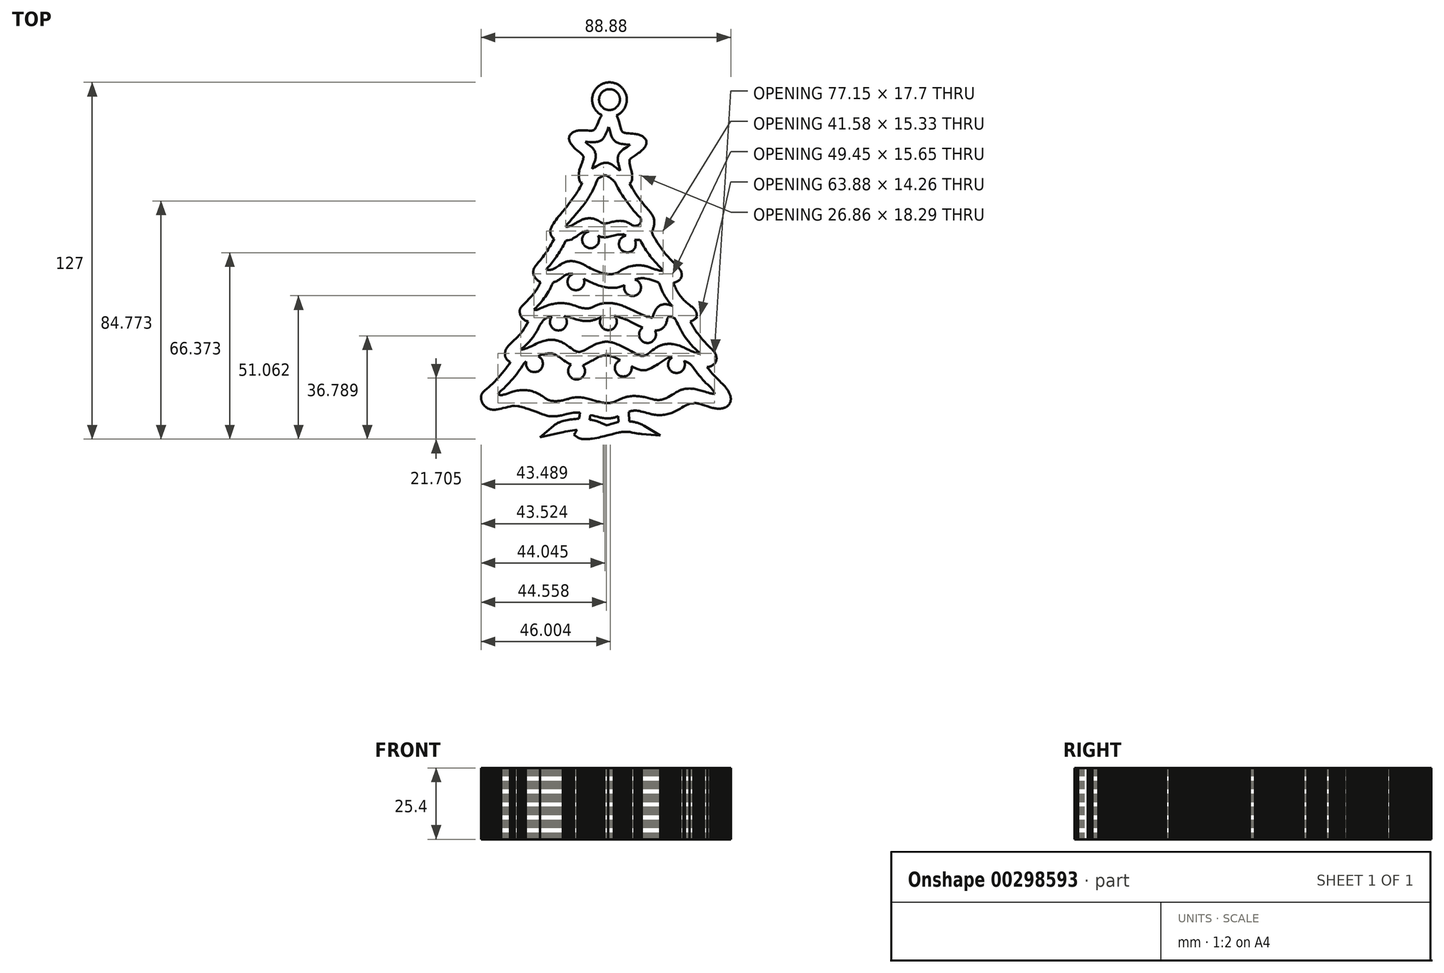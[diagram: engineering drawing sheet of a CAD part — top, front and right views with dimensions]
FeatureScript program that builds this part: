
annotation { "Feature Type Name" : "Feature", "Feature Type Description" : "" }
export const myFeature = defineFeature(function(context is Context, id is Id, definition is map)
    precondition{}
    {
        {
            var Q0;
            Q0=qCreatedBy(makeId("Top.planeOp"),FACE);
            var sketch = newSketch(context, id + "F0", { "sketchPlane" : qUnion([Q0])});
            skLineSegment(sketch, "E0", {"start": v(-10.31, -60.2) * mm, "end": v(-10.71, -60.23) * mm});
            skLineSegment(sketch, "E1", {"start": v(-10.71, -60.23) * mm, "end": v(-11.12, -60.26) * mm});
            skLineSegment(sketch, "E2", {"start": v(-11.12, -60.26) * mm, "end": v(-11.93, -60.35) * mm});
            skLineSegment(sketch, "E3", {"start": v(-11.93, -60.35) * mm, "end": v(-12.75, -60.48) * mm});
            skLineSegment(sketch, "E4", {"start": v(-12.75, -60.48) * mm, "end": v(-13.6, -60.62) * mm});
            skLineSegment(sketch, "E5", {"start": v(-13.6, -60.62) * mm, "end": v(-14.47, -60.8) * mm});
            skLineSegment(sketch, "E6", {"start": v(-14.47, -60.8) * mm, "end": v(-15.37, -60.98) * mm});
            skLineSegment(sketch, "E7", {"start": v(-15.37, -60.98) * mm, "end": v(-17.3, -61.4) * mm});
            skLineSegment(sketch, "E8", {"start": v(-17.3, -61.4) * mm, "end": v(-23.47, -62.8) * mm});
            skLineSegment(sketch, "E9", {"start": v(-23.47, -62.8) * mm, "end": v(-18.63, -58.71) * mm});
            skLineSegment(sketch, "E10", {"start": v(-18.63, -58.71) * mm, "end": v(-18.42, -58.54) * mm});
            skLineSegment(sketch, "E11", {"start": v(-18.42, -58.54) * mm, "end": v(-18.2, -58.38) * mm});
            skLineSegment(sketch, "E12", {"start": v(-18.2, -58.38) * mm, "end": v(-17.97, -58.22) * mm});
            skLineSegment(sketch, "E13", {"start": v(-17.97, -58.22) * mm, "end": v(-17.73, -58.07) * mm});
            skLineSegment(sketch, "E14", {"start": v(-17.73, -58.07) * mm, "end": v(-17.49, -57.93) * mm});
            skLineSegment(sketch, "E15", {"start": v(-17.49, -57.93) * mm, "end": v(-17.24, -57.8) * mm});
            skLineSegment(sketch, "E16", {"start": v(-17.24, -57.8) * mm, "end": v(-16.98, -57.67) * mm});
            skLineSegment(sketch, "E17", {"start": v(-16.98, -57.67) * mm, "end": v(-16.72, -57.55) * mm});
            skLineSegment(sketch, "E18", {"start": v(-16.72, -57.55) * mm, "end": v(-16.45, -57.44) * mm});
            skLineSegment(sketch, "E19", {"start": v(-16.45, -57.44) * mm, "end": v(-16.18, -57.33) * mm});
            skLineSegment(sketch, "E20", {"start": v(-16.18, -57.33) * mm, "end": v(-15.61, -57.14) * mm});
            skLineSegment(sketch, "E21", {"start": v(-15.61, -57.14) * mm, "end": v(-15.03, -56.96) * mm});
            skLineSegment(sketch, "E22", {"start": v(-15.03, -56.96) * mm, "end": v(-14.44, -56.82) * mm});
            skLineSegment(sketch, "E23", {"start": v(-14.44, -56.82) * mm, "end": v(-13.84, -56.69) * mm});
            skLineSegment(sketch, "E24", {"start": v(-13.84, -56.69) * mm, "end": v(-13.23, -56.58) * mm});
            skLineSegment(sketch, "E25", {"start": v(-13.23, -56.58) * mm, "end": v(-12.62, -56.49) * mm});
            skLineSegment(sketch, "E26", {"start": v(-12.62, -56.49) * mm, "end": v(-12, -56.41) * mm});
            skLineSegment(sketch, "E27", {"start": v(-12, -56.41) * mm, "end": v(-11.4, -56.35) * mm});
            skLineSegment(sketch, "E28", {"start": v(-11.4, -56.35) * mm, "end": v(-10.8, -56.3) * mm});
            skLineSegment(sketch, "E29", {"start": v(-10.8, -56.3) * mm, "end": v(-10.2, -56.27) * mm});
            skLineSegment(sketch, "E30", {"start": v(-10.2, -56.27) * mm, "end": v(-9.62, -56.25) * mm});
            skLineSegment(sketch, "E31", {"start": v(-9.62, -56.25) * mm, "end": v(-9.36, -55.07) * mm});
            skLineSegment(sketch, "E32", {"start": v(-9.36, -55.07) * mm, "end": v(-9.2, -54.1) * mm});
            skLineSegment(sketch, "E33", {"start": v(-9.2, -54.1) * mm, "end": v(-9.5, -54.06) * mm});
            skLineSegment(sketch, "E34", {"start": v(-9.5, -54.06) * mm, "end": v(-9.81, -54.04) * mm});
            skLineSegment(sketch, "E35", {"start": v(-9.81, -54.04) * mm, "end": v(-10.11, -54.02) * mm});
            skLineSegment(sketch, "E36", {"start": v(-10.11, -54.02) * mm, "end": v(-10.41, -54.02) * mm});
            skLineSegment(sketch, "E37", {"start": v(-10.41, -54.02) * mm, "end": v(-10.7, -54.02) * mm});
            skLineSegment(sketch, "E38", {"start": v(-10.7, -54.02) * mm, "end": v(-11, -54.03) * mm});
            skLineSegment(sketch, "E39", {"start": v(-11, -54.03) * mm, "end": v(-11.29, -54.06) * mm});
            skLineSegment(sketch, "E40", {"start": v(-11.29, -54.06) * mm, "end": v(-11.58, -54.09) * mm});
            skLineSegment(sketch, "E41", {"start": v(-11.58, -54.09) * mm, "end": v(-12.17, -54.17) * mm});
            skLineSegment(sketch, "E42", {"start": v(-12.17, -54.17) * mm, "end": v(-12.78, -54.29) * mm});
            skLineSegment(sketch, "E43", {"start": v(-12.78, -54.29) * mm, "end": v(-13.41, -54.44) * mm});
            skLineSegment(sketch, "E44", {"start": v(-13.41, -54.44) * mm, "end": v(-14.09, -54.6) * mm});
            skLineSegment(sketch, "E45", {"start": v(-14.09, -54.6) * mm, "end": v(-14.96, -54.83) * mm});
            skLineSegment(sketch, "E46", {"start": v(-14.96, -54.83) * mm, "end": v(-15.79, -55.03) * mm});
            skLineSegment(sketch, "E47", {"start": v(-15.79, -55.03) * mm, "end": v(-16.2, -55.1) * mm});
            skLineSegment(sketch, "E48", {"start": v(-16.2, -55.1) * mm, "end": v(-16.6, -55.18) * mm});
            skLineSegment(sketch, "E49", {"start": v(-16.6, -55.18) * mm, "end": v(-17, -55.25) * mm});
            skLineSegment(sketch, "E50", {"start": v(-17, -55.25) * mm, "end": v(-17.39, -55.3) * mm});
            skLineSegment(sketch, "E51", {"start": v(-17.39, -55.3) * mm, "end": v(-17.79, -55.34) * mm});
            skLineSegment(sketch, "E52", {"start": v(-17.79, -55.34) * mm, "end": v(-18.19, -55.37) * mm});
            skLineSegment(sketch, "E53", {"start": v(-18.19, -55.37) * mm, "end": v(-18.6, -55.38) * mm});
            skLineSegment(sketch, "E54", {"start": v(-18.6, -55.38) * mm, "end": v(-19.01, -55.38) * mm});
            skLineSegment(sketch, "E55", {"start": v(-19.01, -55.38) * mm, "end": v(-19.43, -55.37) * mm});
            skLineSegment(sketch, "E56", {"start": v(-19.43, -55.37) * mm, "end": v(-19.87, -55.34) * mm});
            skLineSegment(sketch, "E57", {"start": v(-19.87, -55.34) * mm, "end": v(-20.32, -55.3) * mm});
            skLineSegment(sketch, "E58", {"start": v(-20.32, -55.3) * mm, "end": v(-20.78, -55.24) * mm});
            skLineSegment(sketch, "E59", {"start": v(-20.78, -55.24) * mm, "end": v(-20.99, -55.2) * mm});
            skLineSegment(sketch, "E60", {"start": v(-20.99, -55.2) * mm, "end": v(-21.2, -55.13) * mm});
            skLineSegment(sketch, "E61", {"start": v(-21.2, -55.13) * mm, "end": v(-21.62, -54.98) * mm});
            skLineSegment(sketch, "E62", {"start": v(-21.62, -54.98) * mm, "end": v(-22.85, -54.52) * mm});
            skLineSegment(sketch, "E63", {"start": v(-22.85, -54.52) * mm, "end": v(-24.67, -53.85) * mm});
            skLineSegment(sketch, "E64", {"start": v(-24.67, -53.85) * mm, "end": v(-26.49, -53.2) * mm});
            skLineSegment(sketch, "E65", {"start": v(-26.49, -53.2) * mm, "end": v(-27.5, -52.83) * mm});
            skLineSegment(sketch, "E66", {"start": v(-27.5, -52.83) * mm, "end": v(-28.55, -52.48) * mm});
            skLineSegment(sketch, "E67", {"start": v(-28.55, -52.48) * mm, "end": v(-29.08, -52.3) * mm});
            skLineSegment(sketch, "E68", {"start": v(-29.08, -52.3) * mm, "end": v(-29.6, -52.14) * mm});
            skLineSegment(sketch, "E69", {"start": v(-29.6, -52.14) * mm, "end": v(-30.13, -52) * mm});
            skLineSegment(sketch, "E70", {"start": v(-30.13, -52) * mm, "end": v(-30.65, -51.85) * mm});
            skLineSegment(sketch, "E71", {"start": v(-30.65, -51.85) * mm, "end": v(-30.73, -51.83) * mm});
            skLineSegment(sketch, "E72", {"start": v(-30.73, -51.83) * mm, "end": v(-30.97, -51.78) * mm});
            skLineSegment(sketch, "E73", {"start": v(-30.97, -51.78) * mm, "end": v(-31.23, -51.73) * mm});
            skLineSegment(sketch, "E74", {"start": v(-31.23, -51.73) * mm, "end": v(-31.35, -51.76) * mm});
            skLineSegment(sketch, "E75", {"start": v(-31.35, -51.76) * mm, "end": v(-32.54, -51.6) * mm});
            skLineSegment(sketch, "E76", {"start": v(-32.54, -51.6) * mm, "end": v(-32.92, -51.64) * mm});
            skLineSegment(sketch, "E77", {"start": v(-32.92, -51.64) * mm, "end": v(-33.3, -51.7) * mm});
            skLineSegment(sketch, "E78", {"start": v(-33.3, -51.7) * mm, "end": v(-33.71, -51.78) * mm});
            skLineSegment(sketch, "E79", {"start": v(-33.71, -51.78) * mm, "end": v(-34.12, -51.86) * mm});
            skLineSegment(sketch, "E80", {"start": v(-34.12, -51.86) * mm, "end": v(-34.92, -52.05) * mm});
            skLineSegment(sketch, "E81", {"start": v(-34.92, -52.05) * mm, "end": v(-35.67, -52.22) * mm});
            skLineSegment(sketch, "E82", {"start": v(-35.67, -52.22) * mm, "end": v(-36.7, -52.47) * mm});
            skLineSegment(sketch, "E83", {"start": v(-36.7, -52.47) * mm, "end": v(-37.34, -52.62) * mm});
            skLineSegment(sketch, "E84", {"start": v(-37.34, -52.62) * mm, "end": v(-38.02, -52.77) * mm});
            skLineSegment(sketch, "E85", {"start": v(-38.02, -52.77) * mm, "end": v(-38.7, -52.9) * mm});
            skLineSegment(sketch, "E86", {"start": v(-38.7, -52.9) * mm, "end": v(-39.02, -52.95) * mm});
            skLineSegment(sketch, "E87", {"start": v(-39.02, -52.95) * mm, "end": v(-39.33, -53) * mm});
            skLineSegment(sketch, "E88", {"start": v(-39.33, -53) * mm, "end": v(-39.62, -53.03) * mm});
            skLineSegment(sketch, "E89", {"start": v(-39.62, -53.03) * mm, "end": v(-39.89, -53.04) * mm});
            skLineSegment(sketch, "E90", {"start": v(-39.89, -53.04) * mm, "end": v(-40.12, -53.04) * mm});
            skLineSegment(sketch, "E91", {"start": v(-40.12, -53.04) * mm, "end": v(-40.32, -53.02) * mm});
            skLineSegment(sketch, "E92", {"start": v(-40.32, -53.02) * mm, "end": v(-40.7, -52.95) * mm});
            skLineSegment(sketch, "E93", {"start": v(-40.7, -52.95) * mm, "end": v(-41.06, -52.86) * mm});
            skLineSegment(sketch, "E94", {"start": v(-41.06, -52.86) * mm, "end": v(-41.42, -52.75) * mm});
            skLineSegment(sketch, "E95", {"start": v(-41.42, -52.75) * mm, "end": v(-41.76, -52.63) * mm});
            skLineSegment(sketch, "E96", {"start": v(-41.76, -52.63) * mm, "end": v(-42.08, -52.48) * mm});
            skLineSegment(sketch, "E97", {"start": v(-42.08, -52.48) * mm, "end": v(-42.4, -52.31) * mm});
            skLineSegment(sketch, "E98", {"start": v(-42.4, -52.31) * mm, "end": v(-42.69, -52.13) * mm});
            skLineSegment(sketch, "E99", {"start": v(-42.69, -52.13) * mm, "end": v(-42.96, -51.92) * mm});
            skLineSegment(sketch, "E100", {"start": v(-42.96, -51.92) * mm, "end": v(-43.22, -51.7) * mm});
            skLineSegment(sketch, "E101", {"start": v(-43.22, -51.7) * mm, "end": v(-43.34, -51.57) * mm});
            skLineSegment(sketch, "E102", {"start": v(-43.34, -51.57) * mm, "end": v(-43.45, -51.44) * mm});
            skLineSegment(sketch, "E103", {"start": v(-43.45, -51.44) * mm, "end": v(-43.56, -51.31) * mm});
            skLineSegment(sketch, "E104", {"start": v(-43.56, -51.31) * mm, "end": v(-43.67, -51.17) * mm});
            skLineSegment(sketch, "E105", {"start": v(-43.67, -51.17) * mm, "end": v(-43.77, -51.03) * mm});
            skLineSegment(sketch, "E106", {"start": v(-43.77, -51.03) * mm, "end": v(-43.86, -50.88) * mm});
            skLineSegment(sketch, "E107", {"start": v(-43.86, -50.88) * mm, "end": v(-43.94, -50.72) * mm});
            skLineSegment(sketch, "E108", {"start": v(-43.94, -50.72) * mm, "end": v(-44.02, -50.56) * mm});
            skLineSegment(sketch, "E109", {"start": v(-44.02, -50.56) * mm, "end": v(-44.1, -50.4) * mm});
            skLineSegment(sketch, "E110", {"start": v(-44.1, -50.4) * mm, "end": v(-44.16, -50.22) * mm});
            skLineSegment(sketch, "E111", {"start": v(-44.16, -50.22) * mm, "end": v(-44.22, -50.04) * mm});
            skLineSegment(sketch, "E112", {"start": v(-44.22, -50.04) * mm, "end": v(-44.28, -49.86) * mm});
            skLineSegment(sketch, "E113", {"start": v(-44.28, -49.86) * mm, "end": v(-44.32, -49.67) * mm});
            skLineSegment(sketch, "E114", {"start": v(-44.32, -49.67) * mm, "end": v(-44.36, -49.47) * mm});
            skLineSegment(sketch, "E115", {"start": v(-44.36, -49.47) * mm, "end": v(-44.4, -49.25) * mm});
            skLineSegment(sketch, "E116", {"start": v(-44.4, -49.25) * mm, "end": v(-44.42, -49.04) * mm});
            skLineSegment(sketch, "E117", {"start": v(-44.42, -49.04) * mm, "end": v(-44.44, -48.84) * mm});
            skLineSegment(sketch, "E118", {"start": v(-44.44, -48.84) * mm, "end": v(-44.44, -48.65) * mm});
            skLineSegment(sketch, "E119", {"start": v(-44.44, -48.65) * mm, "end": v(-44.44, -48.47) * mm});
            skLineSegment(sketch, "E120", {"start": v(-44.44, -48.47) * mm, "end": v(-44.43, -48.3) * mm});
            skLineSegment(sketch, "E121", {"start": v(-44.43, -48.3) * mm, "end": v(-44.4, -48.13) * mm});
            skLineSegment(sketch, "E122", {"start": v(-44.4, -48.13) * mm, "end": v(-44.38, -47.98) * mm});
            skLineSegment(sketch, "E123", {"start": v(-44.38, -47.98) * mm, "end": v(-44.34, -47.83) * mm});
            skLineSegment(sketch, "E124", {"start": v(-44.34, -47.83) * mm, "end": v(-44.3, -47.69) * mm});
            skLineSegment(sketch, "E125", {"start": v(-44.3, -47.69) * mm, "end": v(-44.25, -47.55) * mm});
            skLineSegment(sketch, "E126", {"start": v(-44.25, -47.55) * mm, "end": v(-44.19, -47.42) * mm});
            skLineSegment(sketch, "E127", {"start": v(-44.19, -47.42) * mm, "end": v(-44.12, -47.3) * mm});
            skLineSegment(sketch, "E128", {"start": v(-44.12, -47.3) * mm, "end": v(-44.05, -47.18) * mm});
            skLineSegment(sketch, "E129", {"start": v(-44.05, -47.18) * mm, "end": v(-43.89, -46.95) * mm});
            skLineSegment(sketch, "E130", {"start": v(-43.89, -46.95) * mm, "end": v(-43.7, -46.73) * mm});
            skLineSegment(sketch, "E131", {"start": v(-43.7, -46.73) * mm, "end": v(-43.5, -46.52) * mm});
            skLineSegment(sketch, "E132", {"start": v(-43.5, -46.52) * mm, "end": v(-43.27, -46.31) * mm});
            skLineSegment(sketch, "E133", {"start": v(-43.27, -46.31) * mm, "end": v(-43.03, -46.1) * mm});
            skLineSegment(sketch, "E134", {"start": v(-43.03, -46.1) * mm, "end": v(-42.5, -45.67) * mm});
            skLineSegment(sketch, "E135", {"start": v(-42.5, -45.67) * mm, "end": v(-42.23, -45.43) * mm});
            skLineSegment(sketch, "E136", {"start": v(-42.23, -45.43) * mm, "end": v(-41.94, -45.18) * mm});
            skLineSegment(sketch, "E137", {"start": v(-41.94, -45.18) * mm, "end": v(-41.17, -44.45) * mm});
            skLineSegment(sketch, "E138", {"start": v(-41.17, -44.45) * mm, "end": v(-40.4, -43.7) * mm});
            skLineSegment(sketch, "E139", {"start": v(-40.4, -43.7) * mm, "end": v(-39.64, -42.96) * mm});
            skLineSegment(sketch, "E140", {"start": v(-39.64, -42.96) * mm, "end": v(-38.9, -42.2) * mm});
            skLineSegment(sketch, "E141", {"start": v(-38.9, -42.2) * mm, "end": v(-38.22, -41.47) * mm});
            skLineSegment(sketch, "E142", {"start": v(-38.22, -41.47) * mm, "end": v(-37.56, -40.73) * mm});
            skLineSegment(sketch, "E143", {"start": v(-37.56, -40.73) * mm, "end": v(-36.92, -39.98) * mm});
            skLineSegment(sketch, "E144", {"start": v(-36.92, -39.98) * mm, "end": v(-36.3, -39.22) * mm});
            skLineSegment(sketch, "E145", {"start": v(-36.3, -39.22) * mm, "end": v(-35.7, -38.45) * mm});
            skLineSegment(sketch, "E146", {"start": v(-35.7, -38.45) * mm, "end": v(-35.1, -37.67) * mm});
            skLineSegment(sketch, "E147", {"start": v(-35.1, -37.67) * mm, "end": v(-34.53, -36.88) * mm});
            skLineSegment(sketch, "E148", {"start": v(-34.53, -36.88) * mm, "end": v(-33.96, -36.07) * mm});
            skLineSegment(sketch, "E149", {"start": v(-33.96, -36.07) * mm, "end": v(-34.16, -35.98) * mm});
            skLineSegment(sketch, "E150", {"start": v(-34.16, -35.98) * mm, "end": v(-34.34, -35.9) * mm});
            skLineSegment(sketch, "E151", {"start": v(-34.34, -35.9) * mm, "end": v(-34.52, -35.8) * mm});
            skLineSegment(sketch, "E152", {"start": v(-34.52, -35.8) * mm, "end": v(-34.68, -35.68) * mm});
            skLineSegment(sketch, "E153", {"start": v(-34.68, -35.68) * mm, "end": v(-34.84, -35.57) * mm});
            skLineSegment(sketch, "E154", {"start": v(-34.84, -35.57) * mm, "end": v(-34.98, -35.45) * mm});
            skLineSegment(sketch, "E155", {"start": v(-34.98, -35.45) * mm, "end": v(-35.12, -35.32) * mm});
            skLineSegment(sketch, "E156", {"start": v(-35.12, -35.32) * mm, "end": v(-35.24, -35.2) * mm});
            skLineSegment(sketch, "E157", {"start": v(-35.24, -35.2) * mm, "end": v(-35.35, -35.05) * mm});
            skLineSegment(sketch, "E158", {"start": v(-35.35, -35.05) * mm, "end": v(-35.46, -34.91) * mm});
            skLineSegment(sketch, "E159", {"start": v(-35.46, -34.91) * mm, "end": v(-35.55, -34.76) * mm});
            skLineSegment(sketch, "E160", {"start": v(-35.55, -34.76) * mm, "end": v(-35.64, -34.61) * mm});
            skLineSegment(sketch, "E161", {"start": v(-35.64, -34.61) * mm, "end": v(-35.71, -34.46) * mm});
            skLineSegment(sketch, "E162", {"start": v(-35.71, -34.46) * mm, "end": v(-35.78, -34.3) * mm});
            skLineSegment(sketch, "E163", {"start": v(-35.78, -34.3) * mm, "end": v(-35.83, -34.13) * mm});
            skLineSegment(sketch, "E164", {"start": v(-35.83, -34.13) * mm, "end": v(-35.88, -33.96) * mm});
            skLineSegment(sketch, "E165", {"start": v(-35.88, -33.96) * mm, "end": v(-35.91, -33.8) * mm});
            skLineSegment(sketch, "E166", {"start": v(-35.91, -33.8) * mm, "end": v(-35.94, -33.62) * mm});
            skLineSegment(sketch, "E167", {"start": v(-35.94, -33.62) * mm, "end": v(-35.95, -33.44) * mm});
            skLineSegment(sketch, "E168", {"start": v(-35.95, -33.44) * mm, "end": v(-35.96, -33.26) * mm});
            skLineSegment(sketch, "E169", {"start": v(-35.96, -33.26) * mm, "end": v(-35.96, -33.08) * mm});
            skLineSegment(sketch, "E170", {"start": v(-35.96, -33.08) * mm, "end": v(-35.94, -32.9) * mm});
            skLineSegment(sketch, "E171", {"start": v(-35.94, -32.9) * mm, "end": v(-35.92, -32.7) * mm});
            skLineSegment(sketch, "E172", {"start": v(-35.92, -32.7) * mm, "end": v(-35.89, -32.52) * mm});
            skLineSegment(sketch, "E173", {"start": v(-35.89, -32.52) * mm, "end": v(-35.85, -32.33) * mm});
            skLineSegment(sketch, "E174", {"start": v(-35.85, -32.33) * mm, "end": v(-35.8, -32.14) * mm});
            skLineSegment(sketch, "E175", {"start": v(-35.8, -32.14) * mm, "end": v(-35.73, -31.95) * mm});
            skLineSegment(sketch, "E176", {"start": v(-35.73, -31.95) * mm, "end": v(-35.66, -31.76) * mm});
            skLineSegment(sketch, "E177", {"start": v(-35.66, -31.76) * mm, "end": v(-35.58, -31.57) * mm});
            skLineSegment(sketch, "E178", {"start": v(-35.58, -31.57) * mm, "end": v(-35.5, -31.38) * mm});
            skLineSegment(sketch, "E179", {"start": v(-35.5, -31.38) * mm, "end": v(-35.4, -31.19) * mm});
            skLineSegment(sketch, "E180", {"start": v(-35.4, -31.19) * mm, "end": v(-35.28, -31) * mm});
            skLineSegment(sketch, "E181", {"start": v(-35.28, -31) * mm, "end": v(-35.19, -30.85) * mm});
            skLineSegment(sketch, "E182", {"start": v(-35.19, -30.85) * mm, "end": v(-35.07, -30.69) * mm});
            skLineSegment(sketch, "E183", {"start": v(-35.07, -30.69) * mm, "end": v(-34.8, -30.36) * mm});
            skLineSegment(sketch, "E184", {"start": v(-34.8, -30.36) * mm, "end": v(-34.5, -30.02) * mm});
            skLineSegment(sketch, "E185", {"start": v(-34.5, -30.02) * mm, "end": v(-34.17, -29.68) * mm});
            skLineSegment(sketch, "E186", {"start": v(-34.17, -29.68) * mm, "end": v(-33.49, -29.02) * mm});
            skLineSegment(sketch, "E187", {"start": v(-33.49, -29.02) * mm, "end": v(-32.9, -28.46) * mm});
            skLineSegment(sketch, "E188", {"start": v(-32.9, -28.46) * mm, "end": v(-31.9, -27.52) * mm});
            skLineSegment(sketch, "E189", {"start": v(-31.9, -27.52) * mm, "end": v(-31.4, -27.04) * mm});
            skLineSegment(sketch, "E190", {"start": v(-31.4, -27.04) * mm, "end": v(-30.9, -26.56) * mm});
            skLineSegment(sketch, "E191", {"start": v(-30.9, -26.56) * mm, "end": v(-30.61, -26.24) * mm});
            skLineSegment(sketch, "E192", {"start": v(-30.61, -26.24) * mm, "end": v(-30.32, -25.87) * mm});
            skLineSegment(sketch, "E193", {"start": v(-30.32, -25.87) * mm, "end": v(-30.02, -25.48) * mm});
            skLineSegment(sketch, "E194", {"start": v(-30.02, -25.48) * mm, "end": v(-29.73, -25.07) * mm});
            skLineSegment(sketch, "E195", {"start": v(-29.73, -25.07) * mm, "end": v(-29.19, -24.23) * mm});
            skLineSegment(sketch, "E196", {"start": v(-29.19, -24.23) * mm, "end": v(-28.7, -23.46) * mm});
            skLineSegment(sketch, "E197", {"start": v(-28.7, -23.46) * mm, "end": v(-28.16, -22.56) * mm});
            skLineSegment(sketch, "E198", {"start": v(-28.16, -22.56) * mm, "end": v(-27.61, -21.63) * mm});
            skLineSegment(sketch, "E199", {"start": v(-27.61, -21.63) * mm, "end": v(-27.88, -21.55) * mm});
            skLineSegment(sketch, "E200", {"start": v(-27.88, -21.55) * mm, "end": v(-28.14, -21.46) * mm});
            skLineSegment(sketch, "E201", {"start": v(-28.14, -21.46) * mm, "end": v(-28.4, -21.36) * mm});
            skLineSegment(sketch, "E202", {"start": v(-28.4, -21.36) * mm, "end": v(-28.64, -21.25) * mm});
            skLineSegment(sketch, "E203", {"start": v(-28.64, -21.25) * mm, "end": v(-28.89, -21.12) * mm});
            skLineSegment(sketch, "E204", {"start": v(-28.89, -21.12) * mm, "end": v(-29.13, -20.97) * mm});
            skLineSegment(sketch, "E205", {"start": v(-29.13, -20.97) * mm, "end": v(-29.36, -20.8) * mm});
            skLineSegment(sketch, "E206", {"start": v(-29.36, -20.8) * mm, "end": v(-29.58, -20.62) * mm});
            skLineSegment(sketch, "E207", {"start": v(-29.58, -20.62) * mm, "end": v(-29.74, -20.47) * mm});
            skLineSegment(sketch, "E208", {"start": v(-29.74, -20.47) * mm, "end": v(-29.88, -20.31) * mm});
            skLineSegment(sketch, "E209", {"start": v(-29.88, -20.31) * mm, "end": v(-30, -20.15) * mm});
            skLineSegment(sketch, "E210", {"start": v(-30, -20.15) * mm, "end": v(-30.12, -19.98) * mm});
            skLineSegment(sketch, "E211", {"start": v(-30.12, -19.98) * mm, "end": v(-30.23, -19.8) * mm});
            skLineSegment(sketch, "E212", {"start": v(-30.23, -19.8) * mm, "end": v(-30.32, -19.63) * mm});
            skLineSegment(sketch, "E213", {"start": v(-30.32, -19.63) * mm, "end": v(-30.4, -19.45) * mm});
            skLineSegment(sketch, "E214", {"start": v(-30.4, -19.45) * mm, "end": v(-30.47, -19.26) * mm});
            skLineSegment(sketch, "E215", {"start": v(-30.47, -19.26) * mm, "end": v(-30.53, -19.07) * mm});
            skLineSegment(sketch, "E216", {"start": v(-30.53, -19.07) * mm, "end": v(-30.58, -18.87) * mm});
            skLineSegment(sketch, "E217", {"start": v(-30.58, -18.87) * mm, "end": v(-30.62, -18.67) * mm});
            skLineSegment(sketch, "E218", {"start": v(-30.62, -18.67) * mm, "end": v(-30.65, -18.47) * mm});
            skLineSegment(sketch, "E219", {"start": v(-30.65, -18.47) * mm, "end": v(-30.67, -18.27) * mm});
            skLineSegment(sketch, "E220", {"start": v(-30.67, -18.27) * mm, "end": v(-30.68, -18.06) * mm});
            skLineSegment(sketch, "E221", {"start": v(-30.68, -18.06) * mm, "end": v(-30.68, -17.85) * mm});
            skLineSegment(sketch, "E222", {"start": v(-30.68, -17.85) * mm, "end": v(-30.68, -17.64) * mm});
            skLineSegment(sketch, "E223", {"start": v(-30.68, -17.64) * mm, "end": v(-30.67, -17.49) * mm});
            skLineSegment(sketch, "E224", {"start": v(-30.67, -17.49) * mm, "end": v(-30.63, -17.34) * mm});
            skLineSegment(sketch, "E225", {"start": v(-30.63, -17.34) * mm, "end": v(-30.6, -17.2) * mm});
            skLineSegment(sketch, "E226", {"start": v(-30.6, -17.2) * mm, "end": v(-30.54, -17.07) * mm});
            skLineSegment(sketch, "E227", {"start": v(-30.54, -17.07) * mm, "end": v(-30.48, -16.94) * mm});
            skLineSegment(sketch, "E228", {"start": v(-30.48, -16.94) * mm, "end": v(-30.4, -16.81) * mm});
            skLineSegment(sketch, "E229", {"start": v(-30.4, -16.81) * mm, "end": v(-30.23, -16.56) * mm});
            skLineSegment(sketch, "E230", {"start": v(-30.23, -16.56) * mm, "end": v(-30.03, -16.31) * mm});
            skLineSegment(sketch, "E231", {"start": v(-30.03, -16.31) * mm, "end": v(-29.82, -16.08) * mm});
            skLineSegment(sketch, "E232", {"start": v(-29.82, -16.08) * mm, "end": v(-29.6, -15.85) * mm});
            skLineSegment(sketch, "E233", {"start": v(-29.6, -15.85) * mm, "end": v(-29.18, -15.44) * mm});
            skLineSegment(sketch, "E234", {"start": v(-29.18, -15.44) * mm, "end": v(-28.62, -14.88) * mm});
            skLineSegment(sketch, "E235", {"start": v(-28.62, -14.88) * mm, "end": v(-28.07, -14.3) * mm});
            skLineSegment(sketch, "E236", {"start": v(-28.07, -14.3) * mm, "end": v(-27.52, -13.73) * mm});
            skLineSegment(sketch, "E237", {"start": v(-27.52, -13.73) * mm, "end": v(-26.98, -13.15) * mm});
            skLineSegment(sketch, "E238", {"start": v(-26.98, -13.15) * mm, "end": v(-26.44, -12.52) * mm});
            skLineSegment(sketch, "E239", {"start": v(-26.44, -12.52) * mm, "end": v(-25.9, -11.88) * mm});
            skLineSegment(sketch, "E240", {"start": v(-25.9, -11.88) * mm, "end": v(-25.4, -11.21) * mm});
            skLineSegment(sketch, "E241", {"start": v(-25.4, -11.21) * mm, "end": v(-25.14, -10.87) * mm});
            skLineSegment(sketch, "E242", {"start": v(-25.14, -10.87) * mm, "end": v(-24.9, -10.53) * mm});
            skLineSegment(sketch, "E243", {"start": v(-24.9, -10.53) * mm, "end": v(-24.66, -10.18) * mm});
            skLineSegment(sketch, "E244", {"start": v(-24.66, -10.18) * mm, "end": v(-24.43, -9.83) * mm});
            skLineSegment(sketch, "E245", {"start": v(-24.43, -9.83) * mm, "end": v(-24.21, -9.47) * mm});
            skLineSegment(sketch, "E246", {"start": v(-24.21, -9.47) * mm, "end": v(-24, -9.1) * mm});
            skLineSegment(sketch, "E247", {"start": v(-24, -9.1) * mm, "end": v(-23.8, -8.74) * mm});
            skLineSegment(sketch, "E248", {"start": v(-23.8, -8.74) * mm, "end": v(-23.6, -8.37) * mm});
            skLineSegment(sketch, "E249", {"start": v(-23.6, -8.37) * mm, "end": v(-23.4, -8) * mm});
            skLineSegment(sketch, "E250", {"start": v(-23.4, -8) * mm, "end": v(-23.23, -7.62) * mm});
            skLineSegment(sketch, "E251", {"start": v(-23.23, -7.62) * mm, "end": v(-23.44, -7.53) * mm});
            skLineSegment(sketch, "E252", {"start": v(-23.44, -7.53) * mm, "end": v(-23.64, -7.43) * mm});
            skLineSegment(sketch, "E253", {"start": v(-23.64, -7.43) * mm, "end": v(-23.83, -7.32) * mm});
            skLineSegment(sketch, "E254", {"start": v(-23.83, -7.32) * mm, "end": v(-24.02, -7.2) * mm});
            skLineSegment(sketch, "E255", {"start": v(-24.02, -7.2) * mm, "end": v(-24.2, -7.07) * mm});
            skLineSegment(sketch, "E256", {"start": v(-24.2, -7.07) * mm, "end": v(-24.37, -6.93) * mm});
            skLineSegment(sketch, "E257", {"start": v(-24.37, -6.93) * mm, "end": v(-24.55, -6.77) * mm});
            skLineSegment(sketch, "E258", {"start": v(-24.55, -6.77) * mm, "end": v(-24.72, -6.6) * mm});
            skLineSegment(sketch, "E259", {"start": v(-24.72, -6.6) * mm, "end": v(-24.97, -6.33) * mm});
            skLineSegment(sketch, "E260", {"start": v(-24.97, -6.33) * mm, "end": v(-25.2, -6.04) * mm});
            skLineSegment(sketch, "E261", {"start": v(-25.2, -6.04) * mm, "end": v(-25.3, -5.89) * mm});
            skLineSegment(sketch, "E262", {"start": v(-25.3, -5.89) * mm, "end": v(-25.4, -5.73) * mm});
            skLineSegment(sketch, "E263", {"start": v(-25.4, -5.73) * mm, "end": v(-25.5, -5.57) * mm});
            skLineSegment(sketch, "E264", {"start": v(-25.5, -5.57) * mm, "end": v(-25.58, -5.41) * mm});
            skLineSegment(sketch, "E265", {"start": v(-25.58, -5.41) * mm, "end": v(-25.65, -5.25) * mm});
            skLineSegment(sketch, "E266", {"start": v(-25.65, -5.25) * mm, "end": v(-25.72, -5.08) * mm});
            skLineSegment(sketch, "E267", {"start": v(-25.72, -5.08) * mm, "end": v(-25.77, -4.9) * mm});
            skLineSegment(sketch, "E268", {"start": v(-25.77, -4.9) * mm, "end": v(-25.81, -4.73) * mm});
            skLineSegment(sketch, "E269", {"start": v(-25.81, -4.73) * mm, "end": v(-25.85, -4.54) * mm});
            skLineSegment(sketch, "E270", {"start": v(-25.85, -4.54) * mm, "end": v(-25.87, -4.36) * mm});
            skLineSegment(sketch, "E271", {"start": v(-25.87, -4.36) * mm, "end": v(-25.88, -4.17) * mm});
            skLineSegment(sketch, "E272", {"start": v(-25.88, -4.17) * mm, "end": v(-25.88, -3.98) * mm});
            skLineSegment(sketch, "E273", {"start": v(-25.88, -3.98) * mm, "end": v(-25.87, -3.77) * mm});
            skLineSegment(sketch, "E274", {"start": v(-25.87, -3.77) * mm, "end": v(-25.84, -3.57) * mm});
            skLineSegment(sketch, "E275", {"start": v(-25.84, -3.57) * mm, "end": v(-25.8, -3.37) * mm});
            skLineSegment(sketch, "E276", {"start": v(-25.8, -3.37) * mm, "end": v(-25.75, -3.18) * mm});
            skLineSegment(sketch, "E277", {"start": v(-25.75, -3.18) * mm, "end": v(-25.69, -2.99) * mm});
            skLineSegment(sketch, "E278", {"start": v(-25.69, -2.99) * mm, "end": v(-25.61, -2.8) * mm});
            skLineSegment(sketch, "E279", {"start": v(-25.61, -2.8) * mm, "end": v(-25.53, -2.62) * mm});
            skLineSegment(sketch, "E280", {"start": v(-25.53, -2.62) * mm, "end": v(-25.44, -2.44) * mm});
            skLineSegment(sketch, "E281", {"start": v(-25.44, -2.44) * mm, "end": v(-25.23, -2.1) * mm});
            skLineSegment(sketch, "E282", {"start": v(-25.23, -2.1) * mm, "end": v(-25, -1.76) * mm});
            skLineSegment(sketch, "E283", {"start": v(-25, -1.76) * mm, "end": v(-24.76, -1.44) * mm});
            skLineSegment(sketch, "E284", {"start": v(-24.76, -1.44) * mm, "end": v(-24.5, -1.12) * mm});
            skLineSegment(sketch, "E285", {"start": v(-24.5, -1.12) * mm, "end": v(-23.98, -0.5) * mm});
            skLineSegment(sketch, "E286", {"start": v(-23.98, -0.5) * mm, "end": v(-23.45, 0.1) * mm});
            skLineSegment(sketch, "E287", {"start": v(-23.45, 0.1) * mm, "end": v(-22.93, 0.72) * mm});
            skLineSegment(sketch, "E288", {"start": v(-22.93, 0.72) * mm, "end": v(-22.68, 1.03) * mm});
            skLineSegment(sketch, "E289", {"start": v(-22.68, 1.03) * mm, "end": v(-22.44, 1.36) * mm});
            skLineSegment(sketch, "E290", {"start": v(-22.44, 1.36) * mm, "end": v(-22.05, 1.9) * mm});
            skLineSegment(sketch, "E291", {"start": v(-22.05, 1.9) * mm, "end": v(-21.67, 2.43) * mm});
            skLineSegment(sketch, "E292", {"start": v(-21.67, 2.43) * mm, "end": v(-21.3, 2.97) * mm});
            skLineSegment(sketch, "E293", {"start": v(-21.3, 2.97) * mm, "end": v(-20.94, 3.5) * mm});
            skLineSegment(sketch, "E294", {"start": v(-20.94, 3.5) * mm, "end": v(-20.58, 4.06) * mm});
            skLineSegment(sketch, "E295", {"start": v(-20.58, 4.06) * mm, "end": v(-20.24, 4.61) * mm});
            skLineSegment(sketch, "E296", {"start": v(-20.24, 4.61) * mm, "end": v(-19.9, 5.17) * mm});
            skLineSegment(sketch, "E297", {"start": v(-19.9, 5.17) * mm, "end": v(-19.57, 5.75) * mm});
            skLineSegment(sketch, "E298", {"start": v(-19.57, 5.75) * mm, "end": v(-18.99, 6.8) * mm});
            skLineSegment(sketch, "E299", {"start": v(-18.99, 6.8) * mm, "end": v(-18.4, 7.83) * mm});
            skLineSegment(sketch, "E300", {"start": v(-18.4, 7.83) * mm, "end": v(-18.61, 7.98) * mm});
            skLineSegment(sketch, "E301", {"start": v(-18.61, 7.98) * mm, "end": v(-18.83, 8.15) * mm});
            skLineSegment(sketch, "E302", {"start": v(-18.83, 8.15) * mm, "end": v(-18.96, 8.28) * mm});
            skLineSegment(sketch, "E303", {"start": v(-18.96, 8.28) * mm, "end": v(-19.1, 8.41) * mm});
            skLineSegment(sketch, "E304", {"start": v(-19.1, 8.41) * mm, "end": v(-19.2, 8.55) * mm});
            skLineSegment(sketch, "E305", {"start": v(-19.2, 8.55) * mm, "end": v(-19.3, 8.7) * mm});
            skLineSegment(sketch, "E306", {"start": v(-19.3, 8.7) * mm, "end": v(-19.4, 8.85) * mm});
            skLineSegment(sketch, "E307", {"start": v(-19.4, 8.85) * mm, "end": v(-19.48, 9) * mm});
            skLineSegment(sketch, "E308", {"start": v(-19.48, 9) * mm, "end": v(-19.55, 9.16) * mm});
            skLineSegment(sketch, "E309", {"start": v(-19.55, 9.16) * mm, "end": v(-19.61, 9.32) * mm});
            skLineSegment(sketch, "E310", {"start": v(-19.61, 9.32) * mm, "end": v(-19.66, 9.5) * mm});
            skLineSegment(sketch, "E311", {"start": v(-19.66, 9.5) * mm, "end": v(-19.7, 9.66) * mm});
            skLineSegment(sketch, "E312", {"start": v(-19.7, 9.66) * mm, "end": v(-19.73, 9.83) * mm});
            skLineSegment(sketch, "E313", {"start": v(-19.73, 9.83) * mm, "end": v(-19.76, 10.01) * mm});
            skLineSegment(sketch, "E314", {"start": v(-19.76, 10.01) * mm, "end": v(-19.77, 10.19) * mm});
            skLineSegment(sketch, "E315", {"start": v(-19.77, 10.19) * mm, "end": v(-19.78, 10.37) * mm});
            skLineSegment(sketch, "E316", {"start": v(-19.78, 10.37) * mm, "end": v(-19.76, 10.74) * mm});
            skLineSegment(sketch, "E317", {"start": v(-19.76, 10.74) * mm, "end": v(-19.74, 10.95) * mm});
            skLineSegment(sketch, "E318", {"start": v(-19.74, 10.95) * mm, "end": v(-19.69, 11.17) * mm});
            skLineSegment(sketch, "E319", {"start": v(-19.69, 11.17) * mm, "end": v(-19.62, 11.4) * mm});
            skLineSegment(sketch, "E320", {"start": v(-19.62, 11.4) * mm, "end": v(-19.53, 11.65) * mm});
            skLineSegment(sketch, "E321", {"start": v(-19.53, 11.65) * mm, "end": v(-19.42, 11.9) * mm});
            skLineSegment(sketch, "E322", {"start": v(-19.42, 11.9) * mm, "end": v(-19.3, 12.17) * mm});
            skLineSegment(sketch, "E323", {"start": v(-19.3, 12.17) * mm, "end": v(-19.15, 12.45) * mm});
            skLineSegment(sketch, "E324", {"start": v(-19.15, 12.45) * mm, "end": v(-19, 12.73) * mm});
            skLineSegment(sketch, "E325", {"start": v(-19, 12.73) * mm, "end": v(-18.64, 13.3) * mm});
            skLineSegment(sketch, "E326", {"start": v(-18.64, 13.3) * mm, "end": v(-18.25, 13.9) * mm});
            skLineSegment(sketch, "E327", {"start": v(-18.25, 13.9) * mm, "end": v(-17.81, 14.52) * mm});
            skLineSegment(sketch, "E328", {"start": v(-17.81, 14.52) * mm, "end": v(-17.35, 15.13) * mm});
            skLineSegment(sketch, "E329", {"start": v(-17.35, 15.13) * mm, "end": v(-16.88, 15.74) * mm});
            skLineSegment(sketch, "E330", {"start": v(-16.88, 15.74) * mm, "end": v(-16.4, 16.34) * mm});
            skLineSegment(sketch, "E331", {"start": v(-16.4, 16.34) * mm, "end": v(-15.47, 17.47) * mm});
            skLineSegment(sketch, "E332", {"start": v(-15.47, 17.47) * mm, "end": v(-14.63, 18.47) * mm});
            skLineSegment(sketch, "E333", {"start": v(-14.63, 18.47) * mm, "end": v(-13.97, 19.27) * mm});
            skLineSegment(sketch, "E334", {"start": v(-13.97, 19.27) * mm, "end": v(-13.16, 20.3) * mm});
            skLineSegment(sketch, "E335", {"start": v(-13.16, 20.3) * mm, "end": v(-12.38, 21.32) * mm});
            skLineSegment(sketch, "E336", {"start": v(-12.38, 21.32) * mm, "end": v(-11.62, 22.34) * mm});
            skLineSegment(sketch, "E337", {"start": v(-11.62, 22.34) * mm, "end": v(-11.25, 22.85) * mm});
            skLineSegment(sketch, "E338", {"start": v(-11.25, 22.85) * mm, "end": v(-10.9, 23.37) * mm});
            skLineSegment(sketch, "E339", {"start": v(-10.9, 23.37) * mm, "end": v(-10.55, 23.89) * mm});
            skLineSegment(sketch, "E340", {"start": v(-10.55, 23.89) * mm, "end": v(-10.21, 24.41) * mm});
            skLineSegment(sketch, "E341", {"start": v(-10.21, 24.41) * mm, "end": v(-9.89, 24.94) * mm});
            skLineSegment(sketch, "E342", {"start": v(-9.89, 24.94) * mm, "end": v(-9.57, 25.48) * mm});
            skLineSegment(sketch, "E343", {"start": v(-9.57, 25.48) * mm, "end": v(-9.26, 26.03) * mm});
            skLineSegment(sketch, "E344", {"start": v(-9.26, 26.03) * mm, "end": v(-8.97, 26.59) * mm});
            skLineSegment(sketch, "E345", {"start": v(-8.97, 26.59) * mm, "end": v(-8.7, 27.16) * mm});
            skLineSegment(sketch, "E346", {"start": v(-8.7, 27.16) * mm, "end": v(-8.42, 27.74) * mm});
            skLineSegment(sketch, "E347", {"start": v(-8.42, 27.74) * mm, "end": v(-9.16, 27.8) * mm});
            skLineSegment(sketch, "E348", {"start": v(-9.16, 27.8) * mm, "end": v(-9.46, 28.81) * mm});
            skLineSegment(sketch, "E349", {"start": v(-9.46, 28.81) * mm, "end": v(-9.53, 29.08) * mm});
            skLineSegment(sketch, "E350", {"start": v(-9.53, 29.08) * mm, "end": v(-9.6, 29.36) * mm});
            skLineSegment(sketch, "E351", {"start": v(-9.6, 29.36) * mm, "end": v(-9.64, 29.63) * mm});
            skLineSegment(sketch, "E352", {"start": v(-9.64, 29.63) * mm, "end": v(-9.67, 29.9) * mm});
            skLineSegment(sketch, "E353", {"start": v(-9.67, 29.9) * mm, "end": v(-9.68, 30.14) * mm});
            skLineSegment(sketch, "E354", {"start": v(-9.68, 30.14) * mm, "end": v(-9.69, 30.38) * mm});
            skLineSegment(sketch, "E355", {"start": v(-9.69, 30.38) * mm, "end": v(-9.68, 30.62) * mm});
            skLineSegment(sketch, "E356", {"start": v(-9.68, 30.62) * mm, "end": v(-9.67, 30.85) * mm});
            skLineSegment(sketch, "E357", {"start": v(-9.67, 30.85) * mm, "end": v(-9.62, 31.32) * mm});
            skLineSegment(sketch, "E358", {"start": v(-9.62, 31.32) * mm, "end": v(-9.54, 31.78) * mm});
            skLineSegment(sketch, "E359", {"start": v(-9.54, 31.78) * mm, "end": v(-9.44, 32.24) * mm});
            skLineSegment(sketch, "E360", {"start": v(-9.44, 32.24) * mm, "end": v(-9.31, 32.7) * mm});
            skLineSegment(sketch, "E361", {"start": v(-9.31, 32.7) * mm, "end": v(-9.17, 33.15) * mm});
            skLineSegment(sketch, "E362", {"start": v(-9.17, 33.15) * mm, "end": v(-9.02, 33.6) * mm});
            skLineSegment(sketch, "E363", {"start": v(-9.02, 33.6) * mm, "end": v(-8.72, 34.37) * mm});
            skLineSegment(sketch, "E364", {"start": v(-8.72, 34.37) * mm, "end": v(-8.52, 34.9) * mm});
            skLineSegment(sketch, "E365", {"start": v(-8.52, 34.9) * mm, "end": v(-8.33, 35.46) * mm});
            skLineSegment(sketch, "E366", {"start": v(-8.33, 35.46) * mm, "end": v(-8.24, 35.74) * mm});
            skLineSegment(sketch, "E367", {"start": v(-8.24, 35.74) * mm, "end": v(-8.16, 36.02) * mm});
            skLineSegment(sketch, "E368", {"start": v(-8.16, 36.02) * mm, "end": v(-8.1, 36.3) * mm});
            skLineSegment(sketch, "E369", {"start": v(-8.1, 36.3) * mm, "end": v(-8.05, 36.54) * mm});
            skLineSegment(sketch, "E370", {"start": v(-8.05, 36.54) * mm, "end": v(-8.03, 36.78) * mm});
            skLineSegment(sketch, "E371", {"start": v(-8.03, 36.78) * mm, "end": v(-8.03, 36.99) * mm});
            skLineSegment(sketch, "E372", {"start": v(-8.03, 36.99) * mm, "end": v(-8.04, 37.08) * mm});
            skLineSegment(sketch, "E373", {"start": v(-8.04, 37.08) * mm, "end": v(-8.05, 37.17) * mm});
            skLineSegment(sketch, "E374", {"start": v(-8.05, 37.17) * mm, "end": v(-8.08, 37.24) * mm});
            skLineSegment(sketch, "E375", {"start": v(-8.08, 37.24) * mm, "end": v(-8.1, 37.31) * mm});
            skLineSegment(sketch, "E376", {"start": v(-8.1, 37.31) * mm, "end": v(-8.17, 37.4) * mm});
            skLineSegment(sketch, "E377", {"start": v(-8.17, 37.4) * mm, "end": v(-8.26, 37.52) * mm});
            skLineSegment(sketch, "E378", {"start": v(-8.26, 37.52) * mm, "end": v(-8.5, 37.78) * mm});
            skLineSegment(sketch, "E379", {"start": v(-8.5, 37.78) * mm, "end": v(-8.8, 38.06) * mm});
            skLineSegment(sketch, "E380", {"start": v(-8.8, 38.06) * mm, "end": v(-9.13, 38.36) * mm});
            skLineSegment(sketch, "E381", {"start": v(-9.13, 38.36) * mm, "end": v(-9.8, 38.93) * mm});
            skLineSegment(sketch, "E382", {"start": v(-9.8, 38.93) * mm, "end": v(-10.29, 39.35) * mm});
            skLineSegment(sketch, "E383", {"start": v(-10.29, 39.35) * mm, "end": v(-10.83, 39.83) * mm});
            skLineSegment(sketch, "E384", {"start": v(-10.83, 39.83) * mm, "end": v(-11.11, 40.1) * mm});
            skLineSegment(sketch, "E385", {"start": v(-11.11, 40.1) * mm, "end": v(-11.4, 40.37) * mm});
            skLineSegment(sketch, "E386", {"start": v(-11.4, 40.37) * mm, "end": v(-11.68, 40.65) * mm});
            skLineSegment(sketch, "E387", {"start": v(-11.68, 40.65) * mm, "end": v(-11.95, 40.95) * mm});
            skLineSegment(sketch, "E388", {"start": v(-11.95, 40.95) * mm, "end": v(-12.2, 41.27) * mm});
            skLineSegment(sketch, "E389", {"start": v(-12.2, 41.27) * mm, "end": v(-12.44, 41.59) * mm});
            skLineSegment(sketch, "E390", {"start": v(-12.44, 41.59) * mm, "end": v(-12.65, 41.92) * mm});
            skLineSegment(sketch, "E391", {"start": v(-12.65, 41.92) * mm, "end": v(-12.74, 42.09) * mm});
            skLineSegment(sketch, "E392", {"start": v(-12.74, 42.09) * mm, "end": v(-12.83, 42.26) * mm});
            skLineSegment(sketch, "E393", {"start": v(-12.83, 42.26) * mm, "end": v(-12.9, 42.44) * mm});
            skLineSegment(sketch, "E394", {"start": v(-12.9, 42.44) * mm, "end": v(-12.97, 42.61) * mm});
            skLineSegment(sketch, "E395", {"start": v(-12.97, 42.61) * mm, "end": v(-13.03, 42.79) * mm});
            skLineSegment(sketch, "E396", {"start": v(-13.03, 42.79) * mm, "end": v(-13.07, 42.97) * mm});
            skLineSegment(sketch, "E397", {"start": v(-13.07, 42.97) * mm, "end": v(-13.1, 43.15) * mm});
            skLineSegment(sketch, "E398", {"start": v(-13.1, 43.15) * mm, "end": v(-13.13, 43.33) * mm});
            skLineSegment(sketch, "E399", {"start": v(-13.13, 43.33) * mm, "end": v(-13.14, 43.52) * mm});
            skLineSegment(sketch, "E400", {"start": v(-13.14, 43.52) * mm, "end": v(-13.13, 43.7) * mm});
            skLineSegment(sketch, "E401", {"start": v(-13.13, 43.7) * mm, "end": v(-13.1, 43.9) * mm});
            skLineSegment(sketch, "E402", {"start": v(-13.1, 43.9) * mm, "end": v(-13.07, 44.08) * mm});
            skLineSegment(sketch, "E403", {"start": v(-13.07, 44.08) * mm, "end": v(-13.02, 44.27) * mm});
            skLineSegment(sketch, "E404", {"start": v(-13.02, 44.27) * mm, "end": v(-12.96, 44.46) * mm});
            skLineSegment(sketch, "E405", {"start": v(-12.96, 44.46) * mm, "end": v(-12.86, 44.7) * mm});
            skLineSegment(sketch, "E406", {"start": v(-12.86, 44.7) * mm, "end": v(-12.7, 44.9) * mm});
            skLineSegment(sketch, "E407", {"start": v(-12.7, 44.9) * mm, "end": v(-12.57, 45.04) * mm});
            skLineSegment(sketch, "E408", {"start": v(-12.57, 45.04) * mm, "end": v(-12.45, 45.16) * mm});
            skLineSegment(sketch, "E409", {"start": v(-12.45, 45.16) * mm, "end": v(-12.2, 45.4) * mm});
            skLineSegment(sketch, "E410", {"start": v(-12.2, 45.4) * mm, "end": v(-11.92, 45.6) * mm});
            skLineSegment(sketch, "E411", {"start": v(-11.92, 45.6) * mm, "end": v(-11.64, 45.77) * mm});
            skLineSegment(sketch, "E412", {"start": v(-11.64, 45.77) * mm, "end": v(-11.35, 45.92) * mm});
            skLineSegment(sketch, "E413", {"start": v(-11.35, 45.92) * mm, "end": v(-11.05, 46.05) * mm});
            skLineSegment(sketch, "E414", {"start": v(-11.05, 46.05) * mm, "end": v(-10.74, 46.15) * mm});
            skLineSegment(sketch, "E415", {"start": v(-10.74, 46.15) * mm, "end": v(-10.42, 46.24) * mm});
            skLineSegment(sketch, "E416", {"start": v(-10.42, 46.24) * mm, "end": v(-10.1, 46.3) * mm});
            skLineSegment(sketch, "E417", {"start": v(-10.1, 46.3) * mm, "end": v(-9.78, 46.36) * mm});
            skLineSegment(sketch, "E418", {"start": v(-9.78, 46.36) * mm, "end": v(-9.45, 46.4) * mm});
            skLineSegment(sketch, "E419", {"start": v(-9.45, 46.4) * mm, "end": v(-9.12, 46.42) * mm});
            skLineSegment(sketch, "E420", {"start": v(-9.12, 46.42) * mm, "end": v(-8.78, 46.43) * mm});
            skLineSegment(sketch, "E421", {"start": v(-8.78, 46.43) * mm, "end": v(-8.45, 46.44) * mm});
            skLineSegment(sketch, "E422", {"start": v(-8.45, 46.44) * mm, "end": v(-7.8, 46.42) * mm});
            skLineSegment(sketch, "E423", {"start": v(-7.8, 46.42) * mm, "end": v(-7.16, 46.39) * mm});
            skLineSegment(sketch, "E424", {"start": v(-7.16, 46.39) * mm, "end": v(-6.55, 46.34) * mm});
            skLineSegment(sketch, "E425", {"start": v(-6.55, 46.34) * mm, "end": v(-5.98, 46.3) * mm});
            skLineSegment(sketch, "E426", {"start": v(-5.98, 46.3) * mm, "end": v(-5.46, 46.3) * mm});
            skLineSegment(sketch, "E427", {"start": v(-5.46, 46.3) * mm, "end": v(-5.22, 46.3) * mm});
            skLineSegment(sketch, "E428", {"start": v(-5.22, 46.3) * mm, "end": v(-5, 46.31) * mm});
            skLineSegment(sketch, "E429", {"start": v(-5, 46.31) * mm, "end": v(-4.79, 46.34) * mm});
            skLineSegment(sketch, "E430", {"start": v(-4.79, 46.34) * mm, "end": v(-4.6, 46.38) * mm});
            skLineSegment(sketch, "E431", {"start": v(-4.6, 46.38) * mm, "end": v(-4.43, 46.43) * mm});
            skLineSegment(sketch, "E432", {"start": v(-4.43, 46.43) * mm, "end": v(-4.28, 46.5) * mm});
            skLineSegment(sketch, "E433", {"start": v(-4.28, 46.5) * mm, "end": v(-4.15, 46.6) * mm});
            skLineSegment(sketch, "E434", {"start": v(-4.15, 46.6) * mm, "end": v(-4.1, 46.65) * mm});
            skLineSegment(sketch, "E435", {"start": v(-4.1, 46.65) * mm, "end": v(-4.05, 46.7) * mm});
            skLineSegment(sketch, "E436", {"start": v(-4.05, 46.7) * mm, "end": v(-3.93, 46.86) * mm});
            skLineSegment(sketch, "E437", {"start": v(-3.93, 46.86) * mm, "end": v(-3.82, 47.04) * mm});
            skLineSegment(sketch, "E438", {"start": v(-3.82, 47.04) * mm, "end": v(-3.6, 47.42) * mm});
            skLineSegment(sketch, "E439", {"start": v(-3.6, 47.42) * mm, "end": v(-3.39, 47.83) * mm});
            skLineSegment(sketch, "E440", {"start": v(-3.39, 47.83) * mm, "end": v(-3.19, 48.26) * mm});
            skLineSegment(sketch, "E441", {"start": v(-3.19, 48.26) * mm, "end": v(-2.82, 49.14) * mm});
            skLineSegment(sketch, "E442", {"start": v(-2.82, 49.14) * mm, "end": v(-2.49, 49.93) * mm});
            skLineSegment(sketch, "E443", {"start": v(-2.49, 49.93) * mm, "end": v(-2.27, 50.43) * mm});
            skLineSegment(sketch, "E444", {"start": v(-2.27, 50.43) * mm, "end": v(-2.05, 50.92) * mm});
            skLineSegment(sketch, "E445", {"start": v(-2.05, 50.92) * mm, "end": v(-1.93, 51.16) * mm});
            skLineSegment(sketch, "E446", {"start": v(-1.93, 51.16) * mm, "end": v(-1.8, 51.4) * mm});
            skLineSegment(sketch, "E447", {"start": v(-1.8, 51.4) * mm, "end": v(-1.68, 51.63) * mm});
            skLineSegment(sketch, "E448", {"start": v(-1.68, 51.63) * mm, "end": v(-1.53, 51.86) * mm});
            skLineSegment(sketch, "E449", {"start": v(-1.53, 51.86) * mm, "end": v(-1.9, 52.06) * mm});
            skLineSegment(sketch, "E450", {"start": v(-1.9, 52.06) * mm, "end": v(-2.25, 52.28) * mm});
            skLineSegment(sketch, "E451", {"start": v(-2.25, 52.28) * mm, "end": v(-2.59, 52.53) * mm});
            skLineSegment(sketch, "E452", {"start": v(-2.59, 52.53) * mm, "end": v(-2.9, 52.8) * mm});
            skLineSegment(sketch, "E453", {"start": v(-2.9, 52.8) * mm, "end": v(-3.2, 53.1) * mm});
            skLineSegment(sketch, "E454", {"start": v(-3.2, 53.1) * mm, "end": v(-3.48, 53.4) * mm});
            skLineSegment(sketch, "E455", {"start": v(-3.48, 53.4) * mm, "end": v(-3.73, 53.74) * mm});
            skLineSegment(sketch, "E456", {"start": v(-3.73, 53.74) * mm, "end": v(-3.97, 54.08) * mm});
            skLineSegment(sketch, "E457", {"start": v(-3.97, 54.08) * mm, "end": v(-4.18, 54.45) * mm});
            skLineSegment(sketch, "E458", {"start": v(-4.18, 54.45) * mm, "end": v(-4.36, 54.82) * mm});
            skLineSegment(sketch, "E459", {"start": v(-4.36, 54.82) * mm, "end": v(-4.52, 55.21) * mm});
            skLineSegment(sketch, "E460", {"start": v(-4.52, 55.21) * mm, "end": v(-4.66, 55.62) * mm});
            skLineSegment(sketch, "E461", {"start": v(-4.66, 55.62) * mm, "end": v(-4.76, 56.04) * mm});
            skLineSegment(sketch, "E462", {"start": v(-4.76, 56.04) * mm, "end": v(-4.8, 56.25) * mm});
            skLineSegment(sketch, "E463", {"start": v(-4.8, 56.25) * mm, "end": v(-4.84, 56.46) * mm});
            skLineSegment(sketch, "E464", {"start": v(-4.84, 56.46) * mm, "end": v(-4.87, 56.68) * mm});
            skLineSegment(sketch, "E465", {"start": v(-4.87, 56.68) * mm, "end": v(-4.89, 56.9) * mm});
            skLineSegment(sketch, "E466", {"start": v(-4.89, 56.9) * mm, "end": v(-4.9, 57.12) * mm});
            skLineSegment(sketch, "E467", {"start": v(-4.9, 57.12) * mm, "end": v(-4.9, 57.35) * mm});
            skLineSegment(sketch, "E468", {"start": v(-4.9, 57.35) * mm, "end": v(-4.9, 57.66) * mm});
            skLineSegment(sketch, "E469", {"start": v(-4.9, 57.66) * mm, "end": v(-4.87, 57.98) * mm});
            skLineSegment(sketch, "E470", {"start": v(-4.87, 57.98) * mm, "end": v(-4.83, 58.28) * mm});
            skLineSegment(sketch, "E471", {"start": v(-4.83, 58.28) * mm, "end": v(-4.78, 58.59) * mm});
            skLineSegment(sketch, "E472", {"start": v(-4.78, 58.59) * mm, "end": v(-4.7, 58.88) * mm});
            skLineSegment(sketch, "E473", {"start": v(-4.7, 58.88) * mm, "end": v(-4.63, 59.18) * mm});
            skLineSegment(sketch, "E474", {"start": v(-4.63, 59.18) * mm, "end": v(-4.53, 59.46) * mm});
            skLineSegment(sketch, "E475", {"start": v(-4.53, 59.46) * mm, "end": v(-4.42, 59.74) * mm});
            skLineSegment(sketch, "E476", {"start": v(-4.42, 59.74) * mm, "end": v(-4.3, 60.01) * mm});
            skLineSegment(sketch, "E477", {"start": v(-4.3, 60.01) * mm, "end": v(-4.16, 60.28) * mm});
            skLineSegment(sketch, "E478", {"start": v(-4.16, 60.28) * mm, "end": v(-4.01, 60.54) * mm});
            skLineSegment(sketch, "E479", {"start": v(-4.01, 60.54) * mm, "end": v(-3.85, 60.79) * mm});
            skLineSegment(sketch, "E480", {"start": v(-3.85, 60.79) * mm, "end": v(-3.68, 61.03) * mm});
            skLineSegment(sketch, "E481", {"start": v(-3.68, 61.03) * mm, "end": v(-3.5, 61.26) * mm});
            skLineSegment(sketch, "E482", {"start": v(-3.5, 61.26) * mm, "end": v(-3.3, 61.48) * mm});
            skLineSegment(sketch, "E483", {"start": v(-3.3, 61.48) * mm, "end": v(-3.1, 61.7) * mm});
            skLineSegment(sketch, "E484", {"start": v(-3.1, 61.7) * mm, "end": v(-2.89, 61.9) * mm});
            skLineSegment(sketch, "E485", {"start": v(-2.89, 61.9) * mm, "end": v(-2.66, 62.1) * mm});
            skLineSegment(sketch, "E486", {"start": v(-2.66, 62.1) * mm, "end": v(-2.43, 62.28) * mm});
            skLineSegment(sketch, "E487", {"start": v(-2.43, 62.28) * mm, "end": v(-2.19, 62.45) * mm});
            skLineSegment(sketch, "E488", {"start": v(-2.19, 62.45) * mm, "end": v(-1.94, 62.6) * mm});
            skLineSegment(sketch, "E489", {"start": v(-1.94, 62.6) * mm, "end": v(-1.68, 62.76) * mm});
            skLineSegment(sketch, "E490", {"start": v(-1.68, 62.76) * mm, "end": v(-1.42, 62.9) * mm});
            skLineSegment(sketch, "E491", {"start": v(-1.42, 62.9) * mm, "end": v(-1.14, 63.02) * mm});
            skLineSegment(sketch, "E492", {"start": v(-1.14, 63.02) * mm, "end": v(-0.86, 63.13) * mm});
            skLineSegment(sketch, "E493", {"start": v(-0.86, 63.13) * mm, "end": v(-0.58, 63.22) * mm});
            skLineSegment(sketch, "E494", {"start": v(-0.58, 63.22) * mm, "end": v(-0.29, 63.3) * mm});
            skLineSegment(sketch, "E495", {"start": v(-0.29, 63.3) * mm, "end": v(0.01, 63.37) * mm});
            skLineSegment(sketch, "E496", {"start": v(0.01, 63.37) * mm, "end": v(0.31, 63.43) * mm});
            skLineSegment(sketch, "E497", {"start": v(0.31, 63.43) * mm, "end": v(0.62, 63.47) * mm});
            skLineSegment(sketch, "E498", {"start": v(0.62, 63.47) * mm, "end": v(0.93, 63.5) * mm});
            skLineSegment(sketch, "E499", {"start": v(0.93, 63.5) * mm, "end": v(1.25, 63.5) * mm});
            skLineSegment(sketch, "E500", {"start": v(1.25, 63.5) * mm, "end": v(1.57, 63.5) * mm});
            skLineSegment(sketch, "E501", {"start": v(1.57, 63.5) * mm, "end": v(1.88, 63.47) * mm});
            skLineSegment(sketch, "E502", {"start": v(1.88, 63.47) * mm, "end": v(2.19, 63.43) * mm});
            skLineSegment(sketch, "E503", {"start": v(2.19, 63.43) * mm, "end": v(2.5, 63.37) * mm});
            skLineSegment(sketch, "E504", {"start": v(2.5, 63.37) * mm, "end": v(2.79, 63.3) * mm});
            skLineSegment(sketch, "E505", {"start": v(2.79, 63.3) * mm, "end": v(3.08, 63.22) * mm});
            skLineSegment(sketch, "E506", {"start": v(3.08, 63.22) * mm, "end": v(3.37, 63.13) * mm});
            skLineSegment(sketch, "E507", {"start": v(3.37, 63.13) * mm, "end": v(3.65, 63.02) * mm});
            skLineSegment(sketch, "E508", {"start": v(3.65, 63.02) * mm, "end": v(3.92, 62.9) * mm});
            skLineSegment(sketch, "E509", {"start": v(3.92, 62.9) * mm, "end": v(4.18, 62.76) * mm});
            skLineSegment(sketch, "E510", {"start": v(4.18, 62.76) * mm, "end": v(4.44, 62.6) * mm});
            skLineSegment(sketch, "E511", {"start": v(4.44, 62.6) * mm, "end": v(4.7, 62.45) * mm});
            skLineSegment(sketch, "E512", {"start": v(4.7, 62.45) * mm, "end": v(4.93, 62.28) * mm});
            skLineSegment(sketch, "E513", {"start": v(4.93, 62.28) * mm, "end": v(5.17, 62.1) * mm});
            skLineSegment(sketch, "E514", {"start": v(5.17, 62.1) * mm, "end": v(5.39, 61.9) * mm});
            skLineSegment(sketch, "E515", {"start": v(5.39, 61.9) * mm, "end": v(5.6, 61.7) * mm});
            skLineSegment(sketch, "E516", {"start": v(5.6, 61.7) * mm, "end": v(5.8, 61.48) * mm});
            skLineSegment(sketch, "E517", {"start": v(5.8, 61.48) * mm, "end": v(6, 61.26) * mm});
            skLineSegment(sketch, "E518", {"start": v(6, 61.26) * mm, "end": v(6.18, 61.03) * mm});
            skLineSegment(sketch, "E519", {"start": v(6.18, 61.03) * mm, "end": v(6.35, 60.79) * mm});
            skLineSegment(sketch, "E520", {"start": v(6.35, 60.79) * mm, "end": v(6.51, 60.54) * mm});
            skLineSegment(sketch, "E521", {"start": v(6.51, 60.54) * mm, "end": v(6.66, 60.28) * mm});
            skLineSegment(sketch, "E522", {"start": v(6.66, 60.28) * mm, "end": v(6.8, 60.01) * mm});
            skLineSegment(sketch, "E523", {"start": v(6.8, 60.01) * mm, "end": v(6.92, 59.74) * mm});
            skLineSegment(sketch, "E524", {"start": v(6.92, 59.74) * mm, "end": v(7.03, 59.46) * mm});
            skLineSegment(sketch, "E525", {"start": v(7.03, 59.46) * mm, "end": v(7.13, 59.18) * mm});
            skLineSegment(sketch, "E526", {"start": v(7.13, 59.18) * mm, "end": v(7.21, 58.88) * mm});
            skLineSegment(sketch, "E527", {"start": v(7.21, 58.88) * mm, "end": v(7.28, 58.59) * mm});
            skLineSegment(sketch, "E528", {"start": v(7.28, 58.59) * mm, "end": v(7.33, 58.28) * mm});
            skLineSegment(sketch, "E529", {"start": v(7.33, 58.28) * mm, "end": v(7.37, 57.98) * mm});
            skLineSegment(sketch, "E530", {"start": v(7.37, 57.98) * mm, "end": v(7.4, 57.66) * mm});
            skLineSegment(sketch, "E531", {"start": v(7.4, 57.66) * mm, "end": v(7.4, 57.35) * mm});
            skLineSegment(sketch, "E532", {"start": v(7.4, 57.35) * mm, "end": v(7.4, 57.11) * mm});
            skLineSegment(sketch, "E533", {"start": v(7.4, 57.11) * mm, "end": v(7.39, 56.88) * mm});
            skLineSegment(sketch, "E534", {"start": v(7.39, 56.88) * mm, "end": v(7.37, 56.65) * mm});
            skLineSegment(sketch, "E535", {"start": v(7.37, 56.65) * mm, "end": v(7.34, 56.42) * mm});
            skLineSegment(sketch, "E536", {"start": v(7.34, 56.42) * mm, "end": v(7.3, 56.2) * mm});
            skLineSegment(sketch, "E537", {"start": v(7.3, 56.2) * mm, "end": v(7.25, 55.98) * mm});
            skLineSegment(sketch, "E538", {"start": v(7.25, 55.98) * mm, "end": v(7.2, 55.76) * mm});
            skLineSegment(sketch, "E539", {"start": v(7.2, 55.76) * mm, "end": v(7.14, 55.54) * mm});
            skLineSegment(sketch, "E540", {"start": v(7.14, 55.54) * mm, "end": v(7.07, 55.33) * mm});
            skLineSegment(sketch, "E541", {"start": v(7.07, 55.33) * mm, "end": v(6.99, 55.12) * mm});
            skLineSegment(sketch, "E542", {"start": v(6.99, 55.12) * mm, "end": v(6.9, 54.91) * mm});
            skLineSegment(sketch, "E543", {"start": v(6.9, 54.91) * mm, "end": v(6.81, 54.71) * mm});
            skLineSegment(sketch, "E544", {"start": v(6.81, 54.71) * mm, "end": v(6.72, 54.52) * mm});
            skLineSegment(sketch, "E545", {"start": v(6.72, 54.52) * mm, "end": v(6.61, 54.32) * mm});
            skLineSegment(sketch, "E546", {"start": v(6.61, 54.32) * mm, "end": v(6.5, 54.13) * mm});
            skLineSegment(sketch, "E547", {"start": v(6.5, 54.13) * mm, "end": v(6.38, 53.95) * mm});
            skLineSegment(sketch, "E548", {"start": v(6.38, 53.95) * mm, "end": v(6.26, 53.77) * mm});
            skLineSegment(sketch, "E549", {"start": v(6.26, 53.77) * mm, "end": v(6.13, 53.6) * mm});
            skLineSegment(sketch, "E550", {"start": v(6.13, 53.6) * mm, "end": v(6, 53.42) * mm});
            skLineSegment(sketch, "E551", {"start": v(6, 53.42) * mm, "end": v(5.85, 53.26) * mm});
            skLineSegment(sketch, "E552", {"start": v(5.85, 53.26) * mm, "end": v(5.7, 53.1) * mm});
            skLineSegment(sketch, "E553", {"start": v(5.7, 53.1) * mm, "end": v(5.55, 52.94) * mm});
            skLineSegment(sketch, "E554", {"start": v(5.55, 52.94) * mm, "end": v(5.39, 52.8) * mm});
            skLineSegment(sketch, "E555", {"start": v(5.39, 52.8) * mm, "end": v(5.22, 52.65) * mm});
            skLineSegment(sketch, "E556", {"start": v(5.22, 52.65) * mm, "end": v(5.05, 52.5) * mm});
            skLineSegment(sketch, "E557", {"start": v(5.05, 52.5) * mm, "end": v(4.88, 52.38) * mm});
            skLineSegment(sketch, "E558", {"start": v(4.88, 52.38) * mm, "end": v(4.7, 52.25) * mm});
            skLineSegment(sketch, "E559", {"start": v(4.7, 52.25) * mm, "end": v(4.52, 52.13) * mm});
            skLineSegment(sketch, "E560", {"start": v(4.52, 52.13) * mm, "end": v(4.33, 52.02) * mm});
            skLineSegment(sketch, "E561", {"start": v(4.33, 52.02) * mm, "end": v(4.14, 51.9) * mm});
            skLineSegment(sketch, "E562", {"start": v(4.14, 51.9) * mm, "end": v(3.94, 51.8) * mm});
            skLineSegment(sketch, "E563", {"start": v(3.94, 51.8) * mm, "end": v(3.74, 51.72) * mm});
            skLineSegment(sketch, "E564", {"start": v(3.74, 51.72) * mm, "end": v(3.92, 51.4) * mm});
            skLineSegment(sketch, "E565", {"start": v(3.92, 51.4) * mm, "end": v(4.07, 51.08) * mm});
            skLineSegment(sketch, "E566", {"start": v(4.07, 51.08) * mm, "end": v(4.21, 50.76) * mm});
            skLineSegment(sketch, "E567", {"start": v(4.21, 50.76) * mm, "end": v(4.34, 50.42) * mm});
            skLineSegment(sketch, "E568", {"start": v(4.34, 50.42) * mm, "end": v(4.58, 49.69) * mm});
            skLineSegment(sketch, "E569", {"start": v(4.58, 49.69) * mm, "end": v(4.82, 48.86) * mm});
            skLineSegment(sketch, "E570", {"start": v(4.82, 48.86) * mm, "end": v(5, 48.19) * mm});
            skLineSegment(sketch, "E571", {"start": v(5, 48.19) * mm, "end": v(5.12, 47.75) * mm});
            skLineSegment(sketch, "E572", {"start": v(5.12, 47.75) * mm, "end": v(5.24, 47.3) * mm});
            skLineSegment(sketch, "E573", {"start": v(5.24, 47.3) * mm, "end": v(5.39, 46.85) * mm});
            skLineSegment(sketch, "E574", {"start": v(5.39, 46.85) * mm, "end": v(5.54, 46.45) * mm});
            skLineSegment(sketch, "E575", {"start": v(5.54, 46.45) * mm, "end": v(5.62, 46.27) * mm});
            skLineSegment(sketch, "E576", {"start": v(5.62, 46.27) * mm, "end": v(5.7, 46.11) * mm});
            skLineSegment(sketch, "E577", {"start": v(5.7, 46.11) * mm, "end": v(5.78, 45.98) * mm});
            skLineSegment(sketch, "E578", {"start": v(5.78, 45.98) * mm, "end": v(5.86, 45.89) * mm});
            skLineSegment(sketch, "E579", {"start": v(5.86, 45.89) * mm, "end": v(5.97, 45.8) * mm});
            skLineSegment(sketch, "E580", {"start": v(5.97, 45.8) * mm, "end": v(6.1, 45.73) * mm});
            skLineSegment(sketch, "E581", {"start": v(6.1, 45.73) * mm, "end": v(6.25, 45.66) * mm});
            skLineSegment(sketch, "E582", {"start": v(6.25, 45.66) * mm, "end": v(6.43, 45.6) * mm});
            skLineSegment(sketch, "E583", {"start": v(6.43, 45.6) * mm, "end": v(6.63, 45.55) * mm});
            skLineSegment(sketch, "E584", {"start": v(6.63, 45.55) * mm, "end": v(6.84, 45.5) * mm});
            skLineSegment(sketch, "E585", {"start": v(6.84, 45.5) * mm, "end": v(7.28, 45.43) * mm});
            skLineSegment(sketch, "E586", {"start": v(7.28, 45.43) * mm, "end": v(7.73, 45.38) * mm});
            skLineSegment(sketch, "E587", {"start": v(7.73, 45.38) * mm, "end": v(8.16, 45.34) * mm});
            skLineSegment(sketch, "E588", {"start": v(8.16, 45.34) * mm, "end": v(8.82, 45.29) * mm});
            skLineSegment(sketch, "E589", {"start": v(8.82, 45.29) * mm, "end": v(9.52, 45.23) * mm});
            skLineSegment(sketch, "E590", {"start": v(9.52, 45.23) * mm, "end": v(10.24, 45.16) * mm});
            skLineSegment(sketch, "E591", {"start": v(10.24, 45.16) * mm, "end": v(10.6, 45.1) * mm});
            skLineSegment(sketch, "E592", {"start": v(10.6, 45.1) * mm, "end": v(10.96, 45.05) * mm});
            skLineSegment(sketch, "E593", {"start": v(10.96, 45.05) * mm, "end": v(11.31, 44.98) * mm});
            skLineSegment(sketch, "E594", {"start": v(11.31, 44.98) * mm, "end": v(11.66, 44.89) * mm});
            skLineSegment(sketch, "E595", {"start": v(11.66, 44.89) * mm, "end": v(12, 44.78) * mm});
            skLineSegment(sketch, "E596", {"start": v(12, 44.78) * mm, "end": v(12.34, 44.65) * mm});
            skLineSegment(sketch, "E597", {"start": v(12.34, 44.65) * mm, "end": v(12.66, 44.5) * mm});
            skLineSegment(sketch, "E598", {"start": v(12.66, 44.5) * mm, "end": v(12.97, 44.34) * mm});
            skLineSegment(sketch, "E599", {"start": v(12.97, 44.34) * mm, "end": v(13.12, 44.24) * mm});
            skLineSegment(sketch, "E600", {"start": v(13.12, 44.24) * mm, "end": v(13.26, 44.14) * mm});
            skLineSegment(sketch, "E601", {"start": v(13.26, 44.14) * mm, "end": v(13.4, 44.03) * mm});
            skLineSegment(sketch, "E602", {"start": v(13.4, 44.03) * mm, "end": v(13.54, 43.92) * mm});
            skLineSegment(sketch, "E603", {"start": v(13.54, 43.92) * mm, "end": v(13.67, 43.8) * mm});
            skLineSegment(sketch, "E604", {"start": v(13.67, 43.8) * mm, "end": v(13.8, 43.66) * mm});
            skLineSegment(sketch, "E605", {"start": v(13.8, 43.66) * mm, "end": v(13.92, 43.53) * mm});
            skLineSegment(sketch, "E606", {"start": v(13.92, 43.53) * mm, "end": v(14.03, 43.38) * mm});
            skLineSegment(sketch, "E607", {"start": v(14.03, 43.38) * mm, "end": v(14.17, 43.19) * mm});
            skLineSegment(sketch, "E608", {"start": v(14.17, 43.19) * mm, "end": v(14.25, 42.96) * mm});
            skLineSegment(sketch, "E609", {"start": v(14.25, 42.96) * mm, "end": v(14.32, 42.75) * mm});
            skLineSegment(sketch, "E610", {"start": v(14.32, 42.75) * mm, "end": v(14.36, 42.55) * mm});
            skLineSegment(sketch, "E611", {"start": v(14.36, 42.55) * mm, "end": v(14.39, 42.35) * mm});
            skLineSegment(sketch, "E612", {"start": v(14.39, 42.35) * mm, "end": v(14.4, 42.15) * mm});
            skLineSegment(sketch, "E613", {"start": v(14.4, 42.15) * mm, "end": v(14.4, 41.95) * mm});
            skLineSegment(sketch, "E614", {"start": v(14.4, 41.95) * mm, "end": v(14.37, 41.76) * mm});
            skLineSegment(sketch, "E615", {"start": v(14.37, 41.76) * mm, "end": v(14.34, 41.57) * mm});
            skLineSegment(sketch, "E616", {"start": v(14.34, 41.57) * mm, "end": v(14.29, 41.38) * mm});
            skLineSegment(sketch, "E617", {"start": v(14.29, 41.38) * mm, "end": v(14.22, 41.2) * mm});
            skLineSegment(sketch, "E618", {"start": v(14.22, 41.2) * mm, "end": v(14.15, 41.02) * mm});
            skLineSegment(sketch, "E619", {"start": v(14.15, 41.02) * mm, "end": v(14.06, 40.84) * mm});
            skLineSegment(sketch, "E620", {"start": v(14.06, 40.84) * mm, "end": v(13.96, 40.66) * mm});
            skLineSegment(sketch, "E621", {"start": v(13.96, 40.66) * mm, "end": v(13.86, 40.5) * mm});
            skLineSegment(sketch, "E622", {"start": v(13.86, 40.5) * mm, "end": v(13.74, 40.33) * mm});
            skLineSegment(sketch, "E623", {"start": v(13.74, 40.33) * mm, "end": v(13.61, 40.16) * mm});
            skLineSegment(sketch, "E624", {"start": v(13.61, 40.16) * mm, "end": v(13.48, 40) * mm});
            skLineSegment(sketch, "E625", {"start": v(13.48, 40) * mm, "end": v(13.2, 39.69) * mm});
            skLineSegment(sketch, "E626", {"start": v(13.2, 39.69) * mm, "end": v(12.89, 39.39) * mm});
            skLineSegment(sketch, "E627", {"start": v(12.89, 39.39) * mm, "end": v(12.56, 39.1) * mm});
            skLineSegment(sketch, "E628", {"start": v(12.56, 39.1) * mm, "end": v(12.23, 38.84) * mm});
            skLineSegment(sketch, "E629", {"start": v(12.23, 38.84) * mm, "end": v(11.9, 38.58) * mm});
            skLineSegment(sketch, "E630", {"start": v(11.9, 38.58) * mm, "end": v(11.57, 38.34) * mm});
            skLineSegment(sketch, "E631", {"start": v(11.57, 38.34) * mm, "end": v(10.95, 37.9) * mm});
            skLineSegment(sketch, "E632", {"start": v(10.95, 37.9) * mm, "end": v(10.4, 37.54) * mm});
            skLineSegment(sketch, "E633", {"start": v(10.4, 37.54) * mm, "end": v(9.64, 37.02) * mm});
            skLineSegment(sketch, "E634", {"start": v(9.64, 37.02) * mm, "end": v(9.26, 36.75) * mm});
            skLineSegment(sketch, "E635", {"start": v(9.26, 36.75) * mm, "end": v(8.92, 36.48) * mm});
            skLineSegment(sketch, "E636", {"start": v(8.92, 36.48) * mm, "end": v(8.64, 36.25) * mm});
            skLineSegment(sketch, "E637", {"start": v(8.64, 36.25) * mm, "end": v(8.54, 36.14) * mm});
            skLineSegment(sketch, "E638", {"start": v(8.54, 36.14) * mm, "end": v(8.46, 36.05) * mm});
            skLineSegment(sketch, "E639", {"start": v(8.46, 36.05) * mm, "end": v(8.43, 35.98) * mm});
            skLineSegment(sketch, "E640", {"start": v(8.43, 35.98) * mm, "end": v(8.41, 35.9) * mm});
            skLineSegment(sketch, "E641", {"start": v(8.41, 35.9) * mm, "end": v(8.39, 35.71) * mm});
            skLineSegment(sketch, "E642", {"start": v(8.39, 35.71) * mm, "end": v(8.38, 35.5) * mm});
            skLineSegment(sketch, "E643", {"start": v(8.38, 35.5) * mm, "end": v(8.4, 35.25) * mm});
            skLineSegment(sketch, "E644", {"start": v(8.4, 35.25) * mm, "end": v(8.42, 34.98) * mm});
            skLineSegment(sketch, "E645", {"start": v(8.42, 34.98) * mm, "end": v(8.46, 34.7) * mm});
            skLineSegment(sketch, "E646", {"start": v(8.46, 34.7) * mm, "end": v(8.57, 34.1) * mm});
            skLineSegment(sketch, "E647", {"start": v(8.57, 34.1) * mm, "end": v(8.7, 33.5) * mm});
            skLineSegment(sketch, "E648", {"start": v(8.7, 33.5) * mm, "end": v(8.83, 32.95) * mm});
            skLineSegment(sketch, "E649", {"start": v(8.83, 32.95) * mm, "end": v(8.94, 32.48) * mm});
            skLineSegment(sketch, "E650", {"start": v(8.94, 32.48) * mm, "end": v(9.02, 32.13) * mm});
            skLineSegment(sketch, "E651", {"start": v(9.02, 32.13) * mm, "end": v(9.13, 31.57) * mm});
            skLineSegment(sketch, "E652", {"start": v(9.13, 31.57) * mm, "end": v(9.24, 30.97) * mm});
            skLineSegment(sketch, "E653", {"start": v(9.24, 30.97) * mm, "end": v(9.28, 30.66) * mm});
            skLineSegment(sketch, "E654", {"start": v(9.28, 30.66) * mm, "end": v(9.31, 30.35) * mm});
            skLineSegment(sketch, "E655", {"start": v(9.31, 30.35) * mm, "end": v(9.33, 30.04) * mm});
            skLineSegment(sketch, "E656", {"start": v(9.33, 30.04) * mm, "end": v(9.34, 29.73) * mm});
            skLineSegment(sketch, "E657", {"start": v(9.34, 29.73) * mm, "end": v(9.33, 29.43) * mm});
            skLineSegment(sketch, "E658", {"start": v(9.33, 29.43) * mm, "end": v(9.3, 29.13) * mm});
            skLineSegment(sketch, "E659", {"start": v(9.3, 29.13) * mm, "end": v(9.25, 28.83) * mm});
            skLineSegment(sketch, "E660", {"start": v(9.25, 28.83) * mm, "end": v(9.17, 28.55) * mm});
            skLineSegment(sketch, "E661", {"start": v(9.17, 28.55) * mm, "end": v(9.12, 28.41) * mm});
            skLineSegment(sketch, "E662", {"start": v(9.12, 28.41) * mm, "end": v(9.06, 28.28) * mm});
            skLineSegment(sketch, "E663", {"start": v(9.06, 28.28) * mm, "end": v(9, 28.15) * mm});
            skLineSegment(sketch, "E664", {"start": v(9, 28.15) * mm, "end": v(8.93, 28.02) * mm});
            skLineSegment(sketch, "E665", {"start": v(8.93, 28.02) * mm, "end": v(8.85, 27.9) * mm});
            skLineSegment(sketch, "E666", {"start": v(8.85, 27.9) * mm, "end": v(8.76, 27.77) * mm});
            skLineSegment(sketch, "E667", {"start": v(8.76, 27.77) * mm, "end": v(8.67, 27.66) * mm});
            skLineSegment(sketch, "E668", {"start": v(8.67, 27.66) * mm, "end": v(8.56, 27.54) * mm});
            skLineSegment(sketch, "E669", {"start": v(8.56, 27.54) * mm, "end": v(8.44, 27.43) * mm});
            skLineSegment(sketch, "E670", {"start": v(8.44, 27.43) * mm, "end": v(9.32, 25.9) * mm});
            skLineSegment(sketch, "E671", {"start": v(9.32, 25.9) * mm, "end": v(9.77, 25.14) * mm});
            skLineSegment(sketch, "E672", {"start": v(9.77, 25.14) * mm, "end": v(10.23, 24.39) * mm});
            skLineSegment(sketch, "E673", {"start": v(10.23, 24.39) * mm, "end": v(10.72, 23.64) * mm});
            skLineSegment(sketch, "E674", {"start": v(10.72, 23.64) * mm, "end": v(11.22, 22.92) * mm});
            skLineSegment(sketch, "E675", {"start": v(11.22, 22.92) * mm, "end": v(11.73, 22.21) * mm});
            skLineSegment(sketch, "E676", {"start": v(11.73, 22.21) * mm, "end": v(12.26, 21.52) * mm});
            skLineSegment(sketch, "E677", {"start": v(12.26, 21.52) * mm, "end": v(12.8, 20.84) * mm});
            skLineSegment(sketch, "E678", {"start": v(12.8, 20.84) * mm, "end": v(13.34, 20.17) * mm});
            skLineSegment(sketch, "E679", {"start": v(13.34, 20.17) * mm, "end": v(13.9, 19.5) * mm});
            skLineSegment(sketch, "E680", {"start": v(13.9, 19.5) * mm, "end": v(14.5, 18.83) * mm});
            skLineSegment(sketch, "E681", {"start": v(14.5, 18.83) * mm, "end": v(14.88, 18.38) * mm});
            skLineSegment(sketch, "E682", {"start": v(14.88, 18.38) * mm, "end": v(15.27, 17.93) * mm});
            skLineSegment(sketch, "E683", {"start": v(15.27, 17.93) * mm, "end": v(15.65, 17.46) * mm});
            skLineSegment(sketch, "E684", {"start": v(15.65, 17.46) * mm, "end": v(15.84, 17.22) * mm});
            skLineSegment(sketch, "E685", {"start": v(15.84, 17.22) * mm, "end": v(16.02, 16.97) * mm});
            skLineSegment(sketch, "E686", {"start": v(16.02, 16.97) * mm, "end": v(16.2, 16.73) * mm});
            skLineSegment(sketch, "E687", {"start": v(16.2, 16.73) * mm, "end": v(16.35, 16.47) * mm});
            skLineSegment(sketch, "E688", {"start": v(16.35, 16.47) * mm, "end": v(16.5, 16.21) * mm});
            skLineSegment(sketch, "E689", {"start": v(16.5, 16.21) * mm, "end": v(16.65, 15.95) * mm});
            skLineSegment(sketch, "E690", {"start": v(16.65, 15.95) * mm, "end": v(16.78, 15.68) * mm});
            skLineSegment(sketch, "E691", {"start": v(16.78, 15.68) * mm, "end": v(16.9, 15.4) * mm});
            skLineSegment(sketch, "E692", {"start": v(16.9, 15.4) * mm, "end": v(17, 15.13) * mm});
            skLineSegment(sketch, "E693", {"start": v(17, 15.13) * mm, "end": v(17.07, 14.84) * mm});
            skLineSegment(sketch, "E694", {"start": v(17.07, 14.84) * mm, "end": v(17.14, 14.54) * mm});
            skLineSegment(sketch, "E695", {"start": v(17.14, 14.54) * mm, "end": v(17.18, 14.24) * mm});
            skLineSegment(sketch, "E696", {"start": v(17.18, 14.24) * mm, "end": v(17.21, 13.93) * mm});
            skLineSegment(sketch, "E697", {"start": v(17.21, 13.93) * mm, "end": v(17.22, 13.63) * mm});
            skLineSegment(sketch, "E698", {"start": v(17.22, 13.63) * mm, "end": v(17.2, 13.33) * mm});
            skLineSegment(sketch, "E699", {"start": v(17.2, 13.33) * mm, "end": v(17.18, 13.03) * mm});
            skLineSegment(sketch, "E700", {"start": v(17.18, 13.03) * mm, "end": v(17.14, 12.74) * mm});
            skLineSegment(sketch, "E701", {"start": v(17.14, 12.74) * mm, "end": v(17.08, 12.44) * mm});
            skLineSegment(sketch, "E702", {"start": v(17.08, 12.44) * mm, "end": v(17.01, 12.15) * mm});
            skLineSegment(sketch, "E703", {"start": v(17.01, 12.15) * mm, "end": v(16.93, 11.86) * mm});
            skLineSegment(sketch, "E704", {"start": v(16.93, 11.86) * mm, "end": v(16.84, 11.57) * mm});
            skLineSegment(sketch, "E705", {"start": v(16.84, 11.57) * mm, "end": v(16.74, 11.28) * mm});
            skLineSegment(sketch, "E706", {"start": v(16.74, 11.28) * mm, "end": v(16.63, 11) * mm});
            skLineSegment(sketch, "E707", {"start": v(16.63, 11) * mm, "end": v(16.51, 10.72) * mm});
            skLineSegment(sketch, "E708", {"start": v(16.51, 10.72) * mm, "end": v(16.26, 10.17) * mm});
            skLineSegment(sketch, "E709", {"start": v(16.26, 10.17) * mm, "end": v(16.48, 9.7) * mm});
            skLineSegment(sketch, "E710", {"start": v(16.48, 9.7) * mm, "end": v(16.72, 9.22) * mm});
            skLineSegment(sketch, "E711", {"start": v(16.72, 9.22) * mm, "end": v(16.97, 8.74) * mm});
            skLineSegment(sketch, "E712", {"start": v(16.97, 8.74) * mm, "end": v(17.23, 8.27) * mm});
            skLineSegment(sketch, "E713", {"start": v(17.23, 8.27) * mm, "end": v(17.5, 7.8) * mm});
            skLineSegment(sketch, "E714", {"start": v(17.5, 7.8) * mm, "end": v(17.77, 7.32) * mm});
            skLineSegment(sketch, "E715", {"start": v(17.77, 7.32) * mm, "end": v(18.35, 6.38) * mm});
            skLineSegment(sketch, "E716", {"start": v(18.35, 6.38) * mm, "end": v(18.94, 5.46) * mm});
            skLineSegment(sketch, "E717", {"start": v(18.94, 5.46) * mm, "end": v(19.56, 4.56) * mm});
            skLineSegment(sketch, "E718", {"start": v(19.56, 4.56) * mm, "end": v(20.19, 3.7) * mm});
            skLineSegment(sketch, "E719", {"start": v(20.19, 3.7) * mm, "end": v(20.81, 2.88) * mm});
            skLineSegment(sketch, "E720", {"start": v(20.81, 2.88) * mm, "end": v(21.26, 2.34) * mm});
            skLineSegment(sketch, "E721", {"start": v(21.26, 2.34) * mm, "end": v(21.73, 1.8) * mm});
            skLineSegment(sketch, "E722", {"start": v(21.73, 1.8) * mm, "end": v(22.2, 1.3) * mm});
            skLineSegment(sketch, "E723", {"start": v(22.2, 1.3) * mm, "end": v(22.7, 0.8) * mm});
            skLineSegment(sketch, "E724", {"start": v(22.7, 0.8) * mm, "end": v(23.69, -0.2) * mm});
            skLineSegment(sketch, "E725", {"start": v(23.69, -0.2) * mm, "end": v(24.68, -1.19) * mm});
            skLineSegment(sketch, "E726", {"start": v(24.68, -1.19) * mm, "end": v(25.1, -1.62) * mm});
            skLineSegment(sketch, "E727", {"start": v(25.1, -1.62) * mm, "end": v(25.54, -2.09) * mm});
            skLineSegment(sketch, "E728", {"start": v(25.54, -2.09) * mm, "end": v(25.76, -2.34) * mm});
            skLineSegment(sketch, "E729", {"start": v(25.76, -2.34) * mm, "end": v(25.96, -2.6) * mm});
            skLineSegment(sketch, "E730", {"start": v(25.96, -2.6) * mm, "end": v(26.16, -2.86) * mm});
            skLineSegment(sketch, "E731", {"start": v(26.16, -2.86) * mm, "end": v(26.34, -3.13) * mm});
            skLineSegment(sketch, "E732", {"start": v(26.34, -3.13) * mm, "end": v(26.51, -3.4) * mm});
            skLineSegment(sketch, "E733", {"start": v(26.51, -3.4) * mm, "end": v(26.66, -3.7) * mm});
            skLineSegment(sketch, "E734", {"start": v(26.66, -3.7) * mm, "end": v(26.78, -3.99) * mm});
            skLineSegment(sketch, "E735", {"start": v(26.78, -3.99) * mm, "end": v(26.87, -4.28) * mm});
            skLineSegment(sketch, "E736", {"start": v(26.87, -4.28) * mm, "end": v(26.9, -4.43) * mm});
            skLineSegment(sketch, "E737", {"start": v(26.9, -4.43) * mm, "end": v(26.94, -4.59) * mm});
            skLineSegment(sketch, "E738", {"start": v(26.94, -4.59) * mm, "end": v(26.96, -4.74) * mm});
            skLineSegment(sketch, "E739", {"start": v(26.96, -4.74) * mm, "end": v(26.97, -4.9) * mm});
            skLineSegment(sketch, "E740", {"start": v(26.97, -4.9) * mm, "end": v(26.97, -5.05) * mm});
            skLineSegment(sketch, "E741", {"start": v(26.97, -5.05) * mm, "end": v(26.96, -5.2) * mm});
            skLineSegment(sketch, "E742", {"start": v(26.96, -5.2) * mm, "end": v(26.94, -5.36) * mm});
            skLineSegment(sketch, "E743", {"start": v(26.94, -5.36) * mm, "end": v(26.9, -5.52) * mm});
            skLineSegment(sketch, "E744", {"start": v(26.9, -5.52) * mm, "end": v(26.84, -5.77) * mm});
            skLineSegment(sketch, "E745", {"start": v(26.84, -5.77) * mm, "end": v(26.75, -6) * mm});
            skLineSegment(sketch, "E746", {"start": v(26.75, -6) * mm, "end": v(26.64, -6.21) * mm});
            skLineSegment(sketch, "E747", {"start": v(26.64, -6.21) * mm, "end": v(26.51, -6.41) * mm});
            skLineSegment(sketch, "E748", {"start": v(26.51, -6.41) * mm, "end": v(26.37, -6.6) * mm});
            skLineSegment(sketch, "E749", {"start": v(26.37, -6.6) * mm, "end": v(26.2, -6.77) * mm});
            skLineSegment(sketch, "E750", {"start": v(26.2, -6.77) * mm, "end": v(26.03, -6.93) * mm});
            skLineSegment(sketch, "E751", {"start": v(26.03, -6.93) * mm, "end": v(25.84, -7.08) * mm});
            skLineSegment(sketch, "E752", {"start": v(25.84, -7.08) * mm, "end": v(25.64, -7.21) * mm});
            skLineSegment(sketch, "E753", {"start": v(25.64, -7.21) * mm, "end": v(25.42, -7.34) * mm});
            skLineSegment(sketch, "E754", {"start": v(25.42, -7.34) * mm, "end": v(25.2, -7.45) * mm});
            skLineSegment(sketch, "E755", {"start": v(25.2, -7.45) * mm, "end": v(24.97, -7.56) * mm});
            skLineSegment(sketch, "E756", {"start": v(24.97, -7.56) * mm, "end": v(24.74, -7.65) * mm});
            skLineSegment(sketch, "E757", {"start": v(24.74, -7.65) * mm, "end": v(24.5, -7.74) * mm});
            skLineSegment(sketch, "E758", {"start": v(24.5, -7.74) * mm, "end": v(24.25, -7.82) * mm});
            skLineSegment(sketch, "E759", {"start": v(24.25, -7.82) * mm, "end": v(24, -7.89) * mm});
            skLineSegment(sketch, "E760", {"start": v(24, -7.89) * mm, "end": v(24.18, -8.34) * mm});
            skLineSegment(sketch, "E761", {"start": v(24.18, -8.34) * mm, "end": v(24.36, -8.79) * mm});
            skLineSegment(sketch, "E762", {"start": v(24.36, -8.79) * mm, "end": v(24.55, -9.23) * mm});
            skLineSegment(sketch, "E763", {"start": v(24.55, -9.23) * mm, "end": v(24.76, -9.67) * mm});
            skLineSegment(sketch, "E764", {"start": v(24.76, -9.67) * mm, "end": v(24.97, -10.1) * mm});
            skLineSegment(sketch, "E765", {"start": v(24.97, -10.1) * mm, "end": v(25.2, -10.53) * mm});
            skLineSegment(sketch, "E766", {"start": v(25.2, -10.53) * mm, "end": v(25.43, -10.95) * mm});
            skLineSegment(sketch, "E767", {"start": v(25.43, -10.95) * mm, "end": v(25.67, -11.36) * mm});
            skLineSegment(sketch, "E768", {"start": v(25.67, -11.36) * mm, "end": v(25.93, -11.76) * mm});
            skLineSegment(sketch, "E769", {"start": v(25.93, -11.76) * mm, "end": v(26.2, -12.16) * mm});
            skLineSegment(sketch, "E770", {"start": v(26.2, -12.16) * mm, "end": v(26.49, -12.55) * mm});
            skLineSegment(sketch, "E771", {"start": v(26.49, -12.55) * mm, "end": v(26.78, -12.93) * mm});
            skLineSegment(sketch, "E772", {"start": v(26.78, -12.93) * mm, "end": v(27.1, -13.3) * mm});
            skLineSegment(sketch, "E773", {"start": v(27.1, -13.3) * mm, "end": v(27.42, -13.66) * mm});
            skLineSegment(sketch, "E774", {"start": v(27.42, -13.66) * mm, "end": v(27.76, -14.02) * mm});
            skLineSegment(sketch, "E775", {"start": v(27.76, -14.02) * mm, "end": v(28.11, -14.36) * mm});
            skLineSegment(sketch, "E776", {"start": v(28.11, -14.36) * mm, "end": v(28.38, -14.6) * mm});
            skLineSegment(sketch, "E777", {"start": v(28.38, -14.6) * mm, "end": v(28.65, -14.83) * mm});
            skLineSegment(sketch, "E778", {"start": v(28.65, -14.83) * mm, "end": v(29.2, -15.28) * mm});
            skLineSegment(sketch, "E779", {"start": v(29.2, -15.28) * mm, "end": v(29.74, -15.72) * mm});
            skLineSegment(sketch, "E780", {"start": v(29.74, -15.72) * mm, "end": v(30.3, -16.16) * mm});
            skLineSegment(sketch, "E781", {"start": v(30.3, -16.16) * mm, "end": v(30.57, -16.38) * mm});
            skLineSegment(sketch, "E782", {"start": v(30.57, -16.38) * mm, "end": v(30.84, -16.61) * mm});
            skLineSegment(sketch, "E783", {"start": v(30.84, -16.61) * mm, "end": v(31.1, -16.85) * mm});
            skLineSegment(sketch, "E784", {"start": v(31.1, -16.85) * mm, "end": v(31.34, -17.1) * mm});
            skLineSegment(sketch, "E785", {"start": v(31.34, -17.1) * mm, "end": v(31.57, -17.37) * mm});
            skLineSegment(sketch, "E786", {"start": v(31.57, -17.37) * mm, "end": v(31.77, -17.65) * mm});
            skLineSegment(sketch, "E787", {"start": v(31.77, -17.65) * mm, "end": v(31.86, -17.8) * mm});
            skLineSegment(sketch, "E788", {"start": v(31.86, -17.8) * mm, "end": v(31.95, -17.95) * mm});
            skLineSegment(sketch, "E789", {"start": v(31.95, -17.95) * mm, "end": v(32.03, -18.1) * mm});
            skLineSegment(sketch, "E790", {"start": v(32.03, -18.1) * mm, "end": v(32.1, -18.27) * mm});
            skLineSegment(sketch, "E791", {"start": v(32.1, -18.27) * mm, "end": v(32.18, -18.47) * mm});
            skLineSegment(sketch, "E792", {"start": v(32.18, -18.47) * mm, "end": v(32.25, -18.67) * mm});
            skLineSegment(sketch, "E793", {"start": v(32.25, -18.67) * mm, "end": v(32.3, -18.88) * mm});
            skLineSegment(sketch, "E794", {"start": v(32.3, -18.88) * mm, "end": v(32.34, -19.09) * mm});
            skLineSegment(sketch, "E795", {"start": v(32.34, -19.09) * mm, "end": v(32.45, -19.8) * mm});
            skLineSegment(sketch, "E796", {"start": v(32.45, -19.8) * mm, "end": v(31.98, -20.35) * mm});
            skLineSegment(sketch, "E797", {"start": v(31.98, -20.35) * mm, "end": v(31.74, -20.6) * mm});
            skLineSegment(sketch, "E798", {"start": v(31.74, -20.6) * mm, "end": v(31.5, -20.83) * mm});
            skLineSegment(sketch, "E799", {"start": v(31.5, -20.83) * mm, "end": v(31.27, -21.03) * mm});
            skLineSegment(sketch, "E800", {"start": v(31.27, -21.03) * mm, "end": v(31.03, -21.2) * mm});
            skLineSegment(sketch, "E801", {"start": v(31.03, -21.2) * mm, "end": v(30.8, -21.36) * mm});
            skLineSegment(sketch, "E802", {"start": v(30.8, -21.36) * mm, "end": v(30.55, -21.48) * mm});
            skLineSegment(sketch, "E803", {"start": v(30.55, -21.48) * mm, "end": v(30.3, -21.58) * mm});
            skLineSegment(sketch, "E804", {"start": v(30.3, -21.58) * mm, "end": v(30.06, -21.66) * mm});
            skLineSegment(sketch, "E805", {"start": v(30.06, -21.66) * mm, "end": v(30.27, -22.1) * mm});
            skLineSegment(sketch, "E806", {"start": v(30.27, -22.1) * mm, "end": v(30.49, -22.55) * mm});
            skLineSegment(sketch, "E807", {"start": v(30.49, -22.55) * mm, "end": v(30.72, -22.99) * mm});
            skLineSegment(sketch, "E808", {"start": v(30.72, -22.99) * mm, "end": v(30.97, -23.42) * mm});
            skLineSegment(sketch, "E809", {"start": v(30.97, -23.42) * mm, "end": v(31.22, -23.84) * mm});
            skLineSegment(sketch, "E810", {"start": v(31.22, -23.84) * mm, "end": v(31.49, -24.26) * mm});
            skLineSegment(sketch, "E811", {"start": v(31.49, -24.26) * mm, "end": v(31.76, -24.68) * mm});
            skLineSegment(sketch, "E812", {"start": v(31.76, -24.68) * mm, "end": v(32.04, -25.1) * mm});
            skLineSegment(sketch, "E813", {"start": v(32.04, -25.1) * mm, "end": v(32.33, -25.5) * mm});
            skLineSegment(sketch, "E814", {"start": v(32.33, -25.5) * mm, "end": v(32.63, -25.9) * mm});
            skLineSegment(sketch, "E815", {"start": v(32.63, -25.9) * mm, "end": v(33.24, -26.68) * mm});
            skLineSegment(sketch, "E816", {"start": v(33.24, -26.68) * mm, "end": v(33.86, -27.44) * mm});
            skLineSegment(sketch, "E817", {"start": v(33.86, -27.44) * mm, "end": v(34.5, -28.17) * mm});
            skLineSegment(sketch, "E818", {"start": v(34.5, -28.17) * mm, "end": v(35.17, -28.9) * mm});
            skLineSegment(sketch, "E819", {"start": v(35.17, -28.9) * mm, "end": v(35.85, -29.62) * mm});
            skLineSegment(sketch, "E820", {"start": v(35.85, -29.62) * mm, "end": v(37.23, -31.02) * mm});
            skLineSegment(sketch, "E821", {"start": v(37.23, -31.02) * mm, "end": v(37.68, -31.46) * mm});
            skLineSegment(sketch, "E822", {"start": v(37.68, -31.46) * mm, "end": v(37.93, -31.72) * mm});
            skLineSegment(sketch, "E823", {"start": v(37.93, -31.72) * mm, "end": v(38.18, -31.98) * mm});
            skLineSegment(sketch, "E824", {"start": v(38.18, -31.98) * mm, "end": v(38.42, -32.25) * mm});
            skLineSegment(sketch, "E825", {"start": v(38.42, -32.25) * mm, "end": v(38.64, -32.53) * mm});
            skLineSegment(sketch, "E826", {"start": v(38.64, -32.53) * mm, "end": v(38.82, -32.8) * mm});
            skLineSegment(sketch, "E827", {"start": v(38.82, -32.8) * mm, "end": v(38.9, -32.92) * mm});
            skLineSegment(sketch, "E828", {"start": v(38.9, -32.92) * mm, "end": v(38.96, -33.05) * mm});
            skLineSegment(sketch, "E829", {"start": v(38.96, -33.05) * mm, "end": v(39.05, -33.26) * mm});
            skLineSegment(sketch, "E830", {"start": v(39.05, -33.26) * mm, "end": v(39.12, -33.47) * mm});
            skLineSegment(sketch, "E831", {"start": v(39.12, -33.47) * mm, "end": v(39.19, -33.68) * mm});
            skLineSegment(sketch, "E832", {"start": v(39.19, -33.68) * mm, "end": v(39.25, -33.89) * mm});
            skLineSegment(sketch, "E833", {"start": v(39.25, -33.89) * mm, "end": v(39.3, -34.1) * mm});
            skLineSegment(sketch, "E834", {"start": v(39.3, -34.1) * mm, "end": v(39.33, -34.31) * mm});
            skLineSegment(sketch, "E835", {"start": v(39.33, -34.31) * mm, "end": v(39.35, -34.53) * mm});
            skLineSegment(sketch, "E836", {"start": v(39.35, -34.53) * mm, "end": v(39.35, -34.74) * mm});
            skLineSegment(sketch, "E837", {"start": v(39.35, -34.74) * mm, "end": v(39.35, -34.95) * mm});
            skLineSegment(sketch, "E838", {"start": v(39.35, -34.95) * mm, "end": v(39.33, -35.17) * mm});
            skLineSegment(sketch, "E839", {"start": v(39.33, -35.17) * mm, "end": v(39.3, -35.38) * mm});
            skLineSegment(sketch, "E840", {"start": v(39.3, -35.38) * mm, "end": v(39.24, -35.58) * mm});
            skLineSegment(sketch, "E841", {"start": v(39.24, -35.58) * mm, "end": v(39.17, -35.79) * mm});
            skLineSegment(sketch, "E842", {"start": v(39.17, -35.79) * mm, "end": v(39.08, -36) * mm});
            skLineSegment(sketch, "E843", {"start": v(39.08, -36) * mm, "end": v(38.97, -36.19) * mm});
            skLineSegment(sketch, "E844", {"start": v(38.97, -36.19) * mm, "end": v(38.85, -36.38) * mm});
            skLineSegment(sketch, "E845", {"start": v(38.85, -36.38) * mm, "end": v(38.72, -36.55) * mm});
            skLineSegment(sketch, "E846", {"start": v(38.72, -36.55) * mm, "end": v(38.6, -36.7) * mm});
            skLineSegment(sketch, "E847", {"start": v(38.6, -36.7) * mm, "end": v(38.45, -36.84) * mm});
            skLineSegment(sketch, "E848", {"start": v(38.45, -36.84) * mm, "end": v(38.3, -36.98) * mm});
            skLineSegment(sketch, "E849", {"start": v(38.3, -36.98) * mm, "end": v(38.13, -37.1) * mm});
            skLineSegment(sketch, "E850", {"start": v(38.13, -37.1) * mm, "end": v(37.96, -37.2) * mm});
            skLineSegment(sketch, "E851", {"start": v(37.96, -37.2) * mm, "end": v(37.79, -37.3) * mm});
            skLineSegment(sketch, "E852", {"start": v(37.79, -37.3) * mm, "end": v(37.6, -37.4) * mm});
            skLineSegment(sketch, "E853", {"start": v(37.6, -37.4) * mm, "end": v(37.42, -37.49) * mm});
            skLineSegment(sketch, "E854", {"start": v(37.42, -37.49) * mm, "end": v(37.22, -37.56) * mm});
            skLineSegment(sketch, "E855", {"start": v(37.22, -37.56) * mm, "end": v(37.02, -37.63) * mm});
            skLineSegment(sketch, "E856", {"start": v(37.02, -37.63) * mm, "end": v(36.82, -37.69) * mm});
            skLineSegment(sketch, "E857", {"start": v(36.82, -37.69) * mm, "end": v(36.4, -37.78) * mm});
            skLineSegment(sketch, "E858", {"start": v(36.4, -37.78) * mm, "end": v(35.97, -37.85) * mm});
            skLineSegment(sketch, "E859", {"start": v(35.97, -37.85) * mm, "end": v(36.27, -38.23) * mm});
            skLineSegment(sketch, "E860", {"start": v(36.27, -38.23) * mm, "end": v(36.58, -38.62) * mm});
            skLineSegment(sketch, "E861", {"start": v(36.58, -38.62) * mm, "end": v(37.24, -39.4) * mm});
            skLineSegment(sketch, "E862", {"start": v(37.24, -39.4) * mm, "end": v(37.93, -40.18) * mm});
            skLineSegment(sketch, "E863", {"start": v(37.93, -40.18) * mm, "end": v(38.62, -40.93) * mm});
            skLineSegment(sketch, "E864", {"start": v(38.62, -40.93) * mm, "end": v(39.3, -41.65) * mm});
            skLineSegment(sketch, "E865", {"start": v(39.3, -41.65) * mm, "end": v(39.93, -42.3) * mm});
            skLineSegment(sketch, "E866", {"start": v(39.93, -42.3) * mm, "end": v(40.5, -42.87) * mm});
            skLineSegment(sketch, "E867", {"start": v(40.5, -42.87) * mm, "end": v(40.98, -43.34) * mm});
            skLineSegment(sketch, "E868", {"start": v(40.98, -43.34) * mm, "end": v(41.41, -43.76) * mm});
            skLineSegment(sketch, "E869", {"start": v(41.41, -43.76) * mm, "end": v(41.85, -44.21) * mm});
            skLineSegment(sketch, "E870", {"start": v(41.85, -44.21) * mm, "end": v(42.28, -44.69) * mm});
            skLineSegment(sketch, "E871", {"start": v(42.28, -44.69) * mm, "end": v(42.69, -45.18) * mm});
            skLineSegment(sketch, "E872", {"start": v(42.69, -45.18) * mm, "end": v(42.89, -45.43) * mm});
            skLineSegment(sketch, "E873", {"start": v(42.89, -45.43) * mm, "end": v(43.08, -45.7) * mm});
            skLineSegment(sketch, "E874", {"start": v(43.08, -45.7) * mm, "end": v(43.26, -45.95) * mm});
            skLineSegment(sketch, "E875", {"start": v(43.26, -45.95) * mm, "end": v(43.43, -46.22) * mm});
            skLineSegment(sketch, "E876", {"start": v(43.43, -46.22) * mm, "end": v(43.6, -46.49) * mm});
            skLineSegment(sketch, "E877", {"start": v(43.6, -46.49) * mm, "end": v(43.75, -46.76) * mm});
            skLineSegment(sketch, "E878", {"start": v(43.75, -46.76) * mm, "end": v(43.89, -47.03) * mm});
            skLineSegment(sketch, "E879", {"start": v(43.89, -47.03) * mm, "end": v(44.02, -47.3) * mm});
            skLineSegment(sketch, "E880", {"start": v(44.02, -47.3) * mm, "end": v(44.1, -47.54) * mm});
            skLineSegment(sketch, "E881", {"start": v(44.1, -47.54) * mm, "end": v(44.2, -47.77) * mm});
            skLineSegment(sketch, "E882", {"start": v(44.2, -47.77) * mm, "end": v(44.26, -48) * mm});
            skLineSegment(sketch, "E883", {"start": v(44.26, -48) * mm, "end": v(44.33, -48.24) * mm});
            skLineSegment(sketch, "E884", {"start": v(44.33, -48.24) * mm, "end": v(44.37, -48.47) * mm});
            skLineSegment(sketch, "E885", {"start": v(44.37, -48.47) * mm, "end": v(44.41, -48.71) * mm});
            skLineSegment(sketch, "E886", {"start": v(44.41, -48.71) * mm, "end": v(44.43, -48.95) * mm});
            skLineSegment(sketch, "E887", {"start": v(44.43, -48.95) * mm, "end": v(44.44, -49.19) * mm});
            skLineSegment(sketch, "E888", {"start": v(44.44, -49.19) * mm, "end": v(44.43, -49.42) * mm});
            skLineSegment(sketch, "E889", {"start": v(44.43, -49.42) * mm, "end": v(44.41, -49.66) * mm});
            skLineSegment(sketch, "E890", {"start": v(44.41, -49.66) * mm, "end": v(44.37, -49.9) * mm});
            skLineSegment(sketch, "E891", {"start": v(44.37, -49.9) * mm, "end": v(44.32, -50.12) * mm});
            skLineSegment(sketch, "E892", {"start": v(44.32, -50.12) * mm, "end": v(44.24, -50.35) * mm});
            skLineSegment(sketch, "E893", {"start": v(44.24, -50.35) * mm, "end": v(44.15, -50.58) * mm});
            skLineSegment(sketch, "E894", {"start": v(44.15, -50.58) * mm, "end": v(44.04, -50.8) * mm});
            skLineSegment(sketch, "E895", {"start": v(44.04, -50.8) * mm, "end": v(43.9, -51.01) * mm});
            skLineSegment(sketch, "E896", {"start": v(43.9, -51.01) * mm, "end": v(43.78, -51.18) * mm});
            skLineSegment(sketch, "E897", {"start": v(43.78, -51.18) * mm, "end": v(43.65, -51.34) * mm});
            skLineSegment(sketch, "E898", {"start": v(43.65, -51.34) * mm, "end": v(43.51, -51.5) * mm});
            skLineSegment(sketch, "E899", {"start": v(43.51, -51.5) * mm, "end": v(43.37, -51.63) * mm});
            skLineSegment(sketch, "E900", {"start": v(43.37, -51.63) * mm, "end": v(43.21, -51.76) * mm});
            skLineSegment(sketch, "E901", {"start": v(43.21, -51.76) * mm, "end": v(43.06, -51.88) * mm});
            skLineSegment(sketch, "E902", {"start": v(43.06, -51.88) * mm, "end": v(42.9, -51.99) * mm});
            skLineSegment(sketch, "E903", {"start": v(42.9, -51.99) * mm, "end": v(42.72, -52.09) * mm});
            skLineSegment(sketch, "E904", {"start": v(42.72, -52.09) * mm, "end": v(42.54, -52.18) * mm});
            skLineSegment(sketch, "E905", {"start": v(42.54, -52.18) * mm, "end": v(42.36, -52.26) * mm});
            skLineSegment(sketch, "E906", {"start": v(42.36, -52.26) * mm, "end": v(42.18, -52.33) * mm});
            skLineSegment(sketch, "E907", {"start": v(42.18, -52.33) * mm, "end": v(41.99, -52.4) * mm});
            skLineSegment(sketch, "E908", {"start": v(41.99, -52.4) * mm, "end": v(41.8, -52.45) * mm});
            skLineSegment(sketch, "E909", {"start": v(41.8, -52.45) * mm, "end": v(41.6, -52.5) * mm});
            skLineSegment(sketch, "E910", {"start": v(41.6, -52.5) * mm, "end": v(41.2, -52.57) * mm});
            skLineSegment(sketch, "E911", {"start": v(41.2, -52.57) * mm, "end": v(40.79, -52.62) * mm});
            skLineSegment(sketch, "E912", {"start": v(40.79, -52.62) * mm, "end": v(40.38, -52.64) * mm});
            skLineSegment(sketch, "E913", {"start": v(40.38, -52.64) * mm, "end": v(39.96, -52.64) * mm});
            skLineSegment(sketch, "E914", {"start": v(39.96, -52.64) * mm, "end": v(39.55, -52.62) * mm});
            skLineSegment(sketch, "E915", {"start": v(39.55, -52.62) * mm, "end": v(39.14, -52.58) * mm});
            skLineSegment(sketch, "E916", {"start": v(39.14, -52.58) * mm, "end": v(38.74, -52.52) * mm});
            skLineSegment(sketch, "E917", {"start": v(38.74, -52.52) * mm, "end": v(38.35, -52.45) * mm});
            skLineSegment(sketch, "E918", {"start": v(38.35, -52.45) * mm, "end": v(37.97, -52.37) * mm});
            skLineSegment(sketch, "E919", {"start": v(37.97, -52.37) * mm, "end": v(37.52, -52.25) * mm});
            skLineSegment(sketch, "E920", {"start": v(37.52, -52.25) * mm, "end": v(37.06, -52.12) * mm});
            skLineSegment(sketch, "E921", {"start": v(37.06, -52.12) * mm, "end": v(36.15, -51.82) * mm});
            skLineSegment(sketch, "E922", {"start": v(36.15, -51.82) * mm, "end": v(35.24, -51.5) * mm});
            skLineSegment(sketch, "E923", {"start": v(35.24, -51.5) * mm, "end": v(34.78, -51.35) * mm});
            skLineSegment(sketch, "E924", {"start": v(34.78, -51.35) * mm, "end": v(34.33, -51.2) * mm});
            skLineSegment(sketch, "E925", {"start": v(34.33, -51.2) * mm, "end": v(33.72, -51.03) * mm});
            skLineSegment(sketch, "E926", {"start": v(33.72, -51.03) * mm, "end": v(33.4, -50.94) * mm});
            skLineSegment(sketch, "E927", {"start": v(33.4, -50.94) * mm, "end": v(33.07, -50.86) * mm});
            skLineSegment(sketch, "E928", {"start": v(33.07, -50.86) * mm, "end": v(32.73, -50.79) * mm});
            skLineSegment(sketch, "E929", {"start": v(32.73, -50.79) * mm, "end": v(32.4, -50.73) * mm});
            skLineSegment(sketch, "E930", {"start": v(32.4, -50.73) * mm, "end": v(32.08, -50.7) * mm});
            skLineSegment(sketch, "E931", {"start": v(32.08, -50.7) * mm, "end": v(31.76, -50.67) * mm});
            skLineSegment(sketch, "E932", {"start": v(31.76, -50.67) * mm, "end": v(31.71, -50.67) * mm});
            skLineSegment(sketch, "E933", {"start": v(31.71, -50.67) * mm, "end": v(31.5, -50.68) * mm});
            skLineSegment(sketch, "E934", {"start": v(31.5, -50.68) * mm, "end": v(31.4, -50.69) * mm});
            skLineSegment(sketch, "E935", {"start": v(31.4, -50.69) * mm, "end": v(31.3, -50.71) * mm});
            skLineSegment(sketch, "E936", {"start": v(31.3, -50.71) * mm, "end": v(31.18, -50.74) * mm});
            skLineSegment(sketch, "E937", {"start": v(31.18, -50.74) * mm, "end": v(29.76, -50.9) * mm});
            skLineSegment(sketch, "E938", {"start": v(29.76, -50.9) * mm, "end": v(28.09, -51.63) * mm});
            skLineSegment(sketch, "E939", {"start": v(28.09, -51.63) * mm, "end": v(27.53, -51.95) * mm});
            skLineSegment(sketch, "E940", {"start": v(27.53, -51.95) * mm, "end": v(26.98, -52.28) * mm});
            skLineSegment(sketch, "E941", {"start": v(26.98, -52.28) * mm, "end": v(26.43, -52.62) * mm});
            skLineSegment(sketch, "E942", {"start": v(26.43, -52.62) * mm, "end": v(25.87, -52.95) * mm});
            skLineSegment(sketch, "E943", {"start": v(25.87, -52.95) * mm, "end": v(25.38, -53.22) * mm});
            skLineSegment(sketch, "E944", {"start": v(25.38, -53.22) * mm, "end": v(24.9, -53.48) * mm});
            skLineSegment(sketch, "E945", {"start": v(24.9, -53.48) * mm, "end": v(24.4, -53.72) * mm});
            skLineSegment(sketch, "E946", {"start": v(24.4, -53.72) * mm, "end": v(23.9, -53.94) * mm});
            skLineSegment(sketch, "E947", {"start": v(23.9, -53.94) * mm, "end": v(23.41, -54.13) * mm});
            skLineSegment(sketch, "E948", {"start": v(23.41, -54.13) * mm, "end": v(22.91, -54.31) * mm});
            skLineSegment(sketch, "E949", {"start": v(22.91, -54.31) * mm, "end": v(22.4, -54.47) * mm});
            skLineSegment(sketch, "E950", {"start": v(22.4, -54.47) * mm, "end": v(21.9, -54.6) * mm});
            skLineSegment(sketch, "E951", {"start": v(21.9, -54.6) * mm, "end": v(21.39, -54.72) * mm});
            skLineSegment(sketch, "E952", {"start": v(21.39, -54.72) * mm, "end": v(20.87, -54.81) * mm});
            skLineSegment(sketch, "E953", {"start": v(20.87, -54.81) * mm, "end": v(20.34, -54.88) * mm});
            skLineSegment(sketch, "E954", {"start": v(20.34, -54.88) * mm, "end": v(19.81, -54.92) * mm});
            skLineSegment(sketch, "E955", {"start": v(19.81, -54.92) * mm, "end": v(19.28, -54.94) * mm});
            skLineSegment(sketch, "E956", {"start": v(19.28, -54.94) * mm, "end": v(18.73, -54.94) * mm});
            skLineSegment(sketch, "E957", {"start": v(18.73, -54.94) * mm, "end": v(18.18, -54.9) * mm});
            skLineSegment(sketch, "E958", {"start": v(18.18, -54.9) * mm, "end": v(17.62, -54.85) * mm});
            skLineSegment(sketch, "E959", {"start": v(17.62, -54.85) * mm, "end": v(17.22, -54.8) * mm});
            skLineSegment(sketch, "E960", {"start": v(17.22, -54.8) * mm, "end": v(16.82, -54.73) * mm});
            skLineSegment(sketch, "E961", {"start": v(16.82, -54.73) * mm, "end": v(16.43, -54.65) * mm});
            skLineSegment(sketch, "E962", {"start": v(16.43, -54.65) * mm, "end": v(16.03, -54.56) * mm});
            skLineSegment(sketch, "E963", {"start": v(16.03, -54.56) * mm, "end": v(15.25, -54.37) * mm});
            skLineSegment(sketch, "E964", {"start": v(15.25, -54.37) * mm, "end": v(14.48, -54.15) * mm});
            skLineSegment(sketch, "E965", {"start": v(14.48, -54.15) * mm, "end": v(13.83, -53.97) * mm});
            skLineSegment(sketch, "E966", {"start": v(13.83, -53.97) * mm, "end": v(13.17, -53.78) * mm});
            skLineSegment(sketch, "E967", {"start": v(13.17, -53.78) * mm, "end": v(12.52, -53.62) * mm});
            skLineSegment(sketch, "E968", {"start": v(12.52, -53.62) * mm, "end": v(12.19, -53.54) * mm});
            skLineSegment(sketch, "E969", {"start": v(12.19, -53.54) * mm, "end": v(11.85, -53.47) * mm});
            skLineSegment(sketch, "E970", {"start": v(11.85, -53.47) * mm, "end": v(11.35, -53.4) * mm});
            skLineSegment(sketch, "E971", {"start": v(11.35, -53.4) * mm, "end": v(10.87, -53.35) * mm});
            skLineSegment(sketch, "E972", {"start": v(10.87, -53.35) * mm, "end": v(10.63, -53.34) * mm});
            skLineSegment(sketch, "E973", {"start": v(10.63, -53.34) * mm, "end": v(10.4, -53.33) * mm});
            skLineSegment(sketch, "E974", {"start": v(10.4, -53.33) * mm, "end": v(10.17, -53.34) * mm});
            skLineSegment(sketch, "E975", {"start": v(10.17, -53.34) * mm, "end": v(9.94, -53.35) * mm});
            skLineSegment(sketch, "E976", {"start": v(9.94, -53.35) * mm, "end": v(9.72, -53.37) * mm});
            skLineSegment(sketch, "E977", {"start": v(9.72, -53.37) * mm, "end": v(9.5, -53.4) * mm});
            skLineSegment(sketch, "E978", {"start": v(9.5, -53.4) * mm, "end": v(9.27, -53.44) * mm});
            skLineSegment(sketch, "E979", {"start": v(9.27, -53.44) * mm, "end": v(9.05, -53.48) * mm});
            skLineSegment(sketch, "E980", {"start": v(9.05, -53.48) * mm, "end": v(8.82, -53.54) * mm});
            skLineSegment(sketch, "E981", {"start": v(8.82, -53.54) * mm, "end": v(8.6, -53.6) * mm});
            skLineSegment(sketch, "E982", {"start": v(8.6, -53.6) * mm, "end": v(8.38, -53.68) * mm});
            skLineSegment(sketch, "E983", {"start": v(8.38, -53.68) * mm, "end": v(8.16, -53.76) * mm});
            skLineSegment(sketch, "E984", {"start": v(8.16, -53.76) * mm, "end": v(8.18, -54.56) * mm});
            skLineSegment(sketch, "E985", {"start": v(8.18, -54.56) * mm, "end": v(8.3, -56.51) * mm});
            skLineSegment(sketch, "E986", {"start": v(8.3, -56.51) * mm, "end": v(8.33, -57.16) * mm});
            skLineSegment(sketch, "E987", {"start": v(8.33, -57.16) * mm, "end": v(8.69, -57.19) * mm});
            skLineSegment(sketch, "E988", {"start": v(8.69, -57.19) * mm, "end": v(9.03, -57.23) * mm});
            skLineSegment(sketch, "E989", {"start": v(9.03, -57.23) * mm, "end": v(9.38, -57.28) * mm});
            skLineSegment(sketch, "E990", {"start": v(9.38, -57.28) * mm, "end": v(9.72, -57.34) * mm});
            skLineSegment(sketch, "E991", {"start": v(9.72, -57.34) * mm, "end": v(10.06, -57.4) * mm});
            skLineSegment(sketch, "E992", {"start": v(10.06, -57.4) * mm, "end": v(10.4, -57.48) * mm});
            skLineSegment(sketch, "E993", {"start": v(10.4, -57.48) * mm, "end": v(10.73, -57.56) * mm});
            skLineSegment(sketch, "E994", {"start": v(10.73, -57.56) * mm, "end": v(11.07, -57.65) * mm});
            skLineSegment(sketch, "E995", {"start": v(11.07, -57.65) * mm, "end": v(11.4, -57.76) * mm});
            skLineSegment(sketch, "E996", {"start": v(11.4, -57.76) * mm, "end": v(11.72, -57.87) * mm});
            skLineSegment(sketch, "E997", {"start": v(11.72, -57.87) * mm, "end": v(12.05, -58) * mm});
            skLineSegment(sketch, "E998", {"start": v(12.05, -58) * mm, "end": v(12.37, -58.13) * mm});
            skLineSegment(sketch, "E999", {"start": v(12.37, -58.13) * mm, "end": v(12.7, -58.28) * mm});
            skLineSegment(sketch, "E1000", {"start": v(12.7, -58.28) * mm, "end": v(13.01, -58.43) * mm});
            skLineSegment(sketch, "E1001", {"start": v(13.01, -58.43) * mm, "end": v(13.33, -58.6) * mm});
            skLineSegment(sketch, "E1002", {"start": v(13.33, -58.6) * mm, "end": v(13.65, -58.79) * mm});
            skLineSegment(sketch, "E1003", {"start": v(13.65, -58.79) * mm, "end": v(19.31, -62.2) * mm});
            skLineSegment(sketch, "E1004", {"start": v(19.31, -62.2) * mm, "end": v(12.72, -61.66) * mm});
            skLineSegment(sketch, "E1005", {"start": v(12.72, -61.66) * mm, "end": v(12.09, -61.6) * mm});
            skLineSegment(sketch, "E1006", {"start": v(12.09, -61.6) * mm, "end": v(11.46, -61.52) * mm});
            skLineSegment(sketch, "E1007", {"start": v(11.46, -61.52) * mm, "end": v(10.84, -61.43) * mm});
            skLineSegment(sketch, "E1008", {"start": v(10.84, -61.43) * mm, "end": v(10.22, -61.32) * mm});
            skLineSegment(sketch, "E1009", {"start": v(10.22, -61.32) * mm, "end": v(9.36, -61.14) * mm});
            skLineSegment(sketch, "E1010", {"start": v(9.36, -61.14) * mm, "end": v(8.93, -61.05) * mm});
            skLineSegment(sketch, "E1011", {"start": v(8.93, -61.05) * mm, "end": v(8.5, -60.98) * mm});
            skLineSegment(sketch, "E1012", {"start": v(8.5, -60.98) * mm, "end": v(8.1, -60.92) * mm});
            skLineSegment(sketch, "E1013", {"start": v(8.1, -60.92) * mm, "end": v(7.7, -60.88) * mm});
            skLineSegment(sketch, "E1014", {"start": v(7.7, -60.88) * mm, "end": v(7.29, -60.86) * mm});
            skLineSegment(sketch, "E1015", {"start": v(7.29, -60.86) * mm, "end": v(6.88, -60.86) * mm});
            skLineSegment(sketch, "E1016", {"start": v(6.88, -60.86) * mm, "end": v(6.48, -60.88) * mm});
            skLineSegment(sketch, "E1017", {"start": v(6.48, -60.88) * mm, "end": v(6.07, -60.91) * mm});
            skLineSegment(sketch, "E1018", {"start": v(6.07, -60.91) * mm, "end": v(5.67, -60.96) * mm});
            skLineSegment(sketch, "E1019", {"start": v(5.67, -60.96) * mm, "end": v(5.26, -61.01) * mm});
            skLineSegment(sketch, "E1020", {"start": v(5.26, -61.01) * mm, "end": v(4.86, -61.08) * mm});
            skLineSegment(sketch, "E1021", {"start": v(4.86, -61.08) * mm, "end": v(4.46, -61.16) * mm});
            skLineSegment(sketch, "E1022", {"start": v(4.46, -61.16) * mm, "end": v(3.66, -61.34) * mm});
            skLineSegment(sketch, "E1023", {"start": v(3.66, -61.34) * mm, "end": v(2.87, -61.54) * mm});
            skLineSegment(sketch, "E1024", {"start": v(2.87, -61.54) * mm, "end": v(2.09, -61.75) * mm});
            skLineSegment(sketch, "E1025", {"start": v(2.09, -61.75) * mm, "end": v(0.77, -62.1) * mm});
            skLineSegment(sketch, "E1026", {"start": v(0.77, -62.1) * mm, "end": v(-0.55, -62.44) * mm});
            skLineSegment(sketch, "E1027", {"start": v(-0.55, -62.44) * mm, "end": v(-1.21, -62.6) * mm});
            skLineSegment(sketch, "E1028", {"start": v(-1.21, -62.6) * mm, "end": v(-1.88, -62.75) * mm});
            skLineSegment(sketch, "E1029", {"start": v(-1.88, -62.75) * mm, "end": v(-2.54, -62.89) * mm});
            skLineSegment(sketch, "E1030", {"start": v(-2.54, -62.89) * mm, "end": v(-3.2, -63.02) * mm});
            skLineSegment(sketch, "E1031", {"start": v(-3.2, -63.02) * mm, "end": v(-3.98, -63.16) * mm});
            skLineSegment(sketch, "E1032", {"start": v(-3.98, -63.16) * mm, "end": v(-4.85, -63.3) * mm});
            skLineSegment(sketch, "E1033", {"start": v(-4.85, -63.3) * mm, "end": v(-5.32, -63.37) * mm});
            skLineSegment(sketch, "E1034", {"start": v(-5.32, -63.37) * mm, "end": v(-5.8, -63.42) * mm});
            skLineSegment(sketch, "E1035", {"start": v(-5.8, -63.42) * mm, "end": v(-6.28, -63.46) * mm});
            skLineSegment(sketch, "E1036", {"start": v(-6.28, -63.46) * mm, "end": v(-6.77, -63.5) * mm});
            skLineSegment(sketch, "E1037", {"start": v(-6.77, -63.5) * mm, "end": v(-7.25, -63.5) * mm});
            skLineSegment(sketch, "E1038", {"start": v(-7.25, -63.5) * mm, "end": v(-7.73, -63.49) * mm});
            skLineSegment(sketch, "E1039", {"start": v(-7.73, -63.49) * mm, "end": v(-8.2, -63.45) * mm});
            skLineSegment(sketch, "E1040", {"start": v(-8.2, -63.45) * mm, "end": v(-8.42, -63.43) * mm});
            skLineSegment(sketch, "E1041", {"start": v(-8.42, -63.43) * mm, "end": v(-8.64, -63.4) * mm});
            skLineSegment(sketch, "E1042", {"start": v(-8.64, -63.4) * mm, "end": v(-8.86, -63.35) * mm});
            skLineSegment(sketch, "E1043", {"start": v(-8.86, -63.35) * mm, "end": v(-9.06, -63.3) * mm});
            skLineSegment(sketch, "E1044", {"start": v(-9.06, -63.3) * mm, "end": v(-9.27, -63.24) * mm});
            skLineSegment(sketch, "E1045", {"start": v(-9.27, -63.24) * mm, "end": v(-9.46, -63.18) * mm});
            skLineSegment(sketch, "E1046", {"start": v(-9.46, -63.18) * mm, "end": v(-9.65, -63.1) * mm});
            skLineSegment(sketch, "E1047", {"start": v(-9.65, -63.1) * mm, "end": v(-9.83, -63.02) * mm});
            skLineSegment(sketch, "E1048", {"start": v(-9.83, -63.02) * mm, "end": v(-10, -62.92) * mm});
            skLineSegment(sketch, "E1049", {"start": v(-10, -62.92) * mm, "end": v(-10.16, -62.82) * mm});
            skLineSegment(sketch, "E1050", {"start": v(-10.16, -62.82) * mm, "end": v(-11.37, -61.96) * mm});
            skLineSegment(sketch, "E1051", {"start": v(-11.37, -61.96) * mm, "end": v(-10.75, -61) * mm});
            skLineSegment(sketch, "E1052", {"start": v(-10.75, -61) * mm, "end": v(-10.72, -60.88) * mm});
            skLineSegment(sketch, "E1053", {"start": v(-10.72, -60.88) * mm, "end": v(-10.68, -60.77) * mm});
            skLineSegment(sketch, "E1054", {"start": v(-10.68, -60.77) * mm, "end": v(-10.64, -60.66) * mm});
            skLineSegment(sketch, "E1055", {"start": v(-10.64, -60.66) * mm, "end": v(-10.59, -60.56) * mm});
            skLineSegment(sketch, "E1056", {"start": v(-10.59, -60.56) * mm, "end": v(-10.53, -60.46) * mm});
            skLineSegment(sketch, "E1057", {"start": v(-10.53, -60.46) * mm, "end": v(-10.46, -60.37) * mm});
            skLineSegment(sketch, "E1058", {"start": v(-10.46, -60.37) * mm, "end": v(-10.31, -60.2) * mm});
            skLineSegment(sketch, "E1059", {"start": v(1.25, 61.06) * mm, "end": v(1.44, 61.06) * mm});
            skLineSegment(sketch, "E1060", {"start": v(1.44, 61.06) * mm, "end": v(1.63, 61.04) * mm});
            skLineSegment(sketch, "E1061", {"start": v(1.63, 61.04) * mm, "end": v(1.82, 61.02) * mm});
            skLineSegment(sketch, "E1062", {"start": v(1.82, 61.02) * mm, "end": v(2, 60.99) * mm});
            skLineSegment(sketch, "E1063", {"start": v(2, 60.99) * mm, "end": v(2.18, 60.95) * mm});
            skLineSegment(sketch, "E1064", {"start": v(2.18, 60.95) * mm, "end": v(2.36, 60.9) * mm});
            skLineSegment(sketch, "E1065", {"start": v(2.36, 60.9) * mm, "end": v(2.53, 60.84) * mm});
            skLineSegment(sketch, "E1066", {"start": v(2.53, 60.84) * mm, "end": v(2.7, 60.77) * mm});
            skLineSegment(sketch, "E1067", {"start": v(2.7, 60.77) * mm, "end": v(2.86, 60.7) * mm});
            skLineSegment(sketch, "E1068", {"start": v(2.86, 60.7) * mm, "end": v(3.02, 60.61) * mm});
            skLineSegment(sketch, "E1069", {"start": v(3.02, 60.61) * mm, "end": v(3.18, 60.52) * mm});
            skLineSegment(sketch, "E1070", {"start": v(3.18, 60.52) * mm, "end": v(3.33, 60.43) * mm});
            skLineSegment(sketch, "E1071", {"start": v(3.33, 60.43) * mm, "end": v(3.47, 60.32) * mm});
            skLineSegment(sketch, "E1072", {"start": v(3.47, 60.32) * mm, "end": v(3.62, 60.21) * mm});
            skLineSegment(sketch, "E1073", {"start": v(3.62, 60.21) * mm, "end": v(3.75, 60.1) * mm});
            skLineSegment(sketch, "E1074", {"start": v(3.75, 60.1) * mm, "end": v(3.88, 59.97) * mm});
            skLineSegment(sketch, "E1075", {"start": v(3.88, 59.97) * mm, "end": v(4, 59.85) * mm});
            skLineSegment(sketch, "E1076", {"start": v(4, 59.85) * mm, "end": v(4.12, 59.71) * mm});
            skLineSegment(sketch, "E1077", {"start": v(4.12, 59.71) * mm, "end": v(4.23, 59.57) * mm});
            skLineSegment(sketch, "E1078", {"start": v(4.23, 59.57) * mm, "end": v(4.33, 59.42) * mm});
            skLineSegment(sketch, "E1079", {"start": v(4.33, 59.42) * mm, "end": v(4.43, 59.27) * mm});
            skLineSegment(sketch, "E1080", {"start": v(4.43, 59.27) * mm, "end": v(4.52, 59.12) * mm});
            skLineSegment(sketch, "E1081", {"start": v(4.52, 59.12) * mm, "end": v(4.6, 58.96) * mm});
            skLineSegment(sketch, "E1082", {"start": v(4.6, 58.96) * mm, "end": v(4.68, 58.8) * mm});
            skLineSegment(sketch, "E1083", {"start": v(4.68, 58.8) * mm, "end": v(4.74, 58.62) * mm});
            skLineSegment(sketch, "E1084", {"start": v(4.74, 58.62) * mm, "end": v(4.8, 58.45) * mm});
            skLineSegment(sketch, "E1085", {"start": v(4.8, 58.45) * mm, "end": v(4.85, 58.27) * mm});
            skLineSegment(sketch, "E1086", {"start": v(4.85, 58.27) * mm, "end": v(4.9, 58.1) * mm});
            skLineSegment(sketch, "E1087", {"start": v(4.9, 58.1) * mm, "end": v(4.93, 57.91) * mm});
            skLineSegment(sketch, "E1088", {"start": v(4.93, 57.91) * mm, "end": v(4.95, 57.73) * mm});
            skLineSegment(sketch, "E1089", {"start": v(4.95, 57.73) * mm, "end": v(4.96, 57.54) * mm});
            skLineSegment(sketch, "E1090", {"start": v(4.96, 57.54) * mm, "end": v(4.97, 57.35) * mm});
            skLineSegment(sketch, "E1091", {"start": v(4.97, 57.35) * mm, "end": v(4.96, 57.15) * mm});
            skLineSegment(sketch, "E1092", {"start": v(4.96, 57.15) * mm, "end": v(4.95, 56.97) * mm});
            skLineSegment(sketch, "E1093", {"start": v(4.95, 56.97) * mm, "end": v(4.93, 56.78) * mm});
            skLineSegment(sketch, "E1094", {"start": v(4.93, 56.78) * mm, "end": v(4.9, 56.6) * mm});
            skLineSegment(sketch, "E1095", {"start": v(4.9, 56.6) * mm, "end": v(4.85, 56.42) * mm});
            skLineSegment(sketch, "E1096", {"start": v(4.85, 56.42) * mm, "end": v(4.8, 56.24) * mm});
            skLineSegment(sketch, "E1097", {"start": v(4.8, 56.24) * mm, "end": v(4.74, 56.07) * mm});
            skLineSegment(sketch, "E1098", {"start": v(4.74, 56.07) * mm, "end": v(4.68, 55.9) * mm});
            skLineSegment(sketch, "E1099", {"start": v(4.68, 55.9) * mm, "end": v(4.6, 55.73) * mm});
            skLineSegment(sketch, "E1100", {"start": v(4.6, 55.73) * mm, "end": v(4.52, 55.57) * mm});
            skLineSegment(sketch, "E1101", {"start": v(4.52, 55.57) * mm, "end": v(4.43, 55.42) * mm});
            skLineSegment(sketch, "E1102", {"start": v(4.43, 55.42) * mm, "end": v(4.33, 55.27) * mm});
            skLineSegment(sketch, "E1103", {"start": v(4.33, 55.27) * mm, "end": v(4.23, 55.12) * mm});
            skLineSegment(sketch, "E1104", {"start": v(4.23, 55.12) * mm, "end": v(4.12, 54.98) * mm});
            skLineSegment(sketch, "E1105", {"start": v(4.12, 54.98) * mm, "end": v(4, 54.85) * mm});
            skLineSegment(sketch, "E1106", {"start": v(4, 54.85) * mm, "end": v(3.88, 54.72) * mm});
            skLineSegment(sketch, "E1107", {"start": v(3.88, 54.72) * mm, "end": v(3.75, 54.6) * mm});
            skLineSegment(sketch, "E1108", {"start": v(3.75, 54.6) * mm, "end": v(3.62, 54.48) * mm});
            skLineSegment(sketch, "E1109", {"start": v(3.62, 54.48) * mm, "end": v(3.47, 54.37) * mm});
            skLineSegment(sketch, "E1110", {"start": v(3.47, 54.37) * mm, "end": v(3.33, 54.26) * mm});
            skLineSegment(sketch, "E1111", {"start": v(3.33, 54.26) * mm, "end": v(3.18, 54.17) * mm});
            skLineSegment(sketch, "E1112", {"start": v(3.18, 54.17) * mm, "end": v(3.02, 54.08) * mm});
            skLineSegment(sketch, "E1113", {"start": v(3.02, 54.08) * mm, "end": v(2.86, 54) * mm});
            skLineSegment(sketch, "E1114", {"start": v(2.86, 54) * mm, "end": v(2.7, 53.92) * mm});
            skLineSegment(sketch, "E1115", {"start": v(2.7, 53.92) * mm, "end": v(2.53, 53.85) * mm});
            skLineSegment(sketch, "E1116", {"start": v(2.53, 53.85) * mm, "end": v(2.36, 53.8) * mm});
            skLineSegment(sketch, "E1117", {"start": v(2.36, 53.8) * mm, "end": v(2.18, 53.75) * mm});
            skLineSegment(sketch, "E1118", {"start": v(2.18, 53.75) * mm, "end": v(2, 53.7) * mm});
            skLineSegment(sketch, "E1119", {"start": v(2, 53.7) * mm, "end": v(1.82, 53.67) * mm});
            skLineSegment(sketch, "E1120", {"start": v(1.82, 53.67) * mm, "end": v(1.63, 53.65) * mm});
            skLineSegment(sketch, "E1121", {"start": v(1.63, 53.65) * mm, "end": v(1.44, 53.63) * mm});
            skLineSegment(sketch, "E1122", {"start": v(1.44, 53.63) * mm, "end": v(1.25, 53.63) * mm});
            skLineSegment(sketch, "E1123", {"start": v(1.25, 53.63) * mm, "end": v(1.06, 53.63) * mm});
            skLineSegment(sketch, "E1124", {"start": v(1.06, 53.63) * mm, "end": v(0.87, 53.65) * mm});
            skLineSegment(sketch, "E1125", {"start": v(0.87, 53.65) * mm, "end": v(0.69, 53.67) * mm});
            skLineSegment(sketch, "E1126", {"start": v(0.69, 53.67) * mm, "end": v(0.5, 53.7) * mm});
            skLineSegment(sketch, "E1127", {"start": v(0.5, 53.7) * mm, "end": v(0.32, 53.75) * mm});
            skLineSegment(sketch, "E1128", {"start": v(0.32, 53.75) * mm, "end": v(0.15, 53.8) * mm});
            skLineSegment(sketch, "E1129", {"start": v(0.15, 53.8) * mm, "end": v(-0.03, 53.85) * mm});
            skLineSegment(sketch, "E1130", {"start": v(-0.03, 53.85) * mm, "end": v(-0.2, 53.92) * mm});
            skLineSegment(sketch, "E1131", {"start": v(-0.2, 53.92) * mm, "end": v(-0.36, 54) * mm});
            skLineSegment(sketch, "E1132", {"start": v(-0.36, 54) * mm, "end": v(-0.52, 54.08) * mm});
            skLineSegment(sketch, "E1133", {"start": v(-0.52, 54.08) * mm, "end": v(-0.68, 54.17) * mm});
            skLineSegment(sketch, "E1134", {"start": v(-0.68, 54.17) * mm, "end": v(-0.83, 54.26) * mm});
            skLineSegment(sketch, "E1135", {"start": v(-0.83, 54.26) * mm, "end": v(-0.97, 54.37) * mm});
            skLineSegment(sketch, "E1136", {"start": v(-0.97, 54.37) * mm, "end": v(-1.11, 54.48) * mm});
            skLineSegment(sketch, "E1137", {"start": v(-1.11, 54.48) * mm, "end": v(-1.25, 54.6) * mm});
            skLineSegment(sketch, "E1138", {"start": v(-1.25, 54.6) * mm, "end": v(-1.38, 54.72) * mm});
            skLineSegment(sketch, "E1139", {"start": v(-1.38, 54.72) * mm, "end": v(-1.5, 54.85) * mm});
            skLineSegment(sketch, "E1140", {"start": v(-1.5, 54.85) * mm, "end": v(-1.62, 54.98) * mm});
            skLineSegment(sketch, "E1141", {"start": v(-1.62, 54.98) * mm, "end": v(-1.73, 55.12) * mm});
            skLineSegment(sketch, "E1142", {"start": v(-1.73, 55.12) * mm, "end": v(-1.83, 55.27) * mm});
            skLineSegment(sketch, "E1143", {"start": v(-1.83, 55.27) * mm, "end": v(-1.93, 55.42) * mm});
            skLineSegment(sketch, "E1144", {"start": v(-1.93, 55.42) * mm, "end": v(-2.02, 55.57) * mm});
            skLineSegment(sketch, "E1145", {"start": v(-2.02, 55.57) * mm, "end": v(-2.1, 55.73) * mm});
            skLineSegment(sketch, "E1146", {"start": v(-2.1, 55.73) * mm, "end": v(-2.17, 55.9) * mm});
            skLineSegment(sketch, "E1147", {"start": v(-2.17, 55.9) * mm, "end": v(-2.24, 56.07) * mm});
            skLineSegment(sketch, "E1148", {"start": v(-2.24, 56.07) * mm, "end": v(-2.3, 56.24) * mm});
            skLineSegment(sketch, "E1149", {"start": v(-2.3, 56.24) * mm, "end": v(-2.35, 56.42) * mm});
            skLineSegment(sketch, "E1150", {"start": v(-2.35, 56.42) * mm, "end": v(-2.4, 56.6) * mm});
            skLineSegment(sketch, "E1151", {"start": v(-2.4, 56.6) * mm, "end": v(-2.42, 56.78) * mm});
            skLineSegment(sketch, "E1152", {"start": v(-2.42, 56.78) * mm, "end": v(-2.45, 56.97) * mm});
            skLineSegment(sketch, "E1153", {"start": v(-2.45, 56.97) * mm, "end": v(-2.46, 57.15) * mm});
            skLineSegment(sketch, "E1154", {"start": v(-2.46, 57.15) * mm, "end": v(-2.47, 57.35) * mm});
            skLineSegment(sketch, "E1155", {"start": v(-2.47, 57.35) * mm, "end": v(-2.46, 57.54) * mm});
            skLineSegment(sketch, "E1156", {"start": v(-2.46, 57.54) * mm, "end": v(-2.45, 57.73) * mm});
            skLineSegment(sketch, "E1157", {"start": v(-2.45, 57.73) * mm, "end": v(-2.42, 57.91) * mm});
            skLineSegment(sketch, "E1158", {"start": v(-2.42, 57.91) * mm, "end": v(-2.4, 58.1) * mm});
            skLineSegment(sketch, "E1159", {"start": v(-2.4, 58.1) * mm, "end": v(-2.35, 58.27) * mm});
            skLineSegment(sketch, "E1160", {"start": v(-2.35, 58.27) * mm, "end": v(-2.3, 58.45) * mm});
            skLineSegment(sketch, "E1161", {"start": v(-2.3, 58.45) * mm, "end": v(-2.24, 58.62) * mm});
            skLineSegment(sketch, "E1162", {"start": v(-2.24, 58.62) * mm, "end": v(-2.17, 58.8) * mm});
            skLineSegment(sketch, "E1163", {"start": v(-2.17, 58.8) * mm, "end": v(-2.1, 58.96) * mm});
            skLineSegment(sketch, "E1164", {"start": v(-2.1, 58.96) * mm, "end": v(-2.02, 59.12) * mm});
            skLineSegment(sketch, "E1165", {"start": v(-2.02, 59.12) * mm, "end": v(-1.93, 59.27) * mm});
            skLineSegment(sketch, "E1166", {"start": v(-1.93, 59.27) * mm, "end": v(-1.83, 59.42) * mm});
            skLineSegment(sketch, "E1167", {"start": v(-1.83, 59.42) * mm, "end": v(-1.73, 59.57) * mm});
            skLineSegment(sketch, "E1168", {"start": v(-1.73, 59.57) * mm, "end": v(-1.62, 59.71) * mm});
            skLineSegment(sketch, "E1169", {"start": v(-1.62, 59.71) * mm, "end": v(-1.5, 59.85) * mm});
            skLineSegment(sketch, "E1170", {"start": v(-1.5, 59.85) * mm, "end": v(-1.38, 59.97) * mm});
            skLineSegment(sketch, "E1171", {"start": v(-1.38, 59.97) * mm, "end": v(-1.25, 60.1) * mm});
            skLineSegment(sketch, "E1172", {"start": v(-1.25, 60.1) * mm, "end": v(-1.11, 60.21) * mm});
            skLineSegment(sketch, "E1173", {"start": v(-1.11, 60.21) * mm, "end": v(-0.97, 60.32) * mm});
            skLineSegment(sketch, "E1174", {"start": v(-0.97, 60.32) * mm, "end": v(-0.83, 60.43) * mm});
            skLineSegment(sketch, "E1175", {"start": v(-0.83, 60.43) * mm, "end": v(-0.68, 60.52) * mm});
            skLineSegment(sketch, "E1176", {"start": v(-0.68, 60.52) * mm, "end": v(-0.52, 60.61) * mm});
            skLineSegment(sketch, "E1177", {"start": v(-0.52, 60.61) * mm, "end": v(-0.36, 60.7) * mm});
            skLineSegment(sketch, "E1178", {"start": v(-0.36, 60.7) * mm, "end": v(-0.2, 60.77) * mm});
            skLineSegment(sketch, "E1179", {"start": v(-0.2, 60.77) * mm, "end": v(-0.03, 60.84) * mm});
            skLineSegment(sketch, "E1180", {"start": v(-0.03, 60.84) * mm, "end": v(0.15, 60.9) * mm});
            skLineSegment(sketch, "E1181", {"start": v(0.15, 60.9) * mm, "end": v(0.32, 60.95) * mm});
            skLineSegment(sketch, "E1182", {"start": v(0.32, 60.95) * mm, "end": v(0.5, 60.99) * mm});
            skLineSegment(sketch, "E1183", {"start": v(0.5, 60.99) * mm, "end": v(0.69, 61.02) * mm});
            skLineSegment(sketch, "E1184", {"start": v(0.69, 61.02) * mm, "end": v(0.87, 61.04) * mm});
            skLineSegment(sketch, "E1185", {"start": v(0.87, 61.04) * mm, "end": v(1.06, 61.06) * mm});
            skLineSegment(sketch, "E1186", {"start": v(1.06, 61.06) * mm, "end": v(1.25, 61.06) * mm});
            skLineSegment(sketch, "E1187", {"start": v(-24.05, -34) * mm, "end": v(-23.88, -34.1) * mm});
            skLineSegment(sketch, "E1188", {"start": v(-23.88, -34.1) * mm, "end": v(-23.7, -34.2) * mm});
            skLineSegment(sketch, "E1189", {"start": v(-23.7, -34.2) * mm, "end": v(-23.55, -34.32) * mm});
            skLineSegment(sketch, "E1190", {"start": v(-23.55, -34.32) * mm, "end": v(-23.4, -34.46) * mm});
            skLineSegment(sketch, "E1191", {"start": v(-23.4, -34.46) * mm, "end": v(-23.26, -34.6) * mm});
            skLineSegment(sketch, "E1192", {"start": v(-23.26, -34.6) * mm, "end": v(-23.13, -34.75) * mm});
            skLineSegment(sketch, "E1193", {"start": v(-23.13, -34.75) * mm, "end": v(-23, -34.9) * mm});
            skLineSegment(sketch, "E1194", {"start": v(-23, -34.9) * mm, "end": v(-22.9, -35.07) * mm});
            skLineSegment(sketch, "E1195", {"start": v(-22.9, -35.07) * mm, "end": v(-22.8, -35.25) * mm});
            skLineSegment(sketch, "E1196", {"start": v(-22.8, -35.25) * mm, "end": v(-22.7, -35.43) * mm});
            skLineSegment(sketch, "E1197", {"start": v(-22.7, -35.43) * mm, "end": v(-22.63, -35.62) * mm});
            skLineSegment(sketch, "E1198", {"start": v(-22.63, -35.62) * mm, "end": v(-22.57, -35.81) * mm});
            skLineSegment(sketch, "E1199", {"start": v(-22.57, -35.81) * mm, "end": v(-22.52, -36.01) * mm});
            skLineSegment(sketch, "E1200", {"start": v(-22.52, -36.01) * mm, "end": v(-22.48, -36.22) * mm});
            skLineSegment(sketch, "E1201", {"start": v(-22.48, -36.22) * mm, "end": v(-22.46, -36.43) * mm});
            skLineSegment(sketch, "E1202", {"start": v(-22.46, -36.43) * mm, "end": v(-22.45, -36.64) * mm});
            skLineSegment(sketch, "E1203", {"start": v(-22.45, -36.64) * mm, "end": v(-22.46, -36.8) * mm});
            skLineSegment(sketch, "E1204", {"start": v(-22.46, -36.8) * mm, "end": v(-22.47, -36.95) * mm});
            skLineSegment(sketch, "E1205", {"start": v(-22.47, -36.95) * mm, "end": v(-22.52, -37.25) * mm});
            skLineSegment(sketch, "E1206", {"start": v(-22.52, -37.25) * mm, "end": v(-22.59, -37.53) * mm});
            skLineSegment(sketch, "E1207", {"start": v(-22.59, -37.53) * mm, "end": v(-22.7, -37.8) * mm});
            skLineSegment(sketch, "E1208", {"start": v(-22.7, -37.8) * mm, "end": v(-22.82, -38.07) * mm});
            skLineSegment(sketch, "E1209", {"start": v(-22.82, -38.07) * mm, "end": v(-22.97, -38.32) * mm});
            skLineSegment(sketch, "E1210", {"start": v(-22.97, -38.32) * mm, "end": v(-23.14, -38.55) * mm});
            skLineSegment(sketch, "E1211", {"start": v(-23.14, -38.55) * mm, "end": v(-23.33, -38.76) * mm});
            skLineSegment(sketch, "E1212", {"start": v(-23.33, -38.76) * mm, "end": v(-23.55, -38.96) * mm});
            skLineSegment(sketch, "E1213", {"start": v(-23.55, -38.96) * mm, "end": v(-23.78, -39.13) * mm});
            skLineSegment(sketch, "E1214", {"start": v(-23.78, -39.13) * mm, "end": v(-24.02, -39.28) * mm});
            skLineSegment(sketch, "E1215", {"start": v(-24.02, -39.28) * mm, "end": v(-24.29, -39.4) * mm});
            skLineSegment(sketch, "E1216", {"start": v(-24.29, -39.4) * mm, "end": v(-24.56, -39.5) * mm});
            skLineSegment(sketch, "E1217", {"start": v(-24.56, -39.5) * mm, "end": v(-24.85, -39.58) * mm});
            skLineSegment(sketch, "E1218", {"start": v(-24.85, -39.58) * mm, "end": v(-25, -39.6) * mm});
            skLineSegment(sketch, "E1219", {"start": v(-25, -39.6) * mm, "end": v(-25.15, -39.63) * mm});
            skLineSegment(sketch, "E1220", {"start": v(-25.15, -39.63) * mm, "end": v(-25.3, -39.64) * mm});
            skLineSegment(sketch, "E1221", {"start": v(-25.3, -39.64) * mm, "end": v(-25.45, -39.64) * mm});
            skLineSegment(sketch, "E1222", {"start": v(-25.45, -39.64) * mm, "end": v(-25.6, -39.64) * mm});
            skLineSegment(sketch, "E1223", {"start": v(-25.6, -39.64) * mm, "end": v(-25.76, -39.63) * mm});
            skLineSegment(sketch, "E1224", {"start": v(-25.76, -39.63) * mm, "end": v(-26.06, -39.58) * mm});
            skLineSegment(sketch, "E1225", {"start": v(-26.06, -39.58) * mm, "end": v(-26.35, -39.5) * mm});
            skLineSegment(sketch, "E1226", {"start": v(-26.35, -39.5) * mm, "end": v(-26.62, -39.4) * mm});
            skLineSegment(sketch, "E1227", {"start": v(-26.62, -39.4) * mm, "end": v(-26.88, -39.28) * mm});
            skLineSegment(sketch, "E1228", {"start": v(-26.88, -39.28) * mm, "end": v(-27.13, -39.13) * mm});
            skLineSegment(sketch, "E1229", {"start": v(-27.13, -39.13) * mm, "end": v(-27.36, -38.96) * mm});
            skLineSegment(sketch, "E1230", {"start": v(-27.36, -38.96) * mm, "end": v(-27.58, -38.76) * mm});
            skLineSegment(sketch, "E1231", {"start": v(-27.58, -38.76) * mm, "end": v(-27.77, -38.55) * mm});
            skLineSegment(sketch, "E1232", {"start": v(-27.77, -38.55) * mm, "end": v(-27.94, -38.32) * mm});
            skLineSegment(sketch, "E1233", {"start": v(-27.94, -38.32) * mm, "end": v(-28.1, -38.07) * mm});
            skLineSegment(sketch, "E1234", {"start": v(-28.1, -38.07) * mm, "end": v(-28.22, -37.8) * mm});
            skLineSegment(sketch, "E1235", {"start": v(-28.22, -37.8) * mm, "end": v(-28.32, -37.53) * mm});
            skLineSegment(sketch, "E1236", {"start": v(-28.32, -37.53) * mm, "end": v(-28.4, -37.25) * mm});
            skLineSegment(sketch, "E1237", {"start": v(-28.4, -37.25) * mm, "end": v(-28.42, -37.1) * mm});
            skLineSegment(sketch, "E1238", {"start": v(-28.42, -37.1) * mm, "end": v(-28.44, -36.95) * mm});
            skLineSegment(sketch, "E1239", {"start": v(-28.44, -36.95) * mm, "end": v(-28.45, -36.8) * mm});
            skLineSegment(sketch, "E1240", {"start": v(-28.45, -36.8) * mm, "end": v(-28.45, -36.64) * mm});
            skLineSegment(sketch, "E1241", {"start": v(-28.45, -36.64) * mm, "end": v(-28.45, -36.46) * mm});
            skLineSegment(sketch, "E1242", {"start": v(-28.45, -36.46) * mm, "end": v(-28.43, -36.28) * mm});
            skLineSegment(sketch, "E1243", {"start": v(-28.43, -36.28) * mm, "end": v(-28.4, -36.1) * mm});
            skLineSegment(sketch, "E1244", {"start": v(-28.4, -36.1) * mm, "end": v(-28.37, -35.93) * mm});
            skLineSegment(sketch, "E1245", {"start": v(-28.37, -35.93) * mm, "end": v(-28.73, -36.04) * mm});
            skLineSegment(sketch, "E1246", {"start": v(-28.73, -36.04) * mm, "end": v(-28.8, -36.13) * mm});
            skLineSegment(sketch, "E1247", {"start": v(-28.8, -36.13) * mm, "end": v(-28.98, -36.33) * mm});
            skLineSegment(sketch, "E1248", {"start": v(-28.98, -36.33) * mm, "end": v(-29.15, -36.54) * mm});
            skLineSegment(sketch, "E1249", {"start": v(-29.15, -36.54) * mm, "end": v(-29.44, -36.93) * mm});
            skLineSegment(sketch, "E1250", {"start": v(-29.44, -36.93) * mm, "end": v(-29.72, -37.32) * mm});
            skLineSegment(sketch, "E1251", {"start": v(-29.72, -37.32) * mm, "end": v(-30.25, -38.14) * mm});
            skLineSegment(sketch, "E1252", {"start": v(-30.25, -38.14) * mm, "end": v(-30.79, -38.96) * mm});
            skLineSegment(sketch, "E1253", {"start": v(-30.79, -38.96) * mm, "end": v(-31.06, -39.37) * mm});
            skLineSegment(sketch, "E1254", {"start": v(-31.06, -39.37) * mm, "end": v(-31.34, -39.76) * mm});
            skLineSegment(sketch, "E1255", {"start": v(-31.34, -39.76) * mm, "end": v(-31.9, -40.52) * mm});
            skLineSegment(sketch, "E1256", {"start": v(-31.9, -40.52) * mm, "end": v(-32.49, -41.26) * mm});
            skLineSegment(sketch, "E1257", {"start": v(-32.49, -41.26) * mm, "end": v(-33.1, -41.98) * mm});
            skLineSegment(sketch, "E1258", {"start": v(-33.1, -41.98) * mm, "end": v(-33.72, -42.68) * mm});
            skLineSegment(sketch, "E1259", {"start": v(-33.72, -42.68) * mm, "end": v(-34.36, -43.37) * mm});
            skLineSegment(sketch, "E1260", {"start": v(-34.36, -43.37) * mm, "end": v(-35.01, -44.05) * mm});
            skLineSegment(sketch, "E1261", {"start": v(-35.01, -44.05) * mm, "end": v(-35.68, -44.71) * mm});
            skLineSegment(sketch, "E1262", {"start": v(-35.68, -44.71) * mm, "end": v(-36.36, -45.36) * mm});
            skLineSegment(sketch, "E1263", {"start": v(-36.36, -45.36) * mm, "end": v(-36.78, -45.75) * mm});
            skLineSegment(sketch, "E1264", {"start": v(-36.78, -45.75) * mm, "end": v(-37.39, -46.3) * mm});
            skLineSegment(sketch, "E1265", {"start": v(-37.39, -46.3) * mm, "end": v(-37.7, -46.62) * mm});
            skLineSegment(sketch, "E1266", {"start": v(-37.7, -46.62) * mm, "end": v(-38, -46.92) * mm});
            skLineSegment(sketch, "E1267", {"start": v(-38, -46.92) * mm, "end": v(-38.27, -47.2) * mm});
            skLineSegment(sketch, "E1268", {"start": v(-38.27, -47.2) * mm, "end": v(-38.37, -47.32) * mm});
            skLineSegment(sketch, "E1269", {"start": v(-38.37, -47.32) * mm, "end": v(-38.46, -47.44) * mm});
            skLineSegment(sketch, "E1270", {"start": v(-38.46, -47.44) * mm, "end": v(-38.36, -47.5) * mm});
            skLineSegment(sketch, "E1271", {"start": v(-38.36, -47.5) * mm, "end": v(-38.18, -47.61) * mm});
            skLineSegment(sketch, "E1272", {"start": v(-38.18, -47.61) * mm, "end": v(-38, -47.7) * mm});
            skLineSegment(sketch, "E1273", {"start": v(-38, -47.7) * mm, "end": v(-37.8, -47.75) * mm});
            skLineSegment(sketch, "E1274", {"start": v(-37.8, -47.75) * mm, "end": v(-37.6, -47.79) * mm});
            skLineSegment(sketch, "E1275", {"start": v(-37.6, -47.79) * mm, "end": v(-37.38, -47.8) * mm});
            skLineSegment(sketch, "E1276", {"start": v(-37.38, -47.8) * mm, "end": v(-37.16, -47.8) * mm});
            skLineSegment(sketch, "E1277", {"start": v(-37.16, -47.8) * mm, "end": v(-36.94, -47.77) * mm});
            skLineSegment(sketch, "E1278", {"start": v(-36.94, -47.77) * mm, "end": v(-36.71, -47.74) * mm});
            skLineSegment(sketch, "E1279", {"start": v(-36.71, -47.74) * mm, "end": v(-36.27, -47.64) * mm});
            skLineSegment(sketch, "E1280", {"start": v(-36.27, -47.64) * mm, "end": v(-35.85, -47.52) * mm});
            skLineSegment(sketch, "E1281", {"start": v(-35.85, -47.52) * mm, "end": v(-35.18, -47.3) * mm});
            skLineSegment(sketch, "E1282", {"start": v(-35.18, -47.3) * mm, "end": v(-34.5, -47.07) * mm});
            skLineSegment(sketch, "E1283", {"start": v(-34.5, -47.07) * mm, "end": v(-33.83, -46.84) * mm});
            skLineSegment(sketch, "E1284", {"start": v(-33.83, -46.84) * mm, "end": v(-33.16, -46.62) * mm});
            skLineSegment(sketch, "E1285", {"start": v(-33.16, -46.62) * mm, "end": v(-32.64, -46.48) * mm});
            skLineSegment(sketch, "E1286", {"start": v(-32.64, -46.48) * mm, "end": v(-32.13, -46.35) * mm});
            skLineSegment(sketch, "E1287", {"start": v(-32.13, -46.35) * mm, "end": v(-31.62, -46.24) * mm});
            skLineSegment(sketch, "E1288", {"start": v(-31.62, -46.24) * mm, "end": v(-31.12, -46.15) * mm});
            skLineSegment(sketch, "E1289", {"start": v(-31.12, -46.15) * mm, "end": v(-30.63, -46.08) * mm});
            skLineSegment(sketch, "E1290", {"start": v(-30.63, -46.08) * mm, "end": v(-30.13, -46.04) * mm});
            skLineSegment(sketch, "E1291", {"start": v(-30.13, -46.04) * mm, "end": v(-29.64, -46.01) * mm});
            skLineSegment(sketch, "E1292", {"start": v(-29.64, -46.01) * mm, "end": v(-29.15, -46) * mm});
            skLineSegment(sketch, "E1293", {"start": v(-29.15, -46) * mm, "end": v(-28.66, -46.03) * mm});
            skLineSegment(sketch, "E1294", {"start": v(-28.66, -46.03) * mm, "end": v(-28.17, -46.07) * mm});
            skLineSegment(sketch, "E1295", {"start": v(-28.17, -46.07) * mm, "end": v(-27.68, -46.13) * mm});
            skLineSegment(sketch, "E1296", {"start": v(-27.68, -46.13) * mm, "end": v(-27.18, -46.22) * mm});
            skLineSegment(sketch, "E1297", {"start": v(-27.18, -46.22) * mm, "end": v(-26.69, -46.34) * mm});
            skLineSegment(sketch, "E1298", {"start": v(-26.69, -46.34) * mm, "end": v(-26.19, -46.47) * mm});
            skLineSegment(sketch, "E1299", {"start": v(-26.19, -46.47) * mm, "end": v(-25.69, -46.64) * mm});
            skLineSegment(sketch, "E1300", {"start": v(-25.69, -46.64) * mm, "end": v(-25.18, -46.83) * mm});
            skLineSegment(sketch, "E1301", {"start": v(-25.18, -46.83) * mm, "end": v(-24.62, -47.06) * mm});
            skLineSegment(sketch, "E1302", {"start": v(-24.62, -47.06) * mm, "end": v(-24.09, -47.32) * mm});
            skLineSegment(sketch, "E1303", {"start": v(-24.09, -47.32) * mm, "end": v(-23.82, -47.46) * mm});
            skLineSegment(sketch, "E1304", {"start": v(-23.82, -47.46) * mm, "end": v(-23.56, -47.6) * mm});
            skLineSegment(sketch, "E1305", {"start": v(-23.56, -47.6) * mm, "end": v(-23.3, -47.76) * mm});
            skLineSegment(sketch, "E1306", {"start": v(-23.3, -47.76) * mm, "end": v(-23.05, -47.92) * mm});
            skLineSegment(sketch, "E1307", {"start": v(-23.05, -47.92) * mm, "end": v(-22.71, -48.15) * mm});
            skLineSegment(sketch, "E1308", {"start": v(-22.71, -48.15) * mm, "end": v(-22.38, -48.39) * mm});
            skLineSegment(sketch, "E1309", {"start": v(-22.38, -48.39) * mm, "end": v(-21.72, -48.87) * mm});
            skLineSegment(sketch, "E1310", {"start": v(-21.72, -48.87) * mm, "end": v(-21.5, -49.01) * mm});
            skLineSegment(sketch, "E1311", {"start": v(-21.5, -49.01) * mm, "end": v(-21.3, -49.14) * mm});
            skLineSegment(sketch, "E1312", {"start": v(-21.3, -49.14) * mm, "end": v(-21.1, -49.26) * mm});
            skLineSegment(sketch, "E1313", {"start": v(-21.1, -49.26) * mm, "end": v(-20.88, -49.37) * mm});
            skLineSegment(sketch, "E1314", {"start": v(-20.88, -49.37) * mm, "end": v(-20.67, -49.47) * mm});
            skLineSegment(sketch, "E1315", {"start": v(-20.67, -49.47) * mm, "end": v(-20.45, -49.56) * mm});
            skLineSegment(sketch, "E1316", {"start": v(-20.45, -49.56) * mm, "end": v(-20.22, -49.64) * mm});
            skLineSegment(sketch, "E1317", {"start": v(-20.22, -49.64) * mm, "end": v(-19.97, -49.71) * mm});
            skLineSegment(sketch, "E1318", {"start": v(-19.97, -49.71) * mm, "end": v(-19.58, -49.8) * mm});
            skLineSegment(sketch, "E1319", {"start": v(-19.58, -49.8) * mm, "end": v(-19.18, -49.87) * mm});
            skLineSegment(sketch, "E1320", {"start": v(-19.18, -49.87) * mm, "end": v(-18.78, -49.92) * mm});
            skLineSegment(sketch, "E1321", {"start": v(-18.78, -49.92) * mm, "end": v(-18.37, -49.95) * mm});
            skLineSegment(sketch, "E1322", {"start": v(-18.37, -49.95) * mm, "end": v(-17.96, -49.96) * mm});
            skLineSegment(sketch, "E1323", {"start": v(-17.96, -49.96) * mm, "end": v(-17.54, -49.95) * mm});
            skLineSegment(sketch, "E1324", {"start": v(-17.54, -49.95) * mm, "end": v(-17.12, -49.93) * mm});
            skLineSegment(sketch, "E1325", {"start": v(-17.12, -49.93) * mm, "end": v(-16.7, -49.89) * mm});
            skLineSegment(sketch, "E1326", {"start": v(-16.7, -49.89) * mm, "end": v(-16.29, -49.84) * mm});
            skLineSegment(sketch, "E1327", {"start": v(-16.29, -49.84) * mm, "end": v(-15.87, -49.77) * mm});
            skLineSegment(sketch, "E1328", {"start": v(-15.87, -49.77) * mm, "end": v(-15.46, -49.7) * mm});
            skLineSegment(sketch, "E1329", {"start": v(-15.46, -49.7) * mm, "end": v(-15.05, -49.6) * mm});
            skLineSegment(sketch, "E1330", {"start": v(-15.05, -49.6) * mm, "end": v(-14.65, -49.5) * mm});
            skLineSegment(sketch, "E1331", {"start": v(-14.65, -49.5) * mm, "end": v(-14.26, -49.4) * mm});
            skLineSegment(sketch, "E1332", {"start": v(-14.26, -49.4) * mm, "end": v(-13.87, -49.29) * mm});
            skLineSegment(sketch, "E1333", {"start": v(-13.87, -49.29) * mm, "end": v(-13.5, -49.17) * mm});
            skLineSegment(sketch, "E1334", {"start": v(-13.5, -49.17) * mm, "end": v(-12.97, -49.01) * mm});
            skLineSegment(sketch, "E1335", {"start": v(-12.97, -49.01) * mm, "end": v(-12.45, -48.88) * mm});
            skLineSegment(sketch, "E1336", {"start": v(-12.45, -48.88) * mm, "end": v(-11.94, -48.78) * mm});
            skLineSegment(sketch, "E1337", {"start": v(-11.94, -48.78) * mm, "end": v(-11.44, -48.7) * mm});
            skLineSegment(sketch, "E1338", {"start": v(-11.44, -48.7) * mm, "end": v(-10.94, -48.64) * mm});
            skLineSegment(sketch, "E1339", {"start": v(-10.94, -48.64) * mm, "end": v(-10.44, -48.6) * mm});
            skLineSegment(sketch, "E1340", {"start": v(-10.44, -48.6) * mm, "end": v(-9.95, -48.6) * mm});
            skLineSegment(sketch, "E1341", {"start": v(-9.95, -48.6) * mm, "end": v(-9.46, -48.6) * mm});
            skLineSegment(sketch, "E1342", {"start": v(-9.46, -48.6) * mm, "end": v(-8.97, -48.63) * mm});
            skLineSegment(sketch, "E1343", {"start": v(-8.97, -48.63) * mm, "end": v(-8.48, -48.68) * mm});
            skLineSegment(sketch, "E1344", {"start": v(-8.48, -48.68) * mm, "end": v(-7.99, -48.75) * mm});
            skLineSegment(sketch, "E1345", {"start": v(-7.99, -48.75) * mm, "end": v(-7.49, -48.83) * mm});
            skLineSegment(sketch, "E1346", {"start": v(-7.49, -48.83) * mm, "end": v(-6.99, -48.93) * mm});
            skLineSegment(sketch, "E1347", {"start": v(-6.99, -48.93) * mm, "end": v(-6.48, -49.05) * mm});
            skLineSegment(sketch, "E1348", {"start": v(-6.48, -49.05) * mm, "end": v(-5.97, -49.18) * mm});
            skLineSegment(sketch, "E1349", {"start": v(-5.97, -49.18) * mm, "end": v(-5.45, -49.32) * mm});
            skLineSegment(sketch, "E1350", {"start": v(-5.45, -49.32) * mm, "end": v(-4.62, -49.57) * mm});
            skLineSegment(sketch, "E1351", {"start": v(-4.62, -49.57) * mm, "end": v(-3.8, -49.82) * mm});
            skLineSegment(sketch, "E1352", {"start": v(-3.8, -49.82) * mm, "end": v(-2.97, -50.06) * mm});
            skLineSegment(sketch, "E1353", {"start": v(-2.97, -50.06) * mm, "end": v(-2.56, -50.17) * mm});
            skLineSegment(sketch, "E1354", {"start": v(-2.56, -50.17) * mm, "end": v(-2.15, -50.28) * mm});
            skLineSegment(sketch, "E1355", {"start": v(-2.15, -50.28) * mm, "end": v(-1.74, -50.37) * mm});
            skLineSegment(sketch, "E1356", {"start": v(-1.74, -50.37) * mm, "end": v(-1.32, -50.46) * mm});
            skLineSegment(sketch, "E1357", {"start": v(-1.32, -50.46) * mm, "end": v(-0.9, -50.53) * mm});
            skLineSegment(sketch, "E1358", {"start": v(-0.9, -50.53) * mm, "end": v(-0.48, -50.58) * mm});
            skLineSegment(sketch, "E1359", {"start": v(-0.48, -50.58) * mm, "end": v(-0.05, -50.62) * mm});
            skLineSegment(sketch, "E1360", {"start": v(-0.05, -50.62) * mm, "end": v(0.38, -50.65) * mm});
            skLineSegment(sketch, "E1361", {"start": v(0.38, -50.65) * mm, "end": v(0.81, -50.65) * mm});
            skLineSegment(sketch, "E1362", {"start": v(0.81, -50.65) * mm, "end": v(1.25, -50.63) * mm});
            skLineSegment(sketch, "E1363", {"start": v(1.25, -50.63) * mm, "end": v(1.56, -50.6) * mm});
            skLineSegment(sketch, "E1364", {"start": v(1.56, -50.6) * mm, "end": v(1.85, -50.55) * mm});
            skLineSegment(sketch, "E1365", {"start": v(1.85, -50.55) * mm, "end": v(2.13, -50.5) * mm});
            skLineSegment(sketch, "E1366", {"start": v(2.13, -50.5) * mm, "end": v(2.41, -50.42) * mm});
            skLineSegment(sketch, "E1367", {"start": v(2.41, -50.42) * mm, "end": v(2.69, -50.33) * mm});
            skLineSegment(sketch, "E1368", {"start": v(2.69, -50.33) * mm, "end": v(2.96, -50.23) * mm});
            skLineSegment(sketch, "E1369", {"start": v(2.96, -50.23) * mm, "end": v(3.24, -50.12) * mm});
            skLineSegment(sketch, "E1370", {"start": v(3.24, -50.12) * mm, "end": v(3.52, -50) * mm});
            skLineSegment(sketch, "E1371", {"start": v(3.52, -50) * mm, "end": v(4.55, -49.51) * mm});
            skLineSegment(sketch, "E1372", {"start": v(4.55, -49.51) * mm, "end": v(5.05, -49.28) * mm});
            skLineSegment(sketch, "E1373", {"start": v(5.05, -49.28) * mm, "end": v(5.55, -49.07) * mm});
            skLineSegment(sketch, "E1374", {"start": v(5.55, -49.07) * mm, "end": v(6.05, -48.86) * mm});
            skLineSegment(sketch, "E1375", {"start": v(6.05, -48.86) * mm, "end": v(6.57, -48.68) * mm});
            skLineSegment(sketch, "E1376", {"start": v(6.57, -48.68) * mm, "end": v(6.83, -48.6) * mm});
            skLineSegment(sketch, "E1377", {"start": v(6.83, -48.6) * mm, "end": v(7.1, -48.51) * mm});
            skLineSegment(sketch, "E1378", {"start": v(7.1, -48.51) * mm, "end": v(7.4, -48.44) * mm});
            skLineSegment(sketch, "E1379", {"start": v(7.4, -48.44) * mm, "end": v(7.69, -48.37) * mm});
            skLineSegment(sketch, "E1380", {"start": v(7.69, -48.37) * mm, "end": v(8.14, -48.29) * mm});
            skLineSegment(sketch, "E1381", {"start": v(8.14, -48.29) * mm, "end": v(8.6, -48.22) * mm});
            skLineSegment(sketch, "E1382", {"start": v(8.6, -48.22) * mm, "end": v(9.06, -48.18) * mm});
            skLineSegment(sketch, "E1383", {"start": v(9.06, -48.18) * mm, "end": v(9.52, -48.15) * mm});
            skLineSegment(sketch, "E1384", {"start": v(9.52, -48.15) * mm, "end": v(9.99, -48.13) * mm});
            skLineSegment(sketch, "E1385", {"start": v(9.99, -48.13) * mm, "end": v(10.45, -48.14) * mm});
            skLineSegment(sketch, "E1386", {"start": v(10.45, -48.14) * mm, "end": v(10.91, -48.16) * mm});
            skLineSegment(sketch, "E1387", {"start": v(10.91, -48.16) * mm, "end": v(11.38, -48.19) * mm});
            skLineSegment(sketch, "E1388", {"start": v(11.38, -48.19) * mm, "end": v(11.84, -48.23) * mm});
            skLineSegment(sketch, "E1389", {"start": v(11.84, -48.23) * mm, "end": v(12.3, -48.3) * mm});
            skLineSegment(sketch, "E1390", {"start": v(12.3, -48.3) * mm, "end": v(12.76, -48.36) * mm});
            skLineSegment(sketch, "E1391", {"start": v(12.76, -48.36) * mm, "end": v(13.22, -48.44) * mm});
            skLineSegment(sketch, "E1392", {"start": v(13.22, -48.44) * mm, "end": v(13.67, -48.53) * mm});
            skLineSegment(sketch, "E1393", {"start": v(13.67, -48.53) * mm, "end": v(14.12, -48.63) * mm});
            skLineSegment(sketch, "E1394", {"start": v(14.12, -48.63) * mm, "end": v(15.02, -48.85) * mm});
            skLineSegment(sketch, "E1395", {"start": v(15.02, -48.85) * mm, "end": v(15.84, -49.07) * mm});
            skLineSegment(sketch, "E1396", {"start": v(15.84, -49.07) * mm, "end": v(16.59, -49.27) * mm});
            skLineSegment(sketch, "E1397", {"start": v(16.59, -49.27) * mm, "end": v(16.94, -49.35) * mm});
            skLineSegment(sketch, "E1398", {"start": v(16.94, -49.35) * mm, "end": v(17.29, -49.43) * mm});
            skLineSegment(sketch, "E1399", {"start": v(17.29, -49.43) * mm, "end": v(17.63, -49.5) * mm});
            skLineSegment(sketch, "E1400", {"start": v(17.63, -49.5) * mm, "end": v(17.96, -49.54) * mm});
            skLineSegment(sketch, "E1401", {"start": v(17.96, -49.54) * mm, "end": v(18.3, -49.57) * mm});
            skLineSegment(sketch, "E1402", {"start": v(18.3, -49.57) * mm, "end": v(18.64, -49.58) * mm});
            skLineSegment(sketch, "E1403", {"start": v(18.64, -49.58) * mm, "end": v(18.99, -49.56) * mm});
            skLineSegment(sketch, "E1404", {"start": v(18.99, -49.56) * mm, "end": v(19.34, -49.53) * mm});
            skLineSegment(sketch, "E1405", {"start": v(19.34, -49.53) * mm, "end": v(19.7, -49.46) * mm});
            skLineSegment(sketch, "E1406", {"start": v(19.7, -49.46) * mm, "end": v(20.1, -49.37) * mm});
            skLineSegment(sketch, "E1407", {"start": v(20.1, -49.37) * mm, "end": v(20.5, -49.25) * mm});
            skLineSegment(sketch, "E1408", {"start": v(20.5, -49.25) * mm, "end": v(20.91, -49.1) * mm});
            skLineSegment(sketch, "E1409", {"start": v(20.91, -49.1) * mm, "end": v(21.26, -48.95) * mm});
            skLineSegment(sketch, "E1410", {"start": v(21.26, -48.95) * mm, "end": v(21.6, -48.79) * mm});
            skLineSegment(sketch, "E1411", {"start": v(21.6, -48.79) * mm, "end": v(21.95, -48.62) * mm});
            skLineSegment(sketch, "E1412", {"start": v(21.95, -48.62) * mm, "end": v(22.28, -48.44) * mm});
            skLineSegment(sketch, "E1413", {"start": v(22.28, -48.44) * mm, "end": v(22.94, -48.06) * mm});
            skLineSegment(sketch, "E1414", {"start": v(22.94, -48.06) * mm, "end": v(23.58, -47.67) * mm});
            skLineSegment(sketch, "E1415", {"start": v(23.58, -47.67) * mm, "end": v(24.23, -47.27) * mm});
            skLineSegment(sketch, "E1416", {"start": v(24.23, -47.27) * mm, "end": v(24.88, -46.88) * mm});
            skLineSegment(sketch, "E1417", {"start": v(24.88, -46.88) * mm, "end": v(25.22, -46.7) * mm});
            skLineSegment(sketch, "E1418", {"start": v(25.22, -46.7) * mm, "end": v(25.55, -46.52) * mm});
            skLineSegment(sketch, "E1419", {"start": v(25.55, -46.52) * mm, "end": v(25.9, -46.35) * mm});
            skLineSegment(sketch, "E1420", {"start": v(25.9, -46.35) * mm, "end": v(26.25, -46.19) * mm});
            skLineSegment(sketch, "E1421", {"start": v(26.25, -46.19) * mm, "end": v(26.5, -46.08) * mm});
            skLineSegment(sketch, "E1422", {"start": v(26.5, -46.08) * mm, "end": v(26.75, -45.99) * mm});
            skLineSegment(sketch, "E1423", {"start": v(26.75, -45.99) * mm, "end": v(27, -45.9) * mm});
            skLineSegment(sketch, "E1424", {"start": v(27, -45.9) * mm, "end": v(27.25, -45.82) * mm});
            skLineSegment(sketch, "E1425", {"start": v(27.25, -45.82) * mm, "end": v(27.5, -45.76) * mm});
            skLineSegment(sketch, "E1426", {"start": v(27.5, -45.76) * mm, "end": v(27.75, -45.7) * mm});
            skLineSegment(sketch, "E1427", {"start": v(27.75, -45.7) * mm, "end": v(28.25, -45.6) * mm});
            skLineSegment(sketch, "E1428", {"start": v(28.25, -45.6) * mm, "end": v(28.75, -45.53) * mm});
            skLineSegment(sketch, "E1429", {"start": v(28.75, -45.53) * mm, "end": v(29.25, -45.5) * mm});
            skLineSegment(sketch, "E1430", {"start": v(29.25, -45.5) * mm, "end": v(29.74, -45.48) * mm});
            skLineSegment(sketch, "E1431", {"start": v(29.74, -45.48) * mm, "end": v(30.24, -45.5) * mm});
            skLineSegment(sketch, "E1432", {"start": v(30.24, -45.5) * mm, "end": v(30.74, -45.53) * mm});
            skLineSegment(sketch, "E1433", {"start": v(30.74, -45.53) * mm, "end": v(31.23, -45.58) * mm});
            skLineSegment(sketch, "E1434", {"start": v(31.23, -45.58) * mm, "end": v(31.73, -45.66) * mm});
            skLineSegment(sketch, "E1435", {"start": v(31.73, -45.66) * mm, "end": v(32.23, -45.76) * mm});
            skLineSegment(sketch, "E1436", {"start": v(32.23, -45.76) * mm, "end": v(32.73, -45.87) * mm});
            skLineSegment(sketch, "E1437", {"start": v(32.73, -45.87) * mm, "end": v(33.23, -46) * mm});
            skLineSegment(sketch, "E1438", {"start": v(33.23, -46) * mm, "end": v(33.73, -46.13) * mm});
            skLineSegment(sketch, "E1439", {"start": v(33.73, -46.13) * mm, "end": v(34.23, -46.28) * mm});
            skLineSegment(sketch, "E1440", {"start": v(34.23, -46.28) * mm, "end": v(35.2, -46.6) * mm});
            skLineSegment(sketch, "E1441", {"start": v(35.2, -46.6) * mm, "end": v(35.8, -46.8) * mm});
            skLineSegment(sketch, "E1442", {"start": v(35.8, -46.8) * mm, "end": v(36.46, -46.99) * mm});
            skLineSegment(sketch, "E1443", {"start": v(36.46, -46.99) * mm, "end": v(36.8, -47.07) * mm});
            skLineSegment(sketch, "E1444", {"start": v(36.8, -47.07) * mm, "end": v(37.11, -47.15) * mm});
            skLineSegment(sketch, "E1445", {"start": v(37.11, -47.15) * mm, "end": v(37.43, -47.22) * mm});
            skLineSegment(sketch, "E1446", {"start": v(37.43, -47.22) * mm, "end": v(37.73, -47.26) * mm});
            skLineSegment(sketch, "E1447", {"start": v(37.73, -47.26) * mm, "end": v(38.01, -47.3) * mm});
            skLineSegment(sketch, "E1448", {"start": v(38.01, -47.3) * mm, "end": v(38.27, -47.3) * mm});
            skLineSegment(sketch, "E1449", {"start": v(38.27, -47.3) * mm, "end": v(38.5, -47.28) * mm});
            skLineSegment(sketch, "E1450", {"start": v(38.5, -47.28) * mm, "end": v(38.6, -47.27) * mm});
            skLineSegment(sketch, "E1451", {"start": v(38.6, -47.27) * mm, "end": v(38.7, -47.24) * mm});
            skLineSegment(sketch, "E1452", {"start": v(38.7, -47.24) * mm, "end": v(38.6, -47) * mm});
            skLineSegment(sketch, "E1453", {"start": v(38.6, -47) * mm, "end": v(38.5, -46.77) * mm});
            skLineSegment(sketch, "E1454", {"start": v(38.5, -46.77) * mm, "end": v(38.36, -46.52) * mm});
            skLineSegment(sketch, "E1455", {"start": v(38.36, -46.52) * mm, "end": v(38.2, -46.27) * mm});
            skLineSegment(sketch, "E1456", {"start": v(38.2, -46.27) * mm, "end": v(38.03, -46.02) * mm});
            skLineSegment(sketch, "E1457", {"start": v(38.03, -46.02) * mm, "end": v(37.84, -45.77) * mm});
            skLineSegment(sketch, "E1458", {"start": v(37.84, -45.77) * mm, "end": v(37.64, -45.53) * mm});
            skLineSegment(sketch, "E1459", {"start": v(37.64, -45.53) * mm, "end": v(37.43, -45.29) * mm});
            skLineSegment(sketch, "E1460", {"start": v(37.43, -45.29) * mm, "end": v(37, -44.83) * mm});
            skLineSegment(sketch, "E1461", {"start": v(37, -44.83) * mm, "end": v(36.59, -44.42) * mm});
            skLineSegment(sketch, "E1462", {"start": v(36.59, -44.42) * mm, "end": v(36.2, -44.07) * mm});
            skLineSegment(sketch, "E1463", {"start": v(36.2, -44.07) * mm, "end": v(35.9, -43.79) * mm});
            skLineSegment(sketch, "E1464", {"start": v(35.9, -43.79) * mm, "end": v(35.52, -43.45) * mm});
            skLineSegment(sketch, "E1465", {"start": v(35.52, -43.45) * mm, "end": v(35.16, -43.11) * mm});
            skLineSegment(sketch, "E1466", {"start": v(35.16, -43.11) * mm, "end": v(34.83, -42.76) * mm});
            skLineSegment(sketch, "E1467", {"start": v(34.83, -42.76) * mm, "end": v(34.5, -42.38) * mm});
            skLineSegment(sketch, "E1468", {"start": v(34.5, -42.38) * mm, "end": v(34.08, -41.88) * mm});
            skLineSegment(sketch, "E1469", {"start": v(34.08, -41.88) * mm, "end": v(33.87, -41.63) * mm});
            skLineSegment(sketch, "E1470", {"start": v(33.87, -41.63) * mm, "end": v(33.66, -41.39) * mm});
            skLineSegment(sketch, "E1471", {"start": v(33.66, -41.39) * mm, "end": v(33.37, -41.06) * mm});
            skLineSegment(sketch, "E1472", {"start": v(33.37, -41.06) * mm, "end": v(33.1, -40.73) * mm});
            skLineSegment(sketch, "E1473", {"start": v(33.1, -40.73) * mm, "end": v(32.82, -40.4) * mm});
            skLineSegment(sketch, "E1474", {"start": v(32.82, -40.4) * mm, "end": v(32.55, -40.04) * mm});
            skLineSegment(sketch, "E1475", {"start": v(32.55, -40.04) * mm, "end": v(32.03, -39.34) * mm});
            skLineSegment(sketch, "E1476", {"start": v(32.03, -39.34) * mm, "end": v(31.53, -38.64) * mm});
            skLineSegment(sketch, "E1477", {"start": v(31.53, -38.64) * mm, "end": v(31.03, -37.96) * mm});
            skLineSegment(sketch, "E1478", {"start": v(31.03, -37.96) * mm, "end": v(30.8, -37.67) * mm});
            skLineSegment(sketch, "E1479", {"start": v(30.8, -37.67) * mm, "end": v(30.6, -37.43) * mm});
            skLineSegment(sketch, "E1480", {"start": v(30.6, -37.43) * mm, "end": v(30.41, -37.2) * mm});
            skLineSegment(sketch, "E1481", {"start": v(30.41, -37.2) * mm, "end": v(30.23, -37.01) * mm});
            skLineSegment(sketch, "E1482", {"start": v(30.23, -37.01) * mm, "end": v(30.04, -36.84) * mm});
            skLineSegment(sketch, "E1483", {"start": v(30.04, -36.84) * mm, "end": v(29.86, -36.7) * mm});
            skLineSegment(sketch, "E1484", {"start": v(29.86, -36.7) * mm, "end": v(29.67, -36.55) * mm});
            skLineSegment(sketch, "E1485", {"start": v(29.67, -36.55) * mm, "end": v(29.46, -36.42) * mm});
            skLineSegment(sketch, "E1486", {"start": v(29.46, -36.42) * mm, "end": v(29.25, -36.3) * mm});
            skLineSegment(sketch, "E1487", {"start": v(29.25, -36.3) * mm, "end": v(29, -36.18) * mm});
            skLineSegment(sketch, "E1488", {"start": v(29, -36.18) * mm, "end": v(28.46, -35.92) * mm});
            skLineSegment(sketch, "E1489", {"start": v(28.46, -35.92) * mm, "end": v(27.78, -35.63) * mm});
            skLineSegment(sketch, "E1490", {"start": v(27.78, -35.63) * mm, "end": v(27.85, -35.78) * mm});
            skLineSegment(sketch, "E1491", {"start": v(27.85, -35.78) * mm, "end": v(27.9, -35.94) * mm});
            skLineSegment(sketch, "E1492", {"start": v(27.9, -35.94) * mm, "end": v(27.96, -36.1) * mm});
            skLineSegment(sketch, "E1493", {"start": v(27.96, -36.1) * mm, "end": v(28, -36.26) * mm});
            skLineSegment(sketch, "E1494", {"start": v(28, -36.26) * mm, "end": v(28.04, -36.43) * mm});
            skLineSegment(sketch, "E1495", {"start": v(28.04, -36.43) * mm, "end": v(28.06, -36.6) * mm});
            skLineSegment(sketch, "E1496", {"start": v(28.06, -36.6) * mm, "end": v(28.08, -36.77) * mm});
            skLineSegment(sketch, "E1497", {"start": v(28.08, -36.77) * mm, "end": v(28.08, -36.95) * mm});
            skLineSegment(sketch, "E1498", {"start": v(28.08, -36.95) * mm, "end": v(28.08, -37.1) * mm});
            skLineSegment(sketch, "E1499", {"start": v(28.08, -37.1) * mm, "end": v(28.07, -37.26) * mm});
            skLineSegment(sketch, "E1500", {"start": v(28.07, -37.26) * mm, "end": v(28.02, -37.55) * mm});
            skLineSegment(sketch, "E1501", {"start": v(28.02, -37.55) * mm, "end": v(27.95, -37.84) * mm});
            skLineSegment(sketch, "E1502", {"start": v(27.95, -37.84) * mm, "end": v(27.85, -38.12) * mm});
            skLineSegment(sketch, "E1503", {"start": v(27.85, -38.12) * mm, "end": v(27.72, -38.38) * mm});
            skLineSegment(sketch, "E1504", {"start": v(27.72, -38.38) * mm, "end": v(27.57, -38.63) * mm});
            skLineSegment(sketch, "E1505", {"start": v(27.57, -38.63) * mm, "end": v(27.4, -38.86) * mm});
            skLineSegment(sketch, "E1506", {"start": v(27.4, -38.86) * mm, "end": v(27.2, -39.07) * mm});
            skLineSegment(sketch, "E1507", {"start": v(27.2, -39.07) * mm, "end": v(27, -39.26) * mm});
            skLineSegment(sketch, "E1508", {"start": v(27, -39.26) * mm, "end": v(26.76, -39.44) * mm});
            skLineSegment(sketch, "E1509", {"start": v(26.76, -39.44) * mm, "end": v(26.51, -39.59) * mm});
            skLineSegment(sketch, "E1510", {"start": v(26.51, -39.59) * mm, "end": v(26.25, -39.71) * mm});
            skLineSegment(sketch, "E1511", {"start": v(26.25, -39.71) * mm, "end": v(25.98, -39.81) * mm});
            skLineSegment(sketch, "E1512", {"start": v(25.98, -39.81) * mm, "end": v(25.69, -39.89) * mm});
            skLineSegment(sketch, "E1513", {"start": v(25.69, -39.89) * mm, "end": v(25.54, -39.91) * mm});
            skLineSegment(sketch, "E1514", {"start": v(25.54, -39.91) * mm, "end": v(25.4, -39.93) * mm});
            skLineSegment(sketch, "E1515", {"start": v(25.4, -39.93) * mm, "end": v(25.24, -39.95) * mm});
            skLineSegment(sketch, "E1516", {"start": v(25.24, -39.95) * mm, "end": v(25.08, -39.95) * mm});
            skLineSegment(sketch, "E1517", {"start": v(25.08, -39.95) * mm, "end": v(24.93, -39.95) * mm});
            skLineSegment(sketch, "E1518", {"start": v(24.93, -39.95) * mm, "end": v(24.78, -39.93) * mm});
            skLineSegment(sketch, "E1519", {"start": v(24.78, -39.93) * mm, "end": v(24.48, -39.89) * mm});
            skLineSegment(sketch, "E1520", {"start": v(24.48, -39.89) * mm, "end": v(24.2, -39.81) * mm});
            skLineSegment(sketch, "E1521", {"start": v(24.2, -39.81) * mm, "end": v(23.92, -39.71) * mm});
            skLineSegment(sketch, "E1522", {"start": v(23.92, -39.71) * mm, "end": v(23.65, -39.59) * mm});
            skLineSegment(sketch, "E1523", {"start": v(23.65, -39.59) * mm, "end": v(23.4, -39.44) * mm});
            skLineSegment(sketch, "E1524", {"start": v(23.4, -39.44) * mm, "end": v(23.18, -39.26) * mm});
            skLineSegment(sketch, "E1525", {"start": v(23.18, -39.26) * mm, "end": v(22.96, -39.07) * mm});
            skLineSegment(sketch, "E1526", {"start": v(22.96, -39.07) * mm, "end": v(22.77, -38.86) * mm});
            skLineSegment(sketch, "E1527", {"start": v(22.77, -38.86) * mm, "end": v(22.6, -38.63) * mm});
            skLineSegment(sketch, "E1528", {"start": v(22.6, -38.63) * mm, "end": v(22.45, -38.38) * mm});
            skLineSegment(sketch, "E1529", {"start": v(22.45, -38.38) * mm, "end": v(22.32, -38.12) * mm});
            skLineSegment(sketch, "E1530", {"start": v(22.32, -38.12) * mm, "end": v(22.22, -37.84) * mm});
            skLineSegment(sketch, "E1531", {"start": v(22.22, -37.84) * mm, "end": v(22.15, -37.55) * mm});
            skLineSegment(sketch, "E1532", {"start": v(22.15, -37.55) * mm, "end": v(22.12, -37.4) * mm});
            skLineSegment(sketch, "E1533", {"start": v(22.12, -37.4) * mm, "end": v(22.1, -37.26) * mm});
            skLineSegment(sketch, "E1534", {"start": v(22.1, -37.26) * mm, "end": v(22.09, -37.1) * mm});
            skLineSegment(sketch, "E1535", {"start": v(22.09, -37.1) * mm, "end": v(22.08, -36.95) * mm});
            skLineSegment(sketch, "E1536", {"start": v(22.08, -36.95) * mm, "end": v(22.1, -36.75) * mm});
            skLineSegment(sketch, "E1537", {"start": v(22.1, -36.75) * mm, "end": v(22.11, -36.54) * mm});
            skLineSegment(sketch, "E1538", {"start": v(22.11, -36.54) * mm, "end": v(22.14, -36.35) * mm});
            skLineSegment(sketch, "E1539", {"start": v(22.14, -36.35) * mm, "end": v(22.2, -36.16) * mm});
            skLineSegment(sketch, "E1540", {"start": v(22.2, -36.16) * mm, "end": v(22.25, -35.97) * mm});
            skLineSegment(sketch, "E1541", {"start": v(22.25, -35.97) * mm, "end": v(22.32, -35.79) * mm});
            skLineSegment(sketch, "E1542", {"start": v(22.32, -35.79) * mm, "end": v(22.4, -35.61) * mm});
            skLineSegment(sketch, "E1543", {"start": v(22.4, -35.61) * mm, "end": v(22.49, -35.44) * mm});
            skLineSegment(sketch, "E1544", {"start": v(22.49, -35.44) * mm, "end": v(22.6, -35.28) * mm});
            skLineSegment(sketch, "E1545", {"start": v(22.6, -35.28) * mm, "end": v(22.7, -35.13) * mm});
            skLineSegment(sketch, "E1546", {"start": v(22.7, -35.13) * mm, "end": v(22.82, -34.98) * mm});
            skLineSegment(sketch, "E1547", {"start": v(22.82, -34.98) * mm, "end": v(22.95, -34.84) * mm});
            skLineSegment(sketch, "E1548", {"start": v(22.95, -34.84) * mm, "end": v(23.1, -34.7) * mm});
            skLineSegment(sketch, "E1549", {"start": v(23.1, -34.7) * mm, "end": v(23.24, -34.58) * mm});
            skLineSegment(sketch, "E1550", {"start": v(23.24, -34.58) * mm, "end": v(23.4, -34.47) * mm});
            skLineSegment(sketch, "E1551", {"start": v(23.4, -34.47) * mm, "end": v(23.55, -34.37) * mm});
            skLineSegment(sketch, "E1552", {"start": v(23.55, -34.37) * mm, "end": v(23.28, -34.37) * mm});
            skLineSegment(sketch, "E1553", {"start": v(23.28, -34.37) * mm, "end": v(23, -34.39) * mm});
            skLineSegment(sketch, "E1554", {"start": v(23, -34.39) * mm, "end": v(22.7, -34.42) * mm});
            skLineSegment(sketch, "E1555", {"start": v(22.7, -34.42) * mm, "end": v(22.42, -34.47) * mm});
            skLineSegment(sketch, "E1556", {"start": v(22.42, -34.47) * mm, "end": v(22.03, -34.54) * mm});
            skLineSegment(sketch, "E1557", {"start": v(22.03, -34.54) * mm, "end": v(18.55, -36.78) * mm});
            skLineSegment(sketch, "E1558", {"start": v(18.55, -36.78) * mm, "end": v(18.53, -36.8) * mm});
            skLineSegment(sketch, "E1559", {"start": v(18.53, -36.8) * mm, "end": v(17.99, -37.13) * mm});
            skLineSegment(sketch, "E1560", {"start": v(17.99, -37.13) * mm, "end": v(17.41, -37.47) * mm});
            skLineSegment(sketch, "E1561", {"start": v(17.41, -37.47) * mm, "end": v(16.82, -37.82) * mm});
            skLineSegment(sketch, "E1562", {"start": v(16.82, -37.82) * mm, "end": v(16.2, -38.16) * mm});
            skLineSegment(sketch, "E1563", {"start": v(16.2, -38.16) * mm, "end": v(15.89, -38.32) * mm});
            skLineSegment(sketch, "E1564", {"start": v(15.89, -38.32) * mm, "end": v(15.57, -38.46) * mm});
            skLineSegment(sketch, "E1565", {"start": v(15.57, -38.46) * mm, "end": v(15.26, -38.6) * mm});
            skLineSegment(sketch, "E1566", {"start": v(15.26, -38.6) * mm, "end": v(14.94, -38.71) * mm});
            skLineSegment(sketch, "E1567", {"start": v(14.94, -38.71) * mm, "end": v(14.63, -38.81) * mm});
            skLineSegment(sketch, "E1568", {"start": v(14.63, -38.81) * mm, "end": v(14.31, -38.9) * mm});
            skLineSegment(sketch, "E1569", {"start": v(14.31, -38.9) * mm, "end": v(14, -38.95) * mm});
            skLineSegment(sketch, "E1570", {"start": v(14, -38.95) * mm, "end": v(13.69, -38.99) * mm});
            skLineSegment(sketch, "E1571", {"start": v(13.69, -38.99) * mm, "end": v(13.49, -39) * mm});
            skLineSegment(sketch, "E1572", {"start": v(13.49, -39) * mm, "end": v(13.29, -39) * mm});
            skLineSegment(sketch, "E1573", {"start": v(13.29, -39) * mm, "end": v(13.09, -39) * mm});
            skLineSegment(sketch, "E1574", {"start": v(13.09, -39) * mm, "end": v(12.9, -38.97) * mm});
            skLineSegment(sketch, "E1575", {"start": v(12.9, -38.97) * mm, "end": v(12.5, -38.91) * mm});
            skLineSegment(sketch, "E1576", {"start": v(12.5, -38.91) * mm, "end": v(12.12, -38.83) * mm});
            skLineSegment(sketch, "E1577", {"start": v(12.12, -38.83) * mm, "end": v(11.75, -38.72) * mm});
            skLineSegment(sketch, "E1578", {"start": v(11.75, -38.72) * mm, "end": v(11.37, -38.58) * mm});
            skLineSegment(sketch, "E1579", {"start": v(11.37, -38.58) * mm, "end": v(11, -38.44) * mm});
            skLineSegment(sketch, "E1580", {"start": v(11, -38.44) * mm, "end": v(10.64, -38.27) * mm});
            skLineSegment(sketch, "E1581", {"start": v(10.64, -38.27) * mm, "end": v(9.86, -37.9) * mm});
            skLineSegment(sketch, "E1582", {"start": v(9.86, -37.9) * mm, "end": v(9.08, -37.5) * mm});
            skLineSegment(sketch, "E1583", {"start": v(9.08, -37.5) * mm, "end": v(9.12, -37.66) * mm});
            skLineSegment(sketch, "E1584", {"start": v(9.12, -37.66) * mm, "end": v(9.14, -37.83) * mm});
            skLineSegment(sketch, "E1585", {"start": v(9.14, -37.83) * mm, "end": v(9.16, -38) * mm});
            skLineSegment(sketch, "E1586", {"start": v(9.16, -38) * mm, "end": v(9.16, -38.18) * mm});
            skLineSegment(sketch, "E1587", {"start": v(9.16, -38.18) * mm, "end": v(9.16, -38.33) * mm});
            skLineSegment(sketch, "E1588", {"start": v(9.16, -38.33) * mm, "end": v(9.15, -38.49) * mm});
            skLineSegment(sketch, "E1589", {"start": v(9.15, -38.49) * mm, "end": v(9.1, -38.78) * mm});
            skLineSegment(sketch, "E1590", {"start": v(9.1, -38.78) * mm, "end": v(9.03, -39.07) * mm});
            skLineSegment(sketch, "E1591", {"start": v(9.03, -39.07) * mm, "end": v(8.93, -39.35) * mm});
            skLineSegment(sketch, "E1592", {"start": v(8.93, -39.35) * mm, "end": v(8.8, -39.6) * mm});
            skLineSegment(sketch, "E1593", {"start": v(8.8, -39.6) * mm, "end": v(8.65, -39.86) * mm});
            skLineSegment(sketch, "E1594", {"start": v(8.65, -39.86) * mm, "end": v(8.48, -40.09) * mm});
            skLineSegment(sketch, "E1595", {"start": v(8.48, -40.09) * mm, "end": v(8.28, -40.3) * mm});
            skLineSegment(sketch, "E1596", {"start": v(8.28, -40.3) * mm, "end": v(8.07, -40.5) * mm});
            skLineSegment(sketch, "E1597", {"start": v(8.07, -40.5) * mm, "end": v(7.84, -40.67) * mm});
            skLineSegment(sketch, "E1598", {"start": v(7.84, -40.67) * mm, "end": v(7.6, -40.82) * mm});
            skLineSegment(sketch, "E1599", {"start": v(7.6, -40.82) * mm, "end": v(7.33, -40.94) * mm});
            skLineSegment(sketch, "E1600", {"start": v(7.33, -40.94) * mm, "end": v(7.05, -41.05) * mm});
            skLineSegment(sketch, "E1601", {"start": v(7.05, -41.05) * mm, "end": v(6.77, -41.12) * mm});
            skLineSegment(sketch, "E1602", {"start": v(6.77, -41.12) * mm, "end": v(6.62, -41.15) * mm});
            skLineSegment(sketch, "E1603", {"start": v(6.62, -41.15) * mm, "end": v(6.47, -41.16) * mm});
            skLineSegment(sketch, "E1604", {"start": v(6.47, -41.16) * mm, "end": v(6.32, -41.18) * mm});
            skLineSegment(sketch, "E1605", {"start": v(6.32, -41.18) * mm, "end": v(6.16, -41.18) * mm});
            skLineSegment(sketch, "E1606", {"start": v(6.16, -41.18) * mm, "end": v(6, -41.18) * mm});
            skLineSegment(sketch, "E1607", {"start": v(6, -41.18) * mm, "end": v(5.85, -41.16) * mm});
            skLineSegment(sketch, "E1608", {"start": v(5.85, -41.16) * mm, "end": v(5.56, -41.12) * mm});
            skLineSegment(sketch, "E1609", {"start": v(5.56, -41.12) * mm, "end": v(5.27, -41.05) * mm});
            skLineSegment(sketch, "E1610", {"start": v(5.27, -41.05) * mm, "end": v(5, -40.94) * mm});
            skLineSegment(sketch, "E1611", {"start": v(5, -40.94) * mm, "end": v(4.73, -40.82) * mm});
            skLineSegment(sketch, "E1612", {"start": v(4.73, -40.82) * mm, "end": v(4.48, -40.67) * mm});
            skLineSegment(sketch, "E1613", {"start": v(4.48, -40.67) * mm, "end": v(4.25, -40.5) * mm});
            skLineSegment(sketch, "E1614", {"start": v(4.25, -40.5) * mm, "end": v(4.04, -40.3) * mm});
            skLineSegment(sketch, "E1615", {"start": v(4.04, -40.3) * mm, "end": v(3.85, -40.09) * mm});
            skLineSegment(sketch, "E1616", {"start": v(3.85, -40.09) * mm, "end": v(3.67, -39.86) * mm});
            skLineSegment(sketch, "E1617", {"start": v(3.67, -39.86) * mm, "end": v(3.52, -39.6) * mm});
            skLineSegment(sketch, "E1618", {"start": v(3.52, -39.6) * mm, "end": v(3.4, -39.35) * mm});
            skLineSegment(sketch, "E1619", {"start": v(3.4, -39.35) * mm, "end": v(3.3, -39.07) * mm});
            skLineSegment(sketch, "E1620", {"start": v(3.3, -39.07) * mm, "end": v(3.22, -38.78) * mm});
            skLineSegment(sketch, "E1621", {"start": v(3.22, -38.78) * mm, "end": v(3.2, -38.64) * mm});
            skLineSegment(sketch, "E1622", {"start": v(3.2, -38.64) * mm, "end": v(3.18, -38.49) * mm});
            skLineSegment(sketch, "E1623", {"start": v(3.18, -38.49) * mm, "end": v(3.17, -38.33) * mm});
            skLineSegment(sketch, "E1624", {"start": v(3.17, -38.33) * mm, "end": v(3.16, -38.18) * mm});
            skLineSegment(sketch, "E1625", {"start": v(3.16, -38.18) * mm, "end": v(3.17, -37.94) * mm});
            skLineSegment(sketch, "E1626", {"start": v(3.17, -37.94) * mm, "end": v(3.2, -37.7) * mm});
            skLineSegment(sketch, "E1627", {"start": v(3.2, -37.7) * mm, "end": v(3.25, -37.47) * mm});
            skLineSegment(sketch, "E1628", {"start": v(3.25, -37.47) * mm, "end": v(3.3, -37.25) * mm});
            skLineSegment(sketch, "E1629", {"start": v(3.3, -37.25) * mm, "end": v(3.4, -37.03) * mm});
            skLineSegment(sketch, "E1630", {"start": v(3.4, -37.03) * mm, "end": v(3.49, -36.82) * mm});
            skLineSegment(sketch, "E1631", {"start": v(3.49, -36.82) * mm, "end": v(3.6, -36.62) * mm});
            skLineSegment(sketch, "E1632", {"start": v(3.6, -36.62) * mm, "end": v(3.72, -36.43) * mm});
            skLineSegment(sketch, "E1633", {"start": v(3.72, -36.43) * mm, "end": v(3.86, -36.25) * mm});
            skLineSegment(sketch, "E1634", {"start": v(3.86, -36.25) * mm, "end": v(4.02, -36.08) * mm});
            skLineSegment(sketch, "E1635", {"start": v(4.02, -36.08) * mm, "end": v(4.18, -35.93) * mm});
            skLineSegment(sketch, "E1636", {"start": v(4.18, -35.93) * mm, "end": v(4.36, -35.78) * mm});
            skLineSegment(sketch, "E1637", {"start": v(4.36, -35.78) * mm, "end": v(4.54, -35.65) * mm});
            skLineSegment(sketch, "E1638", {"start": v(4.54, -35.65) * mm, "end": v(4.74, -35.54) * mm});
            skLineSegment(sketch, "E1639", {"start": v(4.74, -35.54) * mm, "end": v(4.95, -35.44) * mm});
            skLineSegment(sketch, "E1640", {"start": v(4.95, -35.44) * mm, "end": v(5.16, -35.35) * mm});
            skLineSegment(sketch, "E1641", {"start": v(5.16, -35.35) * mm, "end": v(4.36, -34.95) * mm});
            skLineSegment(sketch, "E1642", {"start": v(4.36, -34.95) * mm, "end": v(3.95, -34.76) * mm});
            skLineSegment(sketch, "E1643", {"start": v(3.95, -34.76) * mm, "end": v(3.54, -34.58) * mm});
            skLineSegment(sketch, "E1644", {"start": v(3.54, -34.58) * mm, "end": v(3.11, -34.4) * mm});
            skLineSegment(sketch, "E1645", {"start": v(3.11, -34.4) * mm, "end": v(2.68, -34.24) * mm});
            skLineSegment(sketch, "E1646", {"start": v(2.68, -34.24) * mm, "end": v(2.25, -34.1) * mm});
            skLineSegment(sketch, "E1647", {"start": v(2.25, -34.1) * mm, "end": v(1.82, -33.97) * mm});
            skLineSegment(sketch, "E1648", {"start": v(1.82, -33.97) * mm, "end": v(1.4, -33.86) * mm});
            skLineSegment(sketch, "E1649", {"start": v(1.4, -33.86) * mm, "end": v(0.96, -33.77) * mm});
            skLineSegment(sketch, "E1650", {"start": v(0.96, -33.77) * mm, "end": v(0.54, -33.71) * mm});
            skLineSegment(sketch, "E1651", {"start": v(0.54, -33.71) * mm, "end": v(0.12, -33.68) * mm});
            skLineSegment(sketch, "E1652", {"start": v(0.12, -33.68) * mm, "end": v(-0.1, -33.67) * mm});
            skLineSegment(sketch, "E1653", {"start": v(-0.1, -33.67) * mm, "end": v(-0.3, -33.68) * mm});
            skLineSegment(sketch, "E1654", {"start": v(-0.3, -33.68) * mm, "end": v(-0.5, -33.69) * mm});
            skLineSegment(sketch, "E1655", {"start": v(-0.5, -33.69) * mm, "end": v(-0.7, -33.7) * mm});
            skLineSegment(sketch, "E1656", {"start": v(-0.7, -33.7) * mm, "end": v(-0.9, -33.74) * mm});
            skLineSegment(sketch, "E1657", {"start": v(-0.9, -33.74) * mm, "end": v(-1.1, -33.77) * mm});
            skLineSegment(sketch, "E1658", {"start": v(-1.1, -33.77) * mm, "end": v(-1.3, -33.82) * mm});
            skLineSegment(sketch, "E1659", {"start": v(-1.3, -33.82) * mm, "end": v(-1.5, -33.88) * mm});
            skLineSegment(sketch, "E1660", {"start": v(-1.5, -33.88) * mm, "end": v(-1.76, -33.96) * mm});
            skLineSegment(sketch, "E1661", {"start": v(-1.76, -33.96) * mm, "end": v(-2.1, -34.05) * mm});
            skLineSegment(sketch, "E1662", {"start": v(-2.1, -34.05) * mm, "end": v(-2.43, -34.16) * mm});
            skLineSegment(sketch, "E1663", {"start": v(-2.43, -34.16) * mm, "end": v(-2.57, -34.22) * mm});
            skLineSegment(sketch, "E1664", {"start": v(-2.57, -34.22) * mm, "end": v(-2.68, -34.27) * mm});
            skLineSegment(sketch, "E1665", {"start": v(-2.68, -34.27) * mm, "end": v(-4.38, -35.3) * mm});
            skLineSegment(sketch, "E1666", {"start": v(-4.38, -35.3) * mm, "end": v(-4.47, -35.34) * mm});
            skLineSegment(sketch, "E1667", {"start": v(-4.47, -35.34) * mm, "end": v(-4.94, -35.57) * mm});
            skLineSegment(sketch, "E1668", {"start": v(-4.94, -35.57) * mm, "end": v(-5.4, -35.81) * mm});
            skLineSegment(sketch, "E1669", {"start": v(-5.4, -35.81) * mm, "end": v(-6.34, -36.33) * mm});
            skLineSegment(sketch, "E1670", {"start": v(-6.34, -36.33) * mm, "end": v(-6.82, -36.58) * mm});
            skLineSegment(sketch, "E1671", {"start": v(-6.82, -36.58) * mm, "end": v(-7.3, -36.82) * mm});
            skLineSegment(sketch, "E1672", {"start": v(-7.3, -36.82) * mm, "end": v(-7.77, -37.03) * mm});
            skLineSegment(sketch, "E1673", {"start": v(-7.77, -37.03) * mm, "end": v(-8.01, -37.13) * mm});
            skLineSegment(sketch, "E1674", {"start": v(-8.01, -37.13) * mm, "end": v(-8.26, -37.21) * mm});
            skLineSegment(sketch, "E1675", {"start": v(-8.26, -37.21) * mm, "end": v(-8.08, -37.42) * mm});
            skLineSegment(sketch, "E1676", {"start": v(-8.08, -37.42) * mm, "end": v(-7.92, -37.65) * mm});
            skLineSegment(sketch, "E1677", {"start": v(-7.92, -37.65) * mm, "end": v(-7.78, -37.89) * mm});
            skLineSegment(sketch, "E1678", {"start": v(-7.78, -37.89) * mm, "end": v(-7.67, -38.14) * mm});
            skLineSegment(sketch, "E1679", {"start": v(-7.67, -38.14) * mm, "end": v(-7.58, -38.4) * mm});
            skLineSegment(sketch, "E1680", {"start": v(-7.58, -38.4) * mm, "end": v(-7.5, -38.68) * mm});
            skLineSegment(sketch, "E1681", {"start": v(-7.5, -38.68) * mm, "end": v(-7.47, -38.96) * mm});
            skLineSegment(sketch, "E1682", {"start": v(-7.47, -38.96) * mm, "end": v(-7.45, -39.26) * mm});
            skLineSegment(sketch, "E1683", {"start": v(-7.45, -39.26) * mm, "end": v(-7.46, -39.41) * mm});
            skLineSegment(sketch, "E1684", {"start": v(-7.46, -39.41) * mm, "end": v(-7.47, -39.56) * mm});
            skLineSegment(sketch, "E1685", {"start": v(-7.47, -39.56) * mm, "end": v(-7.52, -39.86) * mm});
            skLineSegment(sketch, "E1686", {"start": v(-7.52, -39.86) * mm, "end": v(-7.59, -40.15) * mm});
            skLineSegment(sketch, "E1687", {"start": v(-7.59, -40.15) * mm, "end": v(-7.7, -40.42) * mm});
            skLineSegment(sketch, "E1688", {"start": v(-7.7, -40.42) * mm, "end": v(-7.82, -40.69) * mm});
            skLineSegment(sketch, "E1689", {"start": v(-7.82, -40.69) * mm, "end": v(-7.97, -40.93) * mm});
            skLineSegment(sketch, "E1690", {"start": v(-7.97, -40.93) * mm, "end": v(-8.14, -41.17) * mm});
            skLineSegment(sketch, "E1691", {"start": v(-8.14, -41.17) * mm, "end": v(-8.33, -41.38) * mm});
            skLineSegment(sketch, "E1692", {"start": v(-8.33, -41.38) * mm, "end": v(-8.55, -41.57) * mm});
            skLineSegment(sketch, "E1693", {"start": v(-8.55, -41.57) * mm, "end": v(-8.78, -41.74) * mm});
            skLineSegment(sketch, "E1694", {"start": v(-8.78, -41.74) * mm, "end": v(-9.02, -41.9) * mm});
            skLineSegment(sketch, "E1695", {"start": v(-9.02, -41.9) * mm, "end": v(-9.29, -42.02) * mm});
            skLineSegment(sketch, "E1696", {"start": v(-9.29, -42.02) * mm, "end": v(-9.56, -42.12) * mm});
            skLineSegment(sketch, "E1697", {"start": v(-9.56, -42.12) * mm, "end": v(-9.85, -42.2) * mm});
            skLineSegment(sketch, "E1698", {"start": v(-9.85, -42.2) * mm, "end": v(-10, -42.22) * mm});
            skLineSegment(sketch, "E1699", {"start": v(-10, -42.22) * mm, "end": v(-10.15, -42.24) * mm});
            skLineSegment(sketch, "E1700", {"start": v(-10.15, -42.24) * mm, "end": v(-10.3, -42.25) * mm});
            skLineSegment(sketch, "E1701", {"start": v(-10.3, -42.25) * mm, "end": v(-10.45, -42.26) * mm});
            skLineSegment(sketch, "E1702", {"start": v(-10.45, -42.26) * mm, "end": v(-10.6, -42.25) * mm});
            skLineSegment(sketch, "E1703", {"start": v(-10.6, -42.25) * mm, "end": v(-10.76, -42.24) * mm});
            skLineSegment(sketch, "E1704", {"start": v(-10.76, -42.24) * mm, "end": v(-11.06, -42.2) * mm});
            skLineSegment(sketch, "E1705", {"start": v(-11.06, -42.2) * mm, "end": v(-11.35, -42.12) * mm});
            skLineSegment(sketch, "E1706", {"start": v(-11.35, -42.12) * mm, "end": v(-11.62, -42.02) * mm});
            skLineSegment(sketch, "E1707", {"start": v(-11.62, -42.02) * mm, "end": v(-11.88, -41.9) * mm});
            skLineSegment(sketch, "E1708", {"start": v(-11.88, -41.9) * mm, "end": v(-12.13, -41.74) * mm});
            skLineSegment(sketch, "E1709", {"start": v(-12.13, -41.74) * mm, "end": v(-12.36, -41.57) * mm});
            skLineSegment(sketch, "E1710", {"start": v(-12.36, -41.57) * mm, "end": v(-12.58, -41.38) * mm});
            skLineSegment(sketch, "E1711", {"start": v(-12.58, -41.38) * mm, "end": v(-12.77, -41.17) * mm});
            skLineSegment(sketch, "E1712", {"start": v(-12.77, -41.17) * mm, "end": v(-12.94, -40.93) * mm});
            skLineSegment(sketch, "E1713", {"start": v(-12.94, -40.93) * mm, "end": v(-13.1, -40.69) * mm});
            skLineSegment(sketch, "E1714", {"start": v(-13.1, -40.69) * mm, "end": v(-13.22, -40.42) * mm});
            skLineSegment(sketch, "E1715", {"start": v(-13.22, -40.42) * mm, "end": v(-13.32, -40.15) * mm});
            skLineSegment(sketch, "E1716", {"start": v(-13.32, -40.15) * mm, "end": v(-13.4, -39.86) * mm});
            skLineSegment(sketch, "E1717", {"start": v(-13.4, -39.86) * mm, "end": v(-13.42, -39.71) * mm});
            skLineSegment(sketch, "E1718", {"start": v(-13.42, -39.71) * mm, "end": v(-13.44, -39.56) * mm});
            skLineSegment(sketch, "E1719", {"start": v(-13.44, -39.56) * mm, "end": v(-13.45, -39.41) * mm});
            skLineSegment(sketch, "E1720", {"start": v(-13.45, -39.41) * mm, "end": v(-13.45, -39.26) * mm});
            skLineSegment(sketch, "E1721", {"start": v(-13.45, -39.26) * mm, "end": v(-13.45, -39.08) * mm});
            skLineSegment(sketch, "E1722", {"start": v(-13.45, -39.08) * mm, "end": v(-13.44, -38.92) * mm});
            skLineSegment(sketch, "E1723", {"start": v(-13.44, -38.92) * mm, "end": v(-13.41, -38.75) * mm});
            skLineSegment(sketch, "E1724", {"start": v(-13.41, -38.75) * mm, "end": v(-13.38, -38.58) * mm});
            skLineSegment(sketch, "E1725", {"start": v(-13.38, -38.58) * mm, "end": v(-13.34, -38.42) * mm});
            skLineSegment(sketch, "E1726", {"start": v(-13.34, -38.42) * mm, "end": v(-13.29, -38.27) * mm});
            skLineSegment(sketch, "E1727", {"start": v(-13.29, -38.27) * mm, "end": v(-13.23, -38.11) * mm});
            skLineSegment(sketch, "E1728", {"start": v(-13.23, -38.11) * mm, "end": v(-13.16, -37.97) * mm});
            skLineSegment(sketch, "E1729", {"start": v(-13.16, -37.97) * mm, "end": v(-13.09, -37.82) * mm});
            skLineSegment(sketch, "E1730", {"start": v(-13.09, -37.82) * mm, "end": v(-13, -37.68) * mm});
            skLineSegment(sketch, "E1731", {"start": v(-13, -37.68) * mm, "end": v(-12.92, -37.55) * mm});
            skLineSegment(sketch, "E1732", {"start": v(-12.92, -37.55) * mm, "end": v(-12.82, -37.42) * mm});
            skLineSegment(sketch, "E1733", {"start": v(-12.82, -37.42) * mm, "end": v(-12.72, -37.3) * mm});
            skLineSegment(sketch, "E1734", {"start": v(-12.72, -37.3) * mm, "end": v(-12.61, -37.17) * mm});
            skLineSegment(sketch, "E1735", {"start": v(-12.61, -37.17) * mm, "end": v(-12.5, -37.06) * mm});
            skLineSegment(sketch, "E1736", {"start": v(-12.5, -37.06) * mm, "end": v(-12.38, -36.95) * mm});
            skLineSegment(sketch, "E1737", {"start": v(-12.38, -36.95) * mm, "end": v(-12.7, -36.8) * mm});
            skLineSegment(sketch, "E1738", {"start": v(-12.7, -36.8) * mm, "end": v(-13.04, -36.65) * mm});
            skLineSegment(sketch, "E1739", {"start": v(-13.04, -36.65) * mm, "end": v(-13.36, -36.48) * mm});
            skLineSegment(sketch, "E1740", {"start": v(-13.36, -36.48) * mm, "end": v(-13.68, -36.3) * mm});
            skLineSegment(sketch, "E1741", {"start": v(-13.68, -36.3) * mm, "end": v(-13.99, -36.11) * mm});
            skLineSegment(sketch, "E1742", {"start": v(-13.99, -36.11) * mm, "end": v(-14.3, -35.91) * mm});
            skLineSegment(sketch, "E1743", {"start": v(-14.3, -35.91) * mm, "end": v(-14.9, -35.5) * mm});
            skLineSegment(sketch, "E1744", {"start": v(-14.9, -35.5) * mm, "end": v(-16.09, -34.66) * mm});
            skLineSegment(sketch, "E1745", {"start": v(-16.09, -34.66) * mm, "end": v(-16.6, -34.3) * mm});
            skLineSegment(sketch, "E1746", {"start": v(-16.6, -34.3) * mm, "end": v(-17.05, -33.98) * mm});
            skLineSegment(sketch, "E1747", {"start": v(-17.05, -33.98) * mm, "end": v(-17.47, -33.7) * mm});
            skLineSegment(sketch, "E1748", {"start": v(-17.47, -33.7) * mm, "end": v(-17.87, -33.47) * mm});
            skLineSegment(sketch, "E1749", {"start": v(-17.87, -33.47) * mm, "end": v(-18.07, -33.37) * mm});
            skLineSegment(sketch, "E1750", {"start": v(-18.07, -33.37) * mm, "end": v(-18.26, -33.28) * mm});
            skLineSegment(sketch, "E1751", {"start": v(-18.26, -33.28) * mm, "end": v(-18.46, -33.2) * mm});
            skLineSegment(sketch, "E1752", {"start": v(-18.46, -33.2) * mm, "end": v(-18.65, -33.13) * mm});
            skLineSegment(sketch, "E1753", {"start": v(-18.65, -33.13) * mm, "end": v(-18.85, -33.07) * mm});
            skLineSegment(sketch, "E1754", {"start": v(-18.85, -33.07) * mm, "end": v(-19.05, -33.02) * mm});
            skLineSegment(sketch, "E1755", {"start": v(-19.05, -33.02) * mm, "end": v(-19.25, -32.98) * mm});
            skLineSegment(sketch, "E1756", {"start": v(-19.25, -32.98) * mm, "end": v(-19.47, -32.96) * mm});
            skLineSegment(sketch, "E1757", {"start": v(-19.47, -32.96) * mm, "end": v(-19.69, -32.95) * mm});
            skLineSegment(sketch, "E1758", {"start": v(-19.69, -32.95) * mm, "end": v(-19.92, -32.94) * mm});
            skLineSegment(sketch, "E1759", {"start": v(-19.92, -32.94) * mm, "end": v(-20.16, -32.95) * mm});
            skLineSegment(sketch, "E1760", {"start": v(-20.16, -32.95) * mm, "end": v(-20.41, -32.97) * mm});
            skLineSegment(sketch, "E1761", {"start": v(-20.41, -32.97) * mm, "end": v(-20.68, -33) * mm});
            skLineSegment(sketch, "E1762", {"start": v(-20.68, -33) * mm, "end": v(-20.96, -33.04) * mm});
            skLineSegment(sketch, "E1763", {"start": v(-20.96, -33.04) * mm, "end": v(-21.26, -33.1) * mm});
            skLineSegment(sketch, "E1764", {"start": v(-21.26, -33.1) * mm, "end": v(-21.58, -33.16) * mm});
            skLineSegment(sketch, "E1765", {"start": v(-21.58, -33.16) * mm, "end": v(-22.27, -33.33) * mm});
            skLineSegment(sketch, "E1766", {"start": v(-22.27, -33.33) * mm, "end": v(-23.05, -33.54) * mm});
            skLineSegment(sketch, "E1767", {"start": v(-23.05, -33.54) * mm, "end": v(-24.05, -34) * mm});
            skLineSegment(sketch, "E1768", {"start": v(-2.8, 8.85) * mm, "end": v(-2.72, 8.7) * mm});
            skLineSegment(sketch, "E1769", {"start": v(-2.72, 8.7) * mm, "end": v(-2.65, 8.54) * mm});
            skLineSegment(sketch, "E1770", {"start": v(-2.65, 8.54) * mm, "end": v(-2.6, 8.37) * mm});
            skLineSegment(sketch, "E1771", {"start": v(-2.6, 8.37) * mm, "end": v(-2.55, 8.2) * mm});
            skLineSegment(sketch, "E1772", {"start": v(-2.55, 8.2) * mm, "end": v(-2.51, 8.03) * mm});
            skLineSegment(sketch, "E1773", {"start": v(-2.51, 8.03) * mm, "end": v(-2.49, 7.85) * mm});
            skLineSegment(sketch, "E1774", {"start": v(-2.49, 7.85) * mm, "end": v(-2.47, 7.67) * mm});
            skLineSegment(sketch, "E1775", {"start": v(-2.47, 7.67) * mm, "end": v(-2.46, 7.48) * mm});
            skLineSegment(sketch, "E1776", {"start": v(-2.46, 7.48) * mm, "end": v(-2.47, 7.33) * mm});
            skLineSegment(sketch, "E1777", {"start": v(-2.47, 7.33) * mm, "end": v(-2.48, 7.18) * mm});
            skLineSegment(sketch, "E1778", {"start": v(-2.48, 7.18) * mm, "end": v(-2.52, 6.88) * mm});
            skLineSegment(sketch, "E1779", {"start": v(-2.52, 6.88) * mm, "end": v(-2.6, 6.6) * mm});
            skLineSegment(sketch, "E1780", {"start": v(-2.6, 6.6) * mm, "end": v(-2.7, 6.32) * mm});
            skLineSegment(sketch, "E1781", {"start": v(-2.7, 6.32) * mm, "end": v(-2.83, 6.06) * mm});
            skLineSegment(sketch, "E1782", {"start": v(-2.83, 6.06) * mm, "end": v(-2.98, 5.8) * mm});
            skLineSegment(sketch, "E1783", {"start": v(-2.98, 5.8) * mm, "end": v(-3.15, 5.58) * mm});
            skLineSegment(sketch, "E1784", {"start": v(-3.15, 5.58) * mm, "end": v(-3.34, 5.36) * mm});
            skLineSegment(sketch, "E1785", {"start": v(-3.34, 5.36) * mm, "end": v(-3.56, 5.17) * mm});
            skLineSegment(sketch, "E1786", {"start": v(-3.56, 5.17) * mm, "end": v(-3.79, 5) * mm});
            skLineSegment(sketch, "E1787", {"start": v(-3.79, 5) * mm, "end": v(-4.03, 4.85) * mm});
            skLineSegment(sketch, "E1788", {"start": v(-4.03, 4.85) * mm, "end": v(-4.3, 4.72) * mm});
            skLineSegment(sketch, "E1789", {"start": v(-4.3, 4.72) * mm, "end": v(-4.57, 4.62) * mm});
            skLineSegment(sketch, "E1790", {"start": v(-4.57, 4.62) * mm, "end": v(-4.86, 4.55) * mm});
            skLineSegment(sketch, "E1791", {"start": v(-4.86, 4.55) * mm, "end": v(-5, 4.52) * mm});
            skLineSegment(sketch, "E1792", {"start": v(-5, 4.52) * mm, "end": v(-5.16, 4.5) * mm});
            skLineSegment(sketch, "E1793", {"start": v(-5.16, 4.5) * mm, "end": v(-5.3, 4.49) * mm});
            skLineSegment(sketch, "E1794", {"start": v(-5.3, 4.49) * mm, "end": v(-5.46, 4.49) * mm});
            skLineSegment(sketch, "E1795", {"start": v(-5.46, 4.49) * mm, "end": v(-5.62, 4.49) * mm});
            skLineSegment(sketch, "E1796", {"start": v(-5.62, 4.49) * mm, "end": v(-5.77, 4.5) * mm});
            skLineSegment(sketch, "E1797", {"start": v(-5.77, 4.5) * mm, "end": v(-6.07, 4.55) * mm});
            skLineSegment(sketch, "E1798", {"start": v(-6.07, 4.55) * mm, "end": v(-6.36, 4.62) * mm});
            skLineSegment(sketch, "E1799", {"start": v(-6.36, 4.62) * mm, "end": v(-6.63, 4.72) * mm});
            skLineSegment(sketch, "E1800", {"start": v(-6.63, 4.72) * mm, "end": v(-6.9, 4.85) * mm});
            skLineSegment(sketch, "E1801", {"start": v(-6.9, 4.85) * mm, "end": v(-7.14, 5) * mm});
            skLineSegment(sketch, "E1802", {"start": v(-7.14, 5) * mm, "end": v(-7.37, 5.17) * mm});
            skLineSegment(sketch, "E1803", {"start": v(-7.37, 5.17) * mm, "end": v(-7.58, 5.36) * mm});
            skLineSegment(sketch, "E1804", {"start": v(-7.58, 5.36) * mm, "end": v(-7.78, 5.58) * mm});
            skLineSegment(sketch, "E1805", {"start": v(-7.78, 5.58) * mm, "end": v(-7.95, 5.8) * mm});
            skLineSegment(sketch, "E1806", {"start": v(-7.95, 5.8) * mm, "end": v(-8.1, 6.06) * mm});
            skLineSegment(sketch, "E1807", {"start": v(-8.1, 6.06) * mm, "end": v(-8.23, 6.32) * mm});
            skLineSegment(sketch, "E1808", {"start": v(-8.23, 6.32) * mm, "end": v(-8.33, 6.6) * mm});
            skLineSegment(sketch, "E1809", {"start": v(-8.33, 6.6) * mm, "end": v(-8.4, 6.88) * mm});
            skLineSegment(sketch, "E1810", {"start": v(-8.4, 6.88) * mm, "end": v(-8.43, 7.03) * mm});
            skLineSegment(sketch, "E1811", {"start": v(-8.43, 7.03) * mm, "end": v(-8.45, 7.18) * mm});
            skLineSegment(sketch, "E1812", {"start": v(-8.45, 7.18) * mm, "end": v(-8.46, 7.33) * mm});
            skLineSegment(sketch, "E1813", {"start": v(-8.46, 7.33) * mm, "end": v(-8.46, 7.48) * mm});
            skLineSegment(sketch, "E1814", {"start": v(-8.46, 7.48) * mm, "end": v(-8.45, 7.76) * mm});
            skLineSegment(sketch, "E1815", {"start": v(-8.45, 7.76) * mm, "end": v(-8.42, 8.02) * mm});
            skLineSegment(sketch, "E1816", {"start": v(-8.42, 8.02) * mm, "end": v(-8.36, 8.28) * mm});
            skLineSegment(sketch, "E1817", {"start": v(-8.36, 8.28) * mm, "end": v(-8.28, 8.53) * mm});
            skLineSegment(sketch, "E1818", {"start": v(-8.28, 8.53) * mm, "end": v(-8.18, 8.77) * mm});
            skLineSegment(sketch, "E1819", {"start": v(-8.18, 8.77) * mm, "end": v(-8.06, 9) * mm});
            skLineSegment(sketch, "E1820", {"start": v(-8.06, 9) * mm, "end": v(-7.92, 9.21) * mm});
            skLineSegment(sketch, "E1821", {"start": v(-7.92, 9.21) * mm, "end": v(-7.76, 9.41) * mm});
            skLineSegment(sketch, "E1822", {"start": v(-7.76, 9.41) * mm, "end": v(-7.6, 9.6) * mm});
            skLineSegment(sketch, "E1823", {"start": v(-7.6, 9.6) * mm, "end": v(-7.4, 9.77) * mm});
            skLineSegment(sketch, "E1824", {"start": v(-7.4, 9.77) * mm, "end": v(-7.2, 9.93) * mm});
            skLineSegment(sketch, "E1825", {"start": v(-7.2, 9.93) * mm, "end": v(-6.99, 10.07) * mm});
            skLineSegment(sketch, "E1826", {"start": v(-6.99, 10.07) * mm, "end": v(-6.76, 10.2) * mm});
            skLineSegment(sketch, "E1827", {"start": v(-6.76, 10.2) * mm, "end": v(-6.52, 10.3) * mm});
            skLineSegment(sketch, "E1828", {"start": v(-6.52, 10.3) * mm, "end": v(-6.27, 10.37) * mm});
            skLineSegment(sketch, "E1829", {"start": v(-6.27, 10.37) * mm, "end": v(-6.02, 10.43) * mm});
            skLineSegment(sketch, "E1830", {"start": v(-6.02, 10.43) * mm, "end": v(-6.3, 10.5) * mm});
            skLineSegment(sketch, "E1831", {"start": v(-6.3, 10.5) * mm, "end": v(-6.56, 10.53) * mm});
            skLineSegment(sketch, "E1832", {"start": v(-6.56, 10.53) * mm, "end": v(-6.83, 10.54) * mm});
            skLineSegment(sketch, "E1833", {"start": v(-6.83, 10.54) * mm, "end": v(-7.1, 10.52) * mm});
            skLineSegment(sketch, "E1834", {"start": v(-7.1, 10.52) * mm, "end": v(-7.36, 10.48) * mm});
            skLineSegment(sketch, "E1835", {"start": v(-7.36, 10.48) * mm, "end": v(-7.62, 10.41) * mm});
            skLineSegment(sketch, "E1836", {"start": v(-7.62, 10.41) * mm, "end": v(-7.88, 10.33) * mm});
            skLineSegment(sketch, "E1837", {"start": v(-7.88, 10.33) * mm, "end": v(-8.13, 10.23) * mm});
            skLineSegment(sketch, "E1838", {"start": v(-8.13, 10.23) * mm, "end": v(-8.38, 10.12) * mm});
            skLineSegment(sketch, "E1839", {"start": v(-8.38, 10.12) * mm, "end": v(-8.62, 9.99) * mm});
            skLineSegment(sketch, "E1840", {"start": v(-8.62, 9.99) * mm, "end": v(-8.86, 9.85) * mm});
            skLineSegment(sketch, "E1841", {"start": v(-8.86, 9.85) * mm, "end": v(-9.1, 9.7) * mm});
            skLineSegment(sketch, "E1842", {"start": v(-9.1, 9.7) * mm, "end": v(-9.54, 9.39) * mm});
            skLineSegment(sketch, "E1843", {"start": v(-9.54, 9.39) * mm, "end": v(-9.97, 9.06) * mm});
            skLineSegment(sketch, "E1844", {"start": v(-9.97, 9.06) * mm, "end": v(-10.2, 8.89) * mm});
            skLineSegment(sketch, "E1845", {"start": v(-10.2, 8.89) * mm, "end": v(-10.43, 8.73) * mm});
            skLineSegment(sketch, "E1846", {"start": v(-10.43, 8.73) * mm, "end": v(-10.92, 8.43) * mm});
            skLineSegment(sketch, "E1847", {"start": v(-10.92, 8.43) * mm, "end": v(-11.38, 8.19) * mm});
            skLineSegment(sketch, "E1848", {"start": v(-11.38, 8.19) * mm, "end": v(-11.62, 8.06) * mm});
            skLineSegment(sketch, "E1849", {"start": v(-11.62, 8.06) * mm, "end": v(-11.84, 7.93) * mm});
            skLineSegment(sketch, "E1850", {"start": v(-11.84, 7.93) * mm, "end": v(-12.2, 7.48) * mm});
            skLineSegment(sketch, "E1851", {"start": v(-12.2, 7.48) * mm, "end": v(-13.57, 7.28) * mm});
            skLineSegment(sketch, "E1852", {"start": v(-13.57, 7.28) * mm, "end": v(-13.63, 7.29) * mm});
            skLineSegment(sketch, "E1853", {"start": v(-13.63, 7.29) * mm, "end": v(-13.85, 7.25) * mm});
            skLineSegment(sketch, "E1854", {"start": v(-13.85, 7.25) * mm, "end": v(-14.08, 7.2) * mm});
            skLineSegment(sketch, "E1855", {"start": v(-14.08, 7.2) * mm, "end": v(-14.09, 7.2) * mm});
            skLineSegment(sketch, "E1856", {"start": v(-14.09, 7.2) * mm, "end": v(-14.32, 7.16) * mm});
            skLineSegment(sketch, "E1857", {"start": v(-14.32, 7.16) * mm, "end": v(-14.57, 6.6) * mm});
            skLineSegment(sketch, "E1858", {"start": v(-14.57, 6.6) * mm, "end": v(-14.85, 6.04) * mm});
            skLineSegment(sketch, "E1859", {"start": v(-14.85, 6.04) * mm, "end": v(-15.15, 5.47) * mm});
            skLineSegment(sketch, "E1860", {"start": v(-15.15, 5.47) * mm, "end": v(-15.47, 4.9) * mm});
            skLineSegment(sketch, "E1861", {"start": v(-15.47, 4.9) * mm, "end": v(-15.8, 4.32) * mm});
            skLineSegment(sketch, "E1862", {"start": v(-15.8, 4.32) * mm, "end": v(-16.15, 3.74) * mm});
            skLineSegment(sketch, "E1863", {"start": v(-16.15, 3.74) * mm, "end": v(-16.5, 3.16) * mm});
            skLineSegment(sketch, "E1864", {"start": v(-16.5, 3.16) * mm, "end": v(-16.87, 2.6) * mm});
            skLineSegment(sketch, "E1865", {"start": v(-16.87, 2.6) * mm, "end": v(-17.25, 2.03) * mm});
            skLineSegment(sketch, "E1866", {"start": v(-17.25, 2.03) * mm, "end": v(-17.63, 1.47) * mm});
            skLineSegment(sketch, "E1867", {"start": v(-17.63, 1.47) * mm, "end": v(-18, 0.92) * mm});
            skLineSegment(sketch, "E1868", {"start": v(-18, 0.92) * mm, "end": v(-18.4, 0.4) * mm});
            skLineSegment(sketch, "E1869", {"start": v(-18.4, 0.4) * mm, "end": v(-19.15, -0.62) * mm});
            skLineSegment(sketch, "E1870", {"start": v(-19.15, -0.62) * mm, "end": v(-19.88, -1.55) * mm});
            skLineSegment(sketch, "E1871", {"start": v(-19.88, -1.55) * mm, "end": v(-20.14, -1.83) * mm});
            skLineSegment(sketch, "E1872", {"start": v(-20.14, -1.83) * mm, "end": v(-20.53, -2.25) * mm});
            skLineSegment(sketch, "E1873", {"start": v(-20.53, -2.25) * mm, "end": v(-20.93, -2.67) * mm});
            skLineSegment(sketch, "E1874", {"start": v(-20.93, -2.67) * mm, "end": v(-21.08, -2.85) * mm});
            skLineSegment(sketch, "E1875", {"start": v(-21.08, -2.85) * mm, "end": v(-21.18, -3) * mm});
            skLineSegment(sketch, "E1876", {"start": v(-21.18, -3) * mm, "end": v(-21.12, -3.07) * mm});
            skLineSegment(sketch, "E1877", {"start": v(-21.12, -3.07) * mm, "end": v(-21.04, -3.13) * mm});
            skLineSegment(sketch, "E1878", {"start": v(-21.04, -3.13) * mm, "end": v(-20.95, -3.18) * mm});
            skLineSegment(sketch, "E1879", {"start": v(-20.95, -3.18) * mm, "end": v(-20.84, -3.22) * mm});
            skLineSegment(sketch, "E1880", {"start": v(-20.84, -3.22) * mm, "end": v(-20.72, -3.25) * mm});
            skLineSegment(sketch, "E1881", {"start": v(-20.72, -3.25) * mm, "end": v(-20.6, -3.27) * mm});
            skLineSegment(sketch, "E1882", {"start": v(-20.6, -3.27) * mm, "end": v(-20.32, -3.28) * mm});
            skLineSegment(sketch, "E1883", {"start": v(-20.32, -3.28) * mm, "end": v(-20.04, -3.28) * mm});
            skLineSegment(sketch, "E1884", {"start": v(-20.04, -3.28) * mm, "end": v(-19.78, -3.25) * mm});
            skLineSegment(sketch, "E1885", {"start": v(-19.78, -3.25) * mm, "end": v(-19.38, -3.19) * mm});
            skLineSegment(sketch, "E1886", {"start": v(-19.38, -3.19) * mm, "end": v(-19.12, -3.11) * mm});
            skLineSegment(sketch, "E1887", {"start": v(-19.12, -3.11) * mm, "end": v(-18.86, -3.02) * mm});
            skLineSegment(sketch, "E1888", {"start": v(-18.86, -3.02) * mm, "end": v(-18.6, -2.9) * mm});
            skLineSegment(sketch, "E1889", {"start": v(-18.6, -2.9) * mm, "end": v(-18.36, -2.78) * mm});
            skLineSegment(sketch, "E1890", {"start": v(-18.36, -2.78) * mm, "end": v(-17.93, -2.52) * mm});
            skLineSegment(sketch, "E1891", {"start": v(-17.93, -2.52) * mm, "end": v(-17.51, -2.24) * mm});
            skLineSegment(sketch, "E1892", {"start": v(-17.51, -2.24) * mm, "end": v(-17.1, -1.96) * mm});
            skLineSegment(sketch, "E1893", {"start": v(-17.1, -1.96) * mm, "end": v(-16.7, -1.67) * mm});
            skLineSegment(sketch, "E1894", {"start": v(-16.7, -1.67) * mm, "end": v(-16.15, -1.31) * mm});
            skLineSegment(sketch, "E1895", {"start": v(-16.15, -1.31) * mm, "end": v(-15.87, -1.14) * mm});
            skLineSegment(sketch, "E1896", {"start": v(-15.87, -1.14) * mm, "end": v(-15.6, -0.98) * mm});
            skLineSegment(sketch, "E1897", {"start": v(-15.6, -0.98) * mm, "end": v(-15.3, -0.83) * mm});
            skLineSegment(sketch, "E1898", {"start": v(-15.3, -0.83) * mm, "end": v(-15.01, -0.7) * mm});
            skLineSegment(sketch, "E1899", {"start": v(-15.01, -0.7) * mm, "end": v(-14.71, -0.57) * mm});
            skLineSegment(sketch, "E1900", {"start": v(-14.71, -0.57) * mm, "end": v(-14.4, -0.45) * mm});
            skLineSegment(sketch, "E1901", {"start": v(-14.4, -0.45) * mm, "end": v(-14.17, -0.38) * mm});
            skLineSegment(sketch, "E1902", {"start": v(-14.17, -0.38) * mm, "end": v(-13.93, -0.31) * mm});
            skLineSegment(sketch, "E1903", {"start": v(-13.93, -0.31) * mm, "end": v(-13.7, -0.26) * mm});
            skLineSegment(sketch, "E1904", {"start": v(-13.7, -0.26) * mm, "end": v(-13.47, -0.21) * mm});
            skLineSegment(sketch, "E1905", {"start": v(-13.47, -0.21) * mm, "end": v(-13.23, -0.18) * mm});
            skLineSegment(sketch, "E1906", {"start": v(-13.23, -0.18) * mm, "end": v(-13, -0.15) * mm});
            skLineSegment(sketch, "E1907", {"start": v(-13, -0.15) * mm, "end": v(-12.77, -0.13) * mm});
            skLineSegment(sketch, "E1908", {"start": v(-12.77, -0.13) * mm, "end": v(-12.54, -0.12) * mm});
            skLineSegment(sketch, "E1909", {"start": v(-12.54, -0.12) * mm, "end": v(-12.3, -0.11) * mm});
            skLineSegment(sketch, "E1910", {"start": v(-12.3, -0.11) * mm, "end": v(-12.07, -0.12) * mm});
            skLineSegment(sketch, "E1911", {"start": v(-12.07, -0.12) * mm, "end": v(-11.61, -0.15) * mm});
            skLineSegment(sketch, "E1912", {"start": v(-11.61, -0.15) * mm, "end": v(-11.16, -0.21) * mm});
            skLineSegment(sketch, "E1913", {"start": v(-11.16, -0.21) * mm, "end": v(-10.7, -0.3) * mm});
            skLineSegment(sketch, "E1914", {"start": v(-10.7, -0.3) * mm, "end": v(-10.25, -0.42) * mm});
            skLineSegment(sketch, "E1915", {"start": v(-10.25, -0.42) * mm, "end": v(-9.8, -0.55) * mm});
            skLineSegment(sketch, "E1916", {"start": v(-9.8, -0.55) * mm, "end": v(-9.37, -0.7) * mm});
            skLineSegment(sketch, "E1917", {"start": v(-9.37, -0.7) * mm, "end": v(-8.93, -0.88) * mm});
            skLineSegment(sketch, "E1918", {"start": v(-8.93, -0.88) * mm, "end": v(-8.5, -1.08) * mm});
            skLineSegment(sketch, "E1919", {"start": v(-8.5, -1.08) * mm, "end": v(-8.07, -1.29) * mm});
            skLineSegment(sketch, "E1920", {"start": v(-8.07, -1.29) * mm, "end": v(-7.65, -1.5) * mm});
            skLineSegment(sketch, "E1921", {"start": v(-7.65, -1.5) * mm, "end": v(-7.24, -1.74) * mm});
            skLineSegment(sketch, "E1922", {"start": v(-7.24, -1.74) * mm, "end": v(-6.66, -2.07) * mm});
            skLineSegment(sketch, "E1923", {"start": v(-6.66, -2.07) * mm, "end": v(-6.06, -2.4) * mm});
            skLineSegment(sketch, "E1924", {"start": v(-6.06, -2.4) * mm, "end": v(-5.47, -2.71) * mm});
            skLineSegment(sketch, "E1925", {"start": v(-5.47, -2.71) * mm, "end": v(-4.86, -3.01) * mm});
            skLineSegment(sketch, "E1926", {"start": v(-4.86, -3.01) * mm, "end": v(-4.25, -3.3) * mm});
            skLineSegment(sketch, "E1927", {"start": v(-4.25, -3.3) * mm, "end": v(-3.63, -3.57) * mm});
            skLineSegment(sketch, "E1928", {"start": v(-3.63, -3.57) * mm, "end": v(-3, -3.82) * mm});
            skLineSegment(sketch, "E1929", {"start": v(-3, -3.82) * mm, "end": v(-2.37, -4.06) * mm});
            skLineSegment(sketch, "E1930", {"start": v(-2.37, -4.06) * mm, "end": v(-1.75, -4.26) * mm});
            skLineSegment(sketch, "E1931", {"start": v(-1.75, -4.26) * mm, "end": v(-1.43, -4.35) * mm});
            skLineSegment(sketch, "E1932", {"start": v(-1.43, -4.35) * mm, "end": v(-1.1, -4.44) * mm});
            skLineSegment(sketch, "E1933", {"start": v(-1.1, -4.44) * mm, "end": v(-0.78, -4.52) * mm});
            skLineSegment(sketch, "E1934", {"start": v(-0.78, -4.52) * mm, "end": v(-0.45, -4.59) * mm});
            skLineSegment(sketch, "E1935", {"start": v(-0.45, -4.59) * mm, "end": v(-0.11, -4.65) * mm});
            skLineSegment(sketch, "E1936", {"start": v(-0.11, -4.65) * mm, "end": v(0.22, -4.7) * mm});
            skLineSegment(sketch, "E1937", {"start": v(0.22, -4.7) * mm, "end": v(0.56, -4.74) * mm});
            skLineSegment(sketch, "E1938", {"start": v(0.56, -4.74) * mm, "end": v(0.9, -4.77) * mm});
            skLineSegment(sketch, "E1939", {"start": v(0.9, -4.77) * mm, "end": v(1.23, -4.79) * mm});
            skLineSegment(sketch, "E1940", {"start": v(1.23, -4.79) * mm, "end": v(1.56, -4.8) * mm});
            skLineSegment(sketch, "E1941", {"start": v(1.56, -4.8) * mm, "end": v(1.9, -4.78) * mm});
            skLineSegment(sketch, "E1942", {"start": v(1.9, -4.78) * mm, "end": v(2.23, -4.75) * mm});
            skLineSegment(sketch, "E1943", {"start": v(2.23, -4.75) * mm, "end": v(2.56, -4.7) * mm});
            skLineSegment(sketch, "E1944", {"start": v(2.56, -4.7) * mm, "end": v(2.88, -4.65) * mm});
            skLineSegment(sketch, "E1945", {"start": v(2.88, -4.65) * mm, "end": v(3.15, -4.58) * mm});
            skLineSegment(sketch, "E1946", {"start": v(3.15, -4.58) * mm, "end": v(3.4, -4.52) * mm});
            skLineSegment(sketch, "E1947", {"start": v(3.4, -4.52) * mm, "end": v(3.6, -4.45) * mm});
            skLineSegment(sketch, "E1948", {"start": v(3.6, -4.45) * mm, "end": v(3.8, -4.37) * mm});
            skLineSegment(sketch, "E1949", {"start": v(3.8, -4.37) * mm, "end": v(3.98, -4.3) * mm});
            skLineSegment(sketch, "E1950", {"start": v(3.98, -4.3) * mm, "end": v(4.15, -4.21) * mm});
            skLineSegment(sketch, "E1951", {"start": v(4.15, -4.21) * mm, "end": v(4.45, -4.03) * mm});
            skLineSegment(sketch, "E1952", {"start": v(4.45, -4.03) * mm, "end": v(4.75, -3.84) * mm});
            skLineSegment(sketch, "E1953", {"start": v(4.75, -3.84) * mm, "end": v(5.06, -3.62) * mm});
            skLineSegment(sketch, "E1954", {"start": v(5.06, -3.62) * mm, "end": v(5.42, -3.39) * mm});
            skLineSegment(sketch, "E1955", {"start": v(5.42, -3.39) * mm, "end": v(5.85, -3.14) * mm});
            skLineSegment(sketch, "E1956", {"start": v(5.85, -3.14) * mm, "end": v(6.4, -2.85) * mm});
            skLineSegment(sketch, "E1957", {"start": v(6.4, -2.85) * mm, "end": v(6.95, -2.6) * mm});
            skLineSegment(sketch, "E1958", {"start": v(6.95, -2.6) * mm, "end": v(7.52, -2.37) * mm});
            skLineSegment(sketch, "E1959", {"start": v(7.52, -2.37) * mm, "end": v(8.09, -2.17) * mm});
            skLineSegment(sketch, "E1960", {"start": v(8.09, -2.17) * mm, "end": v(8.67, -2) * mm});
            skLineSegment(sketch, "E1961", {"start": v(8.67, -2) * mm, "end": v(9.25, -1.86) * mm});
            skLineSegment(sketch, "E1962", {"start": v(9.25, -1.86) * mm, "end": v(9.55, -1.8) * mm});
            skLineSegment(sketch, "E1963", {"start": v(9.55, -1.8) * mm, "end": v(9.84, -1.75) * mm});
            skLineSegment(sketch, "E1964", {"start": v(9.84, -1.75) * mm, "end": v(10.14, -1.7) * mm});
            skLineSegment(sketch, "E1965", {"start": v(10.14, -1.7) * mm, "end": v(10.44, -1.67) * mm});
            skLineSegment(sketch, "E1966", {"start": v(10.44, -1.67) * mm, "end": v(10.73, -1.64) * mm});
            skLineSegment(sketch, "E1967", {"start": v(10.73, -1.64) * mm, "end": v(11.03, -1.62) * mm});
            skLineSegment(sketch, "E1968", {"start": v(11.03, -1.62) * mm, "end": v(11.33, -1.6) * mm});
            skLineSegment(sketch, "E1969", {"start": v(11.33, -1.6) * mm, "end": v(11.63, -1.6) * mm});
            skLineSegment(sketch, "E1970", {"start": v(11.63, -1.6) * mm, "end": v(11.93, -1.6) * mm});
            skLineSegment(sketch, "E1971", {"start": v(11.93, -1.6) * mm, "end": v(12.23, -1.62) * mm});
            skLineSegment(sketch, "E1972", {"start": v(12.23, -1.62) * mm, "end": v(12.53, -1.64) * mm});
            skLineSegment(sketch, "E1973", {"start": v(12.53, -1.64) * mm, "end": v(12.83, -1.67) * mm});
            skLineSegment(sketch, "E1974", {"start": v(12.83, -1.67) * mm, "end": v(13.13, -1.7) * mm});
            skLineSegment(sketch, "E1975", {"start": v(13.13, -1.7) * mm, "end": v(13.43, -1.76) * mm});
            skLineSegment(sketch, "E1976", {"start": v(13.43, -1.76) * mm, "end": v(13.73, -1.81) * mm});
            skLineSegment(sketch, "E1977", {"start": v(13.73, -1.81) * mm, "end": v(14.02, -1.87) * mm});
            skLineSegment(sketch, "E1978", {"start": v(14.02, -1.87) * mm, "end": v(14.32, -1.95) * mm});
            skLineSegment(sketch, "E1979", {"start": v(14.32, -1.95) * mm, "end": v(14.62, -2.03) * mm});
            skLineSegment(sketch, "E1980", {"start": v(14.62, -2.03) * mm, "end": v(14.91, -2.12) * mm});
            skLineSegment(sketch, "E1981", {"start": v(14.91, -2.12) * mm, "end": v(15.2, -2.22) * mm});
            skLineSegment(sketch, "E1982", {"start": v(15.2, -2.22) * mm, "end": v(15.65, -2.38) * mm});
            skLineSegment(sketch, "E1983", {"start": v(15.65, -2.38) * mm, "end": v(16.21, -2.6) * mm});
            skLineSegment(sketch, "E1984", {"start": v(16.21, -2.6) * mm, "end": v(16.86, -2.84) * mm});
            skLineSegment(sketch, "E1985", {"start": v(16.86, -2.84) * mm, "end": v(17.58, -3.07) * mm});
            skLineSegment(sketch, "E1986", {"start": v(17.58, -3.07) * mm, "end": v(17.94, -3.19) * mm});
            skLineSegment(sketch, "E1987", {"start": v(17.94, -3.19) * mm, "end": v(18.32, -3.29) * mm});
            skLineSegment(sketch, "E1988", {"start": v(18.32, -3.29) * mm, "end": v(18.69, -3.38) * mm});
            skLineSegment(sketch, "E1989", {"start": v(18.69, -3.38) * mm, "end": v(19.05, -3.45) * mm});
            skLineSegment(sketch, "E1990", {"start": v(19.05, -3.45) * mm, "end": v(19.41, -3.5) * mm});
            skLineSegment(sketch, "E1991", {"start": v(19.41, -3.5) * mm, "end": v(19.76, -3.53) * mm});
            skLineSegment(sketch, "E1992", {"start": v(19.76, -3.53) * mm, "end": v(20.09, -3.54) * mm});
            skLineSegment(sketch, "E1993", {"start": v(20.09, -3.54) * mm, "end": v(20.24, -3.54) * mm});
            skLineSegment(sketch, "E1994", {"start": v(20.24, -3.54) * mm, "end": v(20.4, -3.52) * mm});
            skLineSegment(sketch, "E1995", {"start": v(20.4, -3.52) * mm, "end": v(20.27, -3.38) * mm});
            skLineSegment(sketch, "E1996", {"start": v(20.27, -3.38) * mm, "end": v(19.87, -2.92) * mm});
            skLineSegment(sketch, "E1997", {"start": v(19.87, -2.92) * mm, "end": v(19.46, -2.47) * mm});
            skLineSegment(sketch, "E1998", {"start": v(19.46, -2.47) * mm, "end": v(18.63, -1.59) * mm});
            skLineSegment(sketch, "E1999", {"start": v(18.63, -1.59) * mm, "end": v(18.01, -0.94) * mm});
            skLineSegment(sketch, "E2000", {"start": v(18.01, -0.94) * mm, "end": v(17.4, -0.28) * mm});
            skLineSegment(sketch, "E2001", {"start": v(17.4, -0.28) * mm, "end": v(16.79, 0.4) * mm});
            skLineSegment(sketch, "E2002", {"start": v(16.79, 0.4) * mm, "end": v(16.5, 0.73) * mm});
            skLineSegment(sketch, "E2003", {"start": v(16.5, 0.73) * mm, "end": v(16.21, 1.08) * mm});
            skLineSegment(sketch, "E2004", {"start": v(16.21, 1.08) * mm, "end": v(15.79, 1.62) * mm});
            skLineSegment(sketch, "E2005", {"start": v(15.79, 1.62) * mm, "end": v(15.38, 2.16) * mm});
            skLineSegment(sketch, "E2006", {"start": v(15.38, 2.16) * mm, "end": v(14.99, 2.7) * mm});
            skLineSegment(sketch, "E2007", {"start": v(14.99, 2.7) * mm, "end": v(14.61, 3.24) * mm});
            skLineSegment(sketch, "E2008", {"start": v(14.61, 3.24) * mm, "end": v(14.25, 3.79) * mm});
            skLineSegment(sketch, "E2009", {"start": v(14.25, 3.79) * mm, "end": v(13.9, 4.35) * mm});
            skLineSegment(sketch, "E2010", {"start": v(13.9, 4.35) * mm, "end": v(13.55, 4.93) * mm});
            skLineSegment(sketch, "E2011", {"start": v(13.55, 4.93) * mm, "end": v(13.2, 5.52) * mm});
            skLineSegment(sketch, "E2012", {"start": v(13.2, 5.52) * mm, "end": v(12.65, 6.5) * mm});
            skLineSegment(sketch, "E2013", {"start": v(12.65, 6.5) * mm, "end": v(12.36, 7) * mm});
            skLineSegment(sketch, "E2014", {"start": v(12.36, 7) * mm, "end": v(12.07, 7.48) * mm});
            skLineSegment(sketch, "E2015", {"start": v(12.07, 7.48) * mm, "end": v(11.58, 7.45) * mm});
            skLineSegment(sketch, "E2016", {"start": v(11.58, 7.45) * mm, "end": v(11.11, 7.43) * mm});
            skLineSegment(sketch, "E2017", {"start": v(11.11, 7.43) * mm, "end": v(10.67, 7.43) * mm});
            skLineSegment(sketch, "E2018", {"start": v(10.67, 7.43) * mm, "end": v(10.45, 7.44) * mm});
            skLineSegment(sketch, "E2019", {"start": v(10.45, 7.44) * mm, "end": v(10.23, 7.46) * mm});
            skLineSegment(sketch, "E2020", {"start": v(10.23, 7.46) * mm, "end": v(10.32, 7.3) * mm});
            skLineSegment(sketch, "E2021", {"start": v(10.32, 7.3) * mm, "end": v(10.4, 7.12) * mm});
            skLineSegment(sketch, "E2022", {"start": v(10.4, 7.12) * mm, "end": v(10.46, 6.94) * mm});
            skLineSegment(sketch, "E2023", {"start": v(10.46, 6.94) * mm, "end": v(10.52, 6.76) * mm});
            skLineSegment(sketch, "E2024", {"start": v(10.52, 6.76) * mm, "end": v(10.56, 6.57) * mm});
            skLineSegment(sketch, "E2025", {"start": v(10.56, 6.57) * mm, "end": v(10.6, 6.37) * mm});
            skLineSegment(sketch, "E2026", {"start": v(10.6, 6.37) * mm, "end": v(10.62, 6.18) * mm});
            skLineSegment(sketch, "E2027", {"start": v(10.62, 6.18) * mm, "end": v(10.62, 5.97) * mm});
            skLineSegment(sketch, "E2028", {"start": v(10.62, 5.97) * mm, "end": v(10.62, 5.82) * mm});
            skLineSegment(sketch, "E2029", {"start": v(10.62, 5.82) * mm, "end": v(10.6, 5.67) * mm});
            skLineSegment(sketch, "E2030", {"start": v(10.6, 5.67) * mm, "end": v(10.56, 5.37) * mm});
            skLineSegment(sketch, "E2031", {"start": v(10.56, 5.37) * mm, "end": v(10.49, 5.08) * mm});
            skLineSegment(sketch, "E2032", {"start": v(10.49, 5.08) * mm, "end": v(10.39, 4.8) * mm});
            skLineSegment(sketch, "E2033", {"start": v(10.39, 4.8) * mm, "end": v(10.26, 4.54) * mm});
            skLineSegment(sketch, "E2034", {"start": v(10.26, 4.54) * mm, "end": v(10.11, 4.3) * mm});
            skLineSegment(sketch, "E2035", {"start": v(10.11, 4.3) * mm, "end": v(9.94, 4.07) * mm});
            skLineSegment(sketch, "E2036", {"start": v(9.94, 4.07) * mm, "end": v(9.74, 3.85) * mm});
            skLineSegment(sketch, "E2037", {"start": v(9.74, 3.85) * mm, "end": v(9.53, 3.66) * mm});
            skLineSegment(sketch, "E2038", {"start": v(9.53, 3.66) * mm, "end": v(9.3, 3.49) * mm});
            skLineSegment(sketch, "E2039", {"start": v(9.3, 3.49) * mm, "end": v(9.05, 3.34) * mm});
            skLineSegment(sketch, "E2040", {"start": v(9.05, 3.34) * mm, "end": v(8.8, 3.2) * mm});
            skLineSegment(sketch, "E2041", {"start": v(8.8, 3.2) * mm, "end": v(8.51, 3.1) * mm});
            skLineSegment(sketch, "E2042", {"start": v(8.51, 3.1) * mm, "end": v(8.23, 3.04) * mm});
            skLineSegment(sketch, "E2043", {"start": v(8.23, 3.04) * mm, "end": v(8.08, 3) * mm});
            skLineSegment(sketch, "E2044", {"start": v(8.08, 3) * mm, "end": v(7.93, 2.99) * mm});
            skLineSegment(sketch, "E2045", {"start": v(7.93, 2.99) * mm, "end": v(7.78, 2.98) * mm});
            skLineSegment(sketch, "E2046", {"start": v(7.78, 2.98) * mm, "end": v(7.62, 2.97) * mm});
            skLineSegment(sketch, "E2047", {"start": v(7.62, 2.97) * mm, "end": v(7.47, 2.98) * mm});
            skLineSegment(sketch, "E2048", {"start": v(7.47, 2.98) * mm, "end": v(7.32, 2.99) * mm});
            skLineSegment(sketch, "E2049", {"start": v(7.32, 2.99) * mm, "end": v(7.02, 3.04) * mm});
            skLineSegment(sketch, "E2050", {"start": v(7.02, 3.04) * mm, "end": v(6.73, 3.1) * mm});
            skLineSegment(sketch, "E2051", {"start": v(6.73, 3.1) * mm, "end": v(6.46, 3.2) * mm});
            skLineSegment(sketch, "E2052", {"start": v(6.46, 3.2) * mm, "end": v(6.2, 3.34) * mm});
            skLineSegment(sketch, "E2053", {"start": v(6.2, 3.34) * mm, "end": v(5.95, 3.49) * mm});
            skLineSegment(sketch, "E2054", {"start": v(5.95, 3.49) * mm, "end": v(5.71, 3.66) * mm});
            skLineSegment(sketch, "E2055", {"start": v(5.71, 3.66) * mm, "end": v(5.5, 3.85) * mm});
            skLineSegment(sketch, "E2056", {"start": v(5.5, 3.85) * mm, "end": v(5.3, 4.07) * mm});
            skLineSegment(sketch, "E2057", {"start": v(5.3, 4.07) * mm, "end": v(5.14, 4.3) * mm});
            skLineSegment(sketch, "E2058", {"start": v(5.14, 4.3) * mm, "end": v(4.98, 4.54) * mm});
            skLineSegment(sketch, "E2059", {"start": v(4.98, 4.54) * mm, "end": v(4.86, 4.8) * mm});
            skLineSegment(sketch, "E2060", {"start": v(4.86, 4.8) * mm, "end": v(4.76, 5.08) * mm});
            skLineSegment(sketch, "E2061", {"start": v(4.76, 5.08) * mm, "end": v(4.68, 5.37) * mm});
            skLineSegment(sketch, "E2062", {"start": v(4.68, 5.37) * mm, "end": v(4.66, 5.52) * mm});
            skLineSegment(sketch, "E2063", {"start": v(4.66, 5.52) * mm, "end": v(4.64, 5.67) * mm});
            skLineSegment(sketch, "E2064", {"start": v(4.64, 5.67) * mm, "end": v(4.63, 5.82) * mm});
            skLineSegment(sketch, "E2065", {"start": v(4.63, 5.82) * mm, "end": v(4.62, 5.97) * mm});
            skLineSegment(sketch, "E2066", {"start": v(4.62, 5.97) * mm, "end": v(4.64, 6.25) * mm});
            skLineSegment(sketch, "E2067", {"start": v(4.64, 6.25) * mm, "end": v(4.67, 6.52) * mm});
            skLineSegment(sketch, "E2068", {"start": v(4.67, 6.52) * mm, "end": v(4.73, 6.78) * mm});
            skLineSegment(sketch, "E2069", {"start": v(4.73, 6.78) * mm, "end": v(4.81, 7.03) * mm});
            skLineSegment(sketch, "E2070", {"start": v(4.81, 7.03) * mm, "end": v(4.91, 7.27) * mm});
            skLineSegment(sketch, "E2071", {"start": v(4.91, 7.27) * mm, "end": v(5.04, 7.5) * mm});
            skLineSegment(sketch, "E2072", {"start": v(5.04, 7.5) * mm, "end": v(5.18, 7.71) * mm});
            skLineSegment(sketch, "E2073", {"start": v(5.18, 7.71) * mm, "end": v(5.33, 7.91) * mm});
            skLineSegment(sketch, "E2074", {"start": v(5.33, 7.91) * mm, "end": v(5.5, 8.1) * mm});
            skLineSegment(sketch, "E2075", {"start": v(5.5, 8.1) * mm, "end": v(5.7, 8.28) * mm});
            skLineSegment(sketch, "E2076", {"start": v(5.7, 8.28) * mm, "end": v(5.9, 8.43) * mm});
            skLineSegment(sketch, "E2077", {"start": v(5.9, 8.43) * mm, "end": v(6.12, 8.57) * mm});
            skLineSegment(sketch, "E2078", {"start": v(6.12, 8.57) * mm, "end": v(6.35, 8.7) * mm});
            skLineSegment(sketch, "E2079", {"start": v(6.35, 8.7) * mm, "end": v(6.6, 8.8) * mm});
            skLineSegment(sketch, "E2080", {"start": v(6.6, 8.8) * mm, "end": v(6.84, 8.87) * mm});
            skLineSegment(sketch, "E2081", {"start": v(6.84, 8.87) * mm, "end": v(7.1, 8.93) * mm});
            skLineSegment(sketch, "E2082", {"start": v(7.1, 8.93) * mm, "end": v(6.88, 9.08) * mm});
            skLineSegment(sketch, "E2083", {"start": v(6.88, 9.08) * mm, "end": v(6.66, 9.2) * mm});
            skLineSegment(sketch, "E2084", {"start": v(6.66, 9.2) * mm, "end": v(6.45, 9.31) * mm});
            skLineSegment(sketch, "E2085", {"start": v(6.45, 9.31) * mm, "end": v(6.34, 9.36) * mm});
            skLineSegment(sketch, "E2086", {"start": v(6.34, 9.36) * mm, "end": v(6.24, 9.39) * mm});
            skLineSegment(sketch, "E2087", {"start": v(6.24, 9.39) * mm, "end": v(6.18, 9.4) * mm});
            skLineSegment(sketch, "E2088", {"start": v(6.18, 9.4) * mm, "end": v(5.99, 9.33) * mm});
            skLineSegment(sketch, "E2089", {"start": v(5.99, 9.33) * mm, "end": v(4.56, 9.33) * mm});
            skLineSegment(sketch, "E2090", {"start": v(4.56, 9.33) * mm, "end": v(4.45, 9.35) * mm});
            skLineSegment(sketch, "E2091", {"start": v(4.45, 9.35) * mm, "end": v(4.17, 9.34) * mm});
            skLineSegment(sketch, "E2092", {"start": v(4.17, 9.34) * mm, "end": v(0.5, 8.44) * mm});
            skLineSegment(sketch, "E2093", {"start": v(0.5, 8.44) * mm, "end": v(0.45, 8.43) * mm});
            skLineSegment(sketch, "E2094", {"start": v(0.45, 8.43) * mm, "end": v(0.1, 8.38) * mm});
            skLineSegment(sketch, "E2095", {"start": v(0.1, 8.38) * mm, "end": v(-0.24, 8.36) * mm});
            skLineSegment(sketch, "E2096", {"start": v(-0.24, 8.36) * mm, "end": v(-0.58, 8.35) * mm});
            skLineSegment(sketch, "E2097", {"start": v(-0.58, 8.35) * mm, "end": v(-0.92, 8.37) * mm});
            skLineSegment(sketch, "E2098", {"start": v(-0.92, 8.37) * mm, "end": v(-1.26, 8.4) * mm});
            skLineSegment(sketch, "E2099", {"start": v(-1.26, 8.4) * mm, "end": v(-1.6, 8.47) * mm});
            skLineSegment(sketch, "E2100", {"start": v(-1.6, 8.47) * mm, "end": v(-1.93, 8.55) * mm});
            skLineSegment(sketch, "E2101", {"start": v(-1.93, 8.55) * mm, "end": v(-2.26, 8.65) * mm});
            skLineSegment(sketch, "E2102", {"start": v(-2.26, 8.65) * mm, "end": v(-2.53, 8.75) * mm});
            skLineSegment(sketch, "E2103", {"start": v(-2.53, 8.75) * mm, "end": v(-2.8, 8.85) * mm});
            skLineSegment(sketch, "E2104", {"start": v(-7.88, -6.43) * mm, "end": v(-7.8, -6.68) * mm});
            skLineSegment(sketch, "E2105", {"start": v(-7.8, -6.68) * mm, "end": v(-7.73, -6.94) * mm});
            skLineSegment(sketch, "E2106", {"start": v(-7.73, -6.94) * mm, "end": v(-7.7, -7.21) * mm});
            skLineSegment(sketch, "E2107", {"start": v(-7.7, -7.21) * mm, "end": v(-7.68, -7.49) * mm});
            skLineSegment(sketch, "E2108", {"start": v(-7.68, -7.49) * mm, "end": v(-7.69, -7.64) * mm});
            skLineSegment(sketch, "E2109", {"start": v(-7.69, -7.64) * mm, "end": v(-7.7, -7.8) * mm});
            skLineSegment(sketch, "E2110", {"start": v(-7.7, -7.8) * mm, "end": v(-7.75, -8.1) * mm});
            skLineSegment(sketch, "E2111", {"start": v(-7.75, -8.1) * mm, "end": v(-7.82, -8.38) * mm});
            skLineSegment(sketch, "E2112", {"start": v(-7.82, -8.38) * mm, "end": v(-7.92, -8.66) * mm});
            skLineSegment(sketch, "E2113", {"start": v(-7.92, -8.66) * mm, "end": v(-8.05, -8.92) * mm});
            skLineSegment(sketch, "E2114", {"start": v(-8.05, -8.92) * mm, "end": v(-8.2, -9.16) * mm});
            skLineSegment(sketch, "E2115", {"start": v(-8.2, -9.16) * mm, "end": v(-8.37, -9.4) * mm});
            skLineSegment(sketch, "E2116", {"start": v(-8.37, -9.4) * mm, "end": v(-8.56, -9.6) * mm});
            skLineSegment(sketch, "E2117", {"start": v(-8.56, -9.6) * mm, "end": v(-8.78, -9.8) * mm});
            skLineSegment(sketch, "E2118", {"start": v(-8.78, -9.8) * mm, "end": v(-9, -9.98) * mm});
            skLineSegment(sketch, "E2119", {"start": v(-9, -9.98) * mm, "end": v(-9.25, -10.13) * mm});
            skLineSegment(sketch, "E2120", {"start": v(-9.25, -10.13) * mm, "end": v(-9.52, -10.25) * mm});
            skLineSegment(sketch, "E2121", {"start": v(-9.52, -10.25) * mm, "end": v(-9.8, -10.35) * mm});
            skLineSegment(sketch, "E2122", {"start": v(-9.8, -10.35) * mm, "end": v(-10.08, -10.43) * mm});
            skLineSegment(sketch, "E2123", {"start": v(-10.08, -10.43) * mm, "end": v(-10.23, -10.45) * mm});
            skLineSegment(sketch, "E2124", {"start": v(-10.23, -10.45) * mm, "end": v(-10.38, -10.47) * mm});
            skLineSegment(sketch, "E2125", {"start": v(-10.38, -10.47) * mm, "end": v(-10.53, -10.48) * mm});
            skLineSegment(sketch, "E2126", {"start": v(-10.53, -10.48) * mm, "end": v(-10.68, -10.49) * mm});
            skLineSegment(sketch, "E2127", {"start": v(-10.68, -10.49) * mm, "end": v(-10.84, -10.48) * mm});
            skLineSegment(sketch, "E2128", {"start": v(-10.84, -10.48) * mm, "end": v(-11, -10.47) * mm});
            skLineSegment(sketch, "E2129", {"start": v(-11, -10.47) * mm, "end": v(-11.29, -10.43) * mm});
            skLineSegment(sketch, "E2130", {"start": v(-11.29, -10.43) * mm, "end": v(-11.58, -10.35) * mm});
            skLineSegment(sketch, "E2131", {"start": v(-11.58, -10.35) * mm, "end": v(-11.85, -10.25) * mm});
            skLineSegment(sketch, "E2132", {"start": v(-11.85, -10.25) * mm, "end": v(-12.11, -10.13) * mm});
            skLineSegment(sketch, "E2133", {"start": v(-12.11, -10.13) * mm, "end": v(-12.36, -9.98) * mm});
            skLineSegment(sketch, "E2134", {"start": v(-12.36, -9.98) * mm, "end": v(-12.6, -9.8) * mm});
            skLineSegment(sketch, "E2135", {"start": v(-12.6, -9.8) * mm, "end": v(-12.8, -9.6) * mm});
            skLineSegment(sketch, "E2136", {"start": v(-12.8, -9.6) * mm, "end": v(-13, -9.4) * mm});
            skLineSegment(sketch, "E2137", {"start": v(-13, -9.4) * mm, "end": v(-13.17, -9.16) * mm});
            skLineSegment(sketch, "E2138", {"start": v(-13.17, -9.16) * mm, "end": v(-13.32, -8.92) * mm});
            skLineSegment(sketch, "E2139", {"start": v(-13.32, -8.92) * mm, "end": v(-13.45, -8.66) * mm});
            skLineSegment(sketch, "E2140", {"start": v(-13.45, -8.66) * mm, "end": v(-13.55, -8.38) * mm});
            skLineSegment(sketch, "E2141", {"start": v(-13.55, -8.38) * mm, "end": v(-13.62, -8.1) * mm});
            skLineSegment(sketch, "E2142", {"start": v(-13.62, -8.1) * mm, "end": v(-13.65, -7.94) * mm});
            skLineSegment(sketch, "E2143", {"start": v(-13.65, -7.94) * mm, "end": v(-13.67, -7.8) * mm});
            skLineSegment(sketch, "E2144", {"start": v(-13.67, -7.8) * mm, "end": v(-13.68, -7.64) * mm});
            skLineSegment(sketch, "E2145", {"start": v(-13.68, -7.64) * mm, "end": v(-13.69, -7.49) * mm});
            skLineSegment(sketch, "E2146", {"start": v(-13.69, -7.49) * mm, "end": v(-13.68, -7.25) * mm});
            skLineSegment(sketch, "E2147", {"start": v(-13.68, -7.25) * mm, "end": v(-13.65, -7.02) * mm});
            skLineSegment(sketch, "E2148", {"start": v(-13.65, -7.02) * mm, "end": v(-13.6, -6.79) * mm});
            skLineSegment(sketch, "E2149", {"start": v(-13.6, -6.79) * mm, "end": v(-13.54, -6.57) * mm});
            skLineSegment(sketch, "E2150", {"start": v(-13.54, -6.57) * mm, "end": v(-13.46, -6.35) * mm});
            skLineSegment(sketch, "E2151", {"start": v(-13.46, -6.35) * mm, "end": v(-13.37, -6.15) * mm});
            skLineSegment(sketch, "E2152", {"start": v(-13.37, -6.15) * mm, "end": v(-13.26, -5.95) * mm});
            skLineSegment(sketch, "E2153", {"start": v(-13.26, -5.95) * mm, "end": v(-13.14, -5.76) * mm});
            skLineSegment(sketch, "E2154", {"start": v(-13.14, -5.76) * mm, "end": v(-13, -5.59) * mm});
            skLineSegment(sketch, "E2155", {"start": v(-13, -5.59) * mm, "end": v(-12.86, -5.42) * mm});
            skLineSegment(sketch, "E2156", {"start": v(-12.86, -5.42) * mm, "end": v(-12.7, -5.26) * mm});
            skLineSegment(sketch, "E2157", {"start": v(-12.7, -5.26) * mm, "end": v(-12.53, -5.12) * mm});
            skLineSegment(sketch, "E2158", {"start": v(-12.53, -5.12) * mm, "end": v(-12.35, -4.99) * mm});
            skLineSegment(sketch, "E2159", {"start": v(-12.35, -4.99) * mm, "end": v(-12.16, -4.87) * mm});
            skLineSegment(sketch, "E2160", {"start": v(-12.16, -4.87) * mm, "end": v(-11.95, -4.77) * mm});
            skLineSegment(sketch, "E2161", {"start": v(-11.95, -4.77) * mm, "end": v(-11.75, -4.68) * mm});
            skLineSegment(sketch, "E2162", {"start": v(-11.75, -4.68) * mm, "end": v(-12.05, -4.64) * mm});
            skLineSegment(sketch, "E2163", {"start": v(-12.05, -4.64) * mm, "end": v(-12.34, -4.61) * mm});
            skLineSegment(sketch, "E2164", {"start": v(-12.34, -4.61) * mm, "end": v(-12.61, -4.61) * mm});
            skLineSegment(sketch, "E2165", {"start": v(-12.61, -4.61) * mm, "end": v(-12.88, -4.63) * mm});
            skLineSegment(sketch, "E2166", {"start": v(-12.88, -4.63) * mm, "end": v(-13.13, -4.66) * mm});
            skLineSegment(sketch, "E2167", {"start": v(-13.13, -4.66) * mm, "end": v(-13.38, -4.71) * mm});
            skLineSegment(sketch, "E2168", {"start": v(-13.38, -4.71) * mm, "end": v(-13.62, -4.78) * mm});
            skLineSegment(sketch, "E2169", {"start": v(-13.62, -4.78) * mm, "end": v(-13.86, -4.87) * mm});
            skLineSegment(sketch, "E2170", {"start": v(-13.86, -4.87) * mm, "end": v(-14.09, -4.97) * mm});
            skLineSegment(sketch, "E2171", {"start": v(-14.09, -4.97) * mm, "end": v(-14.32, -5.08) * mm});
            skLineSegment(sketch, "E2172", {"start": v(-14.32, -5.08) * mm, "end": v(-14.54, -5.2) * mm});
            skLineSegment(sketch, "E2173", {"start": v(-14.54, -5.2) * mm, "end": v(-14.77, -5.35) * mm});
            skLineSegment(sketch, "E2174", {"start": v(-14.77, -5.35) * mm, "end": v(-15.23, -5.66) * mm});
            skLineSegment(sketch, "E2175", {"start": v(-15.23, -5.66) * mm, "end": v(-15.7, -6.02) * mm});
            skLineSegment(sketch, "E2176", {"start": v(-15.7, -6.02) * mm, "end": v(-16.24, -6.41) * mm});
            skLineSegment(sketch, "E2177", {"start": v(-16.24, -6.41) * mm, "end": v(-16.52, -6.6) * mm});
            skLineSegment(sketch, "E2178", {"start": v(-16.52, -6.6) * mm, "end": v(-16.8, -6.8) * mm});
            skLineSegment(sketch, "E2179", {"start": v(-16.8, -6.8) * mm, "end": v(-17.09, -6.97) * mm});
            skLineSegment(sketch, "E2180", {"start": v(-17.09, -6.97) * mm, "end": v(-17.38, -7.13) * mm});
            skLineSegment(sketch, "E2181", {"start": v(-17.38, -7.13) * mm, "end": v(-17.68, -7.28) * mm});
            skLineSegment(sketch, "E2182", {"start": v(-17.68, -7.28) * mm, "end": v(-17.98, -7.42) * mm});
            skLineSegment(sketch, "E2183", {"start": v(-17.98, -7.42) * mm, "end": v(-18.19, -7.5) * mm});
            skLineSegment(sketch, "E2184", {"start": v(-18.19, -7.5) * mm, "end": v(-18.38, -7.55) * mm});
            skLineSegment(sketch, "E2185", {"start": v(-18.38, -7.55) * mm, "end": v(-18.56, -7.6) * mm});
            skLineSegment(sketch, "E2186", {"start": v(-18.56, -7.6) * mm, "end": v(-18.75, -7.64) * mm});
            skLineSegment(sketch, "E2187", {"start": v(-18.75, -7.64) * mm, "end": v(-19, -8.16) * mm});
            skLineSegment(sketch, "E2188", {"start": v(-19, -8.16) * mm, "end": v(-19.22, -8.63) * mm});
            skLineSegment(sketch, "E2189", {"start": v(-19.22, -8.63) * mm, "end": v(-19.48, -9.17) * mm});
            skLineSegment(sketch, "E2190", {"start": v(-19.48, -9.17) * mm, "end": v(-19.77, -9.73) * mm});
            skLineSegment(sketch, "E2191", {"start": v(-19.77, -9.73) * mm, "end": v(-20.1, -10.3) * mm});
            skLineSegment(sketch, "E2192", {"start": v(-20.1, -10.3) * mm, "end": v(-20.44, -10.9) * mm});
            skLineSegment(sketch, "E2193", {"start": v(-20.44, -10.9) * mm, "end": v(-20.8, -11.5) * mm});
            skLineSegment(sketch, "E2194", {"start": v(-20.8, -11.5) * mm, "end": v(-21.2, -12.12) * mm});
            skLineSegment(sketch, "E2195", {"start": v(-21.2, -12.12) * mm, "end": v(-21.6, -12.73) * mm});
            skLineSegment(sketch, "E2196", {"start": v(-21.6, -12.73) * mm, "end": v(-22.03, -13.33) * mm});
            skLineSegment(sketch, "E2197", {"start": v(-22.03, -13.33) * mm, "end": v(-22.46, -13.92) * mm});
            skLineSegment(sketch, "E2198", {"start": v(-22.46, -13.92) * mm, "end": v(-22.91, -14.5) * mm});
            skLineSegment(sketch, "E2199", {"start": v(-22.91, -14.5) * mm, "end": v(-23.37, -15.06) * mm});
            skLineSegment(sketch, "E2200", {"start": v(-23.37, -15.06) * mm, "end": v(-23.83, -15.6) * mm});
            skLineSegment(sketch, "E2201", {"start": v(-23.83, -15.6) * mm, "end": v(-24.29, -16.1) * mm});
            skLineSegment(sketch, "E2202", {"start": v(-24.29, -16.1) * mm, "end": v(-24.75, -16.57) * mm});
            skLineSegment(sketch, "E2203", {"start": v(-24.75, -16.57) * mm, "end": v(-25.22, -17) * mm});
            skLineSegment(sketch, "E2204", {"start": v(-25.22, -17) * mm, "end": v(-25.45, -17.19) * mm});
            skLineSegment(sketch, "E2205", {"start": v(-25.45, -17.19) * mm, "end": v(-25.68, -17.37) * mm});
            skLineSegment(sketch, "E2206", {"start": v(-25.68, -17.37) * mm, "end": v(-25.34, -17.45) * mm});
            skLineSegment(sketch, "E2207", {"start": v(-25.34, -17.45) * mm, "end": v(-25, -17.5) * mm});
            skLineSegment(sketch, "E2208", {"start": v(-25, -17.5) * mm, "end": v(-24.84, -17.52) * mm});
            skLineSegment(sketch, "E2209", {"start": v(-24.84, -17.52) * mm, "end": v(-24.7, -17.52) * mm});
            skLineSegment(sketch, "E2210", {"start": v(-24.7, -17.52) * mm, "end": v(-24.58, -17.52) * mm});
            skLineSegment(sketch, "E2211", {"start": v(-24.58, -17.52) * mm, "end": v(-24.48, -17.5) * mm});
            skLineSegment(sketch, "E2212", {"start": v(-24.48, -17.5) * mm, "end": v(-24.35, -17.46) * mm});
            skLineSegment(sketch, "E2213", {"start": v(-24.35, -17.46) * mm, "end": v(-24.22, -17.4) * mm});
            skLineSegment(sketch, "E2214", {"start": v(-24.22, -17.4) * mm, "end": v(-23.97, -17.28) * mm});
            skLineSegment(sketch, "E2215", {"start": v(-23.97, -17.28) * mm, "end": v(-23.41, -17.01) * mm});
            skLineSegment(sketch, "E2216", {"start": v(-23.41, -17.01) * mm, "end": v(-22.86, -16.75) * mm});
            skLineSegment(sketch, "E2217", {"start": v(-22.86, -16.75) * mm, "end": v(-22.43, -16.55) * mm});
            skLineSegment(sketch, "E2218", {"start": v(-22.43, -16.55) * mm, "end": v(-22, -16.37) * mm});
            skLineSegment(sketch, "E2219", {"start": v(-22, -16.37) * mm, "end": v(-21.56, -16.2) * mm});
            skLineSegment(sketch, "E2220", {"start": v(-21.56, -16.2) * mm, "end": v(-21.13, -16.03) * mm});
            skLineSegment(sketch, "E2221", {"start": v(-21.13, -16.03) * mm, "end": v(-20.69, -15.88) * mm});
            skLineSegment(sketch, "E2222", {"start": v(-20.69, -15.88) * mm, "end": v(-20.24, -15.74) * mm});
            skLineSegment(sketch, "E2223", {"start": v(-20.24, -15.74) * mm, "end": v(-19.8, -15.6) * mm});
            skLineSegment(sketch, "E2224", {"start": v(-19.8, -15.6) * mm, "end": v(-19.34, -15.49) * mm});
            skLineSegment(sketch, "E2225", {"start": v(-19.34, -15.49) * mm, "end": v(-18.91, -15.39) * mm});
            skLineSegment(sketch, "E2226", {"start": v(-18.91, -15.39) * mm, "end": v(-18.48, -15.3) * mm});
            skLineSegment(sketch, "E2227", {"start": v(-18.48, -15.3) * mm, "end": v(-18.04, -15.23) * mm});
            skLineSegment(sketch, "E2228", {"start": v(-18.04, -15.23) * mm, "end": v(-17.6, -15.17) * mm});
            skLineSegment(sketch, "E2229", {"start": v(-17.6, -15.17) * mm, "end": v(-17.16, -15.13) * mm});
            skLineSegment(sketch, "E2230", {"start": v(-17.16, -15.13) * mm, "end": v(-16.72, -15.1) * mm});
            skLineSegment(sketch, "E2231", {"start": v(-16.72, -15.1) * mm, "end": v(-16.27, -15.08) * mm});
            skLineSegment(sketch, "E2232", {"start": v(-16.27, -15.08) * mm, "end": v(-15.83, -15.07) * mm});
            skLineSegment(sketch, "E2233", {"start": v(-15.83, -15.07) * mm, "end": v(-15.38, -15.09) * mm});
            skLineSegment(sketch, "E2234", {"start": v(-15.38, -15.09) * mm, "end": v(-14.94, -15.11) * mm});
            skLineSegment(sketch, "E2235", {"start": v(-14.94, -15.11) * mm, "end": v(-14.5, -15.15) * mm});
            skLineSegment(sketch, "E2236", {"start": v(-14.5, -15.15) * mm, "end": v(-14.06, -15.2) * mm});
            skLineSegment(sketch, "E2237", {"start": v(-14.06, -15.2) * mm, "end": v(-13.62, -15.28) * mm});
            skLineSegment(sketch, "E2238", {"start": v(-13.62, -15.28) * mm, "end": v(-13.19, -15.37) * mm});
            skLineSegment(sketch, "E2239", {"start": v(-13.19, -15.37) * mm, "end": v(-12.76, -15.47) * mm});
            skLineSegment(sketch, "E2240", {"start": v(-12.76, -15.47) * mm, "end": v(-12.33, -15.59) * mm});
            skLineSegment(sketch, "E2241", {"start": v(-12.33, -15.59) * mm, "end": v(-11.67, -15.8) * mm});
            skLineSegment(sketch, "E2242", {"start": v(-11.67, -15.8) * mm, "end": v(-11.03, -16.02) * mm});
            skLineSegment(sketch, "E2243", {"start": v(-11.03, -16.02) * mm, "end": v(-10.4, -16.24) * mm});
            skLineSegment(sketch, "E2244", {"start": v(-10.4, -16.24) * mm, "end": v(-9.78, -16.45) * mm});
            skLineSegment(sketch, "E2245", {"start": v(-9.78, -16.45) * mm, "end": v(-9.47, -16.55) * mm});
            skLineSegment(sketch, "E2246", {"start": v(-9.47, -16.55) * mm, "end": v(-9.15, -16.64) * mm});
            skLineSegment(sketch, "E2247", {"start": v(-9.15, -16.64) * mm, "end": v(-8.83, -16.72) * mm});
            skLineSegment(sketch, "E2248", {"start": v(-8.83, -16.72) * mm, "end": v(-8.5, -16.8) * mm});
            skLineSegment(sketch, "E2249", {"start": v(-8.5, -16.8) * mm, "end": v(-8.18, -16.86) * mm});
            skLineSegment(sketch, "E2250", {"start": v(-8.18, -16.86) * mm, "end": v(-7.84, -16.9) * mm});
            skLineSegment(sketch, "E2251", {"start": v(-7.84, -16.9) * mm, "end": v(-7.49, -16.94) * mm});
            skLineSegment(sketch, "E2252", {"start": v(-7.49, -16.94) * mm, "end": v(-7.13, -16.97) * mm});
            skLineSegment(sketch, "E2253", {"start": v(-7.13, -16.97) * mm, "end": v(-6.77, -16.97) * mm});
            skLineSegment(sketch, "E2254", {"start": v(-6.77, -16.97) * mm, "end": v(-6.45, -16.96) * mm});
            skLineSegment(sketch, "E2255", {"start": v(-6.45, -16.96) * mm, "end": v(-6.14, -16.94) * mm});
            skLineSegment(sketch, "E2256", {"start": v(-6.14, -16.94) * mm, "end": v(-5.84, -16.89) * mm});
            skLineSegment(sketch, "E2257", {"start": v(-5.84, -16.89) * mm, "end": v(-5.55, -16.82) * mm});
            skLineSegment(sketch, "E2258", {"start": v(-5.55, -16.82) * mm, "end": v(-5.26, -16.73) * mm});
            skLineSegment(sketch, "E2259", {"start": v(-5.26, -16.73) * mm, "end": v(-4.95, -16.6) * mm});
            skLineSegment(sketch, "E2260", {"start": v(-4.95, -16.6) * mm, "end": v(-4.63, -16.46) * mm});
            skLineSegment(sketch, "E2261", {"start": v(-4.63, -16.46) * mm, "end": v(-3.97, -16.14) * mm});
            skLineSegment(sketch, "E2262", {"start": v(-3.97, -16.14) * mm, "end": v(-3.64, -15.99) * mm});
            skLineSegment(sketch, "E2263", {"start": v(-3.64, -15.99) * mm, "end": v(-3.32, -15.84) * mm});
            skLineSegment(sketch, "E2264", {"start": v(-3.32, -15.84) * mm, "end": v(-3, -15.71) * mm});
            skLineSegment(sketch, "E2265", {"start": v(-3, -15.71) * mm, "end": v(-2.67, -15.59) * mm});
            skLineSegment(sketch, "E2266", {"start": v(-2.67, -15.59) * mm, "end": v(-2.32, -15.47) * mm});
            skLineSegment(sketch, "E2267", {"start": v(-2.32, -15.47) * mm, "end": v(-1.94, -15.37) * mm});
            skLineSegment(sketch, "E2268", {"start": v(-1.94, -15.37) * mm, "end": v(-1.62, -15.3) * mm});
            skLineSegment(sketch, "E2269", {"start": v(-1.62, -15.3) * mm, "end": v(-1.3, -15.23) * mm});
            skLineSegment(sketch, "E2270", {"start": v(-1.3, -15.23) * mm, "end": v(-0.98, -15.17) * mm});
            skLineSegment(sketch, "E2271", {"start": v(-0.98, -15.17) * mm, "end": v(-0.65, -15.13) * mm});
            skLineSegment(sketch, "E2272", {"start": v(-0.65, -15.13) * mm, "end": v(-0.33, -15.09) * mm});
            skLineSegment(sketch, "E2273", {"start": v(-0.33, -15.09) * mm, "end": v(0, -15.06) * mm});
            skLineSegment(sketch, "E2274", {"start": v(0, -15.06) * mm, "end": v(0.32, -15.04) * mm});
            skLineSegment(sketch, "E2275", {"start": v(0.32, -15.04) * mm, "end": v(0.64, -15.03) * mm});
            skLineSegment(sketch, "E2276", {"start": v(0.64, -15.03) * mm, "end": v(0.96, -15.03) * mm});
            skLineSegment(sketch, "E2277", {"start": v(0.96, -15.03) * mm, "end": v(1.28, -15.04) * mm});
            skLineSegment(sketch, "E2278", {"start": v(1.28, -15.04) * mm, "end": v(1.6, -15.05) * mm});
            skLineSegment(sketch, "E2279", {"start": v(1.6, -15.05) * mm, "end": v(1.93, -15.08) * mm});
            skLineSegment(sketch, "E2280", {"start": v(1.93, -15.08) * mm, "end": v(2.26, -15.11) * mm});
            skLineSegment(sketch, "E2281", {"start": v(2.26, -15.11) * mm, "end": v(2.58, -15.15) * mm});
            skLineSegment(sketch, "E2282", {"start": v(2.58, -15.15) * mm, "end": v(2.9, -15.2) * mm});
            skLineSegment(sketch, "E2283", {"start": v(2.9, -15.2) * mm, "end": v(3.23, -15.26) * mm});
            skLineSegment(sketch, "E2284", {"start": v(3.23, -15.26) * mm, "end": v(3.68, -15.36) * mm});
            skLineSegment(sketch, "E2285", {"start": v(3.68, -15.36) * mm, "end": v(4.13, -15.47) * mm});
            skLineSegment(sketch, "E2286", {"start": v(4.13, -15.47) * mm, "end": v(4.57, -15.59) * mm});
            skLineSegment(sketch, "E2287", {"start": v(4.57, -15.59) * mm, "end": v(5.01, -15.72) * mm});
            skLineSegment(sketch, "E2288", {"start": v(5.01, -15.72) * mm, "end": v(5.45, -15.87) * mm});
            skLineSegment(sketch, "E2289", {"start": v(5.45, -15.87) * mm, "end": v(5.88, -16.02) * mm});
            skLineSegment(sketch, "E2290", {"start": v(5.88, -16.02) * mm, "end": v(6.3, -16.18) * mm});
            skLineSegment(sketch, "E2291", {"start": v(6.3, -16.18) * mm, "end": v(6.73, -16.35) * mm});
            skLineSegment(sketch, "E2292", {"start": v(6.73, -16.35) * mm, "end": v(7.58, -16.71) * mm});
            skLineSegment(sketch, "E2293", {"start": v(7.58, -16.71) * mm, "end": v(8.41, -17.1) * mm});
            skLineSegment(sketch, "E2294", {"start": v(8.41, -17.1) * mm, "end": v(10.07, -17.9) * mm});
            skLineSegment(sketch, "E2295", {"start": v(10.07, -17.9) * mm, "end": v(11.29, -18.48) * mm});
            skLineSegment(sketch, "E2296", {"start": v(11.29, -18.48) * mm, "end": v(11.9, -18.77) * mm});
            skLineSegment(sketch, "E2297", {"start": v(11.9, -18.77) * mm, "end": v(12.53, -19.04) * mm});
            skLineSegment(sketch, "E2298", {"start": v(12.53, -19.04) * mm, "end": v(13.16, -19.3) * mm});
            skLineSegment(sketch, "E2299", {"start": v(13.16, -19.3) * mm, "end": v(13.8, -19.55) * mm});
            skLineSegment(sketch, "E2300", {"start": v(13.8, -19.55) * mm, "end": v(14.44, -19.77) * mm});
            skLineSegment(sketch, "E2301", {"start": v(14.44, -19.77) * mm, "end": v(14.76, -19.87) * mm});
            skLineSegment(sketch, "E2302", {"start": v(14.76, -19.87) * mm, "end": v(15.08, -19.96) * mm});
            skLineSegment(sketch, "E2303", {"start": v(15.08, -19.96) * mm, "end": v(15.36, -20.04) * mm});
            skLineSegment(sketch, "E2304", {"start": v(15.36, -20.04) * mm, "end": v(15.75, -20.13) * mm});
            skLineSegment(sketch, "E2305", {"start": v(15.75, -20.13) * mm, "end": v(16.16, -20.22) * mm});
            skLineSegment(sketch, "E2306", {"start": v(16.16, -20.22) * mm, "end": v(16.36, -20.25) * mm});
            skLineSegment(sketch, "E2307", {"start": v(16.36, -20.25) * mm, "end": v(16.52, -20.26) * mm});
            skLineSegment(sketch, "E2308", {"start": v(16.52, -20.26) * mm, "end": v(16.6, -20.06) * mm});
            skLineSegment(sketch, "E2309", {"start": v(16.6, -20.06) * mm, "end": v(16.67, -19.9) * mm});
            skLineSegment(sketch, "E2310", {"start": v(16.67, -19.9) * mm, "end": v(16.92, -19.2) * mm});
            skLineSegment(sketch, "E2311", {"start": v(16.92, -19.2) * mm, "end": v(17.19, -18.5) * mm});
            skLineSegment(sketch, "E2312", {"start": v(17.19, -18.5) * mm, "end": v(17.3, -18.24) * mm});
            skLineSegment(sketch, "E2313", {"start": v(17.3, -18.24) * mm, "end": v(17.4, -17.99) * mm});
            skLineSegment(sketch, "E2314", {"start": v(17.4, -17.99) * mm, "end": v(17.53, -17.74) * mm});
            skLineSegment(sketch, "E2315", {"start": v(17.53, -17.74) * mm, "end": v(17.67, -17.5) * mm});
            skLineSegment(sketch, "E2316", {"start": v(17.67, -17.5) * mm, "end": v(17.81, -17.28) * mm});
            skLineSegment(sketch, "E2317", {"start": v(17.81, -17.28) * mm, "end": v(17.97, -17.05) * mm});
            skLineSegment(sketch, "E2318", {"start": v(17.97, -17.05) * mm, "end": v(18.13, -16.84) * mm});
            skLineSegment(sketch, "E2319", {"start": v(18.13, -16.84) * mm, "end": v(18.3, -16.64) * mm});
            skLineSegment(sketch, "E2320", {"start": v(18.3, -16.64) * mm, "end": v(18.5, -16.46) * mm});
            skLineSegment(sketch, "E2321", {"start": v(18.5, -16.46) * mm, "end": v(18.7, -16.28) * mm});
            skLineSegment(sketch, "E2322", {"start": v(18.7, -16.28) * mm, "end": v(18.9, -16.12) * mm});
            skLineSegment(sketch, "E2323", {"start": v(18.9, -16.12) * mm, "end": v(19.13, -15.98) * mm});
            skLineSegment(sketch, "E2324", {"start": v(19.13, -15.98) * mm, "end": v(19.37, -15.85) * mm});
            skLineSegment(sketch, "E2325", {"start": v(19.37, -15.85) * mm, "end": v(19.62, -15.74) * mm});
            skLineSegment(sketch, "E2326", {"start": v(19.62, -15.74) * mm, "end": v(19.88, -15.64) * mm});
            skLineSegment(sketch, "E2327", {"start": v(19.88, -15.64) * mm, "end": v(20.16, -15.57) * mm});
            skLineSegment(sketch, "E2328", {"start": v(20.16, -15.57) * mm, "end": v(20.4, -15.52) * mm});
            skLineSegment(sketch, "E2329", {"start": v(20.4, -15.52) * mm, "end": v(20.63, -15.5) * mm});
            skLineSegment(sketch, "E2330", {"start": v(20.63, -15.5) * mm, "end": v(20.86, -15.48) * mm});
            skLineSegment(sketch, "E2331", {"start": v(20.86, -15.48) * mm, "end": v(21.09, -15.48) * mm});
            skLineSegment(sketch, "E2332", {"start": v(21.09, -15.48) * mm, "end": v(21.32, -15.49) * mm});
            skLineSegment(sketch, "E2333", {"start": v(21.32, -15.49) * mm, "end": v(21.55, -15.5) * mm});
            skLineSegment(sketch, "E2334", {"start": v(21.55, -15.5) * mm, "end": v(21.77, -15.54) * mm});
            skLineSegment(sketch, "E2335", {"start": v(21.77, -15.54) * mm, "end": v(22, -15.58) * mm});
            skLineSegment(sketch, "E2336", {"start": v(22, -15.58) * mm, "end": v(22.23, -15.63) * mm});
            skLineSegment(sketch, "E2337", {"start": v(22.23, -15.63) * mm, "end": v(22.45, -15.7) * mm});
            skLineSegment(sketch, "E2338", {"start": v(22.45, -15.7) * mm, "end": v(22.9, -15.83) * mm});
            skLineSegment(sketch, "E2339", {"start": v(22.9, -15.83) * mm, "end": v(23.34, -16) * mm});
            skLineSegment(sketch, "E2340", {"start": v(23.34, -16) * mm, "end": v(23.77, -16.17) * mm});
            skLineSegment(sketch, "E2341", {"start": v(23.77, -16.17) * mm, "end": v(23.45, -15.85) * mm});
            skLineSegment(sketch, "E2342", {"start": v(23.45, -15.85) * mm, "end": v(23.05, -15.42) * mm});
            skLineSegment(sketch, "E2343", {"start": v(23.05, -15.42) * mm, "end": v(22.67, -14.99) * mm});
            skLineSegment(sketch, "E2344", {"start": v(22.67, -14.99) * mm, "end": v(22.31, -14.54) * mm});
            skLineSegment(sketch, "E2345", {"start": v(22.31, -14.54) * mm, "end": v(21.96, -14.07) * mm});
            skLineSegment(sketch, "E2346", {"start": v(21.96, -14.07) * mm, "end": v(21.63, -13.6) * mm});
            skLineSegment(sketch, "E2347", {"start": v(21.63, -13.6) * mm, "end": v(21.3, -13.12) * mm});
            skLineSegment(sketch, "E2348", {"start": v(21.3, -13.12) * mm, "end": v(21, -12.63) * mm});
            skLineSegment(sketch, "E2349", {"start": v(21, -12.63) * mm, "end": v(20.7, -12.13) * mm});
            skLineSegment(sketch, "E2350", {"start": v(20.7, -12.13) * mm, "end": v(20.54, -11.86) * mm});
            skLineSegment(sketch, "E2351", {"start": v(20.54, -11.86) * mm, "end": v(20.39, -11.57) * mm});
            skLineSegment(sketch, "E2352", {"start": v(20.39, -11.57) * mm, "end": v(20.1, -10.95) * mm});
            skLineSegment(sketch, "E2353", {"start": v(20.1, -10.95) * mm, "end": v(19.84, -10.31) * mm});
            skLineSegment(sketch, "E2354", {"start": v(19.84, -10.31) * mm, "end": v(19.6, -9.71) * mm});
            skLineSegment(sketch, "E2355", {"start": v(19.6, -9.71) * mm, "end": v(19.02, -8.31) * mm});
            skLineSegment(sketch, "E2356", {"start": v(19.02, -8.31) * mm, "end": v(18.82, -7.83) * mm});
            skLineSegment(sketch, "E2357", {"start": v(18.82, -7.83) * mm, "end": v(18.32, -7.62) * mm});
            skLineSegment(sketch, "E2358", {"start": v(18.32, -7.62) * mm, "end": v(17.64, -7.35) * mm});
            skLineSegment(sketch, "E2359", {"start": v(17.64, -7.35) * mm, "end": v(16.94, -7.1) * mm});
            skLineSegment(sketch, "E2360", {"start": v(16.94, -7.1) * mm, "end": v(16.14, -6.82) * mm});
            skLineSegment(sketch, "E2361", {"start": v(16.14, -6.82) * mm, "end": v(15.33, -6.56) * mm});
            skLineSegment(sketch, "E2362", {"start": v(15.33, -6.56) * mm, "end": v(13.93, -6.25) * mm});
            skLineSegment(sketch, "E2363", {"start": v(13.93, -6.25) * mm, "end": v(13.44, -6.22) * mm});
            skLineSegment(sketch, "E2364", {"start": v(13.44, -6.22) * mm, "end": v(12.96, -6.21) * mm});
            skLineSegment(sketch, "E2365", {"start": v(12.96, -6.21) * mm, "end": v(12.5, -6.23) * mm});
            skLineSegment(sketch, "E2366", {"start": v(12.5, -6.23) * mm, "end": v(12.06, -6.27) * mm});
            skLineSegment(sketch, "E2367", {"start": v(12.06, -6.27) * mm, "end": v(11.62, -6.33) * mm});
            skLineSegment(sketch, "E2368", {"start": v(11.62, -6.33) * mm, "end": v(11.18, -6.42) * mm});
            skLineSegment(sketch, "E2369", {"start": v(11.18, -6.42) * mm, "end": v(10.75, -6.54) * mm});
            skLineSegment(sketch, "E2370", {"start": v(10.75, -6.54) * mm, "end": v(10.3, -6.68) * mm});
            skLineSegment(sketch, "E2371", {"start": v(10.3, -6.68) * mm, "end": v(10.53, -6.76) * mm});
            skLineSegment(sketch, "E2372", {"start": v(10.53, -6.76) * mm, "end": v(10.76, -6.85) * mm});
            skLineSegment(sketch, "E2373", {"start": v(10.76, -6.85) * mm, "end": v(10.97, -6.97) * mm});
            skLineSegment(sketch, "E2374", {"start": v(10.97, -6.97) * mm, "end": v(11.17, -7.1) * mm});
            skLineSegment(sketch, "E2375", {"start": v(11.17, -7.1) * mm, "end": v(11.36, -7.24) * mm});
            skLineSegment(sketch, "E2376", {"start": v(11.36, -7.24) * mm, "end": v(11.54, -7.4) * mm});
            skLineSegment(sketch, "E2377", {"start": v(11.54, -7.4) * mm, "end": v(11.7, -7.56) * mm});
            skLineSegment(sketch, "E2378", {"start": v(11.7, -7.56) * mm, "end": v(11.86, -7.75) * mm});
            skLineSegment(sketch, "E2379", {"start": v(11.86, -7.75) * mm, "end": v(12, -7.94) * mm});
            skLineSegment(sketch, "E2380", {"start": v(12, -7.94) * mm, "end": v(12.11, -8.15) * mm});
            skLineSegment(sketch, "E2381", {"start": v(12.11, -8.15) * mm, "end": v(12.22, -8.36) * mm});
            skLineSegment(sketch, "E2382", {"start": v(12.22, -8.36) * mm, "end": v(12.3, -8.59) * mm});
            skLineSegment(sketch, "E2383", {"start": v(12.3, -8.59) * mm, "end": v(12.38, -8.82) * mm});
            skLineSegment(sketch, "E2384", {"start": v(12.38, -8.82) * mm, "end": v(12.43, -9.06) * mm});
            skLineSegment(sketch, "E2385", {"start": v(12.43, -9.06) * mm, "end": v(12.46, -9.31) * mm});
            skLineSegment(sketch, "E2386", {"start": v(12.46, -9.31) * mm, "end": v(12.47, -9.56) * mm});
            skLineSegment(sketch, "E2387", {"start": v(12.47, -9.56) * mm, "end": v(12.47, -9.72) * mm});
            skLineSegment(sketch, "E2388", {"start": v(12.47, -9.72) * mm, "end": v(12.45, -9.87) * mm});
            skLineSegment(sketch, "E2389", {"start": v(12.45, -9.87) * mm, "end": v(12.4, -10.17) * mm});
            skLineSegment(sketch, "E2390", {"start": v(12.4, -10.17) * mm, "end": v(12.33, -10.46) * mm});
            skLineSegment(sketch, "E2391", {"start": v(12.33, -10.46) * mm, "end": v(12.23, -10.73) * mm});
            skLineSegment(sketch, "E2392", {"start": v(12.23, -10.73) * mm, "end": v(12.1, -11) * mm});
            skLineSegment(sketch, "E2393", {"start": v(12.1, -11) * mm, "end": v(11.96, -11.24) * mm});
            skLineSegment(sketch, "E2394", {"start": v(11.96, -11.24) * mm, "end": v(11.78, -11.47) * mm});
            skLineSegment(sketch, "E2395", {"start": v(11.78, -11.47) * mm, "end": v(11.6, -11.69) * mm});
            skLineSegment(sketch, "E2396", {"start": v(11.6, -11.69) * mm, "end": v(11.38, -11.88) * mm});
            skLineSegment(sketch, "E2397", {"start": v(11.38, -11.88) * mm, "end": v(11.15, -12.05) * mm});
            skLineSegment(sketch, "E2398", {"start": v(11.15, -12.05) * mm, "end": v(10.9, -12.2) * mm});
            skLineSegment(sketch, "E2399", {"start": v(10.9, -12.2) * mm, "end": v(10.64, -12.33) * mm});
            skLineSegment(sketch, "E2400", {"start": v(10.64, -12.33) * mm, "end": v(10.36, -12.43) * mm});
            skLineSegment(sketch, "E2401", {"start": v(10.36, -12.43) * mm, "end": v(10.07, -12.5) * mm});
            skLineSegment(sketch, "E2402", {"start": v(10.07, -12.5) * mm, "end": v(9.93, -12.53) * mm});
            skLineSegment(sketch, "E2403", {"start": v(9.93, -12.53) * mm, "end": v(9.78, -12.55) * mm});
            skLineSegment(sketch, "E2404", {"start": v(9.78, -12.55) * mm, "end": v(9.62, -12.56) * mm});
            skLineSegment(sketch, "E2405", {"start": v(9.62, -12.56) * mm, "end": v(9.47, -12.56) * mm});
            skLineSegment(sketch, "E2406", {"start": v(9.47, -12.56) * mm, "end": v(9.31, -12.56) * mm});
            skLineSegment(sketch, "E2407", {"start": v(9.31, -12.56) * mm, "end": v(9.16, -12.55) * mm});
            skLineSegment(sketch, "E2408", {"start": v(9.16, -12.55) * mm, "end": v(8.86, -12.5) * mm});
            skLineSegment(sketch, "E2409", {"start": v(8.86, -12.5) * mm, "end": v(8.58, -12.43) * mm});
            skLineSegment(sketch, "E2410", {"start": v(8.58, -12.43) * mm, "end": v(8.3, -12.33) * mm});
            skLineSegment(sketch, "E2411", {"start": v(8.3, -12.33) * mm, "end": v(8.04, -12.2) * mm});
            skLineSegment(sketch, "E2412", {"start": v(8.04, -12.2) * mm, "end": v(7.8, -12.05) * mm});
            skLineSegment(sketch, "E2413", {"start": v(7.8, -12.05) * mm, "end": v(7.56, -11.88) * mm});
            skLineSegment(sketch, "E2414", {"start": v(7.56, -11.88) * mm, "end": v(7.35, -11.69) * mm});
            skLineSegment(sketch, "E2415", {"start": v(7.35, -11.69) * mm, "end": v(7.15, -11.47) * mm});
            skLineSegment(sketch, "E2416", {"start": v(7.15, -11.47) * mm, "end": v(6.98, -11.24) * mm});
            skLineSegment(sketch, "E2417", {"start": v(6.98, -11.24) * mm, "end": v(6.83, -11) * mm});
            skLineSegment(sketch, "E2418", {"start": v(6.83, -11) * mm, "end": v(6.7, -10.73) * mm});
            skLineSegment(sketch, "E2419", {"start": v(6.7, -10.73) * mm, "end": v(6.6, -10.46) * mm});
            skLineSegment(sketch, "E2420", {"start": v(6.6, -10.46) * mm, "end": v(6.53, -10.17) * mm});
            skLineSegment(sketch, "E2421", {"start": v(6.53, -10.17) * mm, "end": v(6.5, -10.02) * mm});
            skLineSegment(sketch, "E2422", {"start": v(6.5, -10.02) * mm, "end": v(6.48, -9.87) * mm});
            skLineSegment(sketch, "E2423", {"start": v(6.48, -9.87) * mm, "end": v(6.47, -9.72) * mm});
            skLineSegment(sketch, "E2424", {"start": v(6.47, -9.72) * mm, "end": v(6.47, -9.56) * mm});
            skLineSegment(sketch, "E2425", {"start": v(6.47, -9.56) * mm, "end": v(6.48, -9.32) * mm});
            skLineSegment(sketch, "E2426", {"start": v(6.48, -9.32) * mm, "end": v(6.5, -9.08) * mm});
            skLineSegment(sketch, "E2427", {"start": v(6.5, -9.08) * mm, "end": v(6.56, -8.84) * mm});
            skLineSegment(sketch, "E2428", {"start": v(6.56, -8.84) * mm, "end": v(6.62, -8.62) * mm});
            skLineSegment(sketch, "E2429", {"start": v(6.62, -8.62) * mm, "end": v(6.24, -8.8) * mm});
            skLineSegment(sketch, "E2430", {"start": v(6.24, -8.8) * mm, "end": v(5.86, -8.97) * mm});
            skLineSegment(sketch, "E2431", {"start": v(5.86, -8.97) * mm, "end": v(5.48, -9.12) * mm});
            skLineSegment(sketch, "E2432", {"start": v(5.48, -9.12) * mm, "end": v(5.1, -9.26) * mm});
            skLineSegment(sketch, "E2433", {"start": v(5.1, -9.26) * mm, "end": v(4.7, -9.37) * mm});
            skLineSegment(sketch, "E2434", {"start": v(4.7, -9.37) * mm, "end": v(4.28, -9.47) * mm});
            skLineSegment(sketch, "E2435", {"start": v(4.28, -9.47) * mm, "end": v(3.86, -9.55) * mm});
            skLineSegment(sketch, "E2436", {"start": v(3.86, -9.55) * mm, "end": v(3.43, -9.6) * mm});
            skLineSegment(sketch, "E2437", {"start": v(3.43, -9.6) * mm, "end": v(3.05, -9.64) * mm});
            skLineSegment(sketch, "E2438", {"start": v(3.05, -9.64) * mm, "end": v(2.67, -9.66) * mm});
            skLineSegment(sketch, "E2439", {"start": v(2.67, -9.66) * mm, "end": v(2.3, -9.66) * mm});
            skLineSegment(sketch, "E2440", {"start": v(2.3, -9.66) * mm, "end": v(1.92, -9.65) * mm});
            skLineSegment(sketch, "E2441", {"start": v(1.92, -9.65) * mm, "end": v(1.54, -9.63) * mm});
            skLineSegment(sketch, "E2442", {"start": v(1.54, -9.63) * mm, "end": v(1.16, -9.6) * mm});
            skLineSegment(sketch, "E2443", {"start": v(1.16, -9.6) * mm, "end": v(0.78, -9.56) * mm});
            skLineSegment(sketch, "E2444", {"start": v(0.78, -9.56) * mm, "end": v(0.4, -9.5) * mm});
            skLineSegment(sketch, "E2445", {"start": v(0.4, -9.5) * mm, "end": v(0.02, -9.44) * mm});
            skLineSegment(sketch, "E2446", {"start": v(0.02, -9.44) * mm, "end": v(-0.36, -9.37) * mm});
            skLineSegment(sketch, "E2447", {"start": v(-0.36, -9.37) * mm, "end": v(-1.1, -9.2) * mm});
            skLineSegment(sketch, "E2448", {"start": v(-1.1, -9.2) * mm, "end": v(-1.84, -9) * mm});
            skLineSegment(sketch, "E2449", {"start": v(-1.84, -9) * mm, "end": v(-2.56, -8.8) * mm});
            skLineSegment(sketch, "E2450", {"start": v(-2.56, -8.8) * mm, "end": v(-3.11, -8.6) * mm});
            skLineSegment(sketch, "E2451", {"start": v(-3.11, -8.6) * mm, "end": v(-3.66, -8.4) * mm});
            skLineSegment(sketch, "E2452", {"start": v(-3.66, -8.4) * mm, "end": v(-4.2, -8.17) * mm});
            skLineSegment(sketch, "E2453", {"start": v(-4.2, -8.17) * mm, "end": v(-4.72, -7.93) * mm});
            skLineSegment(sketch, "E2454", {"start": v(-4.72, -7.93) * mm, "end": v(-5.77, -7.45) * mm});
            skLineSegment(sketch, "E2455", {"start": v(-5.77, -7.45) * mm, "end": v(-6.3, -7.21) * mm});
            skLineSegment(sketch, "E2456", {"start": v(-6.3, -7.21) * mm, "end": v(-6.83, -6.98) * mm});
            skLineSegment(sketch, "E2457", {"start": v(-6.83, -6.98) * mm, "end": v(-6.91, -6.95) * mm});
            skLineSegment(sketch, "E2458", {"start": v(-6.91, -6.95) * mm, "end": v(-7.88, -6.43) * mm});
            skLineSegment(sketch, "E2459", {"start": v(-14.85, -19.62) * mm, "end": v(-14.65, -19.83) * mm});
            skLineSegment(sketch, "E2460", {"start": v(-14.65, -19.83) * mm, "end": v(-14.46, -20.07) * mm});
            skLineSegment(sketch, "E2461", {"start": v(-14.46, -20.07) * mm, "end": v(-14.3, -20.32) * mm});
            skLineSegment(sketch, "E2462", {"start": v(-14.3, -20.32) * mm, "end": v(-14.23, -20.45) * mm});
            skLineSegment(sketch, "E2463", {"start": v(-14.23, -20.45) * mm, "end": v(-14.17, -20.59) * mm});
            skLineSegment(sketch, "E2464", {"start": v(-14.17, -20.59) * mm, "end": v(-14.11, -20.73) * mm});
            skLineSegment(sketch, "E2465", {"start": v(-14.11, -20.73) * mm, "end": v(-14.06, -20.87) * mm});
            skLineSegment(sketch, "E2466", {"start": v(-14.06, -20.87) * mm, "end": v(-14.02, -21.02) * mm});
            skLineSegment(sketch, "E2467", {"start": v(-14.02, -21.02) * mm, "end": v(-13.98, -21.17) * mm});
            skLineSegment(sketch, "E2468", {"start": v(-13.98, -21.17) * mm, "end": v(-13.95, -21.32) * mm});
            skLineSegment(sketch, "E2469", {"start": v(-13.95, -21.32) * mm, "end": v(-13.93, -21.48) * mm});
            skLineSegment(sketch, "E2470", {"start": v(-13.93, -21.48) * mm, "end": v(-13.92, -21.64) * mm});
            skLineSegment(sketch, "E2471", {"start": v(-13.92, -21.64) * mm, "end": v(-13.92, -21.8) * mm});
            skLineSegment(sketch, "E2472", {"start": v(-13.92, -21.8) * mm, "end": v(-13.92, -21.95) * mm});
            skLineSegment(sketch, "E2473", {"start": v(-13.92, -21.95) * mm, "end": v(-13.93, -22.1) * mm});
            skLineSegment(sketch, "E2474", {"start": v(-13.93, -22.1) * mm, "end": v(-13.98, -22.4) * mm});
            skLineSegment(sketch, "E2475", {"start": v(-13.98, -22.4) * mm, "end": v(-14.05, -22.69) * mm});
            skLineSegment(sketch, "E2476", {"start": v(-14.05, -22.69) * mm, "end": v(-14.15, -22.96) * mm});
            skLineSegment(sketch, "E2477", {"start": v(-14.15, -22.96) * mm, "end": v(-14.28, -23.23) * mm});
            skLineSegment(sketch, "E2478", {"start": v(-14.28, -23.23) * mm, "end": v(-14.43, -23.47) * mm});
            skLineSegment(sketch, "E2479", {"start": v(-14.43, -23.47) * mm, "end": v(-14.6, -23.7) * mm});
            skLineSegment(sketch, "E2480", {"start": v(-14.6, -23.7) * mm, "end": v(-14.8, -23.92) * mm});
            skLineSegment(sketch, "E2481", {"start": v(-14.8, -23.92) * mm, "end": v(-15, -24.11) * mm});
            skLineSegment(sketch, "E2482", {"start": v(-15, -24.11) * mm, "end": v(-15.24, -24.28) * mm});
            skLineSegment(sketch, "E2483", {"start": v(-15.24, -24.28) * mm, "end": v(-15.49, -24.43) * mm});
            skLineSegment(sketch, "E2484", {"start": v(-15.49, -24.43) * mm, "end": v(-15.75, -24.56) * mm});
            skLineSegment(sketch, "E2485", {"start": v(-15.75, -24.56) * mm, "end": v(-16.02, -24.66) * mm});
            skLineSegment(sketch, "E2486", {"start": v(-16.02, -24.66) * mm, "end": v(-16.31, -24.73) * mm});
            skLineSegment(sketch, "E2487", {"start": v(-16.31, -24.73) * mm, "end": v(-16.46, -24.76) * mm});
            skLineSegment(sketch, "E2488", {"start": v(-16.46, -24.76) * mm, "end": v(-16.6, -24.78) * mm});
            skLineSegment(sketch, "E2489", {"start": v(-16.6, -24.78) * mm, "end": v(-16.76, -24.8) * mm});
            skLineSegment(sketch, "E2490", {"start": v(-16.76, -24.8) * mm, "end": v(-16.92, -24.8) * mm});
            skLineSegment(sketch, "E2491", {"start": v(-16.92, -24.8) * mm, "end": v(-17.07, -24.8) * mm});
            skLineSegment(sketch, "E2492", {"start": v(-17.07, -24.8) * mm, "end": v(-17.22, -24.78) * mm});
            skLineSegment(sketch, "E2493", {"start": v(-17.22, -24.78) * mm, "end": v(-17.52, -24.73) * mm});
            skLineSegment(sketch, "E2494", {"start": v(-17.52, -24.73) * mm, "end": v(-17.8, -24.66) * mm});
            skLineSegment(sketch, "E2495", {"start": v(-17.8, -24.66) * mm, "end": v(-18.08, -24.56) * mm});
            skLineSegment(sketch, "E2496", {"start": v(-18.08, -24.56) * mm, "end": v(-18.35, -24.43) * mm});
            skLineSegment(sketch, "E2497", {"start": v(-18.35, -24.43) * mm, "end": v(-18.6, -24.28) * mm});
            skLineSegment(sketch, "E2498", {"start": v(-18.6, -24.28) * mm, "end": v(-18.82, -24.11) * mm});
            skLineSegment(sketch, "E2499", {"start": v(-18.82, -24.11) * mm, "end": v(-19.04, -23.92) * mm});
            skLineSegment(sketch, "E2500", {"start": v(-19.04, -23.92) * mm, "end": v(-19.23, -23.7) * mm});
            skLineSegment(sketch, "E2501", {"start": v(-19.23, -23.7) * mm, "end": v(-19.4, -23.47) * mm});
            skLineSegment(sketch, "E2502", {"start": v(-19.4, -23.47) * mm, "end": v(-19.55, -23.23) * mm});
            skLineSegment(sketch, "E2503", {"start": v(-19.55, -23.23) * mm, "end": v(-19.68, -22.96) * mm});
            skLineSegment(sketch, "E2504", {"start": v(-19.68, -22.96) * mm, "end": v(-19.78, -22.69) * mm});
            skLineSegment(sketch, "E2505", {"start": v(-19.78, -22.69) * mm, "end": v(-19.85, -22.4) * mm});
            skLineSegment(sketch, "E2506", {"start": v(-19.85, -22.4) * mm, "end": v(-19.88, -22.25) * mm});
            skLineSegment(sketch, "E2507", {"start": v(-19.88, -22.25) * mm, "end": v(-19.9, -22.1) * mm});
            skLineSegment(sketch, "E2508", {"start": v(-19.9, -22.1) * mm, "end": v(-19.91, -21.95) * mm});
            skLineSegment(sketch, "E2509", {"start": v(-19.91, -21.95) * mm, "end": v(-19.92, -21.8) * mm});
            skLineSegment(sketch, "E2510", {"start": v(-19.92, -21.8) * mm, "end": v(-19.9, -21.52) * mm});
            skLineSegment(sketch, "E2511", {"start": v(-19.9, -21.52) * mm, "end": v(-19.87, -21.25) * mm});
            skLineSegment(sketch, "E2512", {"start": v(-19.87, -21.25) * mm, "end": v(-19.8, -21) * mm});
            skLineSegment(sketch, "E2513", {"start": v(-19.8, -21) * mm, "end": v(-19.73, -20.74) * mm});
            skLineSegment(sketch, "E2514", {"start": v(-19.73, -20.74) * mm, "end": v(-19.62, -20.5) * mm});
            skLineSegment(sketch, "E2515", {"start": v(-19.62, -20.5) * mm, "end": v(-19.5, -20.28) * mm});
            skLineSegment(sketch, "E2516", {"start": v(-19.5, -20.28) * mm, "end": v(-19.36, -20.06) * mm});
            skLineSegment(sketch, "E2517", {"start": v(-19.36, -20.06) * mm, "end": v(-19.2, -19.86) * mm});
            skLineSegment(sketch, "E2518", {"start": v(-19.2, -19.86) * mm, "end": v(-19.53, -19.93) * mm});
            skLineSegment(sketch, "E2519", {"start": v(-19.53, -19.93) * mm, "end": v(-19.57, -19.93) * mm});
            skLineSegment(sketch, "E2520", {"start": v(-19.57, -19.93) * mm, "end": v(-19.95, -20) * mm});
            skLineSegment(sketch, "E2521", {"start": v(-19.95, -20) * mm, "end": v(-20.33, -20.1) * mm});
            skLineSegment(sketch, "E2522", {"start": v(-20.33, -20.1) * mm, "end": v(-20.7, -20.2) * mm});
            skLineSegment(sketch, "E2523", {"start": v(-20.7, -20.2) * mm, "end": v(-20.87, -20.27) * mm});
            skLineSegment(sketch, "E2524", {"start": v(-20.87, -20.27) * mm, "end": v(-21.04, -20.34) * mm});
            skLineSegment(sketch, "E2525", {"start": v(-21.04, -20.34) * mm, "end": v(-21.21, -20.42) * mm});
            skLineSegment(sketch, "E2526", {"start": v(-21.21, -20.42) * mm, "end": v(-21.38, -20.51) * mm});
            skLineSegment(sketch, "E2527", {"start": v(-21.38, -20.51) * mm, "end": v(-21.54, -20.6) * mm});
            skLineSegment(sketch, "E2528", {"start": v(-21.54, -20.6) * mm, "end": v(-21.7, -20.7) * mm});
            skLineSegment(sketch, "E2529", {"start": v(-21.7, -20.7) * mm, "end": v(-21.85, -20.82) * mm});
            skLineSegment(sketch, "E2530", {"start": v(-21.85, -20.82) * mm, "end": v(-22, -20.94) * mm});
            skLineSegment(sketch, "E2531", {"start": v(-22, -20.94) * mm, "end": v(-22.15, -21.07) * mm});
            skLineSegment(sketch, "E2532", {"start": v(-22.15, -21.07) * mm, "end": v(-22.29, -21.22) * mm});
            skLineSegment(sketch, "E2533", {"start": v(-22.29, -21.22) * mm, "end": v(-22.45, -21.4) * mm});
            skLineSegment(sketch, "E2534", {"start": v(-22.45, -21.4) * mm, "end": v(-22.6, -21.59) * mm});
            skLineSegment(sketch, "E2535", {"start": v(-22.6, -21.59) * mm, "end": v(-22.75, -21.79) * mm});
            skLineSegment(sketch, "E2536", {"start": v(-22.75, -21.79) * mm, "end": v(-22.9, -22) * mm});
            skLineSegment(sketch, "E2537", {"start": v(-22.9, -22) * mm, "end": v(-23.16, -22.41) * mm});
            skLineSegment(sketch, "E2538", {"start": v(-23.16, -22.41) * mm, "end": v(-23.4, -22.84) * mm});
            skLineSegment(sketch, "E2539", {"start": v(-23.4, -22.84) * mm, "end": v(-24.07, -24.06) * mm});
            skLineSegment(sketch, "E2540", {"start": v(-24.07, -24.06) * mm, "end": v(-24.4, -24.68) * mm});
            skLineSegment(sketch, "E2541", {"start": v(-24.4, -24.68) * mm, "end": v(-24.75, -25.28) * mm});
            skLineSegment(sketch, "E2542", {"start": v(-24.75, -25.28) * mm, "end": v(-25.03, -25.75) * mm});
            skLineSegment(sketch, "E2543", {"start": v(-25.03, -25.75) * mm, "end": v(-25.31, -26.2) * mm});
            skLineSegment(sketch, "E2544", {"start": v(-25.31, -26.2) * mm, "end": v(-25.6, -26.64) * mm});
            skLineSegment(sketch, "E2545", {"start": v(-25.6, -26.64) * mm, "end": v(-25.91, -27.08) * mm});
            skLineSegment(sketch, "E2546", {"start": v(-25.91, -27.08) * mm, "end": v(-26.23, -27.5) * mm});
            skLineSegment(sketch, "E2547", {"start": v(-26.23, -27.5) * mm, "end": v(-26.55, -27.9) * mm});
            skLineSegment(sketch, "E2548", {"start": v(-26.55, -27.9) * mm, "end": v(-26.88, -28.3) * mm});
            skLineSegment(sketch, "E2549", {"start": v(-26.88, -28.3) * mm, "end": v(-27.21, -28.7) * mm});
            skLineSegment(sketch, "E2550", {"start": v(-27.21, -28.7) * mm, "end": v(-27.56, -29.08) * mm});
            skLineSegment(sketch, "E2551", {"start": v(-27.56, -29.08) * mm, "end": v(-27.92, -29.45) * mm});
            skLineSegment(sketch, "E2552", {"start": v(-27.92, -29.45) * mm, "end": v(-28.3, -29.82) * mm});
            skLineSegment(sketch, "E2553", {"start": v(-28.3, -29.82) * mm, "end": v(-28.67, -30.18) * mm});
            skLineSegment(sketch, "E2554", {"start": v(-28.67, -30.18) * mm, "end": v(-29.07, -30.53) * mm});
            skLineSegment(sketch, "E2555", {"start": v(-29.07, -30.53) * mm, "end": v(-29.47, -30.88) * mm});
            skLineSegment(sketch, "E2556", {"start": v(-29.47, -30.88) * mm, "end": v(-29.89, -31.22) * mm});
            skLineSegment(sketch, "E2557", {"start": v(-29.89, -31.22) * mm, "end": v(-30.32, -31.56) * mm});
            skLineSegment(sketch, "E2558", {"start": v(-30.32, -31.56) * mm, "end": v(-30.37, -31.6) * mm});
            skLineSegment(sketch, "E2559", {"start": v(-30.37, -31.6) * mm, "end": v(-30.2, -31.6) * mm});
            skLineSegment(sketch, "E2560", {"start": v(-30.2, -31.6) * mm, "end": v(-30, -31.59) * mm});
            skLineSegment(sketch, "E2561", {"start": v(-30, -31.59) * mm, "end": v(-29.82, -31.56) * mm});
            skLineSegment(sketch, "E2562", {"start": v(-29.82, -31.56) * mm, "end": v(-29.62, -31.53) * mm});
            skLineSegment(sketch, "E2563", {"start": v(-29.62, -31.53) * mm, "end": v(-29.22, -31.45) * mm});
            skLineSegment(sketch, "E2564", {"start": v(-29.22, -31.45) * mm, "end": v(-28.8, -31.34) * mm});
            skLineSegment(sketch, "E2565", {"start": v(-28.8, -31.34) * mm, "end": v(-28.39, -31.2) * mm});
            skLineSegment(sketch, "E2566", {"start": v(-28.39, -31.2) * mm, "end": v(-27.96, -31.04) * mm});
            skLineSegment(sketch, "E2567", {"start": v(-27.96, -31.04) * mm, "end": v(-27.54, -30.87) * mm});
            skLineSegment(sketch, "E2568", {"start": v(-27.54, -30.87) * mm, "end": v(-27.12, -30.69) * mm});
            skLineSegment(sketch, "E2569", {"start": v(-27.12, -30.69) * mm, "end": v(-26.3, -30.3) * mm});
            skLineSegment(sketch, "E2570", {"start": v(-26.3, -30.3) * mm, "end": v(-25.54, -29.93) * mm});
            skLineSegment(sketch, "E2571", {"start": v(-25.54, -29.93) * mm, "end": v(-24.88, -29.59) * mm});
            skLineSegment(sketch, "E2572", {"start": v(-24.88, -29.59) * mm, "end": v(-24.33, -29.33) * mm});
            skLineSegment(sketch, "E2573", {"start": v(-24.33, -29.33) * mm, "end": v(-23.75, -29.07) * mm});
            skLineSegment(sketch, "E2574", {"start": v(-23.75, -29.07) * mm, "end": v(-23.18, -28.85) * mm});
            skLineSegment(sketch, "E2575", {"start": v(-23.18, -28.85) * mm, "end": v(-22.6, -28.65) * mm});
            skLineSegment(sketch, "E2576", {"start": v(-22.6, -28.65) * mm, "end": v(-22.03, -28.49) * mm});
            skLineSegment(sketch, "E2577", {"start": v(-22.03, -28.49) * mm, "end": v(-21.45, -28.35) * mm});
            skLineSegment(sketch, "E2578", {"start": v(-21.45, -28.35) * mm, "end": v(-21.17, -28.3) * mm});
            skLineSegment(sketch, "E2579", {"start": v(-21.17, -28.3) * mm, "end": v(-20.88, -28.25) * mm});
            skLineSegment(sketch, "E2580", {"start": v(-20.88, -28.25) * mm, "end": v(-20.6, -28.2) * mm});
            skLineSegment(sketch, "E2581", {"start": v(-20.6, -28.2) * mm, "end": v(-20.31, -28.18) * mm});
            skLineSegment(sketch, "E2582", {"start": v(-20.31, -28.18) * mm, "end": v(-20.03, -28.15) * mm});
            skLineSegment(sketch, "E2583", {"start": v(-20.03, -28.15) * mm, "end": v(-19.74, -28.14) * mm});
            skLineSegment(sketch, "E2584", {"start": v(-19.74, -28.14) * mm, "end": v(-19.46, -28.14) * mm});
            skLineSegment(sketch, "E2585", {"start": v(-19.46, -28.14) * mm, "end": v(-19.17, -28.14) * mm});
            skLineSegment(sketch, "E2586", {"start": v(-19.17, -28.14) * mm, "end": v(-18.89, -28.15) * mm});
            skLineSegment(sketch, "E2587", {"start": v(-18.89, -28.15) * mm, "end": v(-18.6, -28.18) * mm});
            skLineSegment(sketch, "E2588", {"start": v(-18.6, -28.18) * mm, "end": v(-18.32, -28.21) * mm});
            skLineSegment(sketch, "E2589", {"start": v(-18.32, -28.21) * mm, "end": v(-18.03, -28.25) * mm});
            skLineSegment(sketch, "E2590", {"start": v(-18.03, -28.25) * mm, "end": v(-17.75, -28.3) * mm});
            skLineSegment(sketch, "E2591", {"start": v(-17.75, -28.3) * mm, "end": v(-17.47, -28.37) * mm});
            skLineSegment(sketch, "E2592", {"start": v(-17.47, -28.37) * mm, "end": v(-17.18, -28.44) * mm});
            skLineSegment(sketch, "E2593", {"start": v(-17.18, -28.44) * mm, "end": v(-16.9, -28.53) * mm});
            skLineSegment(sketch, "E2594", {"start": v(-16.9, -28.53) * mm, "end": v(-16.61, -28.62) * mm});
            skLineSegment(sketch, "E2595", {"start": v(-16.61, -28.62) * mm, "end": v(-16.33, -28.73) * mm});
            skLineSegment(sketch, "E2596", {"start": v(-16.33, -28.73) * mm, "end": v(-16.04, -28.85) * mm});
            skLineSegment(sketch, "E2597", {"start": v(-16.04, -28.85) * mm, "end": v(-15.75, -28.97) * mm});
            skLineSegment(sketch, "E2598", {"start": v(-15.75, -28.97) * mm, "end": v(-15.47, -29.11) * mm});
            skLineSegment(sketch, "E2599", {"start": v(-15.47, -29.11) * mm, "end": v(-15.18, -29.26) * mm});
            skLineSegment(sketch, "E2600", {"start": v(-15.18, -29.26) * mm, "end": v(-14.82, -29.47) * mm});
            skLineSegment(sketch, "E2601", {"start": v(-14.82, -29.47) * mm, "end": v(-14.47, -29.69) * mm});
            skLineSegment(sketch, "E2602", {"start": v(-14.47, -29.69) * mm, "end": v(-14.12, -29.91) * mm});
            skLineSegment(sketch, "E2603", {"start": v(-14.12, -29.91) * mm, "end": v(-13.78, -30.15) * mm});
            skLineSegment(sketch, "E2604", {"start": v(-13.78, -30.15) * mm, "end": v(-13.11, -30.63) * mm});
            skLineSegment(sketch, "E2605", {"start": v(-13.11, -30.63) * mm, "end": v(-12.44, -31.12) * mm});
            skLineSegment(sketch, "E2606", {"start": v(-12.44, -31.12) * mm, "end": v(-11.97, -31.46) * mm});
            skLineSegment(sketch, "E2607", {"start": v(-11.97, -31.46) * mm, "end": v(-11.73, -31.63) * mm});
            skLineSegment(sketch, "E2608", {"start": v(-11.73, -31.63) * mm, "end": v(-11.47, -31.8) * mm});
            skLineSegment(sketch, "E2609", {"start": v(-11.47, -31.8) * mm, "end": v(-11.22, -31.94) * mm});
            skLineSegment(sketch, "E2610", {"start": v(-11.22, -31.94) * mm, "end": v(-10.95, -32.08) * mm});
            skLineSegment(sketch, "E2611", {"start": v(-10.95, -32.08) * mm, "end": v(-10.69, -32.2) * mm});
            skLineSegment(sketch, "E2612", {"start": v(-10.69, -32.2) * mm, "end": v(-10.42, -32.3) * mm});
            skLineSegment(sketch, "E2613", {"start": v(-10.42, -32.3) * mm, "end": v(-10.23, -32.35) * mm});
            skLineSegment(sketch, "E2614", {"start": v(-10.23, -32.35) * mm, "end": v(-10.04, -32.4) * mm});
            skLineSegment(sketch, "E2615", {"start": v(-10.04, -32.4) * mm, "end": v(-9.85, -32.42) * mm});
            skLineSegment(sketch, "E2616", {"start": v(-9.85, -32.42) * mm, "end": v(-9.67, -32.43) * mm});
            skLineSegment(sketch, "E2617", {"start": v(-9.67, -32.43) * mm, "end": v(-9.48, -32.43) * mm});
            skLineSegment(sketch, "E2618", {"start": v(-9.48, -32.43) * mm, "end": v(-9.3, -32.41) * mm});
            skLineSegment(sketch, "E2619", {"start": v(-9.3, -32.41) * mm, "end": v(-9.12, -32.39) * mm});
            skLineSegment(sketch, "E2620", {"start": v(-9.12, -32.39) * mm, "end": v(-8.94, -32.35) * mm});
            skLineSegment(sketch, "E2621", {"start": v(-8.94, -32.35) * mm, "end": v(-8.76, -32.3) * mm});
            skLineSegment(sketch, "E2622", {"start": v(-8.76, -32.3) * mm, "end": v(-8.59, -32.25) * mm});
            skLineSegment(sketch, "E2623", {"start": v(-8.59, -32.25) * mm, "end": v(-8.24, -32.12) * mm});
            skLineSegment(sketch, "E2624", {"start": v(-8.24, -32.12) * mm, "end": v(-7.9, -31.96) * mm});
            skLineSegment(sketch, "E2625", {"start": v(-7.9, -31.96) * mm, "end": v(-7.56, -31.77) * mm});
            skLineSegment(sketch, "E2626", {"start": v(-7.56, -31.77) * mm, "end": v(-6.7, -31.27) * mm});
            skLineSegment(sketch, "E2627", {"start": v(-6.7, -31.27) * mm, "end": v(-5.79, -30.76) * mm});
            skLineSegment(sketch, "E2628", {"start": v(-5.79, -30.76) * mm, "end": v(-5.32, -30.51) * mm});
            skLineSegment(sketch, "E2629", {"start": v(-5.32, -30.51) * mm, "end": v(-4.85, -30.27) * mm});
            skLineSegment(sketch, "E2630", {"start": v(-4.85, -30.27) * mm, "end": v(-4.37, -30.03) * mm});
            skLineSegment(sketch, "E2631", {"start": v(-4.37, -30.03) * mm, "end": v(-3.88, -29.81) * mm});
            skLineSegment(sketch, "E2632", {"start": v(-3.88, -29.81) * mm, "end": v(-3.39, -29.6) * mm});
            skLineSegment(sketch, "E2633", {"start": v(-3.39, -29.6) * mm, "end": v(-2.9, -29.42) * mm});
            skLineSegment(sketch, "E2634", {"start": v(-2.9, -29.42) * mm, "end": v(-2.4, -29.25) * mm});
            skLineSegment(sketch, "E2635", {"start": v(-2.4, -29.25) * mm, "end": v(-1.9, -29.1) * mm});
            skLineSegment(sketch, "E2636", {"start": v(-1.9, -29.1) * mm, "end": v(-1.4, -28.99) * mm});
            skLineSegment(sketch, "E2637", {"start": v(-1.4, -28.99) * mm, "end": v(-1.14, -28.94) * mm});
            skLineSegment(sketch, "E2638", {"start": v(-1.14, -28.94) * mm, "end": v(-0.89, -28.9) * mm});
            skLineSegment(sketch, "E2639", {"start": v(-0.89, -28.9) * mm, "end": v(-0.63, -28.87) * mm});
            skLineSegment(sketch, "E2640", {"start": v(-0.63, -28.87) * mm, "end": v(-0.38, -28.84) * mm});
            skLineSegment(sketch, "E2641", {"start": v(-0.38, -28.84) * mm, "end": v(-0.13, -28.83) * mm});
            skLineSegment(sketch, "E2642", {"start": v(-0.13, -28.83) * mm, "end": v(0.12, -28.82) * mm});
            skLineSegment(sketch, "E2643", {"start": v(0.12, -28.82) * mm, "end": v(0.42, -28.83) * mm});
            skLineSegment(sketch, "E2644", {"start": v(0.42, -28.83) * mm, "end": v(0.71, -28.84) * mm});
            skLineSegment(sketch, "E2645", {"start": v(0.71, -28.84) * mm, "end": v(1, -28.87) * mm});
            skLineSegment(sketch, "E2646", {"start": v(1, -28.87) * mm, "end": v(1.3, -28.9) * mm});
            skLineSegment(sketch, "E2647", {"start": v(1.3, -28.9) * mm, "end": v(1.58, -28.95) * mm});
            skLineSegment(sketch, "E2648", {"start": v(1.58, -28.95) * mm, "end": v(1.87, -29.01) * mm});
            skLineSegment(sketch, "E2649", {"start": v(1.87, -29.01) * mm, "end": v(2.15, -29.08) * mm});
            skLineSegment(sketch, "E2650", {"start": v(2.15, -29.08) * mm, "end": v(2.44, -29.15) * mm});
            skLineSegment(sketch, "E2651", {"start": v(2.44, -29.15) * mm, "end": v(3, -29.32) * mm});
            skLineSegment(sketch, "E2652", {"start": v(3, -29.32) * mm, "end": v(3.54, -29.52) * mm});
            skLineSegment(sketch, "E2653", {"start": v(3.54, -29.52) * mm, "end": v(4.09, -29.74) * mm});
            skLineSegment(sketch, "E2654", {"start": v(4.09, -29.74) * mm, "end": v(4.63, -29.98) * mm});
            skLineSegment(sketch, "E2655", {"start": v(4.63, -29.98) * mm, "end": v(5.38, -30.32) * mm});
            skLineSegment(sketch, "E2656", {"start": v(5.38, -30.32) * mm, "end": v(6.12, -30.7) * mm});
            skLineSegment(sketch, "E2657", {"start": v(6.12, -30.7) * mm, "end": v(6.86, -31.08) * mm});
            skLineSegment(sketch, "E2658", {"start": v(6.86, -31.08) * mm, "end": v(7.6, -31.47) * mm});
            skLineSegment(sketch, "E2659", {"start": v(7.6, -31.47) * mm, "end": v(9.07, -32.27) * mm});
            skLineSegment(sketch, "E2660", {"start": v(9.07, -32.27) * mm, "end": v(10.52, -33.07) * mm});
            skLineSegment(sketch, "E2661", {"start": v(10.52, -33.07) * mm, "end": v(10.95, -33.3) * mm});
            skLineSegment(sketch, "E2662", {"start": v(10.95, -33.3) * mm, "end": v(11.16, -33.4) * mm});
            skLineSegment(sketch, "E2663", {"start": v(11.16, -33.4) * mm, "end": v(11.38, -33.5) * mm});
            skLineSegment(sketch, "E2664", {"start": v(11.38, -33.5) * mm, "end": v(11.6, -33.58) * mm});
            skLineSegment(sketch, "E2665", {"start": v(11.6, -33.58) * mm, "end": v(11.82, -33.65) * mm});
            skLineSegment(sketch, "E2666", {"start": v(11.82, -33.65) * mm, "end": v(12.04, -33.72) * mm});
            skLineSegment(sketch, "E2667", {"start": v(12.04, -33.72) * mm, "end": v(12.26, -33.77) * mm});
            skLineSegment(sketch, "E2668", {"start": v(12.26, -33.77) * mm, "end": v(12.49, -33.8) * mm});
            skLineSegment(sketch, "E2669", {"start": v(12.49, -33.8) * mm, "end": v(12.72, -33.83) * mm});
            skLineSegment(sketch, "E2670", {"start": v(12.72, -33.83) * mm, "end": v(12.94, -33.84) * mm});
            skLineSegment(sketch, "E2671", {"start": v(12.94, -33.84) * mm, "end": v(13.17, -33.83) * mm});
            skLineSegment(sketch, "E2672", {"start": v(13.17, -33.83) * mm, "end": v(13.4, -33.8) * mm});
            skLineSegment(sketch, "E2673", {"start": v(13.4, -33.8) * mm, "end": v(13.63, -33.76) * mm});
            skLineSegment(sketch, "E2674", {"start": v(13.63, -33.76) * mm, "end": v(13.86, -33.7) * mm});
            skLineSegment(sketch, "E2675", {"start": v(13.86, -33.7) * mm, "end": v(14.1, -33.6) * mm});
            skLineSegment(sketch, "E2676", {"start": v(14.1, -33.6) * mm, "end": v(14.34, -33.49) * mm});
            skLineSegment(sketch, "E2677", {"start": v(14.34, -33.49) * mm, "end": v(14.59, -33.35) * mm});
            skLineSegment(sketch, "E2678", {"start": v(14.59, -33.35) * mm, "end": v(14.83, -33.2) * mm});
            skLineSegment(sketch, "E2679", {"start": v(14.83, -33.2) * mm, "end": v(15.06, -33.05) * mm});
            skLineSegment(sketch, "E2680", {"start": v(15.06, -33.05) * mm, "end": v(15.52, -32.71) * mm});
            skLineSegment(sketch, "E2681", {"start": v(15.52, -32.71) * mm, "end": v(15.96, -32.37) * mm});
            skLineSegment(sketch, "E2682", {"start": v(15.96, -32.37) * mm, "end": v(16.57, -31.9) * mm});
            skLineSegment(sketch, "E2683", {"start": v(16.57, -31.9) * mm, "end": v(17.19, -31.43) * mm});
            skLineSegment(sketch, "E2684", {"start": v(17.19, -31.43) * mm, "end": v(17.5, -31.2) * mm});
            skLineSegment(sketch, "E2685", {"start": v(17.5, -31.2) * mm, "end": v(17.82, -31) * mm});
            skLineSegment(sketch, "E2686", {"start": v(17.82, -31) * mm, "end": v(18.15, -30.8) * mm});
            skLineSegment(sketch, "E2687", {"start": v(18.15, -30.8) * mm, "end": v(18.5, -30.6) * mm});
            skLineSegment(sketch, "E2688", {"start": v(18.5, -30.6) * mm, "end": v(18.76, -30.46) * mm});
            skLineSegment(sketch, "E2689", {"start": v(18.76, -30.46) * mm, "end": v(19.03, -30.33) * mm});
            skLineSegment(sketch, "E2690", {"start": v(19.03, -30.33) * mm, "end": v(19.3, -30.21) * mm});
            skLineSegment(sketch, "E2691", {"start": v(19.3, -30.21) * mm, "end": v(19.58, -30.1) * mm});
            skLineSegment(sketch, "E2692", {"start": v(19.58, -30.1) * mm, "end": v(19.85, -30) * mm});
            skLineSegment(sketch, "E2693", {"start": v(19.85, -30) * mm, "end": v(20.12, -29.92) * mm});
            skLineSegment(sketch, "E2694", {"start": v(20.12, -29.92) * mm, "end": v(20.4, -29.85) * mm});
            skLineSegment(sketch, "E2695", {"start": v(20.4, -29.85) * mm, "end": v(20.67, -29.78) * mm});
            skLineSegment(sketch, "E2696", {"start": v(20.67, -29.78) * mm, "end": v(20.94, -29.72) * mm});
            skLineSegment(sketch, "E2697", {"start": v(20.94, -29.72) * mm, "end": v(21.21, -29.68) * mm});
            skLineSegment(sketch, "E2698", {"start": v(21.21, -29.68) * mm, "end": v(21.49, -29.64) * mm});
            skLineSegment(sketch, "E2699", {"start": v(21.49, -29.64) * mm, "end": v(21.76, -29.61) * mm});
            skLineSegment(sketch, "E2700", {"start": v(21.76, -29.61) * mm, "end": v(22.03, -29.6) * mm});
            skLineSegment(sketch, "E2701", {"start": v(22.03, -29.6) * mm, "end": v(22.3, -29.58) * mm});
            skLineSegment(sketch, "E2702", {"start": v(22.3, -29.58) * mm, "end": v(22.58, -29.58) * mm});
            skLineSegment(sketch, "E2703", {"start": v(22.58, -29.58) * mm, "end": v(22.86, -29.59) * mm});
            skLineSegment(sketch, "E2704", {"start": v(22.86, -29.59) * mm, "end": v(23.13, -29.6) * mm});
            skLineSegment(sketch, "E2705", {"start": v(23.13, -29.6) * mm, "end": v(23.4, -29.62) * mm});
            skLineSegment(sketch, "E2706", {"start": v(23.4, -29.62) * mm, "end": v(23.96, -29.69) * mm});
            skLineSegment(sketch, "E2707", {"start": v(23.96, -29.69) * mm, "end": v(24.5, -29.79) * mm});
            skLineSegment(sketch, "E2708", {"start": v(24.5, -29.79) * mm, "end": v(25.06, -29.9) * mm});
            skLineSegment(sketch, "E2709", {"start": v(25.06, -29.9) * mm, "end": v(25.6, -30.06) * mm});
            skLineSegment(sketch, "E2710", {"start": v(25.6, -30.06) * mm, "end": v(26.16, -30.23) * mm});
            skLineSegment(sketch, "E2711", {"start": v(26.16, -30.23) * mm, "end": v(26.7, -30.43) * mm});
            skLineSegment(sketch, "E2712", {"start": v(26.7, -30.43) * mm, "end": v(27.26, -30.64) * mm});
            skLineSegment(sketch, "E2713", {"start": v(27.26, -30.64) * mm, "end": v(27.68, -30.82) * mm});
            skLineSegment(sketch, "E2714", {"start": v(27.68, -30.82) * mm, "end": v(28.1, -31.01) * mm});
            skLineSegment(sketch, "E2715", {"start": v(28.1, -31.01) * mm, "end": v(28.9, -31.41) * mm});
            skLineSegment(sketch, "E2716", {"start": v(28.9, -31.41) * mm, "end": v(29.72, -31.82) * mm});
            skLineSegment(sketch, "E2717", {"start": v(29.72, -31.82) * mm, "end": v(30.13, -32.03) * mm});
            skLineSegment(sketch, "E2718", {"start": v(30.13, -32.03) * mm, "end": v(30.54, -32.22) * mm});
            skLineSegment(sketch, "E2719", {"start": v(30.54, -32.22) * mm, "end": v(30.9, -32.38) * mm});
            skLineSegment(sketch, "E2720", {"start": v(30.9, -32.38) * mm, "end": v(31.26, -32.53) * mm});
            skLineSegment(sketch, "E2721", {"start": v(31.26, -32.53) * mm, "end": v(31.63, -32.67) * mm});
            skLineSegment(sketch, "E2722", {"start": v(31.63, -32.67) * mm, "end": v(32, -32.78) * mm});
            skLineSegment(sketch, "E2723", {"start": v(32, -32.78) * mm, "end": v(32.37, -32.88) * mm});
            skLineSegment(sketch, "E2724", {"start": v(32.37, -32.88) * mm, "end": v(32.75, -32.95) * mm});
            skLineSegment(sketch, "E2725", {"start": v(32.75, -32.95) * mm, "end": v(32.93, -32.98) * mm});
            skLineSegment(sketch, "E2726", {"start": v(32.93, -32.98) * mm, "end": v(33.12, -33) * mm});
            skLineSegment(sketch, "E2727", {"start": v(33.12, -33) * mm, "end": v(33.31, -33) * mm});
            skLineSegment(sketch, "E2728", {"start": v(33.31, -33) * mm, "end": v(33.5, -33) * mm});
            skLineSegment(sketch, "E2729", {"start": v(33.5, -33) * mm, "end": v(33.27, -32.75) * mm});
            skLineSegment(sketch, "E2730", {"start": v(33.27, -32.75) * mm, "end": v(33.03, -32.52) * mm});
            skLineSegment(sketch, "E2731", {"start": v(33.03, -32.52) * mm, "end": v(32.6, -32.13) * mm});
            skLineSegment(sketch, "E2732", {"start": v(32.6, -32.13) * mm, "end": v(31.85, -31.46) * mm});
            skLineSegment(sketch, "E2733", {"start": v(31.85, -31.46) * mm, "end": v(31.5, -31.13) * mm});
            skLineSegment(sketch, "E2734", {"start": v(31.5, -31.13) * mm, "end": v(31.15, -30.79) * mm});
            skLineSegment(sketch, "E2735", {"start": v(31.15, -30.79) * mm, "end": v(30.8, -30.44) * mm});
            skLineSegment(sketch, "E2736", {"start": v(30.8, -30.44) * mm, "end": v(30.47, -30.08) * mm});
            skLineSegment(sketch, "E2737", {"start": v(30.47, -30.08) * mm, "end": v(30.15, -29.7) * mm});
            skLineSegment(sketch, "E2738", {"start": v(30.15, -29.7) * mm, "end": v(29.84, -29.3) * mm});
            skLineSegment(sketch, "E2739", {"start": v(29.84, -29.3) * mm, "end": v(28.79, -27.92) * mm});
            skLineSegment(sketch, "E2740", {"start": v(28.79, -27.92) * mm, "end": v(28.27, -27.22) * mm});
            skLineSegment(sketch, "E2741", {"start": v(28.27, -27.22) * mm, "end": v(27.77, -26.51) * mm});
            skLineSegment(sketch, "E2742", {"start": v(27.77, -26.51) * mm, "end": v(27.47, -26.06) * mm});
            skLineSegment(sketch, "E2743", {"start": v(27.47, -26.06) * mm, "end": v(27.19, -25.6) * mm});
            skLineSegment(sketch, "E2744", {"start": v(27.19, -25.6) * mm, "end": v(26.91, -25.13) * mm});
            skLineSegment(sketch, "E2745", {"start": v(26.91, -25.13) * mm, "end": v(26.64, -24.66) * mm});
            skLineSegment(sketch, "E2746", {"start": v(26.64, -24.66) * mm, "end": v(26.13, -23.71) * mm});
            skLineSegment(sketch, "E2747", {"start": v(26.13, -23.71) * mm, "end": v(25.63, -22.75) * mm});
            skLineSegment(sketch, "E2748", {"start": v(25.63, -22.75) * mm, "end": v(25.3, -22.06) * mm});
            skLineSegment(sketch, "E2749", {"start": v(25.3, -22.06) * mm, "end": v(24.99, -21.36) * mm});
            skLineSegment(sketch, "E2750", {"start": v(24.99, -21.36) * mm, "end": v(24.82, -21) * mm});
            skLineSegment(sketch, "E2751", {"start": v(24.82, -21) * mm, "end": v(24.72, -20.82) * mm});
            skLineSegment(sketch, "E2752", {"start": v(24.72, -20.82) * mm, "end": v(24.6, -20.66) * mm});
            skLineSegment(sketch, "E2753", {"start": v(24.6, -20.66) * mm, "end": v(24.55, -20.59) * mm});
            skLineSegment(sketch, "E2754", {"start": v(24.55, -20.59) * mm, "end": v(24.48, -20.52) * mm});
            skLineSegment(sketch, "E2755", {"start": v(24.48, -20.52) * mm, "end": v(24.33, -20.4) * mm});
            skLineSegment(sketch, "E2756", {"start": v(24.33, -20.4) * mm, "end": v(24.16, -20.3) * mm});
            skLineSegment(sketch, "E2757", {"start": v(24.16, -20.3) * mm, "end": v(23.98, -20.22) * mm});
            skLineSegment(sketch, "E2758", {"start": v(23.98, -20.22) * mm, "end": v(23.8, -20.15) * mm});
            skLineSegment(sketch, "E2759", {"start": v(23.8, -20.15) * mm, "end": v(23.6, -20.09) * mm});
            skLineSegment(sketch, "E2760", {"start": v(23.6, -20.09) * mm, "end": v(23.25, -20) * mm});
            skLineSegment(sketch, "E2761", {"start": v(23.25, -20) * mm, "end": v(23.04, -19.95) * mm});
            skLineSegment(sketch, "E2762", {"start": v(23.04, -19.95) * mm, "end": v(22.74, -19.9) * mm});
            skLineSegment(sketch, "E2763", {"start": v(22.74, -19.9) * mm, "end": v(22.58, -19.88) * mm});
            skLineSegment(sketch, "E2764", {"start": v(22.58, -19.88) * mm, "end": v(22.43, -19.87) * mm});
            skLineSegment(sketch, "E2765", {"start": v(22.43, -19.87) * mm, "end": v(22.31, -19.88) * mm});
            skLineSegment(sketch, "E2766", {"start": v(22.31, -19.88) * mm, "end": v(22.26, -19.9) * mm});
            skLineSegment(sketch, "E2767", {"start": v(22.26, -19.9) * mm, "end": v(22.23, -19.9) * mm});
            skLineSegment(sketch, "E2768", {"start": v(22.23, -19.9) * mm, "end": v(22.2, -19.94) * mm});
            skLineSegment(sketch, "E2769", {"start": v(22.2, -19.94) * mm, "end": v(22.16, -20) * mm});
            skLineSegment(sketch, "E2770", {"start": v(22.16, -20) * mm, "end": v(22.08, -20.15) * mm});
            skLineSegment(sketch, "E2771", {"start": v(22.08, -20.15) * mm, "end": v(22, -20.36) * mm});
            skLineSegment(sketch, "E2772", {"start": v(22, -20.36) * mm, "end": v(21.93, -20.6) * mm});
            skLineSegment(sketch, "E2773", {"start": v(21.93, -20.6) * mm, "end": v(21.8, -21.04) * mm});
            skLineSegment(sketch, "E2774", {"start": v(21.8, -21.04) * mm, "end": v(21.7, -21.34) * mm});
            skLineSegment(sketch, "E2775", {"start": v(21.7, -21.34) * mm, "end": v(21.54, -21.88) * mm});
            skLineSegment(sketch, "E2776", {"start": v(21.54, -21.88) * mm, "end": v(21.44, -22.15) * mm});
            skLineSegment(sketch, "E2777", {"start": v(21.44, -22.15) * mm, "end": v(21.34, -22.4) * mm});
            skLineSegment(sketch, "E2778", {"start": v(21.34, -22.4) * mm, "end": v(21.22, -22.66) * mm});
            skLineSegment(sketch, "E2779", {"start": v(21.22, -22.66) * mm, "end": v(21.09, -22.9) * mm});
            skLineSegment(sketch, "E2780", {"start": v(21.09, -22.9) * mm, "end": v(20.94, -23.14) * mm});
            skLineSegment(sketch, "E2781", {"start": v(20.94, -23.14) * mm, "end": v(20.77, -23.38) * mm});
            skLineSegment(sketch, "E2782", {"start": v(20.77, -23.38) * mm, "end": v(20.6, -23.58) * mm});
            skLineSegment(sketch, "E2783", {"start": v(20.6, -23.58) * mm, "end": v(20.43, -23.76) * mm});
            skLineSegment(sketch, "E2784", {"start": v(20.43, -23.76) * mm, "end": v(20.25, -23.93) * mm});
            skLineSegment(sketch, "E2785", {"start": v(20.25, -23.93) * mm, "end": v(20.06, -24.08) * mm});
            skLineSegment(sketch, "E2786", {"start": v(20.06, -24.08) * mm, "end": v(19.87, -24.21) * mm});
            skLineSegment(sketch, "E2787", {"start": v(19.87, -24.21) * mm, "end": v(19.67, -24.33) * mm});
            skLineSegment(sketch, "E2788", {"start": v(19.67, -24.33) * mm, "end": v(19.46, -24.44) * mm});
            skLineSegment(sketch, "E2789", {"start": v(19.46, -24.44) * mm, "end": v(19.25, -24.53) * mm});
            skLineSegment(sketch, "E2790", {"start": v(19.25, -24.53) * mm, "end": v(19.03, -24.6) * mm});
            skLineSegment(sketch, "E2791", {"start": v(19.03, -24.6) * mm, "end": v(18.81, -24.67) * mm});
            skLineSegment(sketch, "E2792", {"start": v(18.81, -24.67) * mm, "end": v(18.59, -24.72) * mm});
            skLineSegment(sketch, "E2793", {"start": v(18.59, -24.72) * mm, "end": v(18.36, -24.77) * mm});
            skLineSegment(sketch, "E2794", {"start": v(18.36, -24.77) * mm, "end": v(18.13, -24.8) * mm});
            skLineSegment(sketch, "E2795", {"start": v(18.13, -24.8) * mm, "end": v(17.9, -24.82) * mm});
            skLineSegment(sketch, "E2796", {"start": v(17.9, -24.82) * mm, "end": v(17.66, -24.83) * mm});
            skLineSegment(sketch, "E2797", {"start": v(17.66, -24.83) * mm, "end": v(17.42, -24.83) * mm});
            skLineSegment(sketch, "E2798", {"start": v(17.42, -24.83) * mm, "end": v(17.5, -25) * mm});
            skLineSegment(sketch, "E2799", {"start": v(17.5, -25) * mm, "end": v(17.58, -25.16) * mm});
            skLineSegment(sketch, "E2800", {"start": v(17.58, -25.16) * mm, "end": v(17.64, -25.33) * mm});
            skLineSegment(sketch, "E2801", {"start": v(17.64, -25.33) * mm, "end": v(17.7, -25.51) * mm});
            skLineSegment(sketch, "E2802", {"start": v(17.7, -25.51) * mm, "end": v(17.74, -25.7) * mm});
            skLineSegment(sketch, "E2803", {"start": v(17.74, -25.7) * mm, "end": v(17.77, -25.88) * mm});
            skLineSegment(sketch, "E2804", {"start": v(17.77, -25.88) * mm, "end": v(17.79, -26.07) * mm});
            skLineSegment(sketch, "E2805", {"start": v(17.79, -26.07) * mm, "end": v(17.8, -26.27) * mm});
            skLineSegment(sketch, "E2806", {"start": v(17.8, -26.27) * mm, "end": v(17.79, -26.42) * mm});
            skLineSegment(sketch, "E2807", {"start": v(17.79, -26.42) * mm, "end": v(17.78, -26.57) * mm});
            skLineSegment(sketch, "E2808", {"start": v(17.78, -26.57) * mm, "end": v(17.73, -26.87) * mm});
            skLineSegment(sketch, "E2809", {"start": v(17.73, -26.87) * mm, "end": v(17.66, -27.16) * mm});
            skLineSegment(sketch, "E2810", {"start": v(17.66, -27.16) * mm, "end": v(17.56, -27.43) * mm});
            skLineSegment(sketch, "E2811", {"start": v(17.56, -27.43) * mm, "end": v(17.43, -27.7) * mm});
            skLineSegment(sketch, "E2812", {"start": v(17.43, -27.7) * mm, "end": v(17.28, -27.94) * mm});
            skLineSegment(sketch, "E2813", {"start": v(17.28, -27.94) * mm, "end": v(17.1, -28.17) * mm});
            skLineSegment(sketch, "E2814", {"start": v(17.1, -28.17) * mm, "end": v(16.91, -28.39) * mm});
            skLineSegment(sketch, "E2815", {"start": v(16.91, -28.39) * mm, "end": v(16.7, -28.58) * mm});
            skLineSegment(sketch, "E2816", {"start": v(16.7, -28.58) * mm, "end": v(16.47, -28.75) * mm});
            skLineSegment(sketch, "E2817", {"start": v(16.47, -28.75) * mm, "end": v(16.22, -28.9) * mm});
            skLineSegment(sketch, "E2818", {"start": v(16.22, -28.9) * mm, "end": v(15.96, -29.03) * mm});
            skLineSegment(sketch, "E2819", {"start": v(15.96, -29.03) * mm, "end": v(15.68, -29.13) * mm});
            skLineSegment(sketch, "E2820", {"start": v(15.68, -29.13) * mm, "end": v(15.4, -29.2) * mm});
            skLineSegment(sketch, "E2821", {"start": v(15.4, -29.2) * mm, "end": v(15.25, -29.23) * mm});
            skLineSegment(sketch, "E2822", {"start": v(15.25, -29.23) * mm, "end": v(15.1, -29.25) * mm});
            skLineSegment(sketch, "E2823", {"start": v(15.1, -29.25) * mm, "end": v(14.95, -29.26) * mm});
            skLineSegment(sketch, "E2824", {"start": v(14.95, -29.26) * mm, "end": v(14.8, -29.27) * mm});
            skLineSegment(sketch, "E2825", {"start": v(14.8, -29.27) * mm, "end": v(14.64, -29.26) * mm});
            skLineSegment(sketch, "E2826", {"start": v(14.64, -29.26) * mm, "end": v(14.48, -29.25) * mm});
            skLineSegment(sketch, "E2827", {"start": v(14.48, -29.25) * mm, "end": v(14.19, -29.2) * mm});
            skLineSegment(sketch, "E2828", {"start": v(14.19, -29.2) * mm, "end": v(13.9, -29.13) * mm});
            skLineSegment(sketch, "E2829", {"start": v(13.9, -29.13) * mm, "end": v(13.62, -29.03) * mm});
            skLineSegment(sketch, "E2830", {"start": v(13.62, -29.03) * mm, "end": v(13.36, -28.9) * mm});
            skLineSegment(sketch, "E2831", {"start": v(13.36, -28.9) * mm, "end": v(13.11, -28.75) * mm});
            skLineSegment(sketch, "E2832", {"start": v(13.11, -28.75) * mm, "end": v(12.88, -28.58) * mm});
            skLineSegment(sketch, "E2833", {"start": v(12.88, -28.58) * mm, "end": v(12.67, -28.39) * mm});
            skLineSegment(sketch, "E2834", {"start": v(12.67, -28.39) * mm, "end": v(12.48, -28.17) * mm});
            skLineSegment(sketch, "E2835", {"start": v(12.48, -28.17) * mm, "end": v(12.3, -27.94) * mm});
            skLineSegment(sketch, "E2836", {"start": v(12.3, -27.94) * mm, "end": v(12.15, -27.7) * mm});
            skLineSegment(sketch, "E2837", {"start": v(12.15, -27.7) * mm, "end": v(12.03, -27.43) * mm});
            skLineSegment(sketch, "E2838", {"start": v(12.03, -27.43) * mm, "end": v(11.93, -27.16) * mm});
            skLineSegment(sketch, "E2839", {"start": v(11.93, -27.16) * mm, "end": v(11.85, -26.87) * mm});
            skLineSegment(sketch, "E2840", {"start": v(11.85, -26.87) * mm, "end": v(11.83, -26.72) * mm});
            skLineSegment(sketch, "E2841", {"start": v(11.83, -26.72) * mm, "end": v(11.8, -26.57) * mm});
            skLineSegment(sketch, "E2842", {"start": v(11.8, -26.57) * mm, "end": v(11.8, -26.42) * mm});
            skLineSegment(sketch, "E2843", {"start": v(11.8, -26.42) * mm, "end": v(11.8, -26.27) * mm});
            skLineSegment(sketch, "E2844", {"start": v(11.8, -26.27) * mm, "end": v(11.8, -26.07) * mm});
            skLineSegment(sketch, "E2845", {"start": v(11.8, -26.07) * mm, "end": v(11.82, -25.89) * mm});
            skLineSegment(sketch, "E2846", {"start": v(11.82, -25.89) * mm, "end": v(11.85, -25.7) * mm});
            skLineSegment(sketch, "E2847", {"start": v(11.85, -25.7) * mm, "end": v(11.89, -25.52) * mm});
            skLineSegment(sketch, "E2848", {"start": v(11.89, -25.52) * mm, "end": v(11.94, -25.34) * mm});
            skLineSegment(sketch, "E2849", {"start": v(11.94, -25.34) * mm, "end": v(12, -25.17) * mm});
            skLineSegment(sketch, "E2850", {"start": v(12, -25.17) * mm, "end": v(12.07, -25) * mm});
            skLineSegment(sketch, "E2851", {"start": v(12.07, -25) * mm, "end": v(12.15, -24.84) * mm});
            skLineSegment(sketch, "E2852", {"start": v(12.15, -24.84) * mm, "end": v(12.24, -24.68) * mm});
            skLineSegment(sketch, "E2853", {"start": v(12.24, -24.68) * mm, "end": v(12.34, -24.53) * mm});
            skLineSegment(sketch, "E2854", {"start": v(12.34, -24.53) * mm, "end": v(12.45, -24.39) * mm});
            skLineSegment(sketch, "E2855", {"start": v(12.45, -24.39) * mm, "end": v(12.57, -24.25) * mm});
            skLineSegment(sketch, "E2856", {"start": v(12.57, -24.25) * mm, "end": v(12.7, -24.12) * mm});
            skLineSegment(sketch, "E2857", {"start": v(12.7, -24.12) * mm, "end": v(12.82, -24) * mm});
            skLineSegment(sketch, "E2858", {"start": v(12.82, -24) * mm, "end": v(12.96, -23.89) * mm});
            skLineSegment(sketch, "E2859", {"start": v(12.96, -23.89) * mm, "end": v(13.1, -23.78) * mm});
            skLineSegment(sketch, "E2860", {"start": v(13.1, -23.78) * mm, "end": v(12.3, -23.45) * mm});
            skLineSegment(sketch, "E2861", {"start": v(12.3, -23.45) * mm, "end": v(11.52, -23.1) * mm});
            skLineSegment(sketch, "E2862", {"start": v(11.52, -23.1) * mm, "end": v(10.74, -22.72) * mm});
            skLineSegment(sketch, "E2863", {"start": v(10.74, -22.72) * mm, "end": v(9.96, -22.33) * mm});
            skLineSegment(sketch, "E2864", {"start": v(9.96, -22.33) * mm, "end": v(8.97, -21.83) * mm});
            skLineSegment(sketch, "E2865", {"start": v(8.97, -21.83) * mm, "end": v(7.97, -21.34) * mm});
            skLineSegment(sketch, "E2866", {"start": v(7.97, -21.34) * mm, "end": v(7.46, -21.1) * mm});
            skLineSegment(sketch, "E2867", {"start": v(7.46, -21.1) * mm, "end": v(6.95, -20.87) * mm});
            skLineSegment(sketch, "E2868", {"start": v(6.95, -20.87) * mm, "end": v(6.44, -20.65) * mm});
            skLineSegment(sketch, "E2869", {"start": v(6.44, -20.65) * mm, "end": v(5.92, -20.46) * mm});
            skLineSegment(sketch, "E2870", {"start": v(5.92, -20.46) * mm, "end": v(5.92, -20.45) * mm});
            skLineSegment(sketch, "E2871", {"start": v(5.92, -20.45) * mm, "end": v(5.6, -20.34) * mm});
            skLineSegment(sketch, "E2872", {"start": v(5.6, -20.34) * mm, "end": v(5.28, -20.23) * mm});
            skLineSegment(sketch, "E2873", {"start": v(5.28, -20.23) * mm, "end": v(5.26, -20.23) * mm});
            skLineSegment(sketch, "E2874", {"start": v(5.26, -20.23) * mm, "end": v(4.27, -19.89) * mm});
            skLineSegment(sketch, "E2875", {"start": v(4.27, -19.89) * mm, "end": v(4.2, -19.85) * mm});
            skLineSegment(sketch, "E2876", {"start": v(4.2, -19.85) * mm, "end": v(4.03, -19.79) * mm});
            skLineSegment(sketch, "E2877", {"start": v(4.03, -19.79) * mm, "end": v(3.87, -19.75) * mm});
            skLineSegment(sketch, "E2878", {"start": v(3.87, -19.75) * mm, "end": v(3.82, -19.73) * mm});
            skLineSegment(sketch, "E2879", {"start": v(3.82, -19.73) * mm, "end": v(3.46, -19.65) * mm});
            skLineSegment(sketch, "E2880", {"start": v(3.46, -19.65) * mm, "end": v(3.1, -19.6) * mm});
            skLineSegment(sketch, "E2881", {"start": v(3.1, -19.6) * mm, "end": v(3.01, -19.58) * mm});
            skLineSegment(sketch, "E2882", {"start": v(3.01, -19.58) * mm, "end": v(3.2, -19.8) * mm});
            skLineSegment(sketch, "E2883", {"start": v(3.2, -19.8) * mm, "end": v(3.37, -20.02) * mm});
            skLineSegment(sketch, "E2884", {"start": v(3.37, -20.02) * mm, "end": v(3.52, -20.27) * mm});
            skLineSegment(sketch, "E2885", {"start": v(3.52, -20.27) * mm, "end": v(3.64, -20.53) * mm});
            skLineSegment(sketch, "E2886", {"start": v(3.64, -20.53) * mm, "end": v(3.74, -20.8) * mm});
            skLineSegment(sketch, "E2887", {"start": v(3.74, -20.8) * mm, "end": v(3.82, -21.09) * mm});
            skLineSegment(sketch, "E2888", {"start": v(3.82, -21.09) * mm, "end": v(3.86, -21.38) * mm});
            skLineSegment(sketch, "E2889", {"start": v(3.86, -21.38) * mm, "end": v(3.87, -21.53) * mm});
            skLineSegment(sketch, "E2890", {"start": v(3.87, -21.53) * mm, "end": v(3.88, -21.69) * mm});
            skLineSegment(sketch, "E2891", {"start": v(3.88, -21.69) * mm, "end": v(3.87, -21.84) * mm});
            skLineSegment(sketch, "E2892", {"start": v(3.87, -21.84) * mm, "end": v(3.86, -22) * mm});
            skLineSegment(sketch, "E2893", {"start": v(3.86, -22) * mm, "end": v(3.82, -22.3) * mm});
            skLineSegment(sketch, "E2894", {"start": v(3.82, -22.3) * mm, "end": v(3.74, -22.58) * mm});
            skLineSegment(sketch, "E2895", {"start": v(3.74, -22.58) * mm, "end": v(3.64, -22.85) * mm});
            skLineSegment(sketch, "E2896", {"start": v(3.64, -22.85) * mm, "end": v(3.51, -23.12) * mm});
            skLineSegment(sketch, "E2897", {"start": v(3.51, -23.12) * mm, "end": v(3.36, -23.36) * mm});
            skLineSegment(sketch, "E2898", {"start": v(3.36, -23.36) * mm, "end": v(3.2, -23.6) * mm});
            skLineSegment(sketch, "E2899", {"start": v(3.2, -23.6) * mm, "end": v(3, -23.8) * mm});
            skLineSegment(sketch, "E2900", {"start": v(3, -23.8) * mm, "end": v(2.78, -24) * mm});
            skLineSegment(sketch, "E2901", {"start": v(2.78, -24) * mm, "end": v(2.55, -24.17) * mm});
            skLineSegment(sketch, "E2902", {"start": v(2.55, -24.17) * mm, "end": v(2.3, -24.32) * mm});
            skLineSegment(sketch, "E2903", {"start": v(2.3, -24.32) * mm, "end": v(2.04, -24.45) * mm});
            skLineSegment(sketch, "E2904", {"start": v(2.04, -24.45) * mm, "end": v(1.77, -24.55) * mm});
            skLineSegment(sketch, "E2905", {"start": v(1.77, -24.55) * mm, "end": v(1.48, -24.63) * mm});
            skLineSegment(sketch, "E2906", {"start": v(1.48, -24.63) * mm, "end": v(1.33, -24.65) * mm});
            skLineSegment(sketch, "E2907", {"start": v(1.33, -24.65) * mm, "end": v(1.18, -24.67) * mm});
            skLineSegment(sketch, "E2908", {"start": v(1.18, -24.67) * mm, "end": v(1.03, -24.68) * mm});
            skLineSegment(sketch, "E2909", {"start": v(1.03, -24.68) * mm, "end": v(0.88, -24.69) * mm});
            skLineSegment(sketch, "E2910", {"start": v(0.88, -24.69) * mm, "end": v(0.72, -24.68) * mm});
            skLineSegment(sketch, "E2911", {"start": v(0.72, -24.68) * mm, "end": v(0.57, -24.67) * mm});
            skLineSegment(sketch, "E2912", {"start": v(0.57, -24.67) * mm, "end": v(0.27, -24.63) * mm});
            skLineSegment(sketch, "E2913", {"start": v(0.27, -24.63) * mm, "end": v(-0.02, -24.55) * mm});
            skLineSegment(sketch, "E2914", {"start": v(-0.02, -24.55) * mm, "end": v(-0.3, -24.45) * mm});
            skLineSegment(sketch, "E2915", {"start": v(-0.3, -24.45) * mm, "end": v(-0.55, -24.32) * mm});
            skLineSegment(sketch, "E2916", {"start": v(-0.55, -24.32) * mm, "end": v(-0.8, -24.17) * mm});
            skLineSegment(sketch, "E2917", {"start": v(-0.8, -24.17) * mm, "end": v(-1.03, -24) * mm});
            skLineSegment(sketch, "E2918", {"start": v(-1.03, -24) * mm, "end": v(-1.24, -23.8) * mm});
            skLineSegment(sketch, "E2919", {"start": v(-1.24, -23.8) * mm, "end": v(-1.44, -23.6) * mm});
            skLineSegment(sketch, "E2920", {"start": v(-1.44, -23.6) * mm, "end": v(-1.61, -23.36) * mm});
            skLineSegment(sketch, "E2921", {"start": v(-1.61, -23.36) * mm, "end": v(-1.76, -23.12) * mm});
            skLineSegment(sketch, "E2922", {"start": v(-1.76, -23.12) * mm, "end": v(-1.89, -22.85) * mm});
            skLineSegment(sketch, "E2923", {"start": v(-1.89, -22.85) * mm, "end": v(-1.99, -22.58) * mm});
            skLineSegment(sketch, "E2924", {"start": v(-1.99, -22.58) * mm, "end": v(-2.06, -22.3) * mm});
            skLineSegment(sketch, "E2925", {"start": v(-2.06, -22.3) * mm, "end": v(-2.09, -22.14) * mm});
            skLineSegment(sketch, "E2926", {"start": v(-2.09, -22.14) * mm, "end": v(-2.1, -22) * mm});
            skLineSegment(sketch, "E2927", {"start": v(-2.1, -22) * mm, "end": v(-2.12, -21.84) * mm});
            skLineSegment(sketch, "E2928", {"start": v(-2.12, -21.84) * mm, "end": v(-2.12, -21.69) * mm});
            skLineSegment(sketch, "E2929", {"start": v(-2.12, -21.69) * mm, "end": v(-2.12, -21.46) * mm});
            skLineSegment(sketch, "E2930", {"start": v(-2.12, -21.46) * mm, "end": v(-2.1, -21.24) * mm});
            skLineSegment(sketch, "E2931", {"start": v(-2.1, -21.24) * mm, "end": v(-2.05, -21.03) * mm});
            skLineSegment(sketch, "E2932", {"start": v(-2.05, -21.03) * mm, "end": v(-2, -20.82) * mm});
            skLineSegment(sketch, "E2933", {"start": v(-2, -20.82) * mm, "end": v(-1.92, -20.61) * mm});
            skLineSegment(sketch, "E2934", {"start": v(-1.92, -20.61) * mm, "end": v(-1.84, -20.41) * mm});
            skLineSegment(sketch, "E2935", {"start": v(-1.84, -20.41) * mm, "end": v(-1.74, -20.23) * mm});
            skLineSegment(sketch, "E2936", {"start": v(-1.74, -20.23) * mm, "end": v(-1.63, -20.04) * mm});
            skLineSegment(sketch, "E2937", {"start": v(-1.63, -20.04) * mm, "end": v(-2.17, -20.27) * mm});
            skLineSegment(sketch, "E2938", {"start": v(-2.17, -20.27) * mm, "end": v(-2.71, -20.5) * mm});
            skLineSegment(sketch, "E2939", {"start": v(-2.71, -20.5) * mm, "end": v(-3.37, -20.77) * mm});
            skLineSegment(sketch, "E2940", {"start": v(-3.37, -20.77) * mm, "end": v(-3.69, -20.89) * mm});
            skLineSegment(sketch, "E2941", {"start": v(-3.69, -20.89) * mm, "end": v(-4, -21) * mm});
            skLineSegment(sketch, "E2942", {"start": v(-4, -21) * mm, "end": v(-4.31, -21.1) * mm});
            skLineSegment(sketch, "E2943", {"start": v(-4.31, -21.1) * mm, "end": v(-4.62, -21.18) * mm});
            skLineSegment(sketch, "E2944", {"start": v(-4.62, -21.18) * mm, "end": v(-4.93, -21.25) * mm});
            skLineSegment(sketch, "E2945", {"start": v(-4.93, -21.25) * mm, "end": v(-5.24, -21.32) * mm});
            skLineSegment(sketch, "E2946", {"start": v(-5.24, -21.32) * mm, "end": v(-5.55, -21.37) * mm});
            skLineSegment(sketch, "E2947", {"start": v(-5.55, -21.37) * mm, "end": v(-5.87, -21.41) * mm});
            skLineSegment(sketch, "E2948", {"start": v(-5.87, -21.41) * mm, "end": v(-6.19, -21.44) * mm});
            skLineSegment(sketch, "E2949", {"start": v(-6.19, -21.44) * mm, "end": v(-6.51, -21.46) * mm});
            skLineSegment(sketch, "E2950", {"start": v(-6.51, -21.46) * mm, "end": v(-6.85, -21.47) * mm});
            skLineSegment(sketch, "E2951", {"start": v(-6.85, -21.47) * mm, "end": v(-7.19, -21.46) * mm});
            skLineSegment(sketch, "E2952", {"start": v(-7.19, -21.46) * mm, "end": v(-7.54, -21.45) * mm});
            skLineSegment(sketch, "E2953", {"start": v(-7.54, -21.45) * mm, "end": v(-7.9, -21.42) * mm});
            skLineSegment(sketch, "E2954", {"start": v(-7.9, -21.42) * mm, "end": v(-8.23, -21.38) * mm});
            skLineSegment(sketch, "E2955", {"start": v(-8.23, -21.38) * mm, "end": v(-8.55, -21.34) * mm});
            skLineSegment(sketch, "E2956", {"start": v(-8.55, -21.34) * mm, "end": v(-8.88, -21.28) * mm});
            skLineSegment(sketch, "E2957", {"start": v(-8.88, -21.28) * mm, "end": v(-9.21, -21.2) * mm});
            skLineSegment(sketch, "E2958", {"start": v(-9.21, -21.2) * mm, "end": v(-9.88, -21.05) * mm});
            skLineSegment(sketch, "E2959", {"start": v(-9.88, -21.05) * mm, "end": v(-10.56, -20.86) * mm});
            skLineSegment(sketch, "E2960", {"start": v(-10.56, -20.86) * mm, "end": v(-11.9, -20.45) * mm});
            skLineSegment(sketch, "E2961", {"start": v(-11.9, -20.45) * mm, "end": v(-12.54, -20.25) * mm});
            skLineSegment(sketch, "E2962", {"start": v(-12.54, -20.25) * mm, "end": v(-13.17, -20.06) * mm});
            skLineSegment(sketch, "E2963", {"start": v(-13.17, -20.06) * mm, "end": v(-13.98, -19.83) * mm});
            skLineSegment(sketch, "E2964", {"start": v(-13.98, -19.83) * mm, "end": v(-14.41, -19.72) * mm});
            skLineSegment(sketch, "E2965", {"start": v(-14.41, -19.72) * mm, "end": v(-14.85, -19.62) * mm});
            skLineSegment(sketch, "E2966", {"start": v(-5.8, -56.54) * mm, "end": v(-5.27, -56.64) * mm});
            skLineSegment(sketch, "E2967", {"start": v(-5.27, -56.64) * mm, "end": v(-4.75, -56.76) * mm});
            skLineSegment(sketch, "E2968", {"start": v(-4.75, -56.76) * mm, "end": v(-4.22, -56.88) * mm});
            skLineSegment(sketch, "E2969", {"start": v(-4.22, -56.88) * mm, "end": v(-3.7, -57.02) * mm});
            skLineSegment(sketch, "E2970", {"start": v(-3.7, -57.02) * mm, "end": v(-3.18, -57.16) * mm});
            skLineSegment(sketch, "E2971", {"start": v(-3.18, -57.16) * mm, "end": v(-2.68, -57.32) * mm});
            skLineSegment(sketch, "E2972", {"start": v(-2.68, -57.32) * mm, "end": v(-2.18, -57.5) * mm});
            skLineSegment(sketch, "E2973", {"start": v(-2.18, -57.5) * mm, "end": v(-1.7, -57.68) * mm});
            skLineSegment(sketch, "E2974", {"start": v(-1.7, -57.68) * mm, "end": v(-1.38, -57.82) * mm});
            skLineSegment(sketch, "E2975", {"start": v(-1.38, -57.82) * mm, "end": v(-1.07, -57.97) * mm});
            skLineSegment(sketch, "E2976", {"start": v(-1.07, -57.97) * mm, "end": v(-0.76, -58.14) * mm});
            skLineSegment(sketch, "E2977", {"start": v(-0.76, -58.14) * mm, "end": v(-0.46, -58.31) * mm});
            skLineSegment(sketch, "E2978", {"start": v(-0.46, -58.31) * mm, "end": v(-0.26, -58.44) * mm});
            skLineSegment(sketch, "E2979", {"start": v(-0.26, -58.44) * mm, "end": v(-0.06, -58.56) * mm});
            skLineSegment(sketch, "E2980", {"start": v(-0.06, -58.56) * mm, "end": v(0.15, -58.54) * mm});
            skLineSegment(sketch, "E2981", {"start": v(0.15, -58.54) * mm, "end": v(0.42, -58.49) * mm});
            skLineSegment(sketch, "E2982", {"start": v(0.42, -58.49) * mm, "end": v(1.07, -58.33) * mm});
            skLineSegment(sketch, "E2983", {"start": v(1.07, -58.33) * mm, "end": v(1.7, -58.16) * mm});
            skLineSegment(sketch, "E2984", {"start": v(1.7, -58.16) * mm, "end": v(2.14, -58.04) * mm});
            skLineSegment(sketch, "E2985", {"start": v(2.14, -58.04) * mm, "end": v(4.45, -57.4) * mm});
            skLineSegment(sketch, "E2986", {"start": v(4.45, -57.4) * mm, "end": v(4.33, -55.32) * mm});
            skLineSegment(sketch, "E2987", {"start": v(4.33, -55.32) * mm, "end": v(3.97, -55.47) * mm});
            skLineSegment(sketch, "E2988", {"start": v(3.97, -55.47) * mm, "end": v(3.6, -55.61) * mm});
            skLineSegment(sketch, "E2989", {"start": v(3.6, -55.61) * mm, "end": v(3.3, -55.7) * mm});
            skLineSegment(sketch, "E2990", {"start": v(3.3, -55.7) * mm, "end": v(3.03, -55.8) * mm});
            skLineSegment(sketch, "E2991", {"start": v(3.03, -55.8) * mm, "end": v(2.75, -55.87) * mm});
            skLineSegment(sketch, "E2992", {"start": v(2.75, -55.87) * mm, "end": v(2.47, -55.93) * mm});
            skLineSegment(sketch, "E2993", {"start": v(2.47, -55.93) * mm, "end": v(2.2, -55.98) * mm});
            skLineSegment(sketch, "E2994", {"start": v(2.2, -55.98) * mm, "end": v(1.92, -56.02) * mm});
            skLineSegment(sketch, "E2995", {"start": v(1.92, -56.02) * mm, "end": v(1.64, -56.05) * mm});
            skLineSegment(sketch, "E2996", {"start": v(1.64, -56.05) * mm, "end": v(1.37, -56.07) * mm});
            skLineSegment(sketch, "E2997", {"start": v(1.37, -56.07) * mm, "end": v(1.09, -56.09) * mm});
            skLineSegment(sketch, "E2998", {"start": v(1.09, -56.09) * mm, "end": v(0.81, -56.1) * mm});
            skLineSegment(sketch, "E2999", {"start": v(0.81, -56.1) * mm, "end": v(0.25, -56.08) * mm});
            skLineSegment(sketch, "E3000", {"start": v(0.25, -56.08) * mm, "end": v(-0.32, -56.04) * mm});
            skLineSegment(sketch, "E3001", {"start": v(-0.32, -56.04) * mm, "end": v(-0.91, -55.99) * mm});
            skLineSegment(sketch, "E3002", {"start": v(-0.91, -55.99) * mm, "end": v(-1.28, -55.94) * mm});
            skLineSegment(sketch, "E3003", {"start": v(-1.28, -55.94) * mm, "end": v(-1.66, -55.87) * mm});
            skLineSegment(sketch, "E3004", {"start": v(-1.66, -55.87) * mm, "end": v(-2.04, -55.8) * mm});
            skLineSegment(sketch, "E3005", {"start": v(-2.04, -55.8) * mm, "end": v(-2.42, -55.7) * mm});
            skLineSegment(sketch, "E3006", {"start": v(-2.42, -55.7) * mm, "end": v(-3.18, -55.51) * mm});
            skLineSegment(sketch, "E3007", {"start": v(-3.18, -55.51) * mm, "end": v(-3.92, -55.32) * mm});
            skLineSegment(sketch, "E3008", {"start": v(-3.92, -55.32) * mm, "end": v(-4.73, -55.1) * mm});
            skLineSegment(sketch, "E3009", {"start": v(-4.73, -55.1) * mm, "end": v(-5.54, -54.9) * mm});
            skLineSegment(sketch, "E3010", {"start": v(-5.54, -54.9) * mm, "end": v(-5.8, -56.54) * mm});
            skLineSegment(sketch, "E3011", {"start": v(-14.35, 12.16) * mm, "end": v(-14.13, 12.14) * mm});
            skLineSegment(sketch, "E3012", {"start": v(-14.13, 12.14) * mm, "end": v(-13.92, 12.13) * mm});
            skLineSegment(sketch, "E3013", {"start": v(-13.92, 12.13) * mm, "end": v(-13.7, 12.13) * mm});
            skLineSegment(sketch, "E3014", {"start": v(-13.7, 12.13) * mm, "end": v(-13.5, 12.15) * mm});
            skLineSegment(sketch, "E3015", {"start": v(-13.5, 12.15) * mm, "end": v(-13.28, 12.18) * mm});
            skLineSegment(sketch, "E3016", {"start": v(-13.28, 12.18) * mm, "end": v(-13.06, 12.24) * mm});
            skLineSegment(sketch, "E3017", {"start": v(-13.06, 12.24) * mm, "end": v(-12.83, 12.3) * mm});
            skLineSegment(sketch, "E3018", {"start": v(-12.83, 12.3) * mm, "end": v(-12.6, 12.39) * mm});
            skLineSegment(sketch, "E3019", {"start": v(-12.6, 12.39) * mm, "end": v(-12.26, 12.54) * mm});
            skLineSegment(sketch, "E3020", {"start": v(-12.26, 12.54) * mm, "end": v(-11.91, 12.72) * mm});
            skLineSegment(sketch, "E3021", {"start": v(-11.91, 12.72) * mm, "end": v(-11.57, 12.91) * mm});
            skLineSegment(sketch, "E3022", {"start": v(-11.57, 12.91) * mm, "end": v(-11.23, 13.11) * mm});
            skLineSegment(sketch, "E3023", {"start": v(-11.23, 13.11) * mm, "end": v(-10.56, 13.53) * mm});
            skLineSegment(sketch, "E3024", {"start": v(-10.56, 13.53) * mm, "end": v(-10.23, 13.74) * mm});
            skLineSegment(sketch, "E3025", {"start": v(-10.23, 13.74) * mm, "end": v(-9.9, 13.93) * mm});
            skLineSegment(sketch, "E3026", {"start": v(-9.9, 13.93) * mm, "end": v(-9.41, 14.2) * mm});
            skLineSegment(sketch, "E3027", {"start": v(-9.41, 14.2) * mm, "end": v(-8.92, 14.44) * mm});
            skLineSegment(sketch, "E3028", {"start": v(-8.92, 14.44) * mm, "end": v(-8.68, 14.55) * mm});
            skLineSegment(sketch, "E3029", {"start": v(-8.68, 14.55) * mm, "end": v(-8.43, 14.65) * mm});
            skLineSegment(sketch, "E3030", {"start": v(-8.43, 14.65) * mm, "end": v(-8.18, 14.74) * mm});
            skLineSegment(sketch, "E3031", {"start": v(-8.18, 14.74) * mm, "end": v(-7.93, 14.82) * mm});
            skLineSegment(sketch, "E3032", {"start": v(-7.93, 14.82) * mm, "end": v(-7.67, 14.9) * mm});
            skLineSegment(sketch, "E3033", {"start": v(-7.67, 14.9) * mm, "end": v(-7.41, 14.96) * mm});
            skLineSegment(sketch, "E3034", {"start": v(-7.41, 14.96) * mm, "end": v(-7.15, 15.01) * mm});
            skLineSegment(sketch, "E3035", {"start": v(-7.15, 15.01) * mm, "end": v(-6.89, 15.06) * mm});
            skLineSegment(sketch, "E3036", {"start": v(-6.89, 15.06) * mm, "end": v(-6.62, 15.1) * mm});
            skLineSegment(sketch, "E3037", {"start": v(-6.62, 15.1) * mm, "end": v(-6.34, 15.12) * mm});
            skLineSegment(sketch, "E3038", {"start": v(-6.34, 15.12) * mm, "end": v(-6.07, 15.13) * mm});
            skLineSegment(sketch, "E3039", {"start": v(-6.07, 15.13) * mm, "end": v(-5.78, 15.13) * mm});
            skLineSegment(sketch, "E3040", {"start": v(-5.78, 15.13) * mm, "end": v(-5.45, 15.12) * mm});
            skLineSegment(sketch, "E3041", {"start": v(-5.45, 15.12) * mm, "end": v(-5.12, 15.1) * mm});
            skLineSegment(sketch, "E3042", {"start": v(-5.12, 15.1) * mm, "end": v(-4.8, 15.05) * mm});
            skLineSegment(sketch, "E3043", {"start": v(-4.8, 15.05) * mm, "end": v(-4.49, 14.99) * mm});
            skLineSegment(sketch, "E3044", {"start": v(-4.49, 14.99) * mm, "end": v(-4.17, 14.9) * mm});
            skLineSegment(sketch, "E3045", {"start": v(-4.17, 14.9) * mm, "end": v(-3.87, 14.81) * mm});
            skLineSegment(sketch, "E3046", {"start": v(-3.87, 14.81) * mm, "end": v(-3.56, 14.7) * mm});
            skLineSegment(sketch, "E3047", {"start": v(-3.56, 14.7) * mm, "end": v(-3.26, 14.57) * mm});
            skLineSegment(sketch, "E3048", {"start": v(-3.26, 14.57) * mm, "end": v(-2.86, 14.37) * mm});
            skLineSegment(sketch, "E3049", {"start": v(-2.86, 14.37) * mm, "end": v(-2.49, 14.15) * mm});
            skLineSegment(sketch, "E3050", {"start": v(-2.49, 14.15) * mm, "end": v(-2.12, 13.92) * mm});
            skLineSegment(sketch, "E3051", {"start": v(-2.12, 13.92) * mm, "end": v(-1.75, 13.7) * mm});
            skLineSegment(sketch, "E3052", {"start": v(-1.75, 13.7) * mm, "end": v(-1.48, 13.54) * mm});
            skLineSegment(sketch, "E3053", {"start": v(-1.48, 13.54) * mm, "end": v(-1.34, 13.48) * mm});
            skLineSegment(sketch, "E3054", {"start": v(-1.34, 13.48) * mm, "end": v(-1.2, 13.42) * mm});
            skLineSegment(sketch, "E3055", {"start": v(-1.2, 13.42) * mm, "end": v(-1.07, 13.37) * mm});
            skLineSegment(sketch, "E3056", {"start": v(-1.07, 13.37) * mm, "end": v(-0.93, 13.33) * mm});
            skLineSegment(sketch, "E3057", {"start": v(-0.93, 13.33) * mm, "end": v(-0.78, 13.3) * mm});
            skLineSegment(sketch, "E3058", {"start": v(-0.78, 13.3) * mm, "end": v(-0.62, 13.29) * mm});
            skLineSegment(sketch, "E3059", {"start": v(-0.62, 13.29) * mm, "end": v(-0.34, 13.28) * mm});
            skLineSegment(sketch, "E3060", {"start": v(-0.34, 13.28) * mm, "end": v(-0.04, 13.3) * mm});
            skLineSegment(sketch, "E3061", {"start": v(-0.04, 13.3) * mm, "end": v(0.27, 13.35) * mm});
            skLineSegment(sketch, "E3062", {"start": v(0.27, 13.35) * mm, "end": v(0.58, 13.41) * mm});
            skLineSegment(sketch, "E3063", {"start": v(0.58, 13.41) * mm, "end": v(1.2, 13.56) * mm});
            skLineSegment(sketch, "E3064", {"start": v(1.2, 13.56) * mm, "end": v(1.77, 13.71) * mm});
            skLineSegment(sketch, "E3065", {"start": v(1.77, 13.71) * mm, "end": v(2.25, 13.84) * mm});
            skLineSegment(sketch, "E3066", {"start": v(2.25, 13.84) * mm, "end": v(2.73, 13.94) * mm});
            skLineSegment(sketch, "E3067", {"start": v(2.73, 13.94) * mm, "end": v(3.2, 14.04) * mm});
            skLineSegment(sketch, "E3068", {"start": v(3.2, 14.04) * mm, "end": v(3.68, 14.11) * mm});
            skLineSegment(sketch, "E3069", {"start": v(3.68, 14.11) * mm, "end": v(4.16, 14.17) * mm});
            skLineSegment(sketch, "E3070", {"start": v(4.16, 14.17) * mm, "end": v(4.65, 14.2) * mm});
            skLineSegment(sketch, "E3071", {"start": v(4.65, 14.2) * mm, "end": v(5.14, 14.2) * mm});
            skLineSegment(sketch, "E3072", {"start": v(5.14, 14.2) * mm, "end": v(5.39, 14.2) * mm});
            skLineSegment(sketch, "E3073", {"start": v(5.39, 14.2) * mm, "end": v(5.64, 14.18) * mm});
            skLineSegment(sketch, "E3074", {"start": v(5.64, 14.18) * mm, "end": v(5.94, 14.15) * mm});
            skLineSegment(sketch, "E3075", {"start": v(5.94, 14.15) * mm, "end": v(6.24, 14.1) * mm});
            skLineSegment(sketch, "E3076", {"start": v(6.24, 14.1) * mm, "end": v(6.53, 14.05) * mm});
            skLineSegment(sketch, "E3077", {"start": v(6.53, 14.05) * mm, "end": v(6.81, 13.98) * mm});
            skLineSegment(sketch, "E3078", {"start": v(6.81, 13.98) * mm, "end": v(7.1, 13.9) * mm});
            skLineSegment(sketch, "E3079", {"start": v(7.1, 13.9) * mm, "end": v(7.37, 13.8) * mm});
            skLineSegment(sketch, "E3080", {"start": v(7.37, 13.8) * mm, "end": v(7.65, 13.68) * mm});
            skLineSegment(sketch, "E3081", {"start": v(7.65, 13.68) * mm, "end": v(7.92, 13.55) * mm});
            skLineSegment(sketch, "E3082", {"start": v(7.92, 13.55) * mm, "end": v(8.26, 13.36) * mm});
            skLineSegment(sketch, "E3083", {"start": v(8.26, 13.36) * mm, "end": v(8.58, 13.16) * mm});
            skLineSegment(sketch, "E3084", {"start": v(8.58, 13.16) * mm, "end": v(8.9, 12.95) * mm});
            skLineSegment(sketch, "E3085", {"start": v(8.9, 12.95) * mm, "end": v(9.23, 12.75) * mm});
            skLineSegment(sketch, "E3086", {"start": v(9.23, 12.75) * mm, "end": v(9.4, 12.65) * mm});
            skLineSegment(sketch, "E3087", {"start": v(9.4, 12.65) * mm, "end": v(9.57, 12.56) * mm});
            skLineSegment(sketch, "E3088", {"start": v(9.57, 12.56) * mm, "end": v(9.73, 12.5) * mm});
            skLineSegment(sketch, "E3089", {"start": v(9.73, 12.5) * mm, "end": v(9.9, 12.46) * mm});
            skLineSegment(sketch, "E3090", {"start": v(9.9, 12.46) * mm, "end": v(10.06, 12.43) * mm});
            skLineSegment(sketch, "E3091", {"start": v(10.06, 12.43) * mm, "end": v(10.23, 12.42) * mm});
            skLineSegment(sketch, "E3092", {"start": v(10.23, 12.42) * mm, "end": v(10.42, 12.42) * mm});
            skLineSegment(sketch, "E3093", {"start": v(10.42, 12.42) * mm, "end": v(10.63, 12.43) * mm});
            skLineSegment(sketch, "E3094", {"start": v(10.63, 12.43) * mm, "end": v(10.78, 12.46) * mm});
            skLineSegment(sketch, "E3095", {"start": v(10.78, 12.46) * mm, "end": v(10.93, 12.49) * mm});
            skLineSegment(sketch, "E3096", {"start": v(10.93, 12.49) * mm, "end": v(11.07, 12.53) * mm});
            skLineSegment(sketch, "E3097", {"start": v(11.07, 12.53) * mm, "end": v(11.2, 12.58) * mm});
            skLineSegment(sketch, "E3098", {"start": v(11.2, 12.58) * mm, "end": v(11.34, 12.64) * mm});
            skLineSegment(sketch, "E3099", {"start": v(11.34, 12.64) * mm, "end": v(11.47, 12.7) * mm});
            skLineSegment(sketch, "E3100", {"start": v(11.47, 12.7) * mm, "end": v(11.59, 12.78) * mm});
            skLineSegment(sketch, "E3101", {"start": v(11.59, 12.78) * mm, "end": v(11.7, 12.87) * mm});
            skLineSegment(sketch, "E3102", {"start": v(11.7, 12.87) * mm, "end": v(11.81, 12.96) * mm});
            skLineSegment(sketch, "E3103", {"start": v(11.81, 12.96) * mm, "end": v(11.92, 13.05) * mm});
            skLineSegment(sketch, "E3104", {"start": v(11.92, 13.05) * mm, "end": v(12.01, 13.15) * mm});
            skLineSegment(sketch, "E3105", {"start": v(12.01, 13.15) * mm, "end": v(12.1, 13.26) * mm});
            skLineSegment(sketch, "E3106", {"start": v(12.1, 13.26) * mm, "end": v(12.18, 13.37) * mm});
            skLineSegment(sketch, "E3107", {"start": v(12.18, 13.37) * mm, "end": v(12.25, 13.48) * mm});
            skLineSegment(sketch, "E3108", {"start": v(12.25, 13.48) * mm, "end": v(12.31, 13.6) * mm});
            skLineSegment(sketch, "E3109", {"start": v(12.31, 13.6) * mm, "end": v(12.37, 13.73) * mm});
            skLineSegment(sketch, "E3110", {"start": v(12.37, 13.73) * mm, "end": v(12.42, 13.85) * mm});
            skLineSegment(sketch, "E3111", {"start": v(12.42, 13.85) * mm, "end": v(12.45, 13.98) * mm});
            skLineSegment(sketch, "E3112", {"start": v(12.45, 13.98) * mm, "end": v(12.48, 14.1) * mm});
            skLineSegment(sketch, "E3113", {"start": v(12.48, 14.1) * mm, "end": v(12.5, 14.24) * mm});
            skLineSegment(sketch, "E3114", {"start": v(12.5, 14.24) * mm, "end": v(12.51, 14.37) * mm});
            skLineSegment(sketch, "E3115", {"start": v(12.51, 14.37) * mm, "end": v(12.51, 14.5) * mm});
            skLineSegment(sketch, "E3116", {"start": v(12.51, 14.5) * mm, "end": v(12.5, 14.63) * mm});
            skLineSegment(sketch, "E3117", {"start": v(12.5, 14.63) * mm, "end": v(12.48, 14.76) * mm});
            skLineSegment(sketch, "E3118", {"start": v(12.48, 14.76) * mm, "end": v(12.45, 14.9) * mm});
            skLineSegment(sketch, "E3119", {"start": v(12.45, 14.9) * mm, "end": v(12.4, 15.02) * mm});
            skLineSegment(sketch, "E3120", {"start": v(12.4, 15.02) * mm, "end": v(12.35, 15.14) * mm});
            skLineSegment(sketch, "E3121", {"start": v(12.35, 15.14) * mm, "end": v(12.28, 15.26) * mm});
            skLineSegment(sketch, "E3122", {"start": v(12.28, 15.26) * mm, "end": v(12.2, 15.38) * mm});
            skLineSegment(sketch, "E3123", {"start": v(12.2, 15.38) * mm, "end": v(12.11, 15.5) * mm});
            skLineSegment(sketch, "E3124", {"start": v(12.11, 15.5) * mm, "end": v(12, 15.6) * mm});
            skLineSegment(sketch, "E3125", {"start": v(12, 15.6) * mm, "end": v(11.9, 15.72) * mm});
            skLineSegment(sketch, "E3126", {"start": v(11.9, 15.72) * mm, "end": v(11.62, 15.96) * mm});
            skLineSegment(sketch, "E3127", {"start": v(11.62, 15.96) * mm, "end": v(11.34, 16.21) * mm});
            skLineSegment(sketch, "E3128", {"start": v(11.34, 16.21) * mm, "end": v(11.08, 16.48) * mm});
            skLineSegment(sketch, "E3129", {"start": v(11.08, 16.48) * mm, "end": v(10.82, 16.76) * mm});
            skLineSegment(sketch, "E3130", {"start": v(10.82, 16.76) * mm, "end": v(10.32, 17.32) * mm});
            skLineSegment(sketch, "E3131", {"start": v(10.32, 17.32) * mm, "end": v(9.84, 17.89) * mm});
            skLineSegment(sketch, "E3132", {"start": v(9.84, 17.89) * mm, "end": v(9.26, 18.6) * mm});
            skLineSegment(sketch, "E3133", {"start": v(9.26, 18.6) * mm, "end": v(8.7, 19.32) * mm});
            skLineSegment(sketch, "E3134", {"start": v(8.7, 19.32) * mm, "end": v(8.14, 20.06) * mm});
            skLineSegment(sketch, "E3135", {"start": v(8.14, 20.06) * mm, "end": v(7.6, 20.8) * mm});
            skLineSegment(sketch, "E3136", {"start": v(7.6, 20.8) * mm, "end": v(6.72, 22.04) * mm});
            skLineSegment(sketch, "E3137", {"start": v(6.72, 22.04) * mm, "end": v(6.28, 22.68) * mm});
            skLineSegment(sketch, "E3138", {"start": v(6.28, 22.68) * mm, "end": v(5.85, 23.33) * mm});
            skLineSegment(sketch, "E3139", {"start": v(5.85, 23.33) * mm, "end": v(5.42, 23.98) * mm});
            skLineSegment(sketch, "E3140", {"start": v(5.42, 23.98) * mm, "end": v(5.01, 24.64) * mm});
            skLineSegment(sketch, "E3141", {"start": v(5.01, 24.64) * mm, "end": v(4.62, 25.3) * mm});
            skLineSegment(sketch, "E3142", {"start": v(4.62, 25.3) * mm, "end": v(4.25, 25.96) * mm});
            skLineSegment(sketch, "E3143", {"start": v(4.25, 25.96) * mm, "end": v(3.85, 26.7) * mm});
            skLineSegment(sketch, "E3144", {"start": v(3.85, 26.7) * mm, "end": v(3.46, 27.45) * mm});
            skLineSegment(sketch, "E3145", {"start": v(3.46, 27.45) * mm, "end": v(3.27, 27.79) * mm});
            skLineSegment(sketch, "E3146", {"start": v(3.27, 27.79) * mm, "end": v(3.17, 27.96) * mm});
            skLineSegment(sketch, "E3147", {"start": v(3.17, 27.96) * mm, "end": v(3.06, 28.12) * mm});
            skLineSegment(sketch, "E3148", {"start": v(3.06, 28.12) * mm, "end": v(2.92, 28.28) * mm});
            skLineSegment(sketch, "E3149", {"start": v(2.92, 28.28) * mm, "end": v(2.76, 28.45) * mm});
            skLineSegment(sketch, "E3150", {"start": v(2.76, 28.45) * mm, "end": v(2.58, 28.61) * mm});
            skLineSegment(sketch, "E3151", {"start": v(2.58, 28.61) * mm, "end": v(2.39, 28.78) * mm});
            skLineSegment(sketch, "E3152", {"start": v(2.39, 28.78) * mm, "end": v(2, 29.09) * mm});
            skLineSegment(sketch, "E3153", {"start": v(2, 29.09) * mm, "end": v(1.63, 29.36) * mm});
            skLineSegment(sketch, "E3154", {"start": v(1.63, 29.36) * mm, "end": v(1.29, 29.63) * mm});
            skLineSegment(sketch, "E3155", {"start": v(1.29, 29.63) * mm, "end": v(0.89, 29.93) * mm});
            skLineSegment(sketch, "E3156", {"start": v(0.89, 29.93) * mm, "end": v(0.68, 30.07) * mm});
            skLineSegment(sketch, "E3157", {"start": v(0.68, 30.07) * mm, "end": v(0.47, 30.2) * mm});
            skLineSegment(sketch, "E3158", {"start": v(0.47, 30.2) * mm, "end": v(0.27, 30.3) * mm});
            skLineSegment(sketch, "E3159", {"start": v(0.27, 30.3) * mm, "end": v(0.08, 30.38) * mm});
            skLineSegment(sketch, "E3160", {"start": v(0.08, 30.38) * mm, "end": v(0, 30.4) * mm});
            skLineSegment(sketch, "E3161", {"start": v(0, 30.4) * mm, "end": v(-0.1, 30.42) * mm});
            skLineSegment(sketch, "E3162", {"start": v(-0.1, 30.42) * mm, "end": v(-0.29, 30.42) * mm});
            skLineSegment(sketch, "E3163", {"start": v(-0.29, 30.42) * mm, "end": v(-0.48, 30.4) * mm});
            skLineSegment(sketch, "E3164", {"start": v(-0.48, 30.4) * mm, "end": v(-0.67, 30.35) * mm});
            skLineSegment(sketch, "E3165", {"start": v(-0.67, 30.35) * mm, "end": v(-0.85, 30.29) * mm});
            skLineSegment(sketch, "E3166", {"start": v(-0.85, 30.29) * mm, "end": v(-1.03, 30.21) * mm});
            skLineSegment(sketch, "E3167", {"start": v(-1.03, 30.21) * mm, "end": v(-1.37, 30.05) * mm});
            skLineSegment(sketch, "E3168", {"start": v(-1.37, 30.05) * mm, "end": v(-1.68, 29.88) * mm});
            skLineSegment(sketch, "E3169", {"start": v(-1.68, 29.88) * mm, "end": v(-2.16, 29.62) * mm});
            skLineSegment(sketch, "E3170", {"start": v(-2.16, 29.62) * mm, "end": v(-2.4, 29.48) * mm});
            skLineSegment(sketch, "E3171", {"start": v(-2.4, 29.48) * mm, "end": v(-2.62, 29.35) * mm});
            skLineSegment(sketch, "E3172", {"start": v(-2.62, 29.35) * mm, "end": v(-2.79, 29.23) * mm});
            skLineSegment(sketch, "E3173", {"start": v(-2.79, 29.23) * mm, "end": v(-2.85, 29.18) * mm});
            skLineSegment(sketch, "E3174", {"start": v(-2.85, 29.18) * mm, "end": v(-2.9, 29.13) * mm});
            skLineSegment(sketch, "E3175", {"start": v(-2.9, 29.13) * mm, "end": v(-2.96, 29.02) * mm});
            skLineSegment(sketch, "E3176", {"start": v(-2.96, 29.02) * mm, "end": v(-3.02, 28.87) * mm});
            skLineSegment(sketch, "E3177", {"start": v(-3.02, 28.87) * mm, "end": v(-3.13, 28.6) * mm});
            skLineSegment(sketch, "E3178", {"start": v(-3.13, 28.6) * mm, "end": v(-3.46, 27.78) * mm});
            skLineSegment(sketch, "E3179", {"start": v(-3.46, 27.78) * mm, "end": v(-3.64, 27.38) * mm});
            skLineSegment(sketch, "E3180", {"start": v(-3.64, 27.38) * mm, "end": v(-3.82, 26.97) * mm});
            skLineSegment(sketch, "E3181", {"start": v(-3.82, 26.97) * mm, "end": v(-4.32, 25.9) * mm});
            skLineSegment(sketch, "E3182", {"start": v(-4.32, 25.9) * mm, "end": v(-4.84, 24.86) * mm});
            skLineSegment(sketch, "E3183", {"start": v(-4.84, 24.86) * mm, "end": v(-5.1, 24.35) * mm});
            skLineSegment(sketch, "E3184", {"start": v(-5.1, 24.35) * mm, "end": v(-5.37, 23.85) * mm});
            skLineSegment(sketch, "E3185", {"start": v(-5.37, 23.85) * mm, "end": v(-5.65, 23.35) * mm});
            skLineSegment(sketch, "E3186", {"start": v(-5.65, 23.35) * mm, "end": v(-5.93, 22.85) * mm});
            skLineSegment(sketch, "E3187", {"start": v(-5.93, 22.85) * mm, "end": v(-6.22, 22.36) * mm});
            skLineSegment(sketch, "E3188", {"start": v(-6.22, 22.36) * mm, "end": v(-6.52, 21.88) * mm});
            skLineSegment(sketch, "E3189", {"start": v(-6.52, 21.88) * mm, "end": v(-6.83, 21.4) * mm});
            skLineSegment(sketch, "E3190", {"start": v(-6.83, 21.4) * mm, "end": v(-7.15, 20.92) * mm});
            skLineSegment(sketch, "E3191", {"start": v(-7.15, 20.92) * mm, "end": v(-7.48, 20.45) * mm});
            skLineSegment(sketch, "E3192", {"start": v(-7.48, 20.45) * mm, "end": v(-7.83, 19.98) * mm});
            skLineSegment(sketch, "E3193", {"start": v(-7.83, 19.98) * mm, "end": v(-8.2, 19.51) * mm});
            skLineSegment(sketch, "E3194", {"start": v(-8.2, 19.51) * mm, "end": v(-8.56, 19.05) * mm});
            skLineSegment(sketch, "E3195", {"start": v(-8.56, 19.05) * mm, "end": v(-9.55, 17.9) * mm});
            skLineSegment(sketch, "E3196", {"start": v(-9.55, 17.9) * mm, "end": v(-10.54, 16.75) * mm});
            skLineSegment(sketch, "E3197", {"start": v(-10.54, 16.75) * mm, "end": v(-11.04, 16.17) * mm});
            skLineSegment(sketch, "E3198", {"start": v(-11.04, 16.17) * mm, "end": v(-11.53, 15.6) * mm});
            skLineSegment(sketch, "E3199", {"start": v(-11.53, 15.6) * mm, "end": v(-12.01, 15) * mm});
            skLineSegment(sketch, "E3200", {"start": v(-12.01, 15) * mm, "end": v(-12.49, 14.4) * mm});
            skLineSegment(sketch, "E3201", {"start": v(-12.49, 14.4) * mm, "end": v(-12.83, 14) * mm});
            skLineSegment(sketch, "E3202", {"start": v(-12.83, 14) * mm, "end": v(-13.18, 13.6) * mm});
            skLineSegment(sketch, "E3203", {"start": v(-13.18, 13.6) * mm, "end": v(-13.54, 13.22) * mm});
            skLineSegment(sketch, "E3204", {"start": v(-13.54, 13.22) * mm, "end": v(-13.88, 12.83) * mm});
            skLineSegment(sketch, "E3205", {"start": v(-13.88, 12.83) * mm, "end": v(-14.01, 12.67) * mm});
            skLineSegment(sketch, "E3206", {"start": v(-14.01, 12.67) * mm, "end": v(-14.14, 12.5) * mm});
            skLineSegment(sketch, "E3207", {"start": v(-14.14, 12.5) * mm, "end": v(-14.25, 12.34) * mm});
            skLineSegment(sketch, "E3208", {"start": v(-14.25, 12.34) * mm, "end": v(-14.35, 12.16) * mm});
            skLineSegment(sketch, "E3209", {"start": v(5.03, 32.02) * mm, "end": v(5, 32.23) * mm});
            skLineSegment(sketch, "E3210", {"start": v(5, 32.23) * mm, "end": v(4.97, 32.45) * mm});
            skLineSegment(sketch, "E3211", {"start": v(4.97, 32.45) * mm, "end": v(4.87, 32.9) * mm});
            skLineSegment(sketch, "E3212", {"start": v(4.87, 32.9) * mm, "end": v(4.76, 33.32) * mm});
            skLineSegment(sketch, "E3213", {"start": v(4.76, 33.32) * mm, "end": v(4.67, 33.63) * mm});
            skLineSegment(sketch, "E3214", {"start": v(4.67, 33.63) * mm, "end": v(4.5, 34.28) * mm});
            skLineSegment(sketch, "E3215", {"start": v(4.5, 34.28) * mm, "end": v(4.41, 34.6) * mm});
            skLineSegment(sketch, "E3216", {"start": v(4.41, 34.6) * mm, "end": v(4.34, 34.93) * mm});
            skLineSegment(sketch, "E3217", {"start": v(4.34, 34.93) * mm, "end": v(4.29, 35.25) * mm});
            skLineSegment(sketch, "E3218", {"start": v(4.29, 35.25) * mm, "end": v(4.24, 35.58) * mm});
            skLineSegment(sketch, "E3219", {"start": v(4.24, 35.58) * mm, "end": v(4.21, 35.9) * mm});
            skLineSegment(sketch, "E3220", {"start": v(4.21, 35.9) * mm, "end": v(4.2, 36.22) * mm});
            skLineSegment(sketch, "E3221", {"start": v(4.2, 36.22) * mm, "end": v(4.21, 36.54) * mm});
            skLineSegment(sketch, "E3222", {"start": v(4.21, 36.54) * mm, "end": v(4.25, 36.85) * mm});
            skLineSegment(sketch, "E3223", {"start": v(4.25, 36.85) * mm, "end": v(4.3, 37.16) * mm});
            skLineSegment(sketch, "E3224", {"start": v(4.3, 37.16) * mm, "end": v(4.4, 37.47) * mm});
            skLineSegment(sketch, "E3225", {"start": v(4.4, 37.47) * mm, "end": v(4.45, 37.62) * mm});
            skLineSegment(sketch, "E3226", {"start": v(4.45, 37.62) * mm, "end": v(4.52, 37.77) * mm});
            skLineSegment(sketch, "E3227", {"start": v(4.52, 37.77) * mm, "end": v(4.59, 37.92) * mm});
            skLineSegment(sketch, "E3228", {"start": v(4.59, 37.92) * mm, "end": v(4.67, 38.07) * mm});
            skLineSegment(sketch, "E3229", {"start": v(4.67, 38.07) * mm, "end": v(4.76, 38.21) * mm});
            skLineSegment(sketch, "E3230", {"start": v(4.76, 38.21) * mm, "end": v(4.85, 38.36) * mm});
            skLineSegment(sketch, "E3231", {"start": v(4.85, 38.36) * mm, "end": v(4.96, 38.5) * mm});
            skLineSegment(sketch, "E3232", {"start": v(4.96, 38.5) * mm, "end": v(5.08, 38.64) * mm});
            skLineSegment(sketch, "E3233", {"start": v(5.08, 38.64) * mm, "end": v(5.33, 38.9) * mm});
            skLineSegment(sketch, "E3234", {"start": v(5.33, 38.9) * mm, "end": v(5.6, 39.15) * mm});
            skLineSegment(sketch, "E3235", {"start": v(5.6, 39.15) * mm, "end": v(5.88, 39.39) * mm});
            skLineSegment(sketch, "E3236", {"start": v(5.88, 39.39) * mm, "end": v(6.18, 39.61) * mm});
            skLineSegment(sketch, "E3237", {"start": v(6.18, 39.61) * mm, "end": v(6.79, 40.03) * mm});
            skLineSegment(sketch, "E3238", {"start": v(6.79, 40.03) * mm, "end": v(7.4, 40.43) * mm});
            skLineSegment(sketch, "E3239", {"start": v(7.4, 40.43) * mm, "end": v(7.64, 40.58) * mm});
            skLineSegment(sketch, "E3240", {"start": v(7.64, 40.58) * mm, "end": v(7.94, 40.77) * mm});
            skLineSegment(sketch, "E3241", {"start": v(7.94, 40.77) * mm, "end": v(8.26, 41) * mm});
            skLineSegment(sketch, "E3242", {"start": v(8.26, 41) * mm, "end": v(8.42, 41.13) * mm});
            skLineSegment(sketch, "E3243", {"start": v(8.42, 41.13) * mm, "end": v(8.57, 41.26) * mm});
            skLineSegment(sketch, "E3244", {"start": v(8.57, 41.26) * mm, "end": v(8.48, 41.27) * mm});
            skLineSegment(sketch, "E3245", {"start": v(8.48, 41.27) * mm, "end": v(8.11, 41.33) * mm});
            skLineSegment(sketch, "E3246", {"start": v(8.11, 41.33) * mm, "end": v(7.74, 41.37) * mm});
            skLineSegment(sketch, "E3247", {"start": v(7.74, 41.37) * mm, "end": v(6.98, 41.43) * mm});
            skLineSegment(sketch, "E3248", {"start": v(6.98, 41.43) * mm, "end": v(6.48, 41.48) * mm});
            skLineSegment(sketch, "E3249", {"start": v(6.48, 41.48) * mm, "end": v(5.97, 41.54) * mm});
            skLineSegment(sketch, "E3250", {"start": v(5.97, 41.54) * mm, "end": v(5.47, 41.62) * mm});
            skLineSegment(sketch, "E3251", {"start": v(5.47, 41.62) * mm, "end": v(4.97, 41.73) * mm});
            skLineSegment(sketch, "E3252", {"start": v(4.97, 41.73) * mm, "end": v(4.65, 41.81) * mm});
            skLineSegment(sketch, "E3253", {"start": v(4.65, 41.81) * mm, "end": v(4.33, 41.92) * mm});
            skLineSegment(sketch, "E3254", {"start": v(4.33, 41.92) * mm, "end": v(4.03, 42.04) * mm});
            skLineSegment(sketch, "E3255", {"start": v(4.03, 42.04) * mm, "end": v(3.74, 42.2) * mm});
            skLineSegment(sketch, "E3256", {"start": v(3.74, 42.2) * mm, "end": v(3.47, 42.37) * mm});
            skLineSegment(sketch, "E3257", {"start": v(3.47, 42.37) * mm, "end": v(3.2, 42.57) * mm});
            skLineSegment(sketch, "E3258", {"start": v(3.2, 42.57) * mm, "end": v(2.97, 42.79) * mm});
            skLineSegment(sketch, "E3259", {"start": v(2.97, 42.79) * mm, "end": v(2.74, 43.04) * mm});
            skLineSegment(sketch, "E3260", {"start": v(2.74, 43.04) * mm, "end": v(2.58, 43.24) * mm});
            skLineSegment(sketch, "E3261", {"start": v(2.58, 43.24) * mm, "end": v(2.44, 43.44) * mm});
            skLineSegment(sketch, "E3262", {"start": v(2.44, 43.44) * mm, "end": v(2.31, 43.66) * mm});
            skLineSegment(sketch, "E3263", {"start": v(2.31, 43.66) * mm, "end": v(2.2, 43.87) * mm});
            skLineSegment(sketch, "E3264", {"start": v(2.2, 43.87) * mm, "end": v(2.1, 44.1) * mm});
            skLineSegment(sketch, "E3265", {"start": v(2.1, 44.1) * mm, "end": v(2, 44.33) * mm});
            skLineSegment(sketch, "E3266", {"start": v(2, 44.33) * mm, "end": v(1.83, 44.8) * mm});
            skLineSegment(sketch, "E3267", {"start": v(1.83, 44.8) * mm, "end": v(1.69, 45.27) * mm});
            skLineSegment(sketch, "E3268", {"start": v(1.69, 45.27) * mm, "end": v(1.55, 45.75) * mm});
            skLineSegment(sketch, "E3269", {"start": v(1.55, 45.75) * mm, "end": v(1.43, 46.23) * mm});
            skLineSegment(sketch, "E3270", {"start": v(1.43, 46.23) * mm, "end": v(1.3, 46.71) * mm});
            skLineSegment(sketch, "E3271", {"start": v(1.3, 46.71) * mm, "end": v(1.18, 47.06) * mm});
            skLineSegment(sketch, "E3272", {"start": v(1.18, 47.06) * mm, "end": v(1.02, 47.53) * mm});
            skLineSegment(sketch, "E3273", {"start": v(1.02, 47.53) * mm, "end": v(0.72, 46.91) * mm});
            skLineSegment(sketch, "E3274", {"start": v(0.72, 46.91) * mm, "end": v(0.5, 46.45) * mm});
            skLineSegment(sketch, "E3275", {"start": v(0.5, 46.45) * mm, "end": v(0.15, 45.64) * mm});
            skLineSegment(sketch, "E3276", {"start": v(0.15, 45.64) * mm, "end": v(-0.05, 45.2) * mm});
            skLineSegment(sketch, "E3277", {"start": v(-0.05, 45.2) * mm, "end": v(-0.26, 44.74) * mm});
            skLineSegment(sketch, "E3278", {"start": v(-0.26, 44.74) * mm, "end": v(-0.5, 44.3) * mm});
            skLineSegment(sketch, "E3279", {"start": v(-0.5, 44.3) * mm, "end": v(-0.62, 44.1) * mm});
            skLineSegment(sketch, "E3280", {"start": v(-0.62, 44.1) * mm, "end": v(-0.74, 43.9) * mm});
            skLineSegment(sketch, "E3281", {"start": v(-0.74, 43.9) * mm, "end": v(-0.87, 43.7) * mm});
            skLineSegment(sketch, "E3282", {"start": v(-0.87, 43.7) * mm, "end": v(-1, 43.53) * mm});
            skLineSegment(sketch, "E3283", {"start": v(-1, 43.53) * mm, "end": v(-1.14, 43.37) * mm});
            skLineSegment(sketch, "E3284", {"start": v(-1.14, 43.37) * mm, "end": v(-1.29, 43.22) * mm});
            skLineSegment(sketch, "E3285", {"start": v(-1.29, 43.22) * mm, "end": v(-1.52, 43.02) * mm});
            skLineSegment(sketch, "E3286", {"start": v(-1.52, 43.02) * mm, "end": v(-1.77, 42.85) * mm});
            skLineSegment(sketch, "E3287", {"start": v(-1.77, 42.85) * mm, "end": v(-2.03, 42.7) * mm});
            skLineSegment(sketch, "E3288", {"start": v(-2.03, 42.7) * mm, "end": v(-2.3, 42.58) * mm});
            skLineSegment(sketch, "E3289", {"start": v(-2.3, 42.58) * mm, "end": v(-2.58, 42.47) * mm});
            skLineSegment(sketch, "E3290", {"start": v(-2.58, 42.47) * mm, "end": v(-2.87, 42.39) * mm});
            skLineSegment(sketch, "E3291", {"start": v(-2.87, 42.39) * mm, "end": v(-3.16, 42.32) * mm});
            skLineSegment(sketch, "E3292", {"start": v(-3.16, 42.32) * mm, "end": v(-3.45, 42.27) * mm});
            skLineSegment(sketch, "E3293", {"start": v(-3.45, 42.27) * mm, "end": v(-3.75, 42.24) * mm});
            skLineSegment(sketch, "E3294", {"start": v(-3.75, 42.24) * mm, "end": v(-4.06, 42.22) * mm});
            skLineSegment(sketch, "E3295", {"start": v(-4.06, 42.22) * mm, "end": v(-4.36, 42.2) * mm});
            skLineSegment(sketch, "E3296", {"start": v(-4.36, 42.2) * mm, "end": v(-4.66, 42.2) * mm});
            skLineSegment(sketch, "E3297", {"start": v(-4.66, 42.2) * mm, "end": v(-5.27, 42.22) * mm});
            skLineSegment(sketch, "E3298", {"start": v(-5.27, 42.22) * mm, "end": v(-5.87, 42.26) * mm});
            skLineSegment(sketch, "E3299", {"start": v(-5.87, 42.26) * mm, "end": v(-6.58, 42.3) * mm});
            skLineSegment(sketch, "E3300", {"start": v(-6.58, 42.3) * mm, "end": v(-6.96, 42.32) * mm});
            skLineSegment(sketch, "E3301", {"start": v(-6.96, 42.32) * mm, "end": v(-7.34, 42.32) * mm});
            skLineSegment(sketch, "E3302", {"start": v(-7.34, 42.32) * mm, "end": v(-7.08, 42.06) * mm});
            skLineSegment(sketch, "E3303", {"start": v(-7.08, 42.06) * mm, "end": v(-6.83, 41.83) * mm});
            skLineSegment(sketch, "E3304", {"start": v(-6.83, 41.83) * mm, "end": v(-6.41, 41.47) * mm});
            skLineSegment(sketch, "E3305", {"start": v(-6.41, 41.47) * mm, "end": v(-6.07, 41.2) * mm});
            skLineSegment(sketch, "E3306", {"start": v(-6.07, 41.2) * mm, "end": v(-5.72, 40.94) * mm});
            skLineSegment(sketch, "E3307", {"start": v(-5.72, 40.94) * mm, "end": v(-5.38, 40.67) * mm});
            skLineSegment(sketch, "E3308", {"start": v(-5.38, 40.67) * mm, "end": v(-5.05, 40.38) * mm});
            skLineSegment(sketch, "E3309", {"start": v(-5.05, 40.38) * mm, "end": v(-4.82, 40.14) * mm});
            skLineSegment(sketch, "E3310", {"start": v(-4.82, 40.14) * mm, "end": v(-4.6, 39.9) * mm});
            skLineSegment(sketch, "E3311", {"start": v(-4.6, 39.9) * mm, "end": v(-4.42, 39.65) * mm});
            skLineSegment(sketch, "E3312", {"start": v(-4.42, 39.65) * mm, "end": v(-4.25, 39.4) * mm});
            skLineSegment(sketch, "E3313", {"start": v(-4.25, 39.4) * mm, "end": v(-4.1, 39.13) * mm});
            skLineSegment(sketch, "E3314", {"start": v(-4.1, 39.13) * mm, "end": v(-3.97, 38.86) * mm});
            skLineSegment(sketch, "E3315", {"start": v(-3.97, 38.86) * mm, "end": v(-3.86, 38.59) * mm});
            skLineSegment(sketch, "E3316", {"start": v(-3.86, 38.59) * mm, "end": v(-3.78, 38.3) * mm});
            skLineSegment(sketch, "E3317", {"start": v(-3.78, 38.3) * mm, "end": v(-3.71, 38.02) * mm});
            skLineSegment(sketch, "E3318", {"start": v(-3.71, 38.02) * mm, "end": v(-3.67, 37.73) * mm});
            skLineSegment(sketch, "E3319", {"start": v(-3.67, 37.73) * mm, "end": v(-3.64, 37.43) * mm});
            skLineSegment(sketch, "E3320", {"start": v(-3.64, 37.43) * mm, "end": v(-3.64, 37.13) * mm});
            skLineSegment(sketch, "E3321", {"start": v(-3.64, 37.13) * mm, "end": v(-3.66, 36.82) * mm});
            skLineSegment(sketch, "E3322", {"start": v(-3.66, 36.82) * mm, "end": v(-3.7, 36.5) * mm});
            skLineSegment(sketch, "E3323", {"start": v(-3.7, 36.5) * mm, "end": v(-3.76, 36.19) * mm});
            skLineSegment(sketch, "E3324", {"start": v(-3.76, 36.19) * mm, "end": v(-3.84, 35.87) * mm});
            skLineSegment(sketch, "E3325", {"start": v(-3.84, 35.87) * mm, "end": v(-3.92, 35.62) * mm});
            skLineSegment(sketch, "E3326", {"start": v(-3.92, 35.62) * mm, "end": v(-4.04, 35.28) * mm});
            skLineSegment(sketch, "E3327", {"start": v(-4.04, 35.28) * mm, "end": v(-4.37, 34.44) * mm});
            skLineSegment(sketch, "E3328", {"start": v(-4.37, 34.44) * mm, "end": v(-4.55, 33.98) * mm});
            skLineSegment(sketch, "E3329", {"start": v(-4.55, 33.98) * mm, "end": v(-4.72, 33.53) * mm});
            skLineSegment(sketch, "E3330", {"start": v(-4.72, 33.53) * mm, "end": v(-4.86, 33.1) * mm});
            skLineSegment(sketch, "E3331", {"start": v(-4.86, 33.1) * mm, "end": v(-4.96, 32.71) * mm});
            skLineSegment(sketch, "E3332", {"start": v(-4.96, 32.71) * mm, "end": v(-4.54, 32.94) * mm});
            skLineSegment(sketch, "E3333", {"start": v(-4.54, 32.94) * mm, "end": v(-4.11, 33.19) * mm});
            skLineSegment(sketch, "E3334", {"start": v(-4.11, 33.19) * mm, "end": v(-3.47, 33.58) * mm});
            skLineSegment(sketch, "E3335", {"start": v(-3.47, 33.58) * mm, "end": v(-3.04, 33.84) * mm});
            skLineSegment(sketch, "E3336", {"start": v(-3.04, 33.84) * mm, "end": v(-2.6, 34.1) * mm});
            skLineSegment(sketch, "E3337", {"start": v(-2.6, 34.1) * mm, "end": v(-2.13, 34.33) * mm});
            skLineSegment(sketch, "E3338", {"start": v(-2.13, 34.33) * mm, "end": v(-1.9, 34.44) * mm});
            skLineSegment(sketch, "E3339", {"start": v(-1.9, 34.44) * mm, "end": v(-1.66, 34.54) * mm});
            skLineSegment(sketch, "E3340", {"start": v(-1.66, 34.54) * mm, "end": v(-1.42, 34.63) * mm});
            skLineSegment(sketch, "E3341", {"start": v(-1.42, 34.63) * mm, "end": v(-1.18, 34.71) * mm});
            skLineSegment(sketch, "E3342", {"start": v(-1.18, 34.71) * mm, "end": v(-0.93, 34.78) * mm});
            skLineSegment(sketch, "E3343", {"start": v(-0.93, 34.78) * mm, "end": v(-0.68, 34.83) * mm});
            skLineSegment(sketch, "E3344", {"start": v(-0.68, 34.83) * mm, "end": v(-0.43, 34.87) * mm});
            skLineSegment(sketch, "E3345", {"start": v(-0.43, 34.87) * mm, "end": v(-0.18, 34.9) * mm});
            skLineSegment(sketch, "E3346", {"start": v(-0.18, 34.9) * mm, "end": v(0.07, 34.9) * mm});
            skLineSegment(sketch, "E3347", {"start": v(0.07, 34.9) * mm, "end": v(0.33, 34.88) * mm});
            skLineSegment(sketch, "E3348", {"start": v(0.33, 34.88) * mm, "end": v(0.57, 34.85) * mm});
            skLineSegment(sketch, "E3349", {"start": v(0.57, 34.85) * mm, "end": v(0.8, 34.8) * mm});
            skLineSegment(sketch, "E3350", {"start": v(0.8, 34.8) * mm, "end": v(1.03, 34.73) * mm});
            skLineSegment(sketch, "E3351", {"start": v(1.03, 34.73) * mm, "end": v(1.26, 34.65) * mm});
            skLineSegment(sketch, "E3352", {"start": v(1.26, 34.65) * mm, "end": v(1.49, 34.55) * mm});
            skLineSegment(sketch, "E3353", {"start": v(1.49, 34.55) * mm, "end": v(1.7, 34.45) * mm});
            skLineSegment(sketch, "E3354", {"start": v(1.7, 34.45) * mm, "end": v(1.93, 34.33) * mm});
            skLineSegment(sketch, "E3355", {"start": v(1.93, 34.33) * mm, "end": v(2.14, 34.2) * mm});
            skLineSegment(sketch, "E3356", {"start": v(2.14, 34.2) * mm, "end": v(2.56, 33.92) * mm});
            skLineSegment(sketch, "E3357", {"start": v(2.56, 33.92) * mm, "end": v(2.97, 33.63) * mm});
            skLineSegment(sketch, "E3358", {"start": v(2.97, 33.63) * mm, "end": v(3.72, 33.03) * mm});
            skLineSegment(sketch, "E3359", {"start": v(3.72, 33.03) * mm, "end": v(4.29, 32.57) * mm});
            skLineSegment(sketch, "E3360", {"start": v(4.29, 32.57) * mm, "end": v(4.66, 32.28) * mm});
            skLineSegment(sketch, "E3361", {"start": v(4.66, 32.28) * mm, "end": v(5.03, 32.02) * mm});
            skSolve(sketch);
        }
        {
            var Q0;
            Q0 = qSketchRegion(id + "F0", true);
            var Q1;
            Q1=makeQuery(id+"F0.imprint","IMPRINT",FACE,{"disambiguationData":[TD([[makeQuery(id+"F0.imprint","IMPRINT",EDGE,{"derivedFrom":sQuery(id+"F0.wireOp",EDGE,"E0")}),-1.0]])]});
            extrude(context, id + "F1", {"entities" : qUnion([Q0, Q1]), "depth" : 25.4 * mm});
        }
    });
